FCSTD DOCUMENT  (FreeCAD 1.0R39109 (Git))
Label: boltNodeV2
License: All rights reserved
LicenseURL: http://en.wikipedia.org/wiki/All_rights_reserved
objects: Part::MultiFuse×223, Part::Feature×188, Sketcher::SketchObject×147, Part::FeaturePython×141, Part::Extrusion×117, Part::Cylinder×79, Part::Fillet×47, Part::Cut×44, App::Part×32, Part::Loft×14, Part::Compound×11, Part::MultiCommon×6, Part::Box×4
note: 1168 computed .brp shape members not serialized (recipe doc carries the construction recipe); baked Part::Feature solids carry a one-line shape summary decoded from their .brp

FEATURE [Part::Feature] Part__Feature020  label="Number Plate"
  Placement = pos=(0,-25,0) rot=(1,0,0;1.5708rad)
  shape: bbox 305.2 x 5.066 x 152.8 mm, 1758 faces (baked)
FEATURE [Part::Feature] Part__Feature021  label="Plate"
  shape: bbox 304.8 x 3.048 x 152.4 mm, 26 faces (baked)
FEATURE [App::Part] Assem1  label="backPlate"
  Group = -> [Part__Feature021]
  Origin = -> Origin
  Placement = pos=(20,6.5,1.5) rot=(0,0,1;0rad)
FEATURE [Part::Feature] Part__Feature023  label="COZIR"
  Placement = pos=(5.41029,2.97838,5.56111) rot=(0,0,1;0rad)
  shape: bbox 51.61 x 17 x 50.23 mm, 43 faces (baked)
FEATURE [Part::Feature] Part__Feature024  label="COMPOUND"
  shape: bbox 3.14 x 5 x 10.76 mm, 60 faces, 10 solids (baked)
FEATURE [App::Part] COZIR_Sensor_v2  label="COZIR Sensor v2"
  Group = -> [Part__Feature023,Part__Feature024]
  Origin = -> Origin001
  Placement = pos=(252.5,-22,91) rot=(0,1,0;4.71239rad)
FEATURE [Part::Feature] Part__Feature025  label="Board"
  shape: bbox 25.4 x 25.4 x 1.57 mm, 211 faces (baked)
FEATURE [Part::Feature] Part__Feature026  label="QFN24_4MM"
  Placement = pos=(12.1412,14.4526,1.57) rot=(0,0,1;3.92699rad)
  shape: bbox 5.657 x 5.657 x 0.9 mm, 172 faces (baked)
FEATURE [Part::Feature] Part__Feature027  label="Part 5"
  shape: bbox 0.48 x 0.6603 x 0.6 mm, 14 faces (baked)
FEATURE [Part::Feature] Part__Feature028  label="Part 6"
  shape: bbox 0.48 x 0.6603 x 0.6 mm, 14 faces (baked)
FEATURE [Part::Feature] Part__Feature029  label="Part 4"
  shape: bbox 0.48 x 0.6603 x 0.6 mm, 14 faces (baked)
FEATURE [Part::Feature] Part__Feature030  label="Part 3"
  shape: bbox 0.48 x 0.6603 x 0.6 mm, 14 faces (baked)
FEATURE [Part::Feature] Part__Feature031  label="Part 2"
  shape: bbox 0.48 x 0.6603 x 0.6 mm, 14 faces (baked)
FEATURE [Part::Feature] Part__Feature032  label="Part 1"
  shape: bbox 3 x 1.4 x 1 mm, 10 faces (baked)
FEATURE [Part::Feature] Part__Feature033  label="Pin1"
  shape: bbox 0.6224 x 1.252 x 1.252 mm, 37 faces (baked)
FEATURE [Part::Feature] Part__Feature034  label="Pin2"
  shape: bbox 0.6224 x 1.252 x 1.252 mm, 37 faces (baked)
FEATURE [Part::Feature] Part__Feature035  label="CeramicBody"
  shape: bbox 1.8 x 1.23 x 1.23 mm, 10 faces (baked)
FEATURE [Part::Feature] Part__Feature036  label="0603-NO (1)"
  Placement = pos=(23.241,6.223,1.57) rot=(0,0,1;0rad)
  shape: bbox 1.7 x 0.9 x 0.55 mm, 52 faces, 3 solids (baked)
FEATURE [Part::Feature] Part__Feature037  label="0603-NO (2)"
  Placement = pos=(13.3858,8.4328,1.57) rot=(0,0,1;0rad)
  shape: bbox 1.7 x 0.9 x 0.55 mm, 52 faces, 3 solids (baked)
FEATURE [Part::Feature] Part__Feature038  label="0603-NO (3)"
  Placement = pos=(1.905,18.923,1.57) rot=(0,0,1;3.14159rad)
  shape: bbox 1.7 x 0.9 x 0.55 mm, 52 faces, 3 solids (baked)
FEATURE [Part::Feature] Part__Feature039  label="Pin1 (1)"
  shape: bbox 0.6224 x 1.252 x 1.252 mm, 37 faces (baked)
FEATURE [Part::Feature] Part__Feature040  label="Pin2 (1)"
  shape: bbox 0.6224 x 1.252 x 1.252 mm, 37 faces (baked)
FEATURE [Part::Feature] Part__Feature041  label="CeramicBody (1)"
  shape: bbox 1.8 x 1.23 x 1.23 mm, 10 faces (baked)
FEATURE [Part::Feature] Part__Feature042  label="Pin1 (2)"
  shape: bbox 0.6224 x 1.252 x 1.252 mm, 37 faces (baked)
FEATURE [Part::Feature] Part__Feature043  label="Pin2 (2)"
  shape: bbox 0.6224 x 1.252 x 1.252 mm, 37 faces (baked)
FEATURE [Part::Feature] Part__Feature044  label="CeramicBody (2)"
  shape: bbox 1.8 x 1.23 x 1.23 mm, 10 faces (baked)
FEATURE [Part::Feature] Part__Feature045  label="CHIPLED_0603_NOOUTLINE"
  Placement = pos=(23.368,8.509,1.57) rot=(0,0,1;1.5708rad)
  shape: bbox 1.616 x 0.8 x 0.4 mm, 133 faces (baked)
FEATURE [Part::Feature] Part__Feature046  label="CHIPLED_0603_NOOUTLINE (1)"
  Placement = pos=(1.905,16.764,1.57) rot=(0,0,-1;1.5708rad)
  shape: bbox 1.616 x 0.8 x 0.4 mm, 133 faces (baked)
FEATURE [Part::Feature] Part__Feature047  label="JST_SH4"
  Placement = pos=(22.86,12.7,1.57) rot=(0,0,1;1.5708rad)
  shape: bbox 4.95 x 6 x 2.96 mm, 229 faces, 7 solids (baked)
FEATURE [Part::Feature] Part__Feature048  label="JST_SH4 (1)"
  Placement = pos=(2.54,12.7,1.57) rot=(0,0,-1;1.5708rad)
  shape: bbox 4.95 x 6 x 2.96 mm, 229 faces, 7 solids (baked)
FEATURE [Part::Feature] Part__Feature049  label="NEO3535_REVERSE"
  Placement = pos=(12.7,23.114,0) rot=(0,1,0;3.14159rad)
  shape: bbox 5.88 x 2.8 x 1.78 mm, 41 faces, 5 solids (baked)
FEATURE [Part::Feature] Part__Feature050  label="RESPACK_4X0603"
  Placement = pos=(22.86,18.415,1.57) rot=(0,0,1;3.14159rad)
  shape: bbox 3.2 x 1.6 x 0.61 mm, 172 faces (baked)
FEATURE [Part::Feature] Part__Feature051  label="SOT363"
  Placement = pos=(17.399,12.192,1.57) rot=(0,0,-1;1.5708rad)
  shape: bbox 2.208 x 2.208 x 1.121 mm, 178 faces, 4 solids (baked)
FEATURE [Sketcher::SketchObject] Sketch001
  ArcFitTolerance = 0
  FullyConstrained = true
  MakeInternals = false
  sketch-geometry (39):
    g0: LineSegment StartX=3 StartY=43.5 StartZ=0 EndX=3 EndY=34.5 EndZ=0
    g1: LineSegment StartX=3 StartY=34.5 StartZ=0 EndX=70.5 EndY=34.5 EndZ=0
    g2: LineSegment StartX=3 StartY=43.5 StartZ=0 EndX=10.5 EndY=43.5 EndZ=0
    g3: LineSegment StartX=3 StartY=71 StartZ=0 EndX=10.5 EndY=71 EndZ=0
    g4: LineSegment StartX=3 StartY=71 StartZ=0 EndX=3 EndY=80 EndZ=0
    g5: LineSegment StartX=70.5 StartY=80 StartZ=0 EndX=70.5 EndY=71 EndZ=0
    g6: LineSegment StartX=70.5 StartY=71 StartZ=0 EndX=62.5 EndY=71 EndZ=0
    g7: LineSegment StartX=62.5 StartY=71 StartZ=0 EndX=62.5 EndY=43 EndZ=0
    g8: LineSegment StartX=62.5 StartY=43 StartZ=0 EndX=70.5 EndY=43 EndZ=0
    g9: LineSegment StartX=70.5 StartY=43 StartZ=0 EndX=70.5 EndY=34.5 EndZ=0
    g10: GeomPoint [constr] X=70.5 Y=34.5 Z=0
    g11: GeomPoint [constr] X=70.5 Y=34.5 Z=0
    g12: GeomPoint [constr] X=70.5 Y=34.5 Z=0
    g13: GeomPoint [constr] X=70.5 Y=34.5 Z=0
    g14: GeomPoint [constr] X=70.5 Y=34.5 Z=0
    g15: LineSegment StartX=10.5 StartY=43.5 StartZ=0 EndX=10.5 EndY=71 EndZ=0
    g16: Circle CenterX=7.5 CenterY=75.5 CenterZ=0 NormalX=0 NormalY=0 NormalZ=1 AngleXU=0 Radius=1.6
    g17: Circle CenterX=7.5 CenterY=39 CenterZ=0 NormalX=0 NormalY=0 NormalZ=1 AngleXU=0 Radius=1.6
    g18: Circle CenterX=66.5 CenterY=39 CenterZ=0 NormalX=0 NormalY=0 NormalZ=1 AngleXU=0 Radius=1.6
    g19: Circle CenterX=66.5 CenterY=75.5 CenterZ=0 NormalX=0 NormalY=0 NormalZ=1 AngleXU=0 Radius=1.6
    g20: Circle CenterX=14.2 CenterY=70.46 CenterZ=0 NormalX=0 NormalY=0 NormalZ=1 AngleXU=0 Radius=1.6
    g21: Circle CenterX=38.54 CenterY=77.84 CenterZ=0 NormalX=0 NormalY=0 NormalZ=1 AngleXU=0 Radius=1.6
    g22: Circle CenterX=58.86 CenterY=77.84 CenterZ=0 NormalX=0 NormalY=0 NormalZ=1 AngleXU=0 Radius=1.6
    g23: Circle CenterX=38.54 CenterY=57.52 CenterZ=0 NormalX=0 NormalY=0 NormalZ=1 AngleXU=0 Radius=1.6
    g24: Circle CenterX=58.86 CenterY=57.52 CenterZ=0 NormalX=0 NormalY=0 NormalZ=1 AngleXU=0 Radius=1.6
    g25: Circle CenterX=38.54 CenterY=52.33 CenterZ=0 NormalX=0 NormalY=0 NormalZ=1 AngleXU=0 Radius=1.6
    g26: Circle CenterX=58.86 CenterY=52.33 CenterZ=0 NormalX=0 NormalY=0 NormalZ=1 AngleXU=0 Radius=1.6
    g27: Circle CenterX=38.54 CenterY=39.63 CenterZ=0 NormalX=0 NormalY=0 NormalZ=1 AngleXU=0 Radius=1.6
    g28: Circle CenterX=58.86 CenterY=39.63 CenterZ=0 NormalX=0 NormalY=0 NormalZ=1 AngleXU=0 Radius=1.6
    g29: Circle CenterX=30.43 CenterY=38.46 CenterZ=0 NormalX=0 NormalY=0 NormalZ=1 AngleXU=0 Radius=1.6
    g30: ArcOfCircle CenterX=48.54 CenterY=70.34 CenterZ=0 NormalX=0 NormalY=0 NormalZ=1 AngleXU=0 Radius=5 StartAngle=-9e-16 EndAngle=3.14159
    g31: ArcOfCircle CenterX=48.54 CenterY=42.63 CenterZ=0 NormalX=0 NormalY=0 NormalZ=1 AngleXU=0 Radius=5 StartAngle=3.14159 EndAngle=6.28319
    g32: LineSegment StartX=43.54 StartY=70.34 StartZ=0 EndX=43.54 EndY=42.63 EndZ=0
    g33: LineSegment StartX=53.54 StartY=42.63 StartZ=0 EndX=53.54 EndY=70.34 EndZ=0
    g34: ArcOfCircle CenterX=22.2 CenterY=70.34 CenterZ=0 NormalX=0 NormalY=0 NormalZ=1 AngleXU=0 Radius=5 StartAngle=0 EndAngle=3.14159
    g35: ArcOfCircle CenterX=22.2 CenterY=42.63 CenterZ=0 NormalX=0 NormalY=0 NormalZ=1 AngleXU=0 Radius=5 StartAngle=3.14159 EndAngle=6.28319
    g36: LineSegment StartX=17.2 StartY=70.34 StartZ=0 EndX=17.2 EndY=42.63 EndZ=0
    g37: LineSegment StartX=27.2 StartY=42.63 StartZ=0 EndX=27.2 EndY=70.34 EndZ=0
    g38: LineSegment StartX=3 StartY=80 StartZ=0 EndX=70.5 EndY=80 EndZ=0
  constraints (103):
    c: Vertical(g0)
    c: Coincident(g1,g0)
    c: Horizontal(g1)
    c: Coincident(g2,g0)
    c: Coincident(g4,g3)
    c: Vertical(g4)
    c: Coincident(g6,g5)
    c: Horizontal(g6)
    c: Coincident(g7,g6)
    c: Vertical(g7)
    c: Horizontal(g8)
    c: Horizontal(g2)
    c: Coincident(g10,g9)
    c: Coincident(g11,g1)
    c: Coincident(g12,g9)
    c: Coincident(g13,g1)
    c: Coincident(g14,g9)
    c: Coincident(g9,g1)
    c: Vertical(g9)
    c: Coincident(g15,g2)
    c: Coincident(g15,g3)
    c: Vertical(g15)
    c: Horizontal(g3)
    c: Vertical(g5)
    c: Coincident(g8,g9)
    c: Coincident(g7,g8)
    c: DistanceX(g8,g8) = 8
    c: Radius(g16) = 1.6
    c: DistanceY(g17) = 39
    c: Radius(g17) = 1.6
    c: DistanceX(g18) = 66.5
    c: DistanceY(g17,g18) = 0
    c: Radius(g18) = 1.6
    c: DistanceX(g19,g18) = 0
    c: Radius(g19) = 1.6
    c: DistanceY(g16) = 75.5
    c: DistanceY(g16,g19) = 0
    c: DistanceY(g3,g5) = 0
    c: Radius(g21) = 1.6
    c: DistanceY(g21,g22) = 0
    c: Radius(g22) = 1.6
    c: DistanceX(g21,g22) = 20.32
    c: DistanceX(g23,g21) = 0
    c: Radius(g23) = 1.6
    c: DistanceY(g23,g21) = 20.32
    c: DistanceY(g24,g23) = 0
    c: DistanceX(g24,g22) = 0
    c: Radius(g24) = 1.6
    c: DistanceX(g25,g23) = 0
    c: Radius(g25) = 1.6
    c: DistanceY(g25,g26) = 0
    c: DistanceX(g24,g26) = 0
    c: Radius(g26) = 1.6
    c: DistanceX(g25,g27) = 0
    c: DistanceX(g28,g26) = 0
    c: DistanceY(g27,g25) = 12.7
    c: DistanceY(g28,g27) = 0
    c: Radius(g28) = 1.6
    c: Radius(g27) = 1.6
    c: Radius(g29) = 1.6
    c: DistanceY(g29,g20) = 32
    c: Radius(g20) = 1.6
    c: Tangent(g30,g32) = -1.5708
    c: Tangent(g32,g31) = -1.5708
    c: Tangent(g31,g33) = -1.5708
    c: Tangent(g33,g30) = -1.5708
    c: Equal(g30,g31)
    c: Vertical(g32)
    c: DistanceY(g27,g31) = 3
    c: Radius(g30) = 5
    c: Tangent(g34,g36) = -1.5708
    c: Tangent(g36,g35) = -1.5708
    c: Tangent(g35,g37) = -1.5708
    c: Tangent(g37,g34) = -1.5708
    c: Equal(g34,g35)
    c: Vertical(g36)
    c: Radius(g34) = 5
    c: DistanceY(g34,g30) = 0
    c: DistanceY(g31,g35) = 0
    c: DistanceX(g16,g17) = 0
    c: DistanceX(g0,g3) = 0
    c: Coincident(g38,g4)
    c: Coincident(g38,g5)
    c: Horizontal(g38)
    c: DistanceX(g29) = 30.43
    c: DistanceX(g20) = 14.2
    c: DistanceY(g20) = 70.46
    c: DistanceX(g27) = 38.54
    c: DistanceY(g27) = 39.63
    c: DistanceY(g23) = 57.52
    c: DistanceY(g3,g16) = 4.5
    c: DistanceY(g16,g4) = 4.5
    c: DistanceY(g0,g17) = 4.5
    c: DistanceX(g0,g17) = 4.5
    c: DistanceX(g17) = 7.5
    c: DistanceY(g17,g0) = 4.5
    c: DistanceX(g16,g3) = 3
    c: DistanceX(g19,g5) = 4
    c: DistanceX(g6,g19) = 4
    c: DistanceY(g18,g8) = 4
    c: DistanceX(g25,g31) = 10
    c: DistanceY(g30,g21) = 7.5
    c: DistanceX(g20,g34) = 8
FEATURE [Part::Extrusion] Extrude  label="sensorHold"
  Base = -> Sketch001
  Dir = (0,0,1)
  DirMode = 2
  FaceMakerClass = Part::FaceMakerBullseye
  FaceMakerMode = 3
  LengthFwd = 4
  LengthRev = 0
  Placement = pos=(0,0,16) rot=(0,0,1;0rad)
  Solid = true
  Symmetric = false
FEATURE [Part::Fillet] Fillet002  label="sensorHold001"
  Base = -> Extrude
  EdgeLinks = -> Extrude [Edge1,Edge2,Edge5,Edge8,Edge11,Edge14,Edge17,Edge20,Edge23,Edge26,Edge29,Edge32]
  Edges = 12 edges r=3: [Edge1,Edge2,Edge5,Edge8,Edge11,Edge14,Edge17,Edge20,Edge23,Edge26,Edge29,Edge32]
FEATURE [App::Part] _603_NO  label="0603-NO"
  Group = -> [Part__Feature033,Part__Feature034,Part__Feature035]
  Origin = -> Origin004
  Placement = pos=(16.51,8.382,1.57) rot=(0,0,1;0rad)
FEATURE [App::Part] _6700497  label="36700497"
  Group = -> [Part__Feature027,Part__Feature028,Part__Feature029,Part__Feature030,Part__Feature031,Part__Feature032]
  Origin = -> Origin002
  Placement = pos=(0,0,0) rot=(0,0,1;3.14159rad)
FEATURE [App::Part] SOT23_5  label="SOT23-5"
  Group = -> [_6700497]
  Origin = -> Origin003
  Placement = pos=(2.54,6.985,1.57) rot=(0,0,1;3.14159rad)
FEATURE [App::Part] _805_NO  label="0805-NO"
  Group = -> [Part__Feature039,Part__Feature040,Part__Feature041]
  Origin = -> Origin005
  Placement = pos=(7.874,13.589,1.57) rot=(0,0,1;1.5708rad)
FEATURE [App::Part] _805_NO__1_  label="0805-NO (1)"
  Group = -> [Part__Feature042,Part__Feature043,Part__Feature044]
  Origin = -> Origin006
  Placement = pos=(12.827,6.223,1.57) rot=(0,0,1;3.14159rad)
FEATURE [App::Part] Packages
  Group = -> [Part__Feature026,SOT23_5,_603_NO,Part__Feature036,Part__Feature037,Part__Feature038,_805_NO,_805_NO__1_,Part__Feature045,Part__Feature046,Part__Feature047,Part__Feature048,Part__Feature049,Part__Feature050,Part__Feature051]
  Origin = -> Origin007
FEATURE [App::Part] Adafruit_I2C_QT_Rotary_Encoder_v2  label="gps"
  Group = -> [Part__Feature025,Packages,Sketch001,Extrude,Fillet002]
  Origin = -> Origin008
  Placement = pos=(176,-12,66) rot=(0,0,1;4.71239rad)
FEATURE [Part::Feature] Part__Feature059  label="ips7100"
  Placement = pos=(-24,0,222) rot=(0.999993,-0.003655,0;3.14159rad)
  shape: bbox 48.14 x 14.05 x 44.14 mm, 1935 faces (baked)
FEATURE [Part::Compound] Compound  label="ips7100s"
  Links = -> [Part__Feature059]
  Placement = pos=(226.5,-19,-35) rot=(0,0.707107,0.707107;0.008727rad)
FEATURE [Part::Feature] Part__Feature061  label="CAPC-0805-T0.95-BN v004"
  Placement = pos=(-5.48627,2.66154,1.6) rot=(0,0,-1;1.5708rad)
  shape: bbox 1.35 x 2.1 x 0.95 mm, 42 faces (baked)
FEATURE [Part::Feature] Part__Feature062  label="CAPC-0805-T0.95-BN v005"
  Placement = pos=(-3.43627,2.66154,1.6) rot=(0,0,-1;1.5708rad)
  shape: bbox 1.35 x 2.1 x 0.95 mm, 42 faces (baked)
FEATURE [Part::Feature] Part__Feature063  label="CAPC-0603-T0.9-BN v002"
  Placement = pos=(-1.69987,-3.28475,1.6) rot=(0,0,1;0rad)
  shape: bbox 1.7 x 0.9 x 0.9 mm, 42 faces (baked)
FEATURE [Part::Feature] Part__Feature064  label="BODY_MF06A001"
  Placement = pos=(0,0,0.762) rot=(0.57735,-0.57735,-0.57735;2.0944rad)
  shape: bbox 1.601 x 2.921 x 1.016 mm, 42 faces (baked)
FEATURE [Part::Feature] Part__Feature065  label="LEAD_MF06A006"
  Placement = pos=(-0.9652,-0.9525,0.1016) rot=(0.57735,-0.57735,-0.57735;2.0944rad)
  shape: bbox 0.6223 x 0.3749 x 0.8636 mm, 14 faces (baked)
FEATURE [Part::Feature] Part__Feature066  label="LEAD_MF06A007"
  Placement = pos=(-0.9652,0,0.1016) rot=(0.57735,-0.57735,-0.57735;2.0944rad)
  shape: bbox 0.6223 x 0.3749 x 0.8636 mm, 14 faces (baked)
FEATURE [Part::Feature] Part__Feature067  label="LEAD_MF06A008"
  Placement = pos=(-0.9652,0.9525,0.1016) rot=(0.57735,-0.57735,-0.57735;2.0944rad)
  shape: bbox 0.6223 x 0.3749 x 0.8636 mm, 14 faces (baked)
FEATURE [Part::Feature] Part__Feature068  label="LEAD_MF06A009"
  Placement = pos=(0.9652,-0.9525,0.1016) rot=(0.57735,0.57735,0.57735;2.0944rad)
  shape: bbox 0.6223 x 0.3749 x 0.8636 mm, 14 faces (baked)
FEATURE [Part::Feature] Part__Feature069  label="LEAD_MF06A010"
  Placement = pos=(0.9652,0,0.1016) rot=(0.57735,0.57735,0.57735;2.0944rad)
  shape: bbox 0.6223 x 0.3749 x 0.8636 mm, 14 faces (baked)
FEATURE [Part::Feature] Part__Feature070  label="LEAD_MF06A011"
  Placement = pos=(0.9652,0.9525,0.1016) rot=(0.57735,0.57735,0.57735;2.0944rad)
  shape: bbox 0.6223 x 0.3749 x 0.8636 mm, 14 faces (baked)
FEATURE [Part::Feature] Part__Feature071  label="SOT363 v003"
  Placement = pos=(4.97054,-0.645171,1.675) rot=(0,0,1;3.14159rad)
  shape: bbox 2.1 x 2 x 1.1 mm, 94 faces, 7 solids (baked)
FEATURE [Part::Feature] Part__Feature072  label="LED 0603 single color v002"
  Placement = pos=(-9.18406,3.72778,1.60762) rot=(0,0,1;1.5708rad)
  shape: bbox 1.961 x 0.7932 x 0.7145 mm, 63 faces, 5 solids (baked)
FEATURE [Part::Feature] Part__Feature073  label="RESC-0603 v003"
  Placement = pos=(4.83432,-3.67461,1.6) rot=(0,0,1;0rad)
  shape: bbox 1.7 x 0.9 x 0.55 mm, 52 faces, 3 solids (baked)
FEATURE [Part::Feature] Part__Feature074  label="RESC-0603 v004"
  Placement = pos=(-7.14949,3.61248,1.6) rot=(0,0,-1;1.5708rad)
  shape: bbox 0.9 x 1.7 x 0.55 mm, 52 faces, 3 solids (baked)
FEATURE [Part::Feature] Part__Feature075  label="Printed Circuit Board001"
  shape: bbox 25.4 x 17.78 x 1.6 mm, 42 faces (baked)
FEATURE [Part::Feature] Part__Feature076  label="EAHC2835WD007"
  shape: bbox 3.513 x 2.813 x 0.7485 mm, 108 faces, 4 solids (baked)
FEATURE [Part::Feature] Part__Feature077  label="AS7341 v003"
  Placement = pos=(0,-0.339822,1.6) rot=(0,0,1;0rad)
  shape: bbox 2 x 3.1 x 1.1 mm, 267 faces, 26 solids (baked)
FEATURE [Part::Feature] Part__Feature078  label="CAPC-0805-T0.95-BN v006"
  Placement = pos=(-5.01759,-3.15294,1.6) rot=(0,0,1;0rad)
  shape: bbox 2.1 x 1.35 x 0.95 mm, 42 faces (baked)
FEATURE [Part::Feature] Part__Feature079  label="YC164_RESPACK v002"
  Placement = pos=(2.99591,1.52916,1.6) rot=(0,0,1;0rad)
  shape: bbox 3.2 x 1.6 x 0.61 mm, 172 faces (baked)
FEATURE [Part::Feature] Part__Feature080  label="qwicc v004"
  Placement = pos=(-10.8364,0.0607456,1.65) rot=(0,0,-1;1.5708rad)
  shape: bbox 4.95 x 6 x 2.96 mm, 229 faces, 7 solids (baked)
FEATURE [Part::Feature] Part__Feature081  label="qwicc v005"
  Placement = pos=(10.8256,0.00556102,1.65) rot=(0,0,1;1.5708rad)
  shape: bbox 4.95 x 6 x 2.96 mm, 229 faces, 7 solids (baked)
FEATURE [App::Part] sot_23_6_v003  label="sot-23-6 v003"
  Group = -> [Part__Feature064,Part__Feature065,Part__Feature066,Part__Feature067,Part__Feature068,Part__Feature069,Part__Feature070]
  Origin = -> Origin011
  Placement = pos=(-4.47945,-0.603742,1.69152) rot=(0,0,1;0rad)
FEATURE [App::Part] Adafruit_AS7341_STEMMA_QT_v003  label="TMP 117"
  Group = -> [Part__Feature075,Part__Feature076,Part__Feature077,Part__Feature078,Part__Feature061,Part__Feature062,Part__Feature063,sot_23_6_v003,Part__Feature071,Part__Feature072,Part__Feature073,Part__Feature074,Part__Feature079,Part__Feature080,Part__Feature081]
  Origin = -> Origin012
  Placement = pos=(225.25,-10,30) rot=(0.57735,0.57735,-0.57735;2.0944rad)
FEATURE [Part::Feature] Part__Feature082  label="Printed Circuit Board002"
  shape: bbox 25.4 x 22.86 x 1.65 mm, 56 faces (baked)
FEATURE [Part::Feature] Part__Feature083  label="BNO055-9axis-IMU v2"
  shape: bbox 5.2 x 3.8 x 1.18 mm, 330 faces, 31 solids (baked)
FEATURE [Part::Feature] Part__Feature084  label="BNO085-9axis-IMU v1"
  Placement = pos=(0.0397428,0.834599,1.65) rot=(0,0,1;0rad)
  shape: bbox 5.2 x 3.8 x 1.18 mm, 330 faces, 31 solids (baked)
FEATURE [Part::Feature] Part__Feature085  label="BODY-TSSOP"
  Placement = pos=(0,0,0.68) rot=(1,0,0;1.5708rad)
  shape: bbox 4.4 x 5 x 1 mm, 44 faces (baked)
FEATURE [Part::Feature] Part__Feature086  label="LEAD-TSSOP"
  Placement = pos=(-2.575,2.275,0.25) rot=(0.57735,-0.57735,-0.57735;2.0944rad)
  shape: bbox 1 x 0.245 x 0.68 mm, 14 faces (baked)
FEATURE [Part::Feature] Part__Feature087  label="LEAD-TSSOP001"
  Placement = pos=(-2.575,1.625,0.25) rot=(0.57735,-0.57735,-0.57735;2.0944rad)
  shape: bbox 1 x 0.245 x 0.68 mm, 14 faces (baked)
FEATURE [Part::Feature] Part__Feature088  label="LEAD-TSSOP002"
  Placement = pos=(-2.575,0.975,0.25) rot=(0.57735,-0.57735,-0.57735;2.0944rad)
  shape: bbox 1 x 0.245 x 0.68 mm, 14 faces (baked)
FEATURE [Part::Feature] Part__Feature089  label="LEAD-TSSOP003"
  Placement = pos=(-2.575,0.325,0.25) rot=(0.57735,-0.57735,-0.57735;2.0944rad)
  shape: bbox 1 x 0.245 x 0.68 mm, 14 faces (baked)
FEATURE [Part::Feature] Part__Feature090  label="LEAD-TSSOP004"
  Placement = pos=(-2.575,-0.325,0.25) rot=(0.57735,-0.57735,-0.57735;2.0944rad)
  shape: bbox 1 x 0.245 x 0.68 mm, 14 faces (baked)
FEATURE [Part::Feature] Part__Feature091  label="LEAD-TSSOP005"
  Placement = pos=(-2.575,-0.975,0.25) rot=(0.57735,-0.57735,-0.57735;2.0944rad)
  shape: bbox 1 x 0.245 x 0.68 mm, 14 faces (baked)
FEATURE [Part::Feature] Part__Feature092  label="LEAD-TSSOP006"
  Placement = pos=(-2.575,-1.625,0.25) rot=(0.57735,-0.57735,-0.57735;2.0944rad)
  shape: bbox 1 x 0.245 x 0.68 mm, 14 faces (baked)
FEATURE [Part::Feature] Part__Feature093  label="LEAD-TSSOP007"
  Placement = pos=(-2.575,-2.275,0.25) rot=(0.57735,-0.57735,-0.57735;2.0944rad)
  shape: bbox 1 x 0.245 x 0.68 mm, 14 faces (baked)
FEATURE [Part::Feature] Part__Feature094  label="LEAD-TSSOP008"
  Placement = pos=(2.575,-2.275,0.25) rot=(0.57735,0.57735,0.57735;2.0944rad)
  shape: bbox 1 x 0.245 x 0.68 mm, 14 faces (baked)
FEATURE [Part::Feature] Part__Feature095  label="LEAD-TSSOP009"
  Placement = pos=(2.575,-1.625,0.25) rot=(0.57735,0.57735,0.57735;2.0944rad)
  shape: bbox 1 x 0.245 x 0.68 mm, 14 faces (baked)
FEATURE [Part::Feature] Part__Feature096  label="LEAD-TSSOP010"
  Placement = pos=(2.575,-0.975,0.25) rot=(0.57735,0.57735,0.57735;2.0944rad)
  shape: bbox 1 x 0.245 x 0.68 mm, 14 faces (baked)
FEATURE [Part::Feature] Part__Feature097  label="LEAD-TSSOP011"
  Placement = pos=(2.575,-0.325,0.25) rot=(0.57735,0.57735,0.57735;2.0944rad)
  shape: bbox 1 x 0.245 x 0.68 mm, 14 faces (baked)
FEATURE [Part::Feature] Part__Feature098  label="LEAD-TSSOP012"
  Placement = pos=(2.575,0.325,0.25) rot=(0.57735,0.57735,0.57735;2.0944rad)
  shape: bbox 1 x 0.245 x 0.68 mm, 14 faces (baked)
FEATURE [Part::Feature] Part__Feature099  label="LEAD-TSSOP013"
  Placement = pos=(2.575,0.975,0.25) rot=(0.57735,0.57735,0.57735;2.0944rad)
  shape: bbox 1 x 0.245 x 0.68 mm, 14 faces (baked)
FEATURE [Part::Feature] Part__Feature100  label="LEAD-TSSOP014"
  Placement = pos=(2.575,1.625,0.25) rot=(0.57735,0.57735,0.57735;2.0944rad)
  shape: bbox 1 x 0.245 x 0.68 mm, 14 faces (baked)
FEATURE [Part::Feature] Part__Feature101  label="LEAD-TSSOP015"
  Placement = pos=(2.575,2.275,0.25) rot=(0.57735,0.57735,0.57735;2.0944rad)
  shape: bbox 1 x 0.245 x 0.68 mm, 14 faces (baked)
FEATURE [App::Part] CD74HC4050PW_v2  label="CD74HC4050PW v2"
  Group = -> [Part__Feature085,Part__Feature086,Part__Feature087,Part__Feature088,Part__Feature089,Part__Feature090,Part__Feature091,Part__Feature092,Part__Feature093,Part__Feature094,Part__Feature095,Part__Feature096,Part__Feature097,Part__Feature098,Part__Feature099,Part__Feature100,Part__Feature101]
  Origin = -> Origin013
  Placement = pos=(-0.480857,-4.04007,1.65) rot=(0,0,1;0rad)
FEATURE [Part::Feature] Part__Feature102  label="Crystal_XTAL3215_32.768KHz v2"
  Placement = pos=(-1.27195,4.88696,1.65) rot=(0,0,1;0rad)
  shape: bbox 3.2 x 1.5 x 0.9 mm, 68 faces, 4 solids (baked)
FEATURE [Part::Feature] Part__Feature103  label="SOT23-5 v1"
  Placement = pos=(-6.713,-5.17721,1.62965) rot=(0,0,1;3.14159rad)
  shape: bbox 2.839 x 3.004 x 1.189 mm, 69 faces, 6 solids (baked)
FEATURE [Part::Feature] Part__Feature104  label="BSS138PS v2"
  Placement = pos=(8.84171,4.56758,1.725) rot=(0,0,1;1.5708rad)
  shape: bbox 2 x 2.1 x 1.1 mm, 94 faces, 7 solids (baked)
FEATURE [Part::Feature] Part__Feature105  label="LED 0603 single color v003"
  Placement = pos=(-11.1101,4.07892,1.65762) rot=(0,0,1;1.5708rad)
  shape: bbox 1.961 x 0.7932 x 0.7145 mm, 63 faces, 5 solids (baked)
FEATURE [Part::Feature] Part__Feature106  label="CAPC-0805-T0.95-BN v007"
  Placement = pos=(-5.76735,-1.60636,1.65) rot=(0,0,1;1.5708rad)
  shape: bbox 1.35 x 2.1 x 0.95 mm, 42 faces (baked)
FEATURE [Part::Feature] Part__Feature107  label="CAPC-0805-T0.95-BN v008"
  Placement = pos=(-9.58996,-4.86923,1.65) rot=(0,0,1;1.5708rad)
  shape: bbox 1.35 x 2.1 x 0.95 mm, 42 faces (baked)
FEATURE [Part::Feature] Part__Feature108  label="CAPC-0603-T0.9-BN v003"
  Placement = pos=(-3.91817,4.74576,1.65) rot=(0,0,-1;1.5708rad)
  shape: bbox 0.9 x 1.7 x 0.9 mm, 42 faces (baked)
FEATURE [Part::Feature] Part__Feature109  label="CAPC-0603-T0.9-BN v004"
  Placement = pos=(1.38535,4.40519,1.65) rot=(0,0,-1;1.5708rad)
  shape: bbox 0.9 x 1.7 x 0.9 mm, 42 faces (baked)
FEATURE [Part::Feature] Part__Feature110  label="CAPC-0603-T0.9-BN v005"
  Placement = pos=(11.4254,5.18954,1.65) rot=(0,0,-1;1.5708rad)
  shape: bbox 0.9 x 1.7 x 0.9 mm, 42 faces (baked)
FEATURE [Part::Feature] Part__Feature111  label="CAPC-0603-T0.9-BN v006"
  Placement = pos=(-5.1728,2.29973,1.65) rot=(0,0,1;0rad)
  shape: bbox 1.7 x 0.9 x 0.9 mm, 42 faces (baked)
FEATURE [Part::Feature] Part__Feature112  label="CAPC-0603-T0.9-BN v007"
  Placement = pos=(-5.03492,0.984521,1.65) rot=(0,0,1;0rad)
  shape: bbox 1.7 x 0.9 x 0.9 mm, 42 faces (baked)
FEATURE [Part::Feature] Part__Feature113  label="YC164_RESPACK v003"
  Placement = pos=(-4.85646,5.94433,1.65) rot=(0,0,1;3.14159rad)
  shape: bbox 3.2 x 1.6 x 0.61 mm, 172 faces (baked)
FEATURE [Part::Feature] Part__Feature114  label="YC164_RESPACK v004"
  Placement = pos=(3.72877,3.34539,1.65) rot=(0,0,1;0rad)
  shape: bbox 3.2 x 1.6 x 0.61 mm, 172 faces (baked)
FEATURE [Part::Feature] Part__Feature115  label="YC164_RESPACK v005"
  Placement = pos=(4.16527,1.97253,1.65) rot=(0,0,-1;1.5708rad)
  shape: bbox 1.6 x 3.2 x 0.61 mm, 172 faces (baked)
FEATURE [Part::Feature] Part__Feature116  label="qwicc v1"
  Placement = pos=(-8.45735,0.0215083,1.345) rot=(0.57735,-0.57735,-0.57735;2.0944rad)
  shape: bbox 4.95 x 6 x 2.96 mm, 229 faces, 7 solids (baked)
FEATURE [Part::Feature] Part__Feature117  label="qwicc v006"
  Placement = pos=(8.46074,0.018239,1.345) rot=(0.57735,0.57735,0.57735;2.0944rad)
  shape: bbox 4.95 x 6 x 2.96 mm, 229 faces, 7 solids (baked)
FEATURE [App::Part] Adafruit_BNO085_STEMMA_QT_v2  label="BNO085"
  Group = -> [Part__Feature082,Part__Feature083,Part__Feature084,CD74HC4050PW_v2,Part__Feature102,Part__Feature103,Part__Feature104,Part__Feature105,Part__Feature106,Part__Feature107,Part__Feature108,Part__Feature109,Part__Feature110,Part__Feature111,Part__Feature112,Part__Feature113,Part__Feature114,Part__Feature115,Part__Feature116,Part__Feature117]
  Origin = -> Origin014
  Placement = pos=(217,-24.7,66) rot=(0,0,-1;1.5708rad)
FEATURE [Part::Feature] Part__Feature  label=" backPlateLargeBorder"
  Placement = pos=(0,3,0) rot=(0,0,1;0rad)
  shape: bbox 311.2 x 1.905 x 158.8 mm, 97 faces (baked)
FEATURE [Part::Box] Box  label="batteryPlus"
  AttacherType = Attacher::AttachEngine3D
  Height = 11
  Length = 68
  Placement = pos=(139,-4,-25) rot=(0.57735,-0.57735,0.57735;2.0944rad)
  Width = 56
FEATURE [Sketcher::SketchObject] Sketch037
  ArcFitTolerance = 0
  FullyConstrained = true
  MakeInternals = false
  Placement = pos=(0,0,-41.5) rot=(0,0,1;0rad)
  sketch-geometry (8):
    g0: LineSegment StartX=158.5 StartY=-4 StartZ=0 EndX=169.5 EndY=-4 EndZ=0
    g1: LineSegment StartX=169.5 StartY=-4 StartZ=0 EndX=169.5 EndY=-14 EndZ=0
    g2: LineSegment StartX=169.5 StartY=-14 StartZ=0 EndX=158.5 EndY=-14 EndZ=0
    g3: LineSegment StartX=158.5 StartY=-14 StartZ=0 EndX=158.5 EndY=-4 EndZ=0
    g4: LineSegment StartX=235.5 StartY=-4 StartZ=0 EndX=246.5 EndY=-4 EndZ=0
    g5: LineSegment StartX=246.5 StartY=-4 StartZ=0 EndX=246.5 EndY=-14 EndZ=0
    g6: LineSegment StartX=246.5 StartY=-14 StartZ=0 EndX=235.5 EndY=-14 EndZ=0
    g7: LineSegment StartX=235.5 StartY=-14 StartZ=0 EndX=235.5 EndY=-4 EndZ=0
  constraints (24):
    c: Coincident(g0,g1)
    c: Coincident(g1,g2)
    c: Coincident(g2,g3)
    c: Coincident(g3,g0)
    c: Horizontal(g0)
    c: Horizontal(g2)
    c: Vertical(g1)
    c: Vertical(g3)
    c: Coincident(g4,g5)
    c: Coincident(g5,g6)
    c: Coincident(g6,g7)
    c: Coincident(g7,g4)
    c: Horizontal(g4)
    c: Horizontal(g6)
    c: Vertical(g5)
    c: Vertical(g7)
    c: DistanceY(g0) = -4
    c: DistanceX(g0) = 158.5
    c: DistanceY(g2,g0) = 10
    c: DistanceX(g2,g1) = 11
    c: DistanceY(g4,g0) = 0
    c: DistanceX(g6,g5) = 11
    c: DistanceY(g1,g6) = 0
    c: DistanceX(g6) = 235.5
FEATURE [Part::Extrusion] Extrude003
  Base = -> Sketch037
  Dir = (0,0,1)
  DirMode = 2
  FaceMakerClass = Part::FaceMakerBullseye
  FaceMakerMode = 3
  LengthFwd = 121.5
  LengthRev = 0
  Solid = true
  Symmetric = false
FEATURE [Part::Fillet] Fillet  label="srsHold"
  Base = -> Extrude003
  EdgeLinks = -> Extrude003 [Edge5,Edge8,Edge9,Edge10,Edge17,Edge20,Edge21,Edge22]
  Edges = 8 edges r=5: [Edge5,Edge8,Edge9,Edge10,Edge17,Edge20,Edge21,Edge22]
FEATURE [Sketcher::SketchObject] Sketch044  label="innerSRS004"
  ArcFitTolerance = 0
  FullyConstrained = true
  MakeInternals = false
  Placement = pos=(0,0,-65) rot=(0,0,1;0rad)
  sketch-geometry (12):
    g0: ArcOfCircle CenterX=180.5 CenterY=-32 CenterZ=0 NormalX=0 NormalY=0 NormalZ=1 AngleXU=0 Radius=10 StartAngle=3.14159 EndAngle=4.71239
    g1: ArcOfCircle CenterX=224.5 CenterY=-32 CenterZ=0 NormalX=0 NormalY=0 NormalZ=1 AngleXU=0 Radius=10 StartAngle=4.71239 EndAngle=6.28319
    g2: LineSegment StartX=170.5 StartY=-32 StartZ=0 EndX=170.5 EndY=0 EndZ=0
    g3: LineSegment StartX=234.5 StartY=0 StartZ=0 EndX=234.5 EndY=-32 EndZ=0
    g4: LineSegment StartX=180.5 StartY=-42 StartZ=0 EndX=224.5 EndY=-42 EndZ=0
    g5: LineSegment StartX=167.5 StartY=0 StartZ=0 EndX=167.5 EndY=-32 EndZ=0
    g6: LineSegment StartX=180.5 StartY=-45 StartZ=0 EndX=224.5 EndY=-45 EndZ=0
    g7: LineSegment StartX=237.5 StartY=0 StartZ=0 EndX=237.5 EndY=-32 EndZ=0
    g8: ArcOfCircle CenterX=180.5 CenterY=-32 CenterZ=0 NormalX=0 NormalY=0 NormalZ=1 AngleXU=0 Radius=13 StartAngle=3.14159 EndAngle=4.71239
    g9: ArcOfCircle CenterX=224.5 CenterY=-32 CenterZ=0 NormalX=0 NormalY=0 NormalZ=1 AngleXU=0 Radius=13 StartAngle=4.71239 EndAngle=6.28319
    g10: LineSegment StartX=167.5 StartY=0 StartZ=0 EndX=170.5 EndY=0 EndZ=0
    g11: LineSegment StartX=234.5 StartY=0 StartZ=0 EndX=237.5 EndY=0 EndZ=0
  constraints (40):
    c: Angle(g1) = 1.5708
    c: DistanceY(g1,g1) = 0
    c: DistanceY(g1,g0) = 0
    c: Angle(g0) = 1.5708
    c: DistanceX(g0,g0) = 10
    c: DistanceY(g0,g0) = 0
    c: DistanceX(g1,g1) = 10
    c: Coincident(g2,g0)
    c: Vertical(g2)
    c: PointOnObject(g3,g-1)
    c: Coincident(g3,g1)
    c: Vertical(g3)
    c: DistanceY(g2,g2) = 32
    c: Coincident(g4,g1)
    c: PointOnObject(g5,g-1)
    c: Vertical(g5)
    c: Horizontal(g6)
    c: Vertical(g7)
    c: DistanceX(g5,g2) = 3
    c: DistanceX(g3,g7) = 3
    c: DistanceY(g5,g0) = 0
    c: DistanceY(g7,g1) = 0
    c: DistanceY(g7,g3) = 0
    c: DistanceX(g2,g3) = 64
    c: DistanceX(g0,g6) = 0
    c: DistanceX(g6,g1) = 0
    c: DistanceY(g2) = 0
    c: Coincident(g5,g8)
    c: Coincident(g6,g8)
    c: DistanceY(g6,g0) = 3
    c: Coincident(g6,g9)
    c: Coincident(g7,g9)
    c: Angle(g8) = 1.5708
    c: Angle(g9) = 1.5708
    c: Coincident(g10,g5)
    c: Coincident(g10,g2)
    c: Coincident(g11,g3)
    c: Coincident(g11,g7)
    c: Coincident(g0,g4)
    c: DistanceX(g2) = 170.5
FEATURE [Sketcher::SketchObject] Sketch045  label="outerSRS004"
  ArcFitTolerance = 0
  FullyConstrained = true
  MakeInternals = false
  Placement = pos=(0,0,-80) rot=(0,0,1;0rad)
  sketch-geometry (12):
    g0: ArcOfCircle CenterX=180.5 CenterY=-32 CenterZ=0 NormalX=0 NormalY=0 NormalZ=1 AngleXU=0 Radius=20 StartAngle=3.14159 EndAngle=4.71239
    g1: ArcOfCircle CenterX=224.5 CenterY=-32 CenterZ=0 NormalX=0 NormalY=0 NormalZ=1 AngleXU=0 Radius=20 StartAngle=4.71239 EndAngle=6.28319
    g2: LineSegment StartX=160.5 StartY=-32 StartZ=0 EndX=160.5 EndY=0 EndZ=0
    g3: LineSegment StartX=244.5 StartY=0 StartZ=0 EndX=244.5 EndY=-32 EndZ=0
    g4: LineSegment StartX=180.5 StartY=-52 StartZ=0 EndX=224.5 EndY=-52 EndZ=0
    g5: LineSegment StartX=157.5 StartY=0 StartZ=0 EndX=157.5 EndY=-32 EndZ=0
    g6: LineSegment StartX=180.5 StartY=-55 StartZ=0 EndX=224.5 EndY=-55 EndZ=0
    g7: LineSegment StartX=247.5 StartY=0 StartZ=0 EndX=247.5 EndY=-32 EndZ=0
    g8: ArcOfCircle CenterX=180.5 CenterY=-32 CenterZ=0 NormalX=0 NormalY=0 NormalZ=1 AngleXU=0 Radius=23 StartAngle=3.14159 EndAngle=4.71239
    g9: ArcOfCircle CenterX=224.5 CenterY=-32 CenterZ=0 NormalX=0 NormalY=0 NormalZ=1 AngleXU=0 Radius=23 StartAngle=4.71239 EndAngle=6.28319
    g10: LineSegment StartX=157.5 StartY=0 StartZ=0 EndX=160.5 EndY=0 EndZ=0
    g11: LineSegment StartX=244.5 StartY=0 StartZ=0 EndX=247.5 EndY=0 EndZ=0
  constraints (40):
    c: Angle(g1) = 1.5708
    c: DistanceY(g1,g0) = 0
    c: Angle(g0) = 1.5708
    c: DistanceY(g0,g0) = 0
    c: Coincident(g2,g0)
    c: Vertical(g2)
    c: PointOnObject(g3,g-1)
    c: Coincident(g3,g1)
    c: Vertical(g3)
    c: DistanceY(g2,g2) = 32
    c: Coincident(g4,g1)
    c: PointOnObject(g5,g-1)
    c: Vertical(g5)
    c: Horizontal(g6)
    c: Vertical(g7)
    c: DistanceX(g5,g2) = 3
    c: DistanceX(g3,g7) = 3
    c: DistanceY(g5,g0) = 0
    c: DistanceY(g7,g1) = 0
    c: DistanceY(g7,g3) = 0
    c: DistanceX(g2) = 160.5
    c: DistanceX(g2,g3) = 84
    c: DistanceX(g0,g6) = 0
    c: DistanceX(g6,g1) = 0
    c: DistanceY(g2) = 0
    c: Coincident(g5,g8)
    c: Coincident(g6,g8)
    c: DistanceY(g6,g0) = 3
    c: Coincident(g6,g9)
    c: Coincident(g7,g9)
    c: Angle(g8) = 1.5708
    c: Angle(g9) = 1.5708
    c: Coincident(g10,g5)
    c: Coincident(g10,g2)
    c: Coincident(g11,g3)
    c: Coincident(g11,g7)
    c: DistanceY(g0,g0) = 20
    c: Coincident(g0,g4)
    c: DistanceY(g1,g0) = 0
    c: DistanceY(g1,g1) = 0
FEATURE [Part::Loft] Loft004  label="srs005"
  Closed = false
  MaxDegree = 5
  Ruled = false
  Sections = -> [Sketch044,Sketch045]
  Solid = true
FEATURE [Part::Fillet] Fillet007  label="srsCovers004"
  Base = -> Loft004
  EdgeLinks = -> Loft004 [Edge1,Edge3,Edge5,Edge7,Edge8,Edge10,Edge11,Edge13,Edge14,Edge16,Edge17,Edge19,Edge20,Edge22,Edge23,Edge25,Edge26,Edge28,Edge29,Edge31,Edge32,Edge34,Edge35,Edge36]
  Edges = 24 edges r=1: [Edge1,Edge3,Edge5,Edge7,Edge8,Edge10,Edge11,Edge13,Edge14,Edge16,Edge17,Edge19,Edge20,Edge22,Edge23,Edge25,Edge26,Edge28,Edge29,Edge31,Edge32,Edge34,Edge35,Edge36]
  Placement = pos=(0,0,38.67) rot=(0,0,1;0rad)
FEATURE [Sketcher::SketchObject] Sketch046  label="innerSRS005"
  ArcFitTolerance = 0
  FullyConstrained = true
  MakeInternals = false
  Placement = pos=(0,0,-65) rot=(0,0,1;0rad)
  sketch-geometry (12):
    g0: ArcOfCircle CenterX=180.5 CenterY=-32 CenterZ=0 NormalX=0 NormalY=0 NormalZ=1 AngleXU=0 Radius=10 StartAngle=3.14159 EndAngle=4.71239
    g1: ArcOfCircle CenterX=224.5 CenterY=-32 CenterZ=0 NormalX=0 NormalY=0 NormalZ=1 AngleXU=0 Radius=10 StartAngle=4.71239 EndAngle=6.28319
    g2: LineSegment StartX=170.5 StartY=-32 StartZ=0 EndX=170.5 EndY=0 EndZ=0
    g3: LineSegment StartX=234.5 StartY=0 StartZ=0 EndX=234.5 EndY=-32 EndZ=0
    g4: LineSegment StartX=180.5 StartY=-42 StartZ=0 EndX=224.5 EndY=-42 EndZ=0
    g5: LineSegment StartX=167.5 StartY=0 StartZ=0 EndX=167.5 EndY=-32 EndZ=0
    g6: LineSegment StartX=180.5 StartY=-45 StartZ=0 EndX=224.5 EndY=-45 EndZ=0
    g7: LineSegment StartX=237.5 StartY=0 StartZ=0 EndX=237.5 EndY=-32 EndZ=0
    g8: ArcOfCircle CenterX=180.5 CenterY=-32 CenterZ=0 NormalX=0 NormalY=0 NormalZ=1 AngleXU=0 Radius=13 StartAngle=3.14159 EndAngle=4.71239
    g9: ArcOfCircle CenterX=224.5 CenterY=-32 CenterZ=0 NormalX=0 NormalY=0 NormalZ=1 AngleXU=0 Radius=13 StartAngle=4.71239 EndAngle=6.28319
    g10: LineSegment StartX=167.5 StartY=0 StartZ=0 EndX=170.5 EndY=0 EndZ=0
    g11: LineSegment StartX=234.5 StartY=0 StartZ=0 EndX=237.5 EndY=0 EndZ=0
  constraints (40):
    c: Angle(g1) = 1.5708
    c: DistanceY(g1,g1) = 0
    c: DistanceY(g1,g0) = 0
    c: Angle(g0) = 1.5708
    c: DistanceX(g0,g0) = 10
    c: DistanceY(g0,g0) = 0
    c: DistanceX(g1,g1) = 10
    c: Coincident(g2,g0)
    c: Vertical(g2)
    c: PointOnObject(g3,g-1)
    c: Coincident(g3,g1)
    c: Vertical(g3)
    c: DistanceY(g2,g2) = 32
    c: Coincident(g4,g1)
    c: PointOnObject(g5,g-1)
    c: Vertical(g5)
    c: Horizontal(g6)
    c: Vertical(g7)
    c: DistanceX(g5,g2) = 3
    c: DistanceX(g3,g7) = 3
    c: DistanceY(g5,g0) = 0
    c: DistanceY(g7,g1) = 0
    c: DistanceY(g7,g3) = 0
    c: DistanceX(g2,g3) = 64
    c: DistanceX(g0,g6) = 0
    c: DistanceX(g6,g1) = 0
    c: DistanceY(g2) = 0
    c: Coincident(g5,g8)
    c: Coincident(g6,g8)
    c: DistanceY(g6,g0) = 3
    c: Coincident(g6,g9)
    c: Coincident(g7,g9)
    c: Angle(g8) = 1.5708
    c: Angle(g9) = 1.5708
    c: Coincident(g10,g5)
    c: Coincident(g10,g2)
    c: Coincident(g11,g3)
    c: Coincident(g11,g7)
    c: Coincident(g0,g4)
    c: DistanceX(g2) = 170.5
FEATURE [Sketcher::SketchObject] Sketch047  label="outerSRS005"
  ArcFitTolerance = 0
  FullyConstrained = true
  MakeInternals = false
  Placement = pos=(0,0,-80) rot=(0,0,1;0rad)
  sketch-geometry (12):
    g0: ArcOfCircle CenterX=180.5 CenterY=-32 CenterZ=0 NormalX=0 NormalY=0 NormalZ=1 AngleXU=0 Radius=20 StartAngle=3.14159 EndAngle=4.71239
    g1: ArcOfCircle CenterX=224.5 CenterY=-32 CenterZ=0 NormalX=0 NormalY=0 NormalZ=1 AngleXU=0 Radius=20 StartAngle=4.71239 EndAngle=6.28319
    g2: LineSegment StartX=160.5 StartY=-32 StartZ=0 EndX=160.5 EndY=0 EndZ=0
    g3: LineSegment StartX=244.5 StartY=0 StartZ=0 EndX=244.5 EndY=-32 EndZ=0
    g4: LineSegment StartX=180.5 StartY=-52 StartZ=0 EndX=224.5 EndY=-52 EndZ=0
    g5: LineSegment StartX=157.5 StartY=0 StartZ=0 EndX=157.5 EndY=-32 EndZ=0
    g6: LineSegment StartX=180.5 StartY=-55 StartZ=0 EndX=224.5 EndY=-55 EndZ=0
    g7: LineSegment StartX=247.5 StartY=0 StartZ=0 EndX=247.5 EndY=-32 EndZ=0
    g8: ArcOfCircle CenterX=180.5 CenterY=-32 CenterZ=0 NormalX=0 NormalY=0 NormalZ=1 AngleXU=0 Radius=23 StartAngle=3.14159 EndAngle=4.71239
    g9: ArcOfCircle CenterX=224.5 CenterY=-32 CenterZ=0 NormalX=0 NormalY=0 NormalZ=1 AngleXU=0 Radius=23 StartAngle=4.71239 EndAngle=6.28319
    g10: LineSegment StartX=157.5 StartY=0 StartZ=0 EndX=160.5 EndY=0 EndZ=0
    g11: LineSegment StartX=244.5 StartY=0 StartZ=0 EndX=247.5 EndY=0 EndZ=0
  constraints (40):
    c: Angle(g1) = 1.5708
    c: DistanceY(g1,g0) = 0
    c: Angle(g0) = 1.5708
    c: DistanceY(g0,g0) = 0
    c: Coincident(g2,g0)
    c: Vertical(g2)
    c: PointOnObject(g3,g-1)
    c: Coincident(g3,g1)
    c: Vertical(g3)
    c: DistanceY(g2,g2) = 32
    c: Coincident(g4,g1)
    c: PointOnObject(g5,g-1)
    c: Vertical(g5)
    c: Horizontal(g6)
    c: Vertical(g7)
    c: DistanceX(g5,g2) = 3
    c: DistanceX(g3,g7) = 3
    c: DistanceY(g5,g0) = 0
    c: DistanceY(g7,g1) = 0
    c: DistanceY(g7,g3) = 0
    c: DistanceX(g2) = 160.5
    c: DistanceX(g2,g3) = 84
    c: DistanceX(g0,g6) = 0
    c: DistanceX(g6,g1) = 0
    c: DistanceY(g2) = 0
    c: Coincident(g5,g8)
    c: Coincident(g6,g8)
    c: DistanceY(g6,g0) = 3
    c: Coincident(g6,g9)
    c: Coincident(g7,g9)
    c: Angle(g8) = 1.5708
    c: Angle(g9) = 1.5708
    c: Coincident(g10,g5)
    c: Coincident(g10,g2)
    c: Coincident(g11,g3)
    c: Coincident(g11,g7)
    c: DistanceY(g0,g0) = 20
    c: Coincident(g0,g4)
    c: DistanceY(g1,g0) = 0
    c: DistanceY(g1,g1) = 0
FEATURE [Part::Loft] Loft005  label="srs006"
  Closed = false
  MaxDegree = 5
  Ruled = false
  Sections = -> [Sketch046,Sketch047]
  Solid = true
FEATURE [Part::Fillet] Fillet008  label="srsCovers005"
  Base = -> Loft005
  EdgeLinks = -> Loft005 [Edge1,Edge3,Edge5,Edge7,Edge8,Edge10,Edge11,Edge13,Edge14,Edge16,Edge17,Edge19,Edge20,Edge22,Edge23,Edge25,Edge26,Edge28,Edge29,Edge31,Edge32,Edge34,Edge35,Edge36]
  Edges = 24 edges r=1: [Edge1,Edge3,Edge5,Edge7,Edge8,Edge10,Edge11,Edge13,Edge14,Edge16,Edge17,Edge19,Edge20,Edge22,Edge23,Edge25,Edge26,Edge28,Edge29,Edge31,Edge32,Edge34,Edge35,Edge36]
  Placement = pos=(0,0,48.33) rot=(0,0,1;0rad)
FEATURE [Sketcher::SketchObject] Sketch048  label="innerSRS006"
  ArcFitTolerance = 0
  FullyConstrained = true
  MakeInternals = false
  Placement = pos=(0,0,-65) rot=(0,0,1;0rad)
  sketch-geometry (12):
    g0: ArcOfCircle CenterX=180.5 CenterY=-32 CenterZ=0 NormalX=0 NormalY=0 NormalZ=1 AngleXU=0 Radius=10 StartAngle=3.14159 EndAngle=4.71239
    g1: ArcOfCircle CenterX=224.5 CenterY=-32 CenterZ=0 NormalX=0 NormalY=0 NormalZ=1 AngleXU=0 Radius=10 StartAngle=4.71239 EndAngle=6.28319
    g2: LineSegment StartX=170.5 StartY=-32 StartZ=0 EndX=170.5 EndY=0 EndZ=0
    g3: LineSegment StartX=234.5 StartY=0 StartZ=0 EndX=234.5 EndY=-32 EndZ=0
    g4: LineSegment StartX=180.5 StartY=-42 StartZ=0 EndX=224.5 EndY=-42 EndZ=0
    g5: LineSegment StartX=167.5 StartY=0 StartZ=0 EndX=167.5 EndY=-32 EndZ=0
    g6: LineSegment StartX=180.5 StartY=-45 StartZ=0 EndX=224.5 EndY=-45 EndZ=0
    g7: LineSegment StartX=237.5 StartY=0 StartZ=0 EndX=237.5 EndY=-32 EndZ=0
    g8: ArcOfCircle CenterX=180.5 CenterY=-32 CenterZ=0 NormalX=0 NormalY=0 NormalZ=1 AngleXU=0 Radius=13 StartAngle=3.14159 EndAngle=4.71239
    g9: ArcOfCircle CenterX=224.5 CenterY=-32 CenterZ=0 NormalX=0 NormalY=0 NormalZ=1 AngleXU=0 Radius=13 StartAngle=4.71239 EndAngle=6.28319
    g10: LineSegment StartX=167.5 StartY=0 StartZ=0 EndX=170.5 EndY=0 EndZ=0
    g11: LineSegment StartX=234.5 StartY=0 StartZ=0 EndX=237.5 EndY=0 EndZ=0
  constraints (40):
    c: Angle(g1) = 1.5708
    c: DistanceY(g1,g1) = 0
    c: DistanceY(g1,g0) = 0
    c: Angle(g0) = 1.5708
    c: DistanceX(g0,g0) = 10
    c: DistanceY(g0,g0) = 0
    c: DistanceX(g1,g1) = 10
    c: Coincident(g2,g0)
    c: Vertical(g2)
    c: PointOnObject(g3,g-1)
    c: Coincident(g3,g1)
    c: Vertical(g3)
    c: DistanceY(g2,g2) = 32
    c: Coincident(g4,g1)
    c: PointOnObject(g5,g-1)
    c: Vertical(g5)
    c: Horizontal(g6)
    c: Vertical(g7)
    c: DistanceX(g5,g2) = 3
    c: DistanceX(g3,g7) = 3
    c: DistanceY(g5,g0) = 0
    c: DistanceY(g7,g1) = 0
    c: DistanceY(g7,g3) = 0
    c: DistanceX(g2,g3) = 64
    c: DistanceX(g0,g6) = 0
    c: DistanceX(g6,g1) = 0
    c: DistanceY(g2) = 0
    c: Coincident(g5,g8)
    c: Coincident(g6,g8)
    c: DistanceY(g6,g0) = 3
    c: Coincident(g6,g9)
    c: Coincident(g7,g9)
    c: Angle(g8) = 1.5708
    c: Angle(g9) = 1.5708
    c: Coincident(g10,g5)
    c: Coincident(g10,g2)
    c: Coincident(g11,g3)
    c: Coincident(g11,g7)
    c: Coincident(g0,g4)
    c: DistanceX(g2) = 170.5
FEATURE [Sketcher::SketchObject] Sketch049  label="outerSRS006"
  ArcFitTolerance = 0
  FullyConstrained = true
  MakeInternals = false
  Placement = pos=(0,0,-80) rot=(0,0,1;0rad)
  sketch-geometry (12):
    g0: ArcOfCircle CenterX=180.5 CenterY=-32 CenterZ=0 NormalX=0 NormalY=0 NormalZ=1 AngleXU=0 Radius=20 StartAngle=3.14159 EndAngle=4.71239
    g1: ArcOfCircle CenterX=224.5 CenterY=-32 CenterZ=0 NormalX=0 NormalY=0 NormalZ=1 AngleXU=0 Radius=20 StartAngle=4.71239 EndAngle=6.28319
    g2: LineSegment StartX=160.5 StartY=-32 StartZ=0 EndX=160.5 EndY=0 EndZ=0
    g3: LineSegment StartX=244.5 StartY=0 StartZ=0 EndX=244.5 EndY=-32 EndZ=0
    g4: LineSegment StartX=180.5 StartY=-52 StartZ=0 EndX=224.5 EndY=-52 EndZ=0
    g5: LineSegment StartX=157.5 StartY=0 StartZ=0 EndX=157.5 EndY=-32 EndZ=0
    g6: LineSegment StartX=180.5 StartY=-55 StartZ=0 EndX=224.5 EndY=-55 EndZ=0
    g7: LineSegment StartX=247.5 StartY=0 StartZ=0 EndX=247.5 EndY=-32 EndZ=0
    g8: ArcOfCircle CenterX=180.5 CenterY=-32 CenterZ=0 NormalX=0 NormalY=0 NormalZ=1 AngleXU=0 Radius=23 StartAngle=3.14159 EndAngle=4.71239
    g9: ArcOfCircle CenterX=224.5 CenterY=-32 CenterZ=0 NormalX=0 NormalY=0 NormalZ=1 AngleXU=0 Radius=23 StartAngle=4.71239 EndAngle=6.28319
    g10: LineSegment StartX=157.5 StartY=0 StartZ=0 EndX=160.5 EndY=0 EndZ=0
    g11: LineSegment StartX=244.5 StartY=0 StartZ=0 EndX=247.5 EndY=0 EndZ=0
  constraints (40):
    c: Angle(g1) = 1.5708
    c: DistanceY(g1,g0) = 0
    c: Angle(g0) = 1.5708
    c: DistanceY(g0,g0) = 0
    c: Coincident(g2,g0)
    c: Vertical(g2)
    c: PointOnObject(g3,g-1)
    c: Coincident(g3,g1)
    c: Vertical(g3)
    c: DistanceY(g2,g2) = 32
    c: Coincident(g4,g1)
    c: PointOnObject(g5,g-1)
    c: Vertical(g5)
    c: Horizontal(g6)
    c: Vertical(g7)
    c: DistanceX(g5,g2) = 3
    c: DistanceX(g3,g7) = 3
    c: DistanceY(g5,g0) = 0
    c: DistanceY(g7,g1) = 0
    c: DistanceY(g7,g3) = 0
    c: DistanceX(g2) = 160.5
    c: DistanceX(g2,g3) = 84
    c: DistanceX(g0,g6) = 0
    c: DistanceX(g6,g1) = 0
    c: DistanceY(g2) = 0
    c: Coincident(g5,g8)
    c: Coincident(g6,g8)
    c: DistanceY(g6,g0) = 3
    c: Coincident(g6,g9)
    c: Coincident(g7,g9)
    c: Angle(g8) = 1.5708
    c: Angle(g9) = 1.5708
    c: Coincident(g10,g5)
    c: Coincident(g10,g2)
    c: Coincident(g11,g3)
    c: Coincident(g11,g7)
    c: DistanceY(g0,g0) = 20
    c: Coincident(g0,g4)
    c: DistanceY(g1,g0) = 0
    c: DistanceY(g1,g1) = 0
FEATURE [Part::Loft] Loft006  label="srs007"
  Closed = false
  MaxDegree = 5
  Ruled = false
  Sections = -> [Sketch048,Sketch049]
  Solid = true
FEATURE [Part::Fillet] Fillet009  label="srsCovers006"
  Base = -> Loft006
  EdgeLinks = -> Loft006 [Edge1,Edge3,Edge5,Edge7,Edge8,Edge10,Edge11,Edge13,Edge14,Edge16,Edge17,Edge19,Edge20,Edge22,Edge23,Edge25,Edge26,Edge28,Edge29,Edge31,Edge32,Edge34,Edge35,Edge36]
  Edges = 24 edges r=1: [Edge1,Edge3,Edge5,Edge7,Edge8,Edge10,Edge11,Edge13,Edge14,Edge16,Edge17,Edge19,Edge20,Edge22,Edge23,Edge25,Edge26,Edge28,Edge29,Edge31,Edge32,Edge34,Edge35,Edge36]
  Placement = pos=(0,0,58) rot=(0,0,1;0rad)
FEATURE [Sketcher::SketchObject] Sketch050  label="innerSRS007"
  ArcFitTolerance = 0
  FullyConstrained = true
  MakeInternals = false
  Placement = pos=(0,0,-65) rot=(0,0,1;0rad)
  sketch-geometry (12):
    g0: ArcOfCircle CenterX=180.5 CenterY=-32 CenterZ=0 NormalX=0 NormalY=0 NormalZ=1 AngleXU=0 Radius=10 StartAngle=3.14159 EndAngle=4.71239
    g1: ArcOfCircle CenterX=224.5 CenterY=-32 CenterZ=0 NormalX=0 NormalY=0 NormalZ=1 AngleXU=0 Radius=10 StartAngle=4.71239 EndAngle=6.28319
    g2: LineSegment StartX=170.5 StartY=-32 StartZ=0 EndX=170.5 EndY=0 EndZ=0
    g3: LineSegment StartX=234.5 StartY=0 StartZ=0 EndX=234.5 EndY=-32 EndZ=0
    g4: LineSegment StartX=180.5 StartY=-42 StartZ=0 EndX=224.5 EndY=-42 EndZ=0
    g5: LineSegment StartX=167.5 StartY=0 StartZ=0 EndX=167.5 EndY=-32 EndZ=0
    g6: LineSegment StartX=180.5 StartY=-45 StartZ=0 EndX=224.5 EndY=-45 EndZ=0
    g7: LineSegment StartX=237.5 StartY=0 StartZ=0 EndX=237.5 EndY=-32 EndZ=0
    g8: ArcOfCircle CenterX=180.5 CenterY=-32 CenterZ=0 NormalX=0 NormalY=0 NormalZ=1 AngleXU=0 Radius=13 StartAngle=3.14159 EndAngle=4.71239
    g9: ArcOfCircle CenterX=224.5 CenterY=-32 CenterZ=0 NormalX=0 NormalY=0 NormalZ=1 AngleXU=0 Radius=13 StartAngle=4.71239 EndAngle=6.28319
    g10: LineSegment StartX=167.5 StartY=0 StartZ=0 EndX=170.5 EndY=0 EndZ=0
    g11: LineSegment StartX=234.5 StartY=0 StartZ=0 EndX=237.5 EndY=0 EndZ=0
  constraints (40):
    c: Angle(g1) = 1.5708
    c: DistanceY(g1,g1) = 0
    c: DistanceY(g1,g0) = 0
    c: Angle(g0) = 1.5708
    c: DistanceX(g0,g0) = 10
    c: DistanceY(g0,g0) = 0
    c: DistanceX(g1,g1) = 10
    c: Coincident(g2,g0)
    c: Vertical(g2)
    c: PointOnObject(g3,g-1)
    c: Coincident(g3,g1)
    c: Vertical(g3)
    c: DistanceY(g2,g2) = 32
    c: Coincident(g4,g1)
    c: PointOnObject(g5,g-1)
    c: Vertical(g5)
    c: Horizontal(g6)
    c: Vertical(g7)
    c: DistanceX(g5,g2) = 3
    c: DistanceX(g3,g7) = 3
    c: DistanceY(g5,g0) = 0
    c: DistanceY(g7,g1) = 0
    c: DistanceY(g7,g3) = 0
    c: DistanceX(g2,g3) = 64
    c: DistanceX(g0,g6) = 0
    c: DistanceX(g6,g1) = 0
    c: DistanceY(g2) = 0
    c: Coincident(g5,g8)
    c: Coincident(g6,g8)
    c: DistanceY(g6,g0) = 3
    c: Coincident(g6,g9)
    c: Coincident(g7,g9)
    c: Angle(g8) = 1.5708
    c: Angle(g9) = 1.5708
    c: Coincident(g10,g5)
    c: Coincident(g10,g2)
    c: Coincident(g11,g3)
    c: Coincident(g11,g7)
    c: Coincident(g0,g4)
    c: DistanceX(g2) = 170.5
FEATURE [Sketcher::SketchObject] Sketch051  label="outerSRS007"
  ArcFitTolerance = 0
  FullyConstrained = true
  MakeInternals = false
  Placement = pos=(0,0,-80) rot=(0,0,1;0rad)
  sketch-geometry (12):
    g0: ArcOfCircle CenterX=180.5 CenterY=-32 CenterZ=0 NormalX=0 NormalY=0 NormalZ=1 AngleXU=0 Radius=20 StartAngle=3.14159 EndAngle=4.71239
    g1: ArcOfCircle CenterX=224.5 CenterY=-32 CenterZ=0 NormalX=0 NormalY=0 NormalZ=1 AngleXU=0 Radius=20 StartAngle=4.71239 EndAngle=6.28319
    g2: LineSegment StartX=160.5 StartY=-32 StartZ=0 EndX=160.5 EndY=0 EndZ=0
    g3: LineSegment StartX=244.5 StartY=0 StartZ=0 EndX=244.5 EndY=-32 EndZ=0
    g4: LineSegment StartX=180.5 StartY=-52 StartZ=0 EndX=224.5 EndY=-52 EndZ=0
    g5: LineSegment StartX=157.5 StartY=0 StartZ=0 EndX=157.5 EndY=-32 EndZ=0
    g6: LineSegment StartX=180.5 StartY=-55 StartZ=0 EndX=224.5 EndY=-55 EndZ=0
    g7: LineSegment StartX=247.5 StartY=0 StartZ=0 EndX=247.5 EndY=-32 EndZ=0
    g8: ArcOfCircle CenterX=180.5 CenterY=-32 CenterZ=0 NormalX=0 NormalY=0 NormalZ=1 AngleXU=0 Radius=23 StartAngle=3.14159 EndAngle=4.71239
    g9: ArcOfCircle CenterX=224.5 CenterY=-32 CenterZ=0 NormalX=0 NormalY=0 NormalZ=1 AngleXU=0 Radius=23 StartAngle=4.71239 EndAngle=6.28319
    g10: LineSegment StartX=157.5 StartY=0 StartZ=0 EndX=160.5 EndY=0 EndZ=0
    g11: LineSegment StartX=244.5 StartY=0 StartZ=0 EndX=247.5 EndY=0 EndZ=0
  constraints (40):
    c: Angle(g1) = 1.5708
    c: DistanceY(g1,g0) = 0
    c: Angle(g0) = 1.5708
    c: DistanceY(g0,g0) = 0
    c: Coincident(g2,g0)
    c: Vertical(g2)
    c: PointOnObject(g3,g-1)
    c: Coincident(g3,g1)
    c: Vertical(g3)
    c: DistanceY(g2,g2) = 32
    c: Coincident(g4,g1)
    c: PointOnObject(g5,g-1)
    c: Vertical(g5)
    c: Horizontal(g6)
    c: Vertical(g7)
    c: DistanceX(g5,g2) = 3
    c: DistanceX(g3,g7) = 3
    c: DistanceY(g5,g0) = 0
    c: DistanceY(g7,g1) = 0
    c: DistanceY(g7,g3) = 0
    c: DistanceX(g2) = 160.5
    c: DistanceX(g2,g3) = 84
    c: DistanceX(g0,g6) = 0
    c: DistanceX(g6,g1) = 0
    c: DistanceY(g2) = 0
    c: Coincident(g5,g8)
    c: Coincident(g6,g8)
    c: DistanceY(g6,g0) = 3
    c: Coincident(g6,g9)
    c: Coincident(g7,g9)
    c: Angle(g8) = 1.5708
    c: Angle(g9) = 1.5708
    c: Coincident(g10,g5)
    c: Coincident(g10,g2)
    c: Coincident(g11,g3)
    c: Coincident(g11,g7)
    c: DistanceY(g0,g0) = 20
    c: Coincident(g0,g4)
    c: DistanceY(g1,g0) = 0
    c: DistanceY(g1,g1) = 0
FEATURE [Part::Loft] Loft007  label="srs008"
  Closed = false
  MaxDegree = 5
  Ruled = false
  Sections = -> [Sketch050,Sketch051]
  Solid = true
FEATURE [Part::Fillet] Fillet010  label="srsCovers007"
  Base = -> Loft007
  EdgeLinks = -> Loft007 [Edge1,Edge3,Edge5,Edge7,Edge8,Edge10,Edge11,Edge13,Edge14,Edge16,Edge17,Edge19,Edge20,Edge22,Edge23,Edge25,Edge26,Edge28,Edge29,Edge31,Edge32,Edge34,Edge35,Edge36]
  Edges = 24 edges r=1: [Edge1,Edge3,Edge5,Edge7,Edge8,Edge10,Edge11,Edge13,Edge14,Edge16,Edge17,Edge19,Edge20,Edge22,Edge23,Edge25,Edge26,Edge28,Edge29,Edge31,Edge32,Edge34,Edge35,Edge36]
  Placement = pos=(0,0,67.67) rot=(0,0,1;0rad)
FEATURE [Sketcher::SketchObject] Sketch052  label="innerSRS008"
  ArcFitTolerance = 0
  FullyConstrained = true
  MakeInternals = false
  Placement = pos=(0,0,-65) rot=(0,0,1;0rad)
  sketch-geometry (12):
    g0: ArcOfCircle CenterX=180.5 CenterY=-32 CenterZ=0 NormalX=0 NormalY=0 NormalZ=1 AngleXU=0 Radius=10 StartAngle=3.14159 EndAngle=4.71239
    g1: ArcOfCircle CenterX=224.5 CenterY=-32 CenterZ=0 NormalX=0 NormalY=0 NormalZ=1 AngleXU=0 Radius=10 StartAngle=4.71239 EndAngle=6.28319
    g2: LineSegment StartX=170.5 StartY=-32 StartZ=0 EndX=170.5 EndY=0 EndZ=0
    g3: LineSegment StartX=234.5 StartY=0 StartZ=0 EndX=234.5 EndY=-32 EndZ=0
    g4: LineSegment StartX=180.5 StartY=-42 StartZ=0 EndX=224.5 EndY=-42 EndZ=0
    g5: LineSegment StartX=167.5 StartY=0 StartZ=0 EndX=167.5 EndY=-32 EndZ=0
    g6: LineSegment StartX=180.5 StartY=-45 StartZ=0 EndX=224.5 EndY=-45 EndZ=0
    g7: LineSegment StartX=237.5 StartY=0 StartZ=0 EndX=237.5 EndY=-32 EndZ=0
    g8: ArcOfCircle CenterX=180.5 CenterY=-32 CenterZ=0 NormalX=0 NormalY=0 NormalZ=1 AngleXU=0 Radius=13 StartAngle=3.14159 EndAngle=4.71239
    g9: ArcOfCircle CenterX=224.5 CenterY=-32 CenterZ=0 NormalX=0 NormalY=0 NormalZ=1 AngleXU=0 Radius=13 StartAngle=4.71239 EndAngle=6.28319
    g10: LineSegment StartX=167.5 StartY=0 StartZ=0 EndX=170.5 EndY=0 EndZ=0
    g11: LineSegment StartX=234.5 StartY=0 StartZ=0 EndX=237.5 EndY=0 EndZ=0
  constraints (40):
    c: Angle(g1) = 1.5708
    c: DistanceY(g1,g1) = 0
    c: DistanceY(g1,g0) = 0
    c: Angle(g0) = 1.5708
    c: DistanceX(g0,g0) = 10
    c: DistanceY(g0,g0) = 0
    c: DistanceX(g1,g1) = 10
    c: Coincident(g2,g0)
    c: Vertical(g2)
    c: PointOnObject(g3,g-1)
    c: Coincident(g3,g1)
    c: Vertical(g3)
    c: DistanceY(g2,g2) = 32
    c: Coincident(g4,g1)
    c: PointOnObject(g5,g-1)
    c: Vertical(g5)
    c: Horizontal(g6)
    c: Vertical(g7)
    c: DistanceX(g5,g2) = 3
    c: DistanceX(g3,g7) = 3
    c: DistanceY(g5,g0) = 0
    c: DistanceY(g7,g1) = 0
    c: DistanceY(g7,g3) = 0
    c: DistanceX(g2,g3) = 64
    c: DistanceX(g0,g6) = 0
    c: DistanceX(g6,g1) = 0
    c: DistanceY(g2) = 0
    c: Coincident(g5,g8)
    c: Coincident(g6,g8)
    c: DistanceY(g6,g0) = 3
    c: Coincident(g6,g9)
    c: Coincident(g7,g9)
    c: Angle(g8) = 1.5708
    c: Angle(g9) = 1.5708
    c: Coincident(g10,g5)
    c: Coincident(g10,g2)
    c: Coincident(g11,g3)
    c: Coincident(g11,g7)
    c: Coincident(g0,g4)
    c: DistanceX(g2) = 170.5
FEATURE [Sketcher::SketchObject] Sketch053  label="outerSRS008"
  ArcFitTolerance = 0
  FullyConstrained = true
  MakeInternals = false
  Placement = pos=(0,0,-80) rot=(0,0,1;0rad)
  sketch-geometry (12):
    g0: ArcOfCircle CenterX=180.5 CenterY=-32 CenterZ=0 NormalX=0 NormalY=0 NormalZ=1 AngleXU=0 Radius=20 StartAngle=3.14159 EndAngle=4.71239
    g1: ArcOfCircle CenterX=224.5 CenterY=-32 CenterZ=0 NormalX=0 NormalY=0 NormalZ=1 AngleXU=0 Radius=20 StartAngle=4.71239 EndAngle=6.28319
    g2: LineSegment StartX=160.5 StartY=-32 StartZ=0 EndX=160.5 EndY=0 EndZ=0
    g3: LineSegment StartX=244.5 StartY=0 StartZ=0 EndX=244.5 EndY=-32 EndZ=0
    g4: LineSegment StartX=180.5 StartY=-52 StartZ=0 EndX=224.5 EndY=-52 EndZ=0
    g5: LineSegment StartX=157.5 StartY=0 StartZ=0 EndX=157.5 EndY=-32 EndZ=0
    g6: LineSegment StartX=180.5 StartY=-55 StartZ=0 EndX=224.5 EndY=-55 EndZ=0
    g7: LineSegment StartX=247.5 StartY=0 StartZ=0 EndX=247.5 EndY=-32 EndZ=0
    g8: ArcOfCircle CenterX=180.5 CenterY=-32 CenterZ=0 NormalX=0 NormalY=0 NormalZ=1 AngleXU=0 Radius=23 StartAngle=3.14159 EndAngle=4.71239
    g9: ArcOfCircle CenterX=224.5 CenterY=-32 CenterZ=0 NormalX=0 NormalY=0 NormalZ=1 AngleXU=0 Radius=23 StartAngle=4.71239 EndAngle=6.28319
    g10: LineSegment StartX=157.5 StartY=0 StartZ=0 EndX=160.5 EndY=0 EndZ=0
    g11: LineSegment StartX=244.5 StartY=0 StartZ=0 EndX=247.5 EndY=0 EndZ=0
  constraints (40):
    c: Angle(g1) = 1.5708
    c: DistanceY(g1,g0) = 0
    c: Angle(g0) = 1.5708
    c: DistanceY(g0,g0) = 0
    c: Coincident(g2,g0)
    c: Vertical(g2)
    c: PointOnObject(g3,g-1)
    c: Coincident(g3,g1)
    c: Vertical(g3)
    c: DistanceY(g2,g2) = 32
    c: Coincident(g4,g1)
    c: PointOnObject(g5,g-1)
    c: Vertical(g5)
    c: Horizontal(g6)
    c: Vertical(g7)
    c: DistanceX(g5,g2) = 3
    c: DistanceX(g3,g7) = 3
    c: DistanceY(g5,g0) = 0
    c: DistanceY(g7,g1) = 0
    c: DistanceY(g7,g3) = 0
    c: DistanceX(g2) = 160.5
    c: DistanceX(g2,g3) = 84
    c: DistanceX(g0,g6) = 0
    c: DistanceX(g6,g1) = 0
    c: DistanceY(g2) = 0
    c: Coincident(g5,g8)
    c: Coincident(g6,g8)
    c: DistanceY(g6,g0) = 3
    c: Coincident(g6,g9)
    c: Coincident(g7,g9)
    c: Angle(g8) = 1.5708
    c: Angle(g9) = 1.5708
    c: Coincident(g10,g5)
    c: Coincident(g10,g2)
    c: Coincident(g11,g3)
    c: Coincident(g11,g7)
    c: DistanceY(g0,g0) = 20
    c: Coincident(g0,g4)
    c: DistanceY(g1,g0) = 0
    c: DistanceY(g1,g1) = 0
FEATURE [Part::Loft] Loft008  label="srs009"
  Closed = false
  MaxDegree = 5
  Ruled = false
  Sections = -> [Sketch052,Sketch053]
  Solid = true
FEATURE [Part::Fillet] Fillet011  label="srsCovers008"
  Base = -> Loft008
  EdgeLinks = -> Loft008 [Edge1,Edge3,Edge5,Edge7,Edge8,Edge10,Edge11,Edge13,Edge14,Edge16,Edge17,Edge19,Edge20,Edge22,Edge23,Edge25,Edge26,Edge28,Edge29,Edge31,Edge32,Edge34,Edge35,Edge36]
  Edges = 24 edges r=1: [Edge1,Edge3,Edge5,Edge7,Edge8,Edge10,Edge11,Edge13,Edge14,Edge16,Edge17,Edge19,Edge20,Edge22,Edge23,Edge25,Edge26,Edge28,Edge29,Edge31,Edge32,Edge34,Edge35,Edge36]
  Placement = pos=(0,0,77.33) rot=(0,0,1;0rad)
FEATURE [Sketcher::SketchObject] Sketch054  label="innerSRS009"
  ArcFitTolerance = 0
  FullyConstrained = true
  MakeInternals = false
  Placement = pos=(0,0,-65) rot=(0,0,1;0rad)
  sketch-geometry (12):
    g0: ArcOfCircle CenterX=180.5 CenterY=-32 CenterZ=0 NormalX=0 NormalY=0 NormalZ=1 AngleXU=0 Radius=10 StartAngle=3.14159 EndAngle=4.71239
    g1: ArcOfCircle CenterX=224.5 CenterY=-32 CenterZ=0 NormalX=0 NormalY=0 NormalZ=1 AngleXU=0 Radius=10 StartAngle=4.71239 EndAngle=6.28319
    g2: LineSegment StartX=170.5 StartY=-32 StartZ=0 EndX=170.5 EndY=0 EndZ=0
    g3: LineSegment StartX=234.5 StartY=0 StartZ=0 EndX=234.5 EndY=-32 EndZ=0
    g4: LineSegment StartX=180.5 StartY=-42 StartZ=0 EndX=224.5 EndY=-42 EndZ=0
    g5: LineSegment StartX=167.5 StartY=0 StartZ=0 EndX=167.5 EndY=-32 EndZ=0
    g6: LineSegment StartX=180.5 StartY=-45 StartZ=0 EndX=224.5 EndY=-45 EndZ=0
    g7: LineSegment StartX=237.5 StartY=0 StartZ=0 EndX=237.5 EndY=-32 EndZ=0
    g8: ArcOfCircle CenterX=180.5 CenterY=-32 CenterZ=0 NormalX=0 NormalY=0 NormalZ=1 AngleXU=0 Radius=13 StartAngle=3.14159 EndAngle=4.71239
    g9: ArcOfCircle CenterX=224.5 CenterY=-32 CenterZ=0 NormalX=0 NormalY=0 NormalZ=1 AngleXU=0 Radius=13 StartAngle=4.71239 EndAngle=6.28319
    g10: LineSegment StartX=167.5 StartY=0 StartZ=0 EndX=170.5 EndY=0 EndZ=0
    g11: LineSegment StartX=234.5 StartY=0 StartZ=0 EndX=237.5 EndY=0 EndZ=0
  constraints (40):
    c: Angle(g1) = 1.5708
    c: DistanceY(g1,g1) = 0
    c: DistanceY(g1,g0) = 0
    c: Angle(g0) = 1.5708
    c: DistanceX(g0,g0) = 10
    c: DistanceY(g0,g0) = 0
    c: DistanceX(g1,g1) = 10
    c: Coincident(g2,g0)
    c: Vertical(g2)
    c: PointOnObject(g3,g-1)
    c: Coincident(g3,g1)
    c: Vertical(g3)
    c: DistanceY(g2,g2) = 32
    c: Coincident(g4,g1)
    c: PointOnObject(g5,g-1)
    c: Vertical(g5)
    c: Horizontal(g6)
    c: Vertical(g7)
    c: DistanceX(g5,g2) = 3
    c: DistanceX(g3,g7) = 3
    c: DistanceY(g5,g0) = 0
    c: DistanceY(g7,g1) = 0
    c: DistanceY(g7,g3) = 0
    c: DistanceX(g2,g3) = 64
    c: DistanceX(g0,g6) = 0
    c: DistanceX(g6,g1) = 0
    c: DistanceY(g2) = 0
    c: Coincident(g5,g8)
    c: Coincident(g6,g8)
    c: DistanceY(g6,g0) = 3
    c: Coincident(g6,g9)
    c: Coincident(g7,g9)
    c: Angle(g8) = 1.5708
    c: Angle(g9) = 1.5708
    c: Coincident(g10,g5)
    c: Coincident(g10,g2)
    c: Coincident(g11,g3)
    c: Coincident(g11,g7)
    c: Coincident(g0,g4)
    c: DistanceX(g2) = 170.5
FEATURE [Sketcher::SketchObject] Sketch055  label="outerSRS009"
  ArcFitTolerance = 0
  FullyConstrained = true
  MakeInternals = false
  Placement = pos=(0,0,-80) rot=(0,0,1;0rad)
  sketch-geometry (12):
    g0: ArcOfCircle CenterX=180.5 CenterY=-32 CenterZ=0 NormalX=0 NormalY=0 NormalZ=1 AngleXU=0 Radius=20 StartAngle=3.14159 EndAngle=4.71239
    g1: ArcOfCircle CenterX=224.5 CenterY=-32 CenterZ=0 NormalX=0 NormalY=0 NormalZ=1 AngleXU=0 Radius=20 StartAngle=4.71239 EndAngle=6.28319
    g2: LineSegment StartX=160.5 StartY=-32 StartZ=0 EndX=160.5 EndY=0 EndZ=0
    g3: LineSegment StartX=244.5 StartY=0 StartZ=0 EndX=244.5 EndY=-32 EndZ=0
    g4: LineSegment StartX=180.5 StartY=-52 StartZ=0 EndX=224.5 EndY=-52 EndZ=0
    g5: LineSegment StartX=157.5 StartY=0 StartZ=0 EndX=157.5 EndY=-32 EndZ=0
    g6: LineSegment StartX=180.5 StartY=-55 StartZ=0 EndX=224.5 EndY=-55 EndZ=0
    g7: LineSegment StartX=247.5 StartY=0 StartZ=0 EndX=247.5 EndY=-32 EndZ=0
    g8: ArcOfCircle CenterX=180.5 CenterY=-32 CenterZ=0 NormalX=0 NormalY=0 NormalZ=1 AngleXU=0 Radius=23 StartAngle=3.14159 EndAngle=4.71239
    g9: ArcOfCircle CenterX=224.5 CenterY=-32 CenterZ=0 NormalX=0 NormalY=0 NormalZ=1 AngleXU=0 Radius=23 StartAngle=4.71239 EndAngle=6.28319
    g10: LineSegment StartX=157.5 StartY=0 StartZ=0 EndX=160.5 EndY=0 EndZ=0
    g11: LineSegment StartX=244.5 StartY=0 StartZ=0 EndX=247.5 EndY=0 EndZ=0
  constraints (40):
    c: Angle(g1) = 1.5708
    c: DistanceY(g1,g0) = 0
    c: Angle(g0) = 1.5708
    c: DistanceY(g0,g0) = 0
    c: Coincident(g2,g0)
    c: Vertical(g2)
    c: PointOnObject(g3,g-1)
    c: Coincident(g3,g1)
    c: Vertical(g3)
    c: DistanceY(g2,g2) = 32
    c: Coincident(g4,g1)
    c: PointOnObject(g5,g-1)
    c: Vertical(g5)
    c: Horizontal(g6)
    c: Vertical(g7)
    c: DistanceX(g5,g2) = 3
    c: DistanceX(g3,g7) = 3
    c: DistanceY(g5,g0) = 0
    c: DistanceY(g7,g1) = 0
    c: DistanceY(g7,g3) = 0
    c: DistanceX(g2) = 160.5
    c: DistanceX(g2,g3) = 84
    c: DistanceX(g0,g6) = 0
    c: DistanceX(g6,g1) = 0
    c: DistanceY(g2) = 0
    c: Coincident(g5,g8)
    c: Coincident(g6,g8)
    c: DistanceY(g6,g0) = 3
    c: Coincident(g6,g9)
    c: Coincident(g7,g9)
    c: Angle(g8) = 1.5708
    c: Angle(g9) = 1.5708
    c: Coincident(g10,g5)
    c: Coincident(g10,g2)
    c: Coincident(g11,g3)
    c: Coincident(g11,g7)
    c: DistanceY(g0,g0) = 20
    c: Coincident(g0,g4)
    c: DistanceY(g1,g0) = 0
    c: DistanceY(g1,g1) = 0
FEATURE [Part::Loft] Loft009  label="srs010"
  Closed = false
  MaxDegree = 5
  Ruled = false
  Sections = -> [Sketch054,Sketch055]
  Solid = true
FEATURE [Part::Fillet] Fillet012  label="srsCovers009"
  Base = -> Loft009
  EdgeLinks = -> Loft009 [Edge1,Edge3,Edge5,Edge7,Edge8,Edge10,Edge11,Edge13,Edge14,Edge16,Edge17,Edge19,Edge20,Edge22,Edge23,Edge25,Edge26,Edge28,Edge29,Edge31,Edge32,Edge34,Edge35,Edge36]
  Edges = 24 edges r=1: [Edge1,Edge3,Edge5,Edge7,Edge8,Edge10,Edge11,Edge13,Edge14,Edge16,Edge17,Edge19,Edge20,Edge22,Edge23,Edge25,Edge26,Edge28,Edge29,Edge31,Edge32,Edge34,Edge35,Edge36]
  Placement = pos=(0,0,87) rot=(0,0,1;0rad)
FEATURE [Sketcher::SketchObject] Sketch056  label="innerSRS010"
  ArcFitTolerance = 0
  FullyConstrained = true
  MakeInternals = false
  Placement = pos=(0,0,-65) rot=(0,0,1;0rad)
  sketch-geometry (12):
    g0: ArcOfCircle CenterX=180.5 CenterY=-32 CenterZ=0 NormalX=0 NormalY=0 NormalZ=1 AngleXU=0 Radius=10 StartAngle=3.14159 EndAngle=4.71239
    g1: ArcOfCircle CenterX=224.5 CenterY=-32 CenterZ=0 NormalX=0 NormalY=0 NormalZ=1 AngleXU=0 Radius=10 StartAngle=4.71239 EndAngle=6.28319
    g2: LineSegment StartX=170.5 StartY=-32 StartZ=0 EndX=170.5 EndY=0 EndZ=0
    g3: LineSegment StartX=234.5 StartY=0 StartZ=0 EndX=234.5 EndY=-32 EndZ=0
    g4: LineSegment StartX=180.5 StartY=-42 StartZ=0 EndX=224.5 EndY=-42 EndZ=0
    g5: LineSegment StartX=167.5 StartY=0 StartZ=0 EndX=167.5 EndY=-32 EndZ=0
    g6: LineSegment StartX=180.5 StartY=-45 StartZ=0 EndX=224.5 EndY=-45 EndZ=0
    g7: LineSegment StartX=237.5 StartY=0 StartZ=0 EndX=237.5 EndY=-32 EndZ=0
    g8: ArcOfCircle CenterX=180.5 CenterY=-32 CenterZ=0 NormalX=0 NormalY=0 NormalZ=1 AngleXU=0 Radius=13 StartAngle=3.14159 EndAngle=4.71239
    g9: ArcOfCircle CenterX=224.5 CenterY=-32 CenterZ=0 NormalX=0 NormalY=0 NormalZ=1 AngleXU=0 Radius=13 StartAngle=4.71239 EndAngle=6.28319
    g10: LineSegment StartX=167.5 StartY=0 StartZ=0 EndX=170.5 EndY=0 EndZ=0
    g11: LineSegment StartX=234.5 StartY=0 StartZ=0 EndX=237.5 EndY=0 EndZ=0
  constraints (40):
    c: Angle(g1) = 1.5708
    c: DistanceY(g1,g1) = 0
    c: DistanceY(g1,g0) = 0
    c: Angle(g0) = 1.5708
    c: DistanceX(g0,g0) = 10
    c: DistanceY(g0,g0) = 0
    c: DistanceX(g1,g1) = 10
    c: Coincident(g2,g0)
    c: Vertical(g2)
    c: PointOnObject(g3,g-1)
    c: Coincident(g3,g1)
    c: Vertical(g3)
    c: DistanceY(g2,g2) = 32
    c: Coincident(g4,g1)
    c: PointOnObject(g5,g-1)
    c: Vertical(g5)
    c: Horizontal(g6)
    c: Vertical(g7)
    c: DistanceX(g5,g2) = 3
    c: DistanceX(g3,g7) = 3
    c: DistanceY(g5,g0) = 0
    c: DistanceY(g7,g1) = 0
    c: DistanceY(g7,g3) = 0
    c: DistanceX(g2,g3) = 64
    c: DistanceX(g0,g6) = 0
    c: DistanceX(g6,g1) = 0
    c: DistanceY(g2) = 0
    c: Coincident(g5,g8)
    c: Coincident(g6,g8)
    c: DistanceY(g6,g0) = 3
    c: Coincident(g6,g9)
    c: Coincident(g7,g9)
    c: Angle(g8) = 1.5708
    c: Angle(g9) = 1.5708
    c: Coincident(g10,g5)
    c: Coincident(g10,g2)
    c: Coincident(g11,g3)
    c: Coincident(g11,g7)
    c: Coincident(g0,g4)
    c: DistanceX(g2) = 170.5
FEATURE [Sketcher::SketchObject] Sketch057  label="outerSRS010"
  ArcFitTolerance = 0
  FullyConstrained = true
  MakeInternals = false
  Placement = pos=(0,0,-80) rot=(0,0,1;0rad)
  sketch-geometry (12):
    g0: ArcOfCircle CenterX=180.5 CenterY=-32 CenterZ=0 NormalX=0 NormalY=0 NormalZ=1 AngleXU=0 Radius=20 StartAngle=3.14159 EndAngle=4.71239
    g1: ArcOfCircle CenterX=224.5 CenterY=-32 CenterZ=0 NormalX=0 NormalY=0 NormalZ=1 AngleXU=0 Radius=20 StartAngle=4.71239 EndAngle=6.28319
    g2: LineSegment StartX=160.5 StartY=-32 StartZ=0 EndX=160.5 EndY=0 EndZ=0
    g3: LineSegment StartX=244.5 StartY=0 StartZ=0 EndX=244.5 EndY=-32 EndZ=0
    g4: LineSegment StartX=180.5 StartY=-52 StartZ=0 EndX=224.5 EndY=-52 EndZ=0
    g5: LineSegment StartX=157.5 StartY=0 StartZ=0 EndX=157.5 EndY=-32 EndZ=0
    g6: LineSegment StartX=180.5 StartY=-55 StartZ=0 EndX=224.5 EndY=-55 EndZ=0
    g7: LineSegment StartX=247.5 StartY=0 StartZ=0 EndX=247.5 EndY=-32 EndZ=0
    g8: ArcOfCircle CenterX=180.5 CenterY=-32 CenterZ=0 NormalX=0 NormalY=0 NormalZ=1 AngleXU=0 Radius=23 StartAngle=3.14159 EndAngle=4.71239
    g9: ArcOfCircle CenterX=224.5 CenterY=-32 CenterZ=0 NormalX=0 NormalY=0 NormalZ=1 AngleXU=0 Radius=23 StartAngle=4.71239 EndAngle=6.28319
    g10: LineSegment StartX=157.5 StartY=0 StartZ=0 EndX=160.5 EndY=0 EndZ=0
    g11: LineSegment StartX=244.5 StartY=0 StartZ=0 EndX=247.5 EndY=0 EndZ=0
  constraints (40):
    c: Angle(g1) = 1.5708
    c: DistanceY(g1,g0) = 0
    c: Angle(g0) = 1.5708
    c: DistanceY(g0,g0) = 0
    c: Coincident(g2,g0)
    c: Vertical(g2)
    c: PointOnObject(g3,g-1)
    c: Coincident(g3,g1)
    c: Vertical(g3)
    c: DistanceY(g2,g2) = 32
    c: Coincident(g4,g1)
    c: PointOnObject(g5,g-1)
    c: Vertical(g5)
    c: Horizontal(g6)
    c: Vertical(g7)
    c: DistanceX(g5,g2) = 3
    c: DistanceX(g3,g7) = 3
    c: DistanceY(g5,g0) = 0
    c: DistanceY(g7,g1) = 0
    c: DistanceY(g7,g3) = 0
    c: DistanceX(g2) = 160.5
    c: DistanceX(g2,g3) = 84
    c: DistanceX(g0,g6) = 0
    c: DistanceX(g6,g1) = 0
    c: DistanceY(g2) = 0
    c: Coincident(g5,g8)
    c: Coincident(g6,g8)
    c: DistanceY(g6,g0) = 3
    c: Coincident(g6,g9)
    c: Coincident(g7,g9)
    c: Angle(g8) = 1.5708
    c: Angle(g9) = 1.5708
    c: Coincident(g10,g5)
    c: Coincident(g10,g2)
    c: Coincident(g11,g3)
    c: Coincident(g11,g7)
    c: DistanceY(g0,g0) = 20
    c: Coincident(g0,g4)
    c: DistanceY(g1,g0) = 0
    c: DistanceY(g1,g1) = 0
FEATURE [Part::Loft] Loft010  label="srs011"
  Closed = false
  MaxDegree = 5
  Ruled = false
  Sections = -> [Sketch056,Sketch057]
  Solid = true
FEATURE [Part::Fillet] Fillet013  label="srsCovers010"
  Base = -> Loft010
  EdgeLinks = -> Loft010 [Edge1,Edge3,Edge5,Edge7,Edge8,Edge10,Edge11,Edge13,Edge14,Edge16,Edge17,Edge19,Edge20,Edge22,Edge23,Edge25,Edge26,Edge28,Edge29,Edge31,Edge32,Edge34,Edge35,Edge36]
  Edges = 24 edges r=1: [Edge1,Edge3,Edge5,Edge7,Edge8,Edge10,Edge11,Edge13,Edge14,Edge16,Edge17,Edge19,Edge20,Edge22,Edge23,Edge25,Edge26,Edge28,Edge29,Edge31,Edge32,Edge34,Edge35,Edge36]
  Placement = pos=(0,0,96.67) rot=(0,0,1;0rad)
FEATURE [Sketcher::SketchObject] Sketch058  label="innerSRS011"
  ArcFitTolerance = 0
  FullyConstrained = true
  MakeInternals = false
  Placement = pos=(0,0,-65) rot=(0,0,1;0rad)
  sketch-geometry (12):
    g0: ArcOfCircle CenterX=180.5 CenterY=-32 CenterZ=0 NormalX=0 NormalY=0 NormalZ=1 AngleXU=0 Radius=10 StartAngle=3.14159 EndAngle=4.71239
    g1: ArcOfCircle CenterX=224.5 CenterY=-32 CenterZ=0 NormalX=0 NormalY=0 NormalZ=1 AngleXU=0 Radius=10 StartAngle=4.71239 EndAngle=6.28319
    g2: LineSegment StartX=170.5 StartY=-32 StartZ=0 EndX=170.5 EndY=0 EndZ=0
    g3: LineSegment StartX=234.5 StartY=0 StartZ=0 EndX=234.5 EndY=-32 EndZ=0
    g4: LineSegment StartX=180.5 StartY=-42 StartZ=0 EndX=224.5 EndY=-42 EndZ=0
    g5: LineSegment StartX=167.5 StartY=0 StartZ=0 EndX=167.5 EndY=-32 EndZ=0
    g6: LineSegment StartX=180.5 StartY=-45 StartZ=0 EndX=224.5 EndY=-45 EndZ=0
    g7: LineSegment StartX=237.5 StartY=0 StartZ=0 EndX=237.5 EndY=-32 EndZ=0
    g8: ArcOfCircle CenterX=180.5 CenterY=-32 CenterZ=0 NormalX=0 NormalY=0 NormalZ=1 AngleXU=0 Radius=13 StartAngle=3.14159 EndAngle=4.71239
    g9: ArcOfCircle CenterX=224.5 CenterY=-32 CenterZ=0 NormalX=0 NormalY=0 NormalZ=1 AngleXU=0 Radius=13 StartAngle=4.71239 EndAngle=6.28319
    g10: LineSegment StartX=167.5 StartY=0 StartZ=0 EndX=170.5 EndY=0 EndZ=0
    g11: LineSegment StartX=234.5 StartY=0 StartZ=0 EndX=237.5 EndY=0 EndZ=0
  constraints (40):
    c: Angle(g1) = 1.5708
    c: DistanceY(g1,g1) = 0
    c: DistanceY(g1,g0) = 0
    c: Angle(g0) = 1.5708
    c: DistanceX(g0,g0) = 10
    c: DistanceY(g0,g0) = 0
    c: DistanceX(g1,g1) = 10
    c: Coincident(g2,g0)
    c: Vertical(g2)
    c: PointOnObject(g3,g-1)
    c: Coincident(g3,g1)
    c: Vertical(g3)
    c: DistanceY(g2,g2) = 32
    c: Coincident(g4,g1)
    c: PointOnObject(g5,g-1)
    c: Vertical(g5)
    c: Horizontal(g6)
    c: Vertical(g7)
    c: DistanceX(g5,g2) = 3
    c: DistanceX(g3,g7) = 3
    c: DistanceY(g5,g0) = 0
    c: DistanceY(g7,g1) = 0
    c: DistanceY(g7,g3) = 0
    c: DistanceX(g2,g3) = 64
    c: DistanceX(g0,g6) = 0
    c: DistanceX(g6,g1) = 0
    c: DistanceY(g2) = 0
    c: Coincident(g5,g8)
    c: Coincident(g6,g8)
    c: DistanceY(g6,g0) = 3
    c: Coincident(g6,g9)
    c: Coincident(g7,g9)
    c: Angle(g8) = 1.5708
    c: Angle(g9) = 1.5708
    c: Coincident(g10,g5)
    c: Coincident(g10,g2)
    c: Coincident(g11,g3)
    c: Coincident(g11,g7)
    c: Coincident(g0,g4)
    c: DistanceX(g2) = 170.5
FEATURE [Sketcher::SketchObject] Sketch059  label="outerSRS011"
  ArcFitTolerance = 0
  FullyConstrained = true
  MakeInternals = false
  Placement = pos=(0,0,-80) rot=(0,0,1;0rad)
  sketch-geometry (12):
    g0: ArcOfCircle CenterX=180.5 CenterY=-32 CenterZ=0 NormalX=0 NormalY=0 NormalZ=1 AngleXU=0 Radius=20 StartAngle=3.14159 EndAngle=4.71239
    g1: ArcOfCircle CenterX=224.5 CenterY=-32 CenterZ=0 NormalX=0 NormalY=0 NormalZ=1 AngleXU=0 Radius=20 StartAngle=4.71239 EndAngle=6.28319
    g2: LineSegment StartX=160.5 StartY=-32 StartZ=0 EndX=160.5 EndY=0 EndZ=0
    g3: LineSegment StartX=244.5 StartY=0 StartZ=0 EndX=244.5 EndY=-32 EndZ=0
    g4: LineSegment StartX=180.5 StartY=-52 StartZ=0 EndX=224.5 EndY=-52 EndZ=0
    g5: LineSegment StartX=157.5 StartY=0 StartZ=0 EndX=157.5 EndY=-32 EndZ=0
    g6: LineSegment StartX=180.5 StartY=-55 StartZ=0 EndX=224.5 EndY=-55 EndZ=0
    g7: LineSegment StartX=247.5 StartY=0 StartZ=0 EndX=247.5 EndY=-32 EndZ=0
    g8: ArcOfCircle CenterX=180.5 CenterY=-32 CenterZ=0 NormalX=0 NormalY=0 NormalZ=1 AngleXU=0 Radius=23 StartAngle=3.14159 EndAngle=4.71239
    g9: ArcOfCircle CenterX=224.5 CenterY=-32 CenterZ=0 NormalX=0 NormalY=0 NormalZ=1 AngleXU=0 Radius=23 StartAngle=4.71239 EndAngle=6.28319
    g10: LineSegment StartX=157.5 StartY=0 StartZ=0 EndX=160.5 EndY=0 EndZ=0
    g11: LineSegment StartX=244.5 StartY=0 StartZ=0 EndX=247.5 EndY=0 EndZ=0
  constraints (40):
    c: Angle(g1) = 1.5708
    c: DistanceY(g1,g0) = 0
    c: Angle(g0) = 1.5708
    c: DistanceY(g0,g0) = 0
    c: Coincident(g2,g0)
    c: Vertical(g2)
    c: PointOnObject(g3,g-1)
    c: Coincident(g3,g1)
    c: Vertical(g3)
    c: DistanceY(g2,g2) = 32
    c: Coincident(g4,g1)
    c: PointOnObject(g5,g-1)
    c: Vertical(g5)
    c: Horizontal(g6)
    c: Vertical(g7)
    c: DistanceX(g5,g2) = 3
    c: DistanceX(g3,g7) = 3
    c: DistanceY(g5,g0) = 0
    c: DistanceY(g7,g1) = 0
    c: DistanceY(g7,g3) = 0
    c: DistanceX(g2) = 160.5
    c: DistanceX(g2,g3) = 84
    c: DistanceX(g0,g6) = 0
    c: DistanceX(g6,g1) = 0
    c: DistanceY(g2) = 0
    c: Coincident(g5,g8)
    c: Coincident(g6,g8)
    c: DistanceY(g6,g0) = 3
    c: Coincident(g6,g9)
    c: Coincident(g7,g9)
    c: Angle(g8) = 1.5708
    c: Angle(g9) = 1.5708
    c: Coincident(g10,g5)
    c: Coincident(g10,g2)
    c: Coincident(g11,g3)
    c: Coincident(g11,g7)
    c: DistanceY(g0,g0) = 20
    c: Coincident(g0,g4)
    c: DistanceY(g1,g0) = 0
    c: DistanceY(g1,g1) = 0
FEATURE [Part::Loft] Loft011  label="srs012"
  Closed = false
  MaxDegree = 5
  Ruled = false
  Sections = -> [Sketch058,Sketch059]
  Solid = true
FEATURE [Part::Fillet] Fillet014  label="srsCovers011"
  Base = -> Loft011
  EdgeLinks = -> Loft011 [Edge1,Edge3,Edge5,Edge7,Edge8,Edge10,Edge11,Edge13,Edge14,Edge16,Edge17,Edge19,Edge20,Edge22,Edge23,Edge25,Edge26,Edge28,Edge29,Edge31,Edge32,Edge34,Edge35,Edge36]
  Edges = 24 edges r=1: [Edge1,Edge3,Edge5,Edge7,Edge8,Edge10,Edge11,Edge13,Edge14,Edge16,Edge17,Edge19,Edge20,Edge22,Edge23,Edge25,Edge26,Edge28,Edge29,Edge31,Edge32,Edge34,Edge35,Edge36]
  Placement = pos=(0,0,106.33) rot=(0,0,1;0rad)
FEATURE [Sketcher::SketchObject] Sketch060  label="innerSRS012"
  ArcFitTolerance = 0
  FullyConstrained = true
  MakeInternals = false
  Placement = pos=(0,0,-65) rot=(0,0,1;0rad)
  sketch-geometry (12):
    g0: ArcOfCircle CenterX=180.5 CenterY=-32 CenterZ=0 NormalX=0 NormalY=0 NormalZ=1 AngleXU=0 Radius=10 StartAngle=3.14159 EndAngle=4.71239
    g1: ArcOfCircle CenterX=224.5 CenterY=-32 CenterZ=0 NormalX=0 NormalY=0 NormalZ=1 AngleXU=0 Radius=10 StartAngle=4.71239 EndAngle=6.28319
    g2: LineSegment StartX=170.5 StartY=-32 StartZ=0 EndX=170.5 EndY=0 EndZ=0
    g3: LineSegment StartX=234.5 StartY=0 StartZ=0 EndX=234.5 EndY=-32 EndZ=0
    g4: LineSegment StartX=180.5 StartY=-42 StartZ=0 EndX=224.5 EndY=-42 EndZ=0
    g5: LineSegment StartX=167.5 StartY=0 StartZ=0 EndX=167.5 EndY=-32 EndZ=0
    g6: LineSegment StartX=180.5 StartY=-45 StartZ=0 EndX=224.5 EndY=-45 EndZ=0
    g7: LineSegment StartX=237.5 StartY=0 StartZ=0 EndX=237.5 EndY=-32 EndZ=0
    g8: ArcOfCircle CenterX=180.5 CenterY=-32 CenterZ=0 NormalX=0 NormalY=0 NormalZ=1 AngleXU=0 Radius=13 StartAngle=3.14159 EndAngle=4.71239
    g9: ArcOfCircle CenterX=224.5 CenterY=-32 CenterZ=0 NormalX=0 NormalY=0 NormalZ=1 AngleXU=0 Radius=13 StartAngle=4.71239 EndAngle=6.28319
    g10: LineSegment StartX=167.5 StartY=0 StartZ=0 EndX=170.5 EndY=0 EndZ=0
    g11: LineSegment StartX=234.5 StartY=0 StartZ=0 EndX=237.5 EndY=0 EndZ=0
  constraints (40):
    c: Angle(g1) = 1.5708
    c: DistanceY(g1,g1) = 0
    c: DistanceY(g1,g0) = 0
    c: Angle(g0) = 1.5708
    c: DistanceX(g0,g0) = 10
    c: DistanceY(g0,g0) = 0
    c: DistanceX(g1,g1) = 10
    c: Coincident(g2,g0)
    c: Vertical(g2)
    c: PointOnObject(g3,g-1)
    c: Coincident(g3,g1)
    c: Vertical(g3)
    c: DistanceY(g2,g2) = 32
    c: Coincident(g4,g1)
    c: PointOnObject(g5,g-1)
    c: Vertical(g5)
    c: Horizontal(g6)
    c: Vertical(g7)
    c: DistanceX(g5,g2) = 3
    c: DistanceX(g3,g7) = 3
    c: DistanceY(g5,g0) = 0
    c: DistanceY(g7,g1) = 0
    c: DistanceY(g7,g3) = 0
    c: DistanceX(g2,g3) = 64
    c: DistanceX(g0,g6) = 0
    c: DistanceX(g6,g1) = 0
    c: DistanceY(g2) = 0
    c: Coincident(g5,g8)
    c: Coincident(g6,g8)
    c: DistanceY(g6,g0) = 3
    c: Coincident(g6,g9)
    c: Coincident(g7,g9)
    c: Angle(g8) = 1.5708
    c: Angle(g9) = 1.5708
    c: Coincident(g10,g5)
    c: Coincident(g10,g2)
    c: Coincident(g11,g3)
    c: Coincident(g11,g7)
    c: Coincident(g0,g4)
    c: DistanceX(g2) = 170.5
FEATURE [Sketcher::SketchObject] Sketch061  label="outerSRS012"
  ArcFitTolerance = 0
  FullyConstrained = true
  MakeInternals = false
  Placement = pos=(0,0,-80) rot=(0,0,1;0rad)
  sketch-geometry (12):
    g0: ArcOfCircle CenterX=180.5 CenterY=-32 CenterZ=0 NormalX=0 NormalY=0 NormalZ=1 AngleXU=0 Radius=20 StartAngle=3.14159 EndAngle=4.71239
    g1: ArcOfCircle CenterX=224.5 CenterY=-32 CenterZ=0 NormalX=0 NormalY=0 NormalZ=1 AngleXU=0 Radius=20 StartAngle=4.71239 EndAngle=6.28319
    g2: LineSegment StartX=160.5 StartY=-32 StartZ=0 EndX=160.5 EndY=0 EndZ=0
    g3: LineSegment StartX=244.5 StartY=0 StartZ=0 EndX=244.5 EndY=-32 EndZ=0
    g4: LineSegment StartX=180.5 StartY=-52 StartZ=0 EndX=224.5 EndY=-52 EndZ=0
    g5: LineSegment StartX=157.5 StartY=0 StartZ=0 EndX=157.5 EndY=-32 EndZ=0
    g6: LineSegment StartX=180.5 StartY=-55 StartZ=0 EndX=224.5 EndY=-55 EndZ=0
    g7: LineSegment StartX=247.5 StartY=0 StartZ=0 EndX=247.5 EndY=-32 EndZ=0
    g8: ArcOfCircle CenterX=180.5 CenterY=-32 CenterZ=0 NormalX=0 NormalY=0 NormalZ=1 AngleXU=0 Radius=23 StartAngle=3.14159 EndAngle=4.71239
    g9: ArcOfCircle CenterX=224.5 CenterY=-32 CenterZ=0 NormalX=0 NormalY=0 NormalZ=1 AngleXU=0 Radius=23 StartAngle=4.71239 EndAngle=6.28319
    g10: LineSegment StartX=157.5 StartY=0 StartZ=0 EndX=160.5 EndY=0 EndZ=0
    g11: LineSegment StartX=244.5 StartY=0 StartZ=0 EndX=247.5 EndY=0 EndZ=0
  constraints (40):
    c: Angle(g1) = 1.5708
    c: DistanceY(g1,g0) = 0
    c: Angle(g0) = 1.5708
    c: DistanceY(g0,g0) = 0
    c: Coincident(g2,g0)
    c: Vertical(g2)
    c: PointOnObject(g3,g-1)
    c: Coincident(g3,g1)
    c: Vertical(g3)
    c: DistanceY(g2,g2) = 32
    c: Coincident(g4,g1)
    c: PointOnObject(g5,g-1)
    c: Vertical(g5)
    c: Horizontal(g6)
    c: Vertical(g7)
    c: DistanceX(g5,g2) = 3
    c: DistanceX(g3,g7) = 3
    c: DistanceY(g5,g0) = 0
    c: DistanceY(g7,g1) = 0
    c: DistanceY(g7,g3) = 0
    c: DistanceX(g2) = 160.5
    c: DistanceX(g2,g3) = 84
    c: DistanceX(g0,g6) = 0
    c: DistanceX(g6,g1) = 0
    c: DistanceY(g2) = 0
    c: Coincident(g5,g8)
    c: Coincident(g6,g8)
    c: DistanceY(g6,g0) = 3
    c: Coincident(g6,g9)
    c: Coincident(g7,g9)
    c: Angle(g8) = 1.5708
    c: Angle(g9) = 1.5708
    c: Coincident(g10,g5)
    c: Coincident(g10,g2)
    c: Coincident(g11,g3)
    c: Coincident(g11,g7)
    c: DistanceY(g0,g0) = 20
    c: Coincident(g0,g4)
    c: DistanceY(g1,g0) = 0
    c: DistanceY(g1,g1) = 0
FEATURE [Part::Loft] Loft012  label="srs013"
  Closed = false
  MaxDegree = 5
  Ruled = false
  Sections = -> [Sketch060,Sketch061]
  Solid = true
FEATURE [Part::Fillet] Fillet015  label="srsCovers012"
  Base = -> Loft012
  EdgeLinks = -> Loft012 [Edge1,Edge3,Edge5,Edge7,Edge8,Edge10,Edge11,Edge13,Edge14,Edge16,Edge17,Edge19,Edge20,Edge22,Edge23,Edge25,Edge26,Edge28,Edge29,Edge31,Edge32,Edge34,Edge35,Edge36]
  Edges = 24 edges r=1: [Edge1,Edge3,Edge5,Edge7,Edge8,Edge10,Edge11,Edge13,Edge14,Edge16,Edge17,Edge19,Edge20,Edge22,Edge23,Edge25,Edge26,Edge28,Edge29,Edge31,Edge32,Edge34,Edge35,Edge36]
  Placement = pos=(0,0,116) rot=(0,0,1;0rad)
FEATURE [Sketcher::SketchObject] Sketch062  label="innerSRS013"
  ArcFitTolerance = 0
  FullyConstrained = true
  MakeInternals = false
  Placement = pos=(0,0,-65) rot=(0,0,1;0rad)
  sketch-geometry (12):
    g0: ArcOfCircle CenterX=180.5 CenterY=-32 CenterZ=0 NormalX=0 NormalY=0 NormalZ=1 AngleXU=0 Radius=10 StartAngle=3.14159 EndAngle=4.71239
    g1: ArcOfCircle CenterX=224.5 CenterY=-32 CenterZ=0 NormalX=0 NormalY=0 NormalZ=1 AngleXU=0 Radius=10 StartAngle=4.71239 EndAngle=6.28319
    g2: LineSegment StartX=170.5 StartY=-32 StartZ=0 EndX=170.5 EndY=0 EndZ=0
    g3: LineSegment StartX=234.5 StartY=0 StartZ=0 EndX=234.5 EndY=-32 EndZ=0
    g4: LineSegment StartX=180.5 StartY=-42 StartZ=0 EndX=224.5 EndY=-42 EndZ=0
    g5: LineSegment StartX=167.5 StartY=0 StartZ=0 EndX=167.5 EndY=-32 EndZ=0
    g6: LineSegment StartX=180.5 StartY=-45 StartZ=0 EndX=224.5 EndY=-45 EndZ=0
    g7: LineSegment StartX=237.5 StartY=0 StartZ=0 EndX=237.5 EndY=-32 EndZ=0
    g8: ArcOfCircle CenterX=180.5 CenterY=-32 CenterZ=0 NormalX=0 NormalY=0 NormalZ=1 AngleXU=0 Radius=13 StartAngle=3.14159 EndAngle=4.71239
    g9: ArcOfCircle CenterX=224.5 CenterY=-32 CenterZ=0 NormalX=0 NormalY=0 NormalZ=1 AngleXU=0 Radius=13 StartAngle=4.71239 EndAngle=6.28319
    g10: LineSegment StartX=167.5 StartY=0 StartZ=0 EndX=170.5 EndY=0 EndZ=0
    g11: LineSegment StartX=234.5 StartY=0 StartZ=0 EndX=237.5 EndY=0 EndZ=0
  constraints (40):
    c: Angle(g1) = 1.5708
    c: DistanceY(g1,g1) = 0
    c: DistanceY(g1,g0) = 0
    c: Angle(g0) = 1.5708
    c: DistanceX(g0,g0) = 10
    c: DistanceY(g0,g0) = 0
    c: DistanceX(g1,g1) = 10
    c: Coincident(g2,g0)
    c: Vertical(g2)
    c: PointOnObject(g3,g-1)
    c: Coincident(g3,g1)
    c: Vertical(g3)
    c: DistanceY(g2,g2) = 32
    c: Coincident(g4,g1)
    c: PointOnObject(g5,g-1)
    c: Vertical(g5)
    c: Horizontal(g6)
    c: Vertical(g7)
    c: DistanceX(g5,g2) = 3
    c: DistanceX(g3,g7) = 3
    c: DistanceY(g5,g0) = 0
    c: DistanceY(g7,g1) = 0
    c: DistanceY(g7,g3) = 0
    c: DistanceX(g2,g3) = 64
    c: DistanceX(g0,g6) = 0
    c: DistanceX(g6,g1) = 0
    c: DistanceY(g2) = 0
    c: Coincident(g5,g8)
    c: Coincident(g6,g8)
    c: DistanceY(g6,g0) = 3
    c: Coincident(g6,g9)
    c: Coincident(g7,g9)
    c: Angle(g8) = 1.5708
    c: Angle(g9) = 1.5708
    c: Coincident(g10,g5)
    c: Coincident(g10,g2)
    c: Coincident(g11,g3)
    c: Coincident(g11,g7)
    c: Coincident(g0,g4)
    c: DistanceX(g2) = 170.5
FEATURE [Sketcher::SketchObject] Sketch063  label="outerSRS013"
  ArcFitTolerance = 0
  FullyConstrained = true
  MakeInternals = false
  Placement = pos=(0,0,-80) rot=(0,0,1;0rad)
  sketch-geometry (12):
    g0: ArcOfCircle CenterX=180.5 CenterY=-32 CenterZ=0 NormalX=0 NormalY=0 NormalZ=1 AngleXU=0 Radius=20 StartAngle=3.14159 EndAngle=4.71239
    g1: ArcOfCircle CenterX=224.5 CenterY=-32 CenterZ=0 NormalX=0 NormalY=0 NormalZ=1 AngleXU=0 Radius=20 StartAngle=4.71239 EndAngle=6.28319
    g2: LineSegment StartX=160.5 StartY=-32 StartZ=0 EndX=160.5 EndY=0 EndZ=0
    g3: LineSegment StartX=244.5 StartY=0 StartZ=0 EndX=244.5 EndY=-32 EndZ=0
    g4: LineSegment StartX=180.5 StartY=-52 StartZ=0 EndX=224.5 EndY=-52 EndZ=0
    g5: LineSegment StartX=157.5 StartY=0 StartZ=0 EndX=157.5 EndY=-32 EndZ=0
    g6: LineSegment StartX=180.5 StartY=-55 StartZ=0 EndX=224.5 EndY=-55 EndZ=0
    g7: LineSegment StartX=247.5 StartY=0 StartZ=0 EndX=247.5 EndY=-32 EndZ=0
    g8: ArcOfCircle CenterX=180.5 CenterY=-32 CenterZ=0 NormalX=0 NormalY=0 NormalZ=1 AngleXU=0 Radius=23 StartAngle=3.14159 EndAngle=4.71239
    g9: ArcOfCircle CenterX=224.5 CenterY=-32 CenterZ=0 NormalX=0 NormalY=0 NormalZ=1 AngleXU=0 Radius=23 StartAngle=4.71239 EndAngle=6.28319
    g10: LineSegment StartX=157.5 StartY=0 StartZ=0 EndX=160.5 EndY=0 EndZ=0
    g11: LineSegment StartX=244.5 StartY=0 StartZ=0 EndX=247.5 EndY=0 EndZ=0
  constraints (40):
    c: Angle(g1) = 1.5708
    c: DistanceY(g1,g0) = 0
    c: Angle(g0) = 1.5708
    c: DistanceY(g0,g0) = 0
    c: Coincident(g2,g0)
    c: Vertical(g2)
    c: PointOnObject(g3,g-1)
    c: Coincident(g3,g1)
    c: Vertical(g3)
    c: DistanceY(g2,g2) = 32
    c: Coincident(g4,g1)
    c: PointOnObject(g5,g-1)
    c: Vertical(g5)
    c: Horizontal(g6)
    c: Vertical(g7)
    c: DistanceX(g5,g2) = 3
    c: DistanceX(g3,g7) = 3
    c: DistanceY(g5,g0) = 0
    c: DistanceY(g7,g1) = 0
    c: DistanceY(g7,g3) = 0
    c: DistanceX(g2) = 160.5
    c: DistanceX(g2,g3) = 84
    c: DistanceX(g0,g6) = 0
    c: DistanceX(g6,g1) = 0
    c: DistanceY(g2) = 0
    c: Coincident(g5,g8)
    c: Coincident(g6,g8)
    c: DistanceY(g6,g0) = 3
    c: Coincident(g6,g9)
    c: Coincident(g7,g9)
    c: Angle(g8) = 1.5708
    c: Angle(g9) = 1.5708
    c: Coincident(g10,g5)
    c: Coincident(g10,g2)
    c: Coincident(g11,g3)
    c: Coincident(g11,g7)
    c: DistanceY(g0,g0) = 20
    c: Coincident(g0,g4)
    c: DistanceY(g1,g0) = 0
    c: DistanceY(g1,g1) = 0
FEATURE [Part::Loft] Loft013  label="srs014"
  Closed = false
  MaxDegree = 5
  Ruled = false
  Sections = -> [Sketch062,Sketch063]
  Solid = true
FEATURE [Part::Fillet] Fillet016  label="srsCovers013"
  Base = -> Loft013
  EdgeLinks = -> Loft013 [Edge1,Edge3,Edge5,Edge7,Edge8,Edge10,Edge11,Edge13,Edge14,Edge16,Edge17,Edge19,Edge20,Edge22,Edge23,Edge25,Edge26,Edge28,Edge29,Edge31,Edge32,Edge34,Edge35,Edge36]
  Edges = 24 edges r=1: [Edge1,Edge3,Edge5,Edge7,Edge8,Edge10,Edge11,Edge13,Edge14,Edge16,Edge17,Edge19,Edge20,Edge22,Edge23,Edge25,Edge26,Edge28,Edge29,Edge31,Edge32,Edge34,Edge35,Edge36]
  Placement = pos=(0,0,125.67) rot=(0,0,1;0rad)
FEATURE [Sketcher::SketchObject] Sketch064  label="innerSRS014"
  ArcFitTolerance = 0
  FullyConstrained = true
  MakeInternals = false
  Placement = pos=(0,0,-65) rot=(0,0,1;0rad)
  sketch-geometry (12):
    g0: ArcOfCircle CenterX=180.5 CenterY=-32 CenterZ=0 NormalX=0 NormalY=0 NormalZ=1 AngleXU=0 Radius=10 StartAngle=3.14159 EndAngle=4.71239
    g1: ArcOfCircle CenterX=224.5 CenterY=-32 CenterZ=0 NormalX=0 NormalY=0 NormalZ=1 AngleXU=0 Radius=10 StartAngle=4.71239 EndAngle=6.28319
    g2: LineSegment StartX=170.5 StartY=-32 StartZ=0 EndX=170.5 EndY=0 EndZ=0
    g3: LineSegment StartX=234.5 StartY=0 StartZ=0 EndX=234.5 EndY=-32 EndZ=0
    g4: LineSegment StartX=180.5 StartY=-42 StartZ=0 EndX=224.5 EndY=-42 EndZ=0
    g5: LineSegment StartX=167.5 StartY=0 StartZ=0 EndX=167.5 EndY=-32 EndZ=0
    g6: LineSegment StartX=180.5 StartY=-45 StartZ=0 EndX=224.5 EndY=-45 EndZ=0
    g7: LineSegment StartX=237.5 StartY=0 StartZ=0 EndX=237.5 EndY=-32 EndZ=0
    g8: ArcOfCircle CenterX=180.5 CenterY=-32 CenterZ=0 NormalX=0 NormalY=0 NormalZ=1 AngleXU=0 Radius=13 StartAngle=3.14159 EndAngle=4.71239
    g9: ArcOfCircle CenterX=224.5 CenterY=-32 CenterZ=0 NormalX=0 NormalY=0 NormalZ=1 AngleXU=0 Radius=13 StartAngle=4.71239 EndAngle=6.28319
    g10: LineSegment StartX=167.5 StartY=0 StartZ=0 EndX=170.5 EndY=0 EndZ=0
    g11: LineSegment StartX=234.5 StartY=0 StartZ=0 EndX=237.5 EndY=0 EndZ=0
  constraints (40):
    c: Angle(g1) = 1.5708
    c: DistanceY(g1,g1) = 0
    c: DistanceY(g1,g0) = 0
    c: Angle(g0) = 1.5708
    c: DistanceX(g0,g0) = 10
    c: DistanceY(g0,g0) = 0
    c: DistanceX(g1,g1) = 10
    c: Coincident(g2,g0)
    c: Vertical(g2)
    c: PointOnObject(g3,g-1)
    c: Coincident(g3,g1)
    c: Vertical(g3)
    c: DistanceY(g2,g2) = 32
    c: Coincident(g4,g1)
    c: PointOnObject(g5,g-1)
    c: Vertical(g5)
    c: Horizontal(g6)
    c: Vertical(g7)
    c: DistanceX(g5,g2) = 3
    c: DistanceX(g3,g7) = 3
    c: DistanceY(g5,g0) = 0
    c: DistanceY(g7,g1) = 0
    c: DistanceY(g7,g3) = 0
    c: DistanceX(g2,g3) = 64
    c: DistanceX(g0,g6) = 0
    c: DistanceX(g6,g1) = 0
    c: DistanceY(g2) = 0
    c: Coincident(g5,g8)
    c: Coincident(g6,g8)
    c: DistanceY(g6,g0) = 3
    c: Coincident(g6,g9)
    c: Coincident(g7,g9)
    c: Angle(g8) = 1.5708
    c: Angle(g9) = 1.5708
    c: Coincident(g10,g5)
    c: Coincident(g10,g2)
    c: Coincident(g11,g3)
    c: Coincident(g11,g7)
    c: Coincident(g0,g4)
    c: DistanceX(g2) = 170.5
FEATURE [Sketcher::SketchObject] Sketch065  label="outerSRS014"
  ArcFitTolerance = 0
  FullyConstrained = true
  MakeInternals = false
  Placement = pos=(0,0,-80) rot=(0,0,1;0rad)
  sketch-geometry (12):
    g0: ArcOfCircle CenterX=180.5 CenterY=-32 CenterZ=0 NormalX=0 NormalY=0 NormalZ=1 AngleXU=0 Radius=20 StartAngle=3.14159 EndAngle=4.71239
    g1: ArcOfCircle CenterX=224.5 CenterY=-32 CenterZ=0 NormalX=0 NormalY=0 NormalZ=1 AngleXU=0 Radius=20 StartAngle=4.71239 EndAngle=6.28319
    g2: LineSegment StartX=160.5 StartY=-32 StartZ=0 EndX=160.5 EndY=0 EndZ=0
    g3: LineSegment StartX=244.5 StartY=0 StartZ=0 EndX=244.5 EndY=-32 EndZ=0
    g4: LineSegment StartX=180.5 StartY=-52 StartZ=0 EndX=224.5 EndY=-52 EndZ=0
    g5: LineSegment StartX=157.5 StartY=0 StartZ=0 EndX=157.5 EndY=-32 EndZ=0
    g6: LineSegment StartX=180.5 StartY=-55 StartZ=0 EndX=224.5 EndY=-55 EndZ=0
    g7: LineSegment StartX=247.5 StartY=0 StartZ=0 EndX=247.5 EndY=-32 EndZ=0
    g8: ArcOfCircle CenterX=180.5 CenterY=-32 CenterZ=0 NormalX=0 NormalY=0 NormalZ=1 AngleXU=0 Radius=23 StartAngle=3.14159 EndAngle=4.71239
    g9: ArcOfCircle CenterX=224.5 CenterY=-32 CenterZ=0 NormalX=0 NormalY=0 NormalZ=1 AngleXU=0 Radius=23 StartAngle=4.71239 EndAngle=6.28319
    g10: LineSegment StartX=157.5 StartY=0 StartZ=0 EndX=160.5 EndY=0 EndZ=0
    g11: LineSegment StartX=244.5 StartY=0 StartZ=0 EndX=247.5 EndY=0 EndZ=0
  constraints (40):
    c: Angle(g1) = 1.5708
    c: DistanceY(g1,g0) = 0
    c: Angle(g0) = 1.5708
    c: DistanceY(g0,g0) = 0
    c: Coincident(g2,g0)
    c: Vertical(g2)
    c: PointOnObject(g3,g-1)
    c: Coincident(g3,g1)
    c: Vertical(g3)
    c: DistanceY(g2,g2) = 32
    c: Coincident(g4,g1)
    c: PointOnObject(g5,g-1)
    c: Vertical(g5)
    c: Horizontal(g6)
    c: Vertical(g7)
    c: DistanceX(g5,g2) = 3
    c: DistanceX(g3,g7) = 3
    c: DistanceY(g5,g0) = 0
    c: DistanceY(g7,g1) = 0
    c: DistanceY(g7,g3) = 0
    c: DistanceX(g2) = 160.5
    c: DistanceX(g2,g3) = 84
    c: DistanceX(g0,g6) = 0
    c: DistanceX(g6,g1) = 0
    c: DistanceY(g2) = 0
    c: Coincident(g5,g8)
    c: Coincident(g6,g8)
    c: DistanceY(g6,g0) = 3
    c: Coincident(g6,g9)
    c: Coincident(g7,g9)
    c: Angle(g8) = 1.5708
    c: Angle(g9) = 1.5708
    c: Coincident(g10,g5)
    c: Coincident(g10,g2)
    c: Coincident(g11,g3)
    c: Coincident(g11,g7)
    c: DistanceY(g0,g0) = 20
    c: Coincident(g0,g4)
    c: DistanceY(g1,g0) = 0
    c: DistanceY(g1,g1) = 0
FEATURE [Part::Loft] Loft014  label="srs015"
  Closed = false
  MaxDegree = 5
  Ruled = false
  Sections = -> [Sketch064,Sketch065]
  Solid = true
FEATURE [Part::Fillet] Fillet017  label="srsCovers014"
  Base = -> Loft014
  EdgeLinks = -> Loft014 [Edge1,Edge3,Edge5,Edge7,Edge8,Edge10,Edge11,Edge13,Edge14,Edge16,Edge17,Edge19,Edge20,Edge22,Edge23,Edge25,Edge26,Edge28,Edge29,Edge31,Edge32,Edge34,Edge35,Edge36]
  Edges = 24 edges r=1: [Edge1,Edge3,Edge5,Edge7,Edge8,Edge10,Edge11,Edge13,Edge14,Edge16,Edge17,Edge19,Edge20,Edge22,Edge23,Edge25,Edge26,Edge28,Edge29,Edge31,Edge32,Edge34,Edge35,Edge36]
  Placement = pos=(0,0,135.33) rot=(0,0,1;0rad)
FEATURE [Sketcher::SketchObject] Sketch066  label="innerSRS015"
  ArcFitTolerance = 0
  FullyConstrained = true
  MakeInternals = false
  Placement = pos=(0,0,-65) rot=(0,0,1;0rad)
  sketch-geometry (12):
    g0: ArcOfCircle CenterX=180.5 CenterY=-32 CenterZ=0 NormalX=0 NormalY=0 NormalZ=1 AngleXU=0 Radius=10 StartAngle=3.14159 EndAngle=4.71239
    g1: ArcOfCircle CenterX=224.5 CenterY=-32 CenterZ=0 NormalX=0 NormalY=0 NormalZ=1 AngleXU=0 Radius=10 StartAngle=4.71239 EndAngle=6.28319
    g2: LineSegment StartX=170.5 StartY=-32 StartZ=0 EndX=170.5 EndY=0 EndZ=0
    g3: LineSegment StartX=234.5 StartY=0 StartZ=0 EndX=234.5 EndY=-32 EndZ=0
    g4: LineSegment StartX=180.5 StartY=-42 StartZ=0 EndX=224.5 EndY=-42 EndZ=0
    g5: LineSegment StartX=167.5 StartY=0 StartZ=0 EndX=167.5 EndY=-32 EndZ=0
    g6: LineSegment StartX=180.5 StartY=-45 StartZ=0 EndX=224.5 EndY=-45 EndZ=0
    g7: LineSegment StartX=237.5 StartY=0 StartZ=0 EndX=237.5 EndY=-32 EndZ=0
    g8: ArcOfCircle CenterX=180.5 CenterY=-32 CenterZ=0 NormalX=0 NormalY=0 NormalZ=1 AngleXU=0 Radius=13 StartAngle=3.14159 EndAngle=4.71239
    g9: ArcOfCircle CenterX=224.5 CenterY=-32 CenterZ=0 NormalX=0 NormalY=0 NormalZ=1 AngleXU=0 Radius=13 StartAngle=4.71239 EndAngle=6.28319
    g10: LineSegment StartX=167.5 StartY=0 StartZ=0 EndX=170.5 EndY=0 EndZ=0
    g11: LineSegment StartX=234.5 StartY=0 StartZ=0 EndX=237.5 EndY=0 EndZ=0
  constraints (40):
    c: Angle(g1) = 1.5708
    c: DistanceY(g1,g1) = 0
    c: DistanceY(g1,g0) = 0
    c: Angle(g0) = 1.5708
    c: DistanceX(g0,g0) = 10
    c: DistanceY(g0,g0) = 0
    c: DistanceX(g1,g1) = 10
    c: Coincident(g2,g0)
    c: Vertical(g2)
    c: PointOnObject(g3,g-1)
    c: Coincident(g3,g1)
    c: Vertical(g3)
    c: DistanceY(g2,g2) = 32
    c: Coincident(g4,g1)
    c: PointOnObject(g5,g-1)
    c: Vertical(g5)
    c: Horizontal(g6)
    c: Vertical(g7)
    c: DistanceX(g5,g2) = 3
    c: DistanceX(g3,g7) = 3
    c: DistanceY(g5,g0) = 0
    c: DistanceY(g7,g1) = 0
    c: DistanceY(g7,g3) = 0
    c: DistanceX(g2,g3) = 64
    c: DistanceX(g0,g6) = 0
    c: DistanceX(g6,g1) = 0
    c: DistanceY(g2) = 0
    c: Coincident(g5,g8)
    c: Coincident(g6,g8)
    c: DistanceY(g6,g0) = 3
    c: Coincident(g6,g9)
    c: Coincident(g7,g9)
    c: Angle(g8) = 1.5708
    c: Angle(g9) = 1.5708
    c: Coincident(g10,g5)
    c: Coincident(g10,g2)
    c: Coincident(g11,g3)
    c: Coincident(g11,g7)
    c: Coincident(g0,g4)
    c: DistanceX(g2) = 170.5
FEATURE [Sketcher::SketchObject] Sketch067  label="outerSRS015"
  ArcFitTolerance = 0
  FullyConstrained = true
  MakeInternals = false
  Placement = pos=(0,0,-80) rot=(0,0,1;0rad)
  sketch-geometry (12):
    g0: ArcOfCircle CenterX=180.5 CenterY=-32 CenterZ=0 NormalX=0 NormalY=0 NormalZ=1 AngleXU=0 Radius=20 StartAngle=3.14159 EndAngle=4.71239
    g1: ArcOfCircle CenterX=224.5 CenterY=-32 CenterZ=0 NormalX=0 NormalY=0 NormalZ=1 AngleXU=0 Radius=20 StartAngle=4.71239 EndAngle=6.28319
    g2: LineSegment StartX=160.5 StartY=-32 StartZ=0 EndX=160.5 EndY=0 EndZ=0
    g3: LineSegment StartX=244.5 StartY=0 StartZ=0 EndX=244.5 EndY=-32 EndZ=0
    g4: LineSegment StartX=180.5 StartY=-52 StartZ=0 EndX=224.5 EndY=-52 EndZ=0
    g5: LineSegment StartX=157.5 StartY=0 StartZ=0 EndX=157.5 EndY=-32 EndZ=0
    g6: LineSegment StartX=180.5 StartY=-55 StartZ=0 EndX=224.5 EndY=-55 EndZ=0
    g7: LineSegment StartX=247.5 StartY=0 StartZ=0 EndX=247.5 EndY=-32 EndZ=0
    g8: ArcOfCircle CenterX=180.5 CenterY=-32 CenterZ=0 NormalX=0 NormalY=0 NormalZ=1 AngleXU=0 Radius=23 StartAngle=3.14159 EndAngle=4.71239
    g9: ArcOfCircle CenterX=224.5 CenterY=-32 CenterZ=0 NormalX=0 NormalY=0 NormalZ=1 AngleXU=0 Radius=23 StartAngle=4.71239 EndAngle=6.28319
    g10: LineSegment StartX=157.5 StartY=0 StartZ=0 EndX=160.5 EndY=0 EndZ=0
    g11: LineSegment StartX=244.5 StartY=0 StartZ=0 EndX=247.5 EndY=0 EndZ=0
  constraints (40):
    c: Angle(g1) = 1.5708
    c: DistanceY(g1,g0) = 0
    c: Angle(g0) = 1.5708
    c: DistanceY(g0,g0) = 0
    c: Coincident(g2,g0)
    c: Vertical(g2)
    c: PointOnObject(g3,g-1)
    c: Coincident(g3,g1)
    c: Vertical(g3)
    c: DistanceY(g2,g2) = 32
    c: Coincident(g4,g1)
    c: PointOnObject(g5,g-1)
    c: Vertical(g5)
    c: Horizontal(g6)
    c: Vertical(g7)
    c: DistanceX(g5,g2) = 3
    c: DistanceX(g3,g7) = 3
    c: DistanceY(g5,g0) = 0
    c: DistanceY(g7,g1) = 0
    c: DistanceY(g7,g3) = 0
    c: DistanceX(g2) = 160.5
    c: DistanceX(g2,g3) = 84
    c: DistanceX(g0,g6) = 0
    c: DistanceX(g6,g1) = 0
    c: DistanceY(g2) = 0
    c: Coincident(g5,g8)
    c: Coincident(g6,g8)
    c: DistanceY(g6,g0) = 3
    c: Coincident(g6,g9)
    c: Coincident(g7,g9)
    c: Angle(g8) = 1.5708
    c: Angle(g9) = 1.5708
    c: Coincident(g10,g5)
    c: Coincident(g10,g2)
    c: Coincident(g11,g3)
    c: Coincident(g11,g7)
    c: DistanceY(g0,g0) = 20
    c: Coincident(g0,g4)
    c: DistanceY(g1,g0) = 0
    c: DistanceY(g1,g1) = 0
FEATURE [Part::Loft] Loft015  label="srs016"
  Closed = false
  MaxDegree = 5
  Ruled = false
  Sections = -> [Sketch066,Sketch067]
  Solid = true
FEATURE [Part::Fillet] Fillet018  label="srsCovers015"
  Base = -> Loft015
  EdgeLinks = -> Loft015 [Edge1,Edge3,Edge5,Edge7,Edge8,Edge10,Edge11,Edge13,Edge14,Edge16,Edge17,Edge19,Edge20,Edge22,Edge23,Edge25,Edge26,Edge28,Edge29,Edge31,Edge32,Edge34,Edge35,Edge36]
  Edges = 24 edges r=1: [Edge1,Edge3,Edge5,Edge7,Edge8,Edge10,Edge11,Edge13,Edge14,Edge16,Edge17,Edge19,Edge20,Edge22,Edge23,Edge25,Edge26,Edge28,Edge29,Edge31,Edge32,Edge34,Edge35,Edge36]
  Placement = pos=(0,0,145) rot=(0,0,1;0rad)
FEATURE [Sketcher::SketchObject] Sketch068  label="innerSRS016"
  ArcFitTolerance = 0
  FullyConstrained = true
  MakeInternals = false
  Placement = pos=(0,0,77) rot=(0,0,1;0rad)
  sketch-geometry (6):
    g0: LineSegment StartX=167.5 StartY=0 StartZ=0 EndX=167.5 EndY=-32 EndZ=0
    g1: LineSegment StartX=180.5 StartY=-45 StartZ=0 EndX=224.5 EndY=-45 EndZ=0
    g2: LineSegment StartX=237.5 StartY=0 StartZ=0 EndX=237.5 EndY=-32 EndZ=0
    g3: ArcOfCircle CenterX=180.5 CenterY=-32 CenterZ=0 NormalX=0 NormalY=0 NormalZ=1 AngleXU=0 Radius=13 StartAngle=3.14159 EndAngle=4.71239
    g4: ArcOfCircle CenterX=224.5 CenterY=-32 CenterZ=0 NormalX=0 NormalY=0 NormalZ=1 AngleXU=0 Radius=13 StartAngle=4.71239 EndAngle=6.28319
    g5: LineSegment StartX=167.5 StartY=0 StartZ=0 EndX=237.5 EndY=0 EndZ=0
  constraints (20):
    c: PointOnObject(g0,g-1)
    c: Vertical(g0)
    c: Horizontal(g1)
    c: Vertical(g2)
    c: DistanceY(g5) = 0
    c: Coincident(g0,g3)
    c: Coincident(g1,g3)
    c: Coincident(g1,g4)
    c: Coincident(g2,g4)
    c: Angle(g3) = 1.5708
    c: Angle(g4) = 1.5708
    c: Coincident(g5,g0)
    c: DistanceX(g0,g3) = 13
    c: DistanceY(g0,g0) = 32
    c: DistanceY(g1,g0) = 13
    c: DistanceY(g3,g4) = 0
    c: DistanceY(g2,g3) = 0
    c: DistanceX(g0) = 167.5
    c: Coincident(g5,g2)
    c: DistanceX(g1,g1) = 44
FEATURE [Sketcher::SketchObject] Sketch069  label="outerSRS016"
  ArcFitTolerance = 0
  FullyConstrained = true
  MakeInternals = false
  Placement = pos=(0,0,-80) rot=(0,0,1;0rad)
  sketch-geometry (6):
    g0: LineSegment StartX=157.5 StartY=0 StartZ=0 EndX=157.5 EndY=-32 EndZ=0
    g1: LineSegment StartX=180.5 StartY=-55 StartZ=0 EndX=224.5 EndY=-55 EndZ=0
    g2: LineSegment StartX=247.5 StartY=0 StartZ=0 EndX=247.5 EndY=-32 EndZ=0
    g3: ArcOfCircle CenterX=180.5 CenterY=-32 CenterZ=0 NormalX=0 NormalY=0 NormalZ=1 AngleXU=0 Radius=23 StartAngle=3.14159 EndAngle=4.71239
    g4: ArcOfCircle CenterX=224.5 CenterY=-32 CenterZ=0 NormalX=0 NormalY=0 NormalZ=1 AngleXU=0 Radius=23 StartAngle=4.71239 EndAngle=6.28319
    g5: LineSegment StartX=157.5 StartY=0 StartZ=0 EndX=247.5 EndY=0 EndZ=0
  constraints (20):
    c: PointOnObject(g5,g-1)
    c: Vertical(g0)
    c: Horizontal(g1)
    c: Vertical(g2)
    c: DistanceY(g2,g5) = 0
    c: Coincident(g0,g3)
    c: Coincident(g1,g3)
    c: Coincident(g1,g4)
    c: Coincident(g2,g4)
    c: Angle(g3) = 1.5708
    c: Angle(g4) = 1.5708
    c: Coincident(g5,g2)
    c: DistanceX(g0) = 157.5
    c: Coincident(g5,g0)
    c: DistanceX(g0,g2) = 90
    c: DistanceY(g0,g0) = 32
    c: DistanceY(g2,g0) = 0
    c: DistanceY(g3,g0) = 0
    c: DistanceY(g4,g2) = 0
    c: DistanceX(g0,g3) = 23
FEATURE [Part::Extrusion] Extrude004
  Base = -> Sketch069
  Dir = (0,0,1)
  DirMode = 2
  FaceMakerClass = Part::FaceMakerBullseye
  FaceMakerMode = 3
  LengthFwd = 3
  LengthRev = 0
  Solid = true
  Symmetric = false
FEATURE [Part::Fillet] Fillet019  label="srsBottom"
  Base = -> Extrude004
  EdgeLinks = -> Extrude004 [Edge3,Edge4,Edge6,Edge7,Edge9,Edge10,Edge12,Edge13,Edge15,Edge16,Edge17,Edge18]
  Edges = 12 edges r=1: [Edge3,Edge4,Edge6,Edge7,Edge9,Edge10,Edge12,Edge13,Edge15,Edge16,Edge17,Edge18]
FEATURE [Sketcher::SketchObject] Sketch072
  ArcFitTolerance = 0
  FullyConstrained = true
  MakeInternals = false
  Placement = pos=(0,0,0) rot=(1,0,0;1.5708rad)
  sketch-geometry (4):
    g0: LineSegment StartX=70 StartY=80 StartZ=0 EndX=247.5 EndY=80 EndZ=0
    g1: LineSegment StartX=247.5 StartY=80 StartZ=0 EndX=247.5 EndY=-80 EndZ=0
    g2: LineSegment StartX=247.5 StartY=-80 StartZ=0 EndX=70 EndY=-80 EndZ=0
    g3: LineSegment StartX=70 StartY=-80 StartZ=0 EndX=70 EndY=80 EndZ=0
  constraints (12):
    c: Coincident(g0,g1)
    c: Coincident(g1,g2)
    c: Coincident(g2,g3)
    c: Coincident(g3,g0)
    c: Horizontal(g0)
    c: Horizontal(g2)
    c: Vertical(g1)
    c: Vertical(g3)
    c: DistanceY(g2) = -80
    c: DistanceY(g0) = 80
    c: DistanceX(g2) = 70
    c: DistanceX(g2,g2) = 177.5
FEATURE [Part::Extrusion] Extrude007  label="srsCuts001"
  Base = -> Sketch072
  Dir = (0,-1,2e-16)
  DirMode = 2
  FaceMakerClass = Part::FaceMakerBullseye
  FaceMakerMode = 3
  LengthFwd = 4.1
  LengthRev = 0
  Solid = true
  Symmetric = false
FEATURE [Part::Extrusion] Extrude008
  Base = -> Sketch068
  Dir = (0,0,1)
  DirMode = 2
  FaceMakerClass = Part::FaceMakerBullseye
  FaceMakerMode = 3
  LengthFwd = 3
  LengthRev = 0
  Solid = true
  Symmetric = false
FEATURE [Part::Fillet] Fillet020  label="srsTop"
  Base = -> Extrude008
  EdgeLinks = -> Extrude008 [Edge4,Edge7,Edge10,Edge13,Edge16,Edge18]
  Edges = 6 edges r=1: [Edge4,Edge7,Edge10,Edge13,Edge16,Edge18]
FEATURE [Part::Cylinder] Cylinder002  label="srsM4Cut"
  Angle = 360
  AttacherType = Attacher::AttachEngine3D
  FirstAngle = 0
  Height = 21
  Placement = pos=(202.5,0,-60) rot=(1,0,0;2.35619rad)
  Radius = 2.25
  SecondAngle = 0
FEATURE [Part::Feature] Part__Feature265  label="M4s"
  Placement = pos=(202.5,-6.22435,-66.2756) rot=(-1,0,0;0.785398rad)
  shape: bbox 8.084 x 6.83 x 6.83 mm, 34 faces (baked)
FEATURE [Part::Feature] Part__Feature266  label="M3Nut"
  Placement = pos=(0,-1,18) rot=(-1,0,0;1.5708rad)
  shape: bbox 6.352 x 2.188 x 6.352 mm, 35 faces (baked)
FEATURE [Part::Feature] Part__Feature267  label="CAPC-0805-T0.95-BN v009"
  Placement = pos=(-5.48627,2.66154,1.6) rot=(0,0,-1;1.5708rad)
  shape: bbox 1.35 x 2.1 x 0.95 mm, 42 faces (baked)
FEATURE [Part::Feature] Part__Feature268  label="CAPC-0805-T0.95-BN v010"
  Placement = pos=(-3.43627,2.66154,1.6) rot=(0,0,-1;1.5708rad)
  shape: bbox 1.35 x 2.1 x 0.95 mm, 42 faces (baked)
FEATURE [Part::Feature] Part__Feature269  label="CAPC-0603-T0.9-BN v008"
  Placement = pos=(-1.69987,-3.28475,1.6) rot=(0,0,1;0rad)
  shape: bbox 1.7 x 0.9 x 0.9 mm, 42 faces (baked)
FEATURE [Part::Feature] Part__Feature270  label="BODY_MF06A002"
  Placement = pos=(0,0,0.762) rot=(0.57735,-0.57735,-0.57735;2.0944rad)
  shape: bbox 1.601 x 2.921 x 1.016 mm, 42 faces (baked)
FEATURE [Part::Feature] Part__Feature271  label="LEAD_MF06A012"
  Placement = pos=(-0.9652,-0.9525,0.1016) rot=(0.57735,-0.57735,-0.57735;2.0944rad)
  shape: bbox 0.6223 x 0.3749 x 0.8636 mm, 14 faces (baked)
FEATURE [Part::Feature] Part__Feature272  label="LEAD_MF06A013"
  Placement = pos=(-0.9652,0,0.1016) rot=(0.57735,-0.57735,-0.57735;2.0944rad)
  shape: bbox 0.6223 x 0.3749 x 0.8636 mm, 14 faces (baked)
FEATURE [Part::Feature] Part__Feature273  label="LEAD_MF06A014"
  Placement = pos=(-0.9652,0.9525,0.1016) rot=(0.57735,-0.57735,-0.57735;2.0944rad)
  shape: bbox 0.6223 x 0.3749 x 0.8636 mm, 14 faces (baked)
FEATURE [Part::Feature] Part__Feature274  label="LEAD_MF06A015"
  Placement = pos=(0.9652,-0.9525,0.1016) rot=(0.57735,0.57735,0.57735;2.0944rad)
  shape: bbox 0.6223 x 0.3749 x 0.8636 mm, 14 faces (baked)
FEATURE [Part::Feature] Part__Feature275  label="LEAD_MF06A016"
  Placement = pos=(0.9652,0,0.1016) rot=(0.57735,0.57735,0.57735;2.0944rad)
  shape: bbox 0.6223 x 0.3749 x 0.8636 mm, 14 faces (baked)
FEATURE [Part::Feature] Part__Feature276  label="LEAD_MF06A017"
  Placement = pos=(0.9652,0.9525,0.1016) rot=(0.57735,0.57735,0.57735;2.0944rad)
  shape: bbox 0.6223 x 0.3749 x 0.8636 mm, 14 faces (baked)
FEATURE [Part::Feature] Part__Feature277  label="SOT363 v004"
  Placement = pos=(4.97054,-0.645171,1.675) rot=(0,0,1;3.14159rad)
  shape: bbox 2.1 x 2 x 1.1 mm, 94 faces, 7 solids (baked)
FEATURE [Part::Feature] Part__Feature278  label="LED 0603 single color v004"
  Placement = pos=(-9.18406,3.72778,1.60762) rot=(0,0,1;1.5708rad)
  shape: bbox 1.961 x 0.7932 x 0.7145 mm, 63 faces, 5 solids (baked)
FEATURE [Part::Feature] Part__Feature279  label="RESC-0603 v005"
  Placement = pos=(4.83432,-3.67461,1.6) rot=(0,0,1;0rad)
  shape: bbox 1.7 x 0.9 x 0.55 mm, 52 faces, 3 solids (baked)
FEATURE [Part::Feature] Part__Feature280  label="RESC-0603 v006"
  Placement = pos=(-7.14949,3.61248,1.6) rot=(0,0,-1;1.5708rad)
  shape: bbox 0.9 x 1.7 x 0.55 mm, 52 faces, 3 solids (baked)
FEATURE [Part::Feature] Part__Feature281  label="Printed Circuit Board003"
  shape: bbox 25.4 x 17.78 x 1.6 mm, 42 faces (baked)
FEATURE [Part::Feature] Part__Feature282  label="EAHC2835WD008"
  shape: bbox 3.513 x 2.813 x 0.7485 mm, 108 faces, 4 solids (baked)
FEATURE [Part::Feature] Part__Feature283  label="AS7341 v004"
  Placement = pos=(0,-0.339822,1.6) rot=(0,0,1;0rad)
  shape: bbox 2 x 3.1 x 1.1 mm, 267 faces, 26 solids (baked)
FEATURE [Part::Feature] Part__Feature284  label="CAPC-0805-T0.95-BN v011"
  Placement = pos=(-5.01759,-3.15294,1.6) rot=(0,0,1;0rad)
  shape: bbox 2.1 x 1.35 x 0.95 mm, 42 faces (baked)
FEATURE [Part::Feature] Part__Feature285  label="YC164_RESPACK v006"
  Placement = pos=(2.99591,1.52916,1.6) rot=(0,0,1;0rad)
  shape: bbox 3.2 x 1.6 x 0.61 mm, 172 faces (baked)
FEATURE [Part::Feature] Part__Feature286  label="qwicc v007"
  Placement = pos=(-10.8364,0.0607456,1.65) rot=(0,0,-1;1.5708rad)
  shape: bbox 4.95 x 6 x 2.96 mm, 229 faces, 7 solids (baked)
FEATURE [Part::Feature] Part__Feature287  label="qwicc v008"
  Placement = pos=(10.8256,0.00556102,1.65) rot=(0,0,1;1.5708rad)
  shape: bbox 4.95 x 6 x 2.96 mm, 229 faces, 7 solids (baked)
FEATURE [App::Part] sot_23_6_v004  label="sot-23-6 v004"
  Group = -> [Part__Feature270,Part__Feature271,Part__Feature272,Part__Feature273,Part__Feature274,Part__Feature275,Part__Feature276]
  Origin = -> Origin015
  Placement = pos=(-4.47945,-0.603742,1.69152) rot=(0,0,1;0rad)
FEATURE [App::Part] Adafruit_AS7341_STEMMA_QT_v004  label="i2cHub"
  Group = -> [Part__Feature281,Part__Feature282,Part__Feature283,Part__Feature284,Part__Feature267,Part__Feature268,Part__Feature269,sot_23_6_v004,Part__Feature277,Part__Feature278,Part__Feature279,Part__Feature280,Part__Feature285,Part__Feature286,Part__Feature287]
  Origin = -> Origin016
  Placement = pos=(202.5,-10,41.83) rot=(-0.57735,0.57735,-0.57735;4.18879rad)
FEATURE [Part::Cylinder] Cylinder012  label="srsM4Cut001"
  Angle = 360
  AttacherType = Attacher::AttachEngine3D
  FirstAngle = 0
  Height = 15
  Placement = pos=(202.5,-14.8492,-74.8492) rot=(1,0,0;2.35619rad)
  Radius = 4
  SecondAngle = 0
FEATURE [Part::FeaturePython] Clone  label="m3x20sNT001"  # WARN: FeaturePython — macro-defined, semantics opaque (R4)
  AttacherType = Attacher::AttachEngine3D
  Fuse = false
  Placement = pos=(170,-8,73) rot=(0,-1,0;1.5708rad)
  Scale = (1.1,1.1,1.1)
FEATURE [Part::FeaturePython] Clone007  label="m3x20sNT002"  # WARN: FeaturePython — macro-defined, semantics opaque (R4)
  AttacherType = Attacher::AttachEngine3D
  Fuse = false
  Placement = pos=(235,-8,73) rot=(0.707107,0,0.707107;3.14159rad)
  Scale = (1.1,1.1,1.1)
FEATURE [Part::MultiFuse] Fusion119  label="srsCuts"
  Shapes = -> [Clone007,Clone]
FEATURE [Part::FeaturePython] Clone008  label="M3Nut019"  # WARN: FeaturePython — macro-defined, semantics opaque (R4)
  AttacherType = Attacher::AttachEngine3D
  Fuse = false
  Placement = pos=(175,-8,74) rot=(0.57735,0.57735,0.57735;2.0944rad)
  Scale = (1.09,1.09,1)
FEATURE [Part::FeaturePython] Clone009  label="M3Nut020"  # WARN: FeaturePython — macro-defined, semantics opaque (R4)
  AttacherType = Attacher::AttachEngine3D
  Fuse = false
  Placement = pos=(230,-8,74) rot=(0.57735,0.57735,0.57735;2.0944rad)
  Scale = (1.09,1.09,1)
FEATURE [Part::Compound] Compound002  label="m3NutsForSRS"
  Links = -> [Clone008,Clone009]
  Placement = pos=(0,0,-1) rot=(0,0,1;0rad)
FEATURE [Sketcher::SketchObject] Sketch095
  ArcFitTolerance = 0
  FullyConstrained = true
  MakeInternals = false
  Placement = pos=(170,0,0) rot=(0.57735,0.57735,0.57735;2.0944rad)
  sketch-geometry (4):
    g0: LineSegment StartX=-14 StartY=80.15 StartZ=0 EndX=-4 EndY=80.15 EndZ=0
    g1: LineSegment StartX=-4 StartY=80.15 StartZ=0 EndX=-4 EndY=76.95 EndZ=0
    g2: LineSegment StartX=-4 StartY=76.95 StartZ=0 EndX=-14 EndY=76.95 EndZ=0
    g3: LineSegment StartX=-14 StartY=76.95 StartZ=0 EndX=-14 EndY=80.15 EndZ=0
  constraints (12):
    c: Coincident(g0,g1)
    c: Coincident(g1,g2)
    c: Coincident(g2,g3)
    c: Coincident(g3,g0)
    c: Horizontal(g0)
    c: Horizontal(g2)
    c: Vertical(g1)
    c: Vertical(g3)
    c: DistanceY(g2) = 76.95
    c: DistanceY(g3,g3) = 3.2
    c: DistanceX(g2,g2) = 10
    c: DistanceX(g2) = -14
FEATURE [Part::Extrusion] Extrude031  label="srsCut002"
  Base = -> Sketch095
  Dir = (1,0,0)
  DirMode = 2
  FaceMakerClass = Part::FaceMakerBullseye
  FaceMakerMode = 3
  LengthFwd = 65
  LengthRev = 0
  Solid = true
  Symmetric = false
FEATURE [Part::Cylinder] Cylinder016
  Angle = 360
  AttacherType = Attacher::AttachEngine3D
  FirstAngle = 0
  Height = 8
  Radius = 2
  SecondAngle = 0
FEATURE [Part::Feature] Part__Feature293  label="m2Nuts"
  shape: bbox 4.619 x 4.619 x 1.601 mm, 22 faces (baked)
FEATURE [Part::FeaturePython] Clone010  label="m2Nuts001"  # Draft clone (typed FeaturePython)
  AttacherType = Attacher::AttachEngine3D
  Fuse = false
  Objects = -> [Part__Feature293]
  Placement = pos=(0,0,4) rot=(0,0,1;0rad)
  Scale = (1.05,1.05,5)
FEATURE [Part::Feature] Part__Feature294  label="m2Nuts003"
  shape: bbox 4.619 x 4.619 x 1.601 mm, 22 faces (baked)
FEATURE [Part::FeaturePython] Clone011  label="m2Nuts002"  # Draft clone (typed FeaturePython)
  AttacherType = Attacher::AttachEngine3D
  Fuse = false
  Objects = -> [Part__Feature294]
  Placement = pos=(0,0,0.8) rot=(0,0,1;0rad)
  Scale = (1.05,1.05,1)
FEATURE [Part::MultiFuse] Fusion003
  Shapes = -> [Clone011,Clone010]
FEATURE [Part::MultiFuse] Fusion004  label="m2Cuts"
  Placement = pos=(178.54,-14.55,61) rot=(0,1,0;3.14159rad)
  Shapes = -> [Cylinder016,Fusion003]
FEATURE [Part::Feature] Part__Feature296  label="M2x14s"
  Placement = pos=(178.54,-34.85,73.99) rot=(0.707107,0.707107,0;3.14159rad)
  shape: bbox 3.801 x 3.801 x 16.02 mm, 166 faces (baked)
FEATURE [Part::Feature] Part__Feature295  label="M2x10s"
  Placement = pos=(178.54,-34.85,1) rot=(0.707107,0.707107,0;3.14159rad)
  shape: bbox 3.801 x 3.801 x 12.02 mm, 126 faces (baked)
FEATURE [Part::Feature] Part__Feature297  label="M2x14s001"
  Placement = pos=(178.54,-14.55,73.99) rot=(0.707107,0.707107,0;3.14159rad)
  shape: bbox 3.801 x 3.801 x 16.02 mm, 166 faces (baked)
FEATURE [Part::Feature] Part__Feature298  label="M2x14s002"
  Placement = pos=(198.84,-14.55,73.99) rot=(0.707107,0.707107,0;3.14159rad)
  shape: bbox 3.801 x 3.801 x 16.02 mm, 166 faces (baked)
FEATURE [Part::Feature] Part__Feature299  label="M2x14s003"
  Placement = pos=(208.09,-14.55,73.99) rot=(0.707107,0.707107,0;3.14159rad)
  shape: bbox 3.801 x 3.801 x 16.02 mm, 166 faces (baked)
FEATURE [Part::Feature] Part__Feature300  label="M2x14s004"
  Placement = pos=(225.89,-34.85,73.99) rot=(0.707107,0.707107,0;3.14159rad)
  shape: bbox 3.801 x 3.801 x 16.02 mm, 166 faces (baked)
FEATURE [Part::Feature] Part__Feature301  label="M2x14s005"
  Placement = pos=(225.89,-14.55,73.99) rot=(0.707107,0.707107,0;3.14159rad)
  shape: bbox 3.801 x 3.801 x 16.02 mm, 166 faces (baked)
FEATURE [Part::MultiFuse] Fusion120  label="gpsM2x14s"
  Placement = pos=(0,0,-14.5) rot=(0,0,1;0rad)
  Shapes = -> [Part__Feature301,Part__Feature296,Part__Feature297,Part__Feature298,Part__Feature299,Part__Feature300]
FEATURE [Part::Feature] Part__Feature302  label="M3x20s002"
  Placement = pos=(180.93,-15.5,53.45) rot=(1,0,0;1.5708rad)
  shape: bbox 5.501 x 23.29 x 5.501 mm, 108 faces (baked)
FEATURE [Part::Feature] Part__Feature303  label="M3x20s003"
  Placement = pos=(224.07,-15.5,53.45) rot=(1,0,0;1.5708rad)
  shape: bbox 5.501 x 23.29 x 5.501 mm, 108 faces (baked)
FEATURE [Part::Feature] Part__Feature304  label="M3x20s004"
  Placement = pos=(202.51,-15.5,16.1) rot=(1,0,0;1.5708rad)
  shape: bbox 5.501 x 23.29 x 5.501 mm, 108 faces (baked)
FEATURE [Part::MultiFuse] Fusion136  label="Co2m3x20s"
  Shapes = -> [Part__Feature302,Part__Feature303,Part__Feature304]
FEATURE [Part::Feature] Part__Feature315  label="M2x14s006"
  Placement = pos=(178.65,-4.68,-43.85) rot=(0.57735,0.57735,0.57735;4.18879rad)
  shape: bbox 3.801 x 16.02 x 3.801 mm, 166 faces (baked)
FEATURE [Part::Feature] Part__Feature316  label="M2x10s001"
  Placement = pos=(190.85,-2.21,-49.51) rot=(-1,0,0;1.5708rad)
  shape: bbox 3.801 x 12.02 x 3.801 mm, 126 faces (baked)
FEATURE [Part::Feature] Part__Feature318  label="m2x30s"
  Placement = pos=(0,-15.16,-31.13) rot=(1,0,0;1.5708rad)
  shape: bbox 3.8 x 32.16 x 3.8 mm, 112 faces (baked)
FEATURE [Part::Feature] Part__Feature319  label="m2x25s"
  Placement = pos=(182.13,-17.67,-31.14) rot=(1,0,0;1.5708rad)
  shape: bbox 4.114 x 27.16 x 4.114 mm, 174 faces (baked)
FEATURE [Part::Feature] Part__Feature314  label="m3x20s002"
  Placement = pos=(223.15,-7e-15,5.42) rot=(0.57735,0.57735,0.57735;4.18879rad)
  shape: bbox 3.801 x 22.02 x 3.801 mm, 226 faces (baked)
FEATURE [Part::Feature] Part__Feature313  label="m3x20s001"
  Placement = pos=(182.14,-7e-15,-31.14) rot=(0.57735,0.57735,0.57735;4.18879rad)
  shape: bbox 3.801 x 22.02 x 3.801 mm, 226 faces (baked)
FEATURE [Part::MultiFuse] Fusion152  label="ipsM2s001"
  Placement = pos=(0,-9.16,0) rot=(0,0,1;0rad)
  Shapes = -> [Part__Feature314,Part__Feature313]
FEATURE [Part::Feature] Part__Feature320  label="m2x25s003"
  Placement = pos=(223.15,-17.67,5.46) rot=(0.57735,-0.57735,0.57735;2.0944rad)
  shape: bbox 4.114 x 27.16 x 4.114 mm, 174 faces (baked)
FEATURE [Part::MultiFuse] Fusion153  label="ipsM2s"
  Shapes = -> [Part__Feature320,Part__Feature319]
FEATURE [Part::FeaturePython] Clone048  label="m2Nuts036"  # WARN: FeaturePython — macro-defined, semantics opaque (R4)
  AttacherType = Attacher::AttachEngine3D
  Fuse = false
  Placement = pos=(0,0,4) rot=(0,0,1;0rad)
  Scale = (1.05,1.05,5)
FEATURE [Part::FeaturePython] Clone049  label="m2Nuts037"  # WARN: FeaturePython — macro-defined, semantics opaque (R4)
  AttacherType = Attacher::AttachEngine3D
  Fuse = false
  Placement = pos=(0,0,0.8) rot=(0,0,1;0rad)
  Scale = (1.05,1.05,1)
FEATURE [Part::Cylinder] Cylinder035
  Angle = 360
  AttacherType = Attacher::AttachEngine3D
  FirstAngle = 0
  Height = 8
  Radius = 2
  SecondAngle = 0
FEATURE [Part::MultiFuse] Fusion165
  Shapes = -> [Clone049,Clone048]
FEATURE [Part::MultiFuse] Fusion166  label="m2Cuts015"
  Placement = pos=(178.65,-6,-43.85) rot=(0.57735,0.57735,0.57735;4.18879rad)
  Shapes = -> [Cylinder035,Fusion165]
FEATURE [Part::FeaturePython] Clone050  label="m2Nuts038"  # WARN: FeaturePython — macro-defined, semantics opaque (R4)
  AttacherType = Attacher::AttachEngine3D
  Fuse = false
  Placement = pos=(0,0,4) rot=(0,0,1;0rad)
  Scale = (1.05,1.05,5)
FEATURE [Part::FeaturePython] Clone051  label="m2Nuts039"  # WARN: FeaturePython — macro-defined, semantics opaque (R4)
  AttacherType = Attacher::AttachEngine3D
  Fuse = false
  Placement = pos=(0,0,0.8) rot=(0,0,1;0rad)
  Scale = (1.05,1.05,1)
FEATURE [Part::Cylinder] Cylinder036
  Angle = 360
  AttacherType = Attacher::AttachEngine3D
  FirstAngle = 0
  Height = 8
  Radius = 2
  SecondAngle = 0
FEATURE [Part::MultiFuse] Fusion167
  Shapes = -> [Clone051,Clone050]
FEATURE [Part::MultiFuse] Fusion168  label="m2Cuts016"
  Placement = pos=(178.65,-6,-64.15) rot=(0.57735,0.57735,0.57735;4.18879rad)
  Shapes = -> [Cylinder036,Fusion167]
FEATURE [Part::FeaturePython] Clone052  label="m2Nuts040"  # WARN: FeaturePython — macro-defined, semantics opaque (R4)
  AttacherType = Attacher::AttachEngine3D
  Fuse = false
  Placement = pos=(0,0,4) rot=(0,0,1;0rad)
  Scale = (1.05,1.05,5)
FEATURE [Part::FeaturePython] Clone053  label="m2Nuts041"  # WARN: FeaturePython — macro-defined, semantics opaque (R4)
  AttacherType = Attacher::AttachEngine3D
  Fuse = false
  Placement = pos=(0,0,0.8) rot=(0,0,1;0rad)
  Scale = (1.05,1.05,1)
FEATURE [Part::Cylinder] Cylinder037
  Angle = 360
  AttacherType = Attacher::AttachEngine3D
  FirstAngle = 0
  Height = 8
  Radius = 2
  SecondAngle = 0
FEATURE [Part::MultiFuse] Fusion169
  Shapes = -> [Clone053,Clone052]
FEATURE [Part::MultiFuse] Fusion170  label="m2Cuts017"
  Placement = pos=(191.35,-6,-64.15) rot=(0.57735,0.57735,0.57735;4.18879rad)
  Shapes = -> [Cylinder037,Fusion169]
FEATURE [Part::FeaturePython] Clone054  label="m2Nuts042"  # WARN: FeaturePython — macro-defined, semantics opaque (R4)
  AttacherType = Attacher::AttachEngine3D
  Fuse = false
  Placement = pos=(0,0,4) rot=(0,0,1;0rad)
  Scale = (1.05,1.05,5)
FEATURE [Part::FeaturePython] Clone055  label="m2Nuts043"  # WARN: FeaturePython — macro-defined, semantics opaque (R4)
  AttacherType = Attacher::AttachEngine3D
  Fuse = false
  Placement = pos=(0,0,0.8) rot=(0,0,1;0rad)
  Scale = (1.05,1.05,1)
FEATURE [Part::Cylinder] Cylinder038
  Angle = 360
  AttacherType = Attacher::AttachEngine3D
  FirstAngle = 0
  Height = 8
  Radius = 2
  SecondAngle = 0
FEATURE [Part::MultiFuse] Fusion171
  Shapes = -> [Clone055,Clone054]
FEATURE [Part::MultiFuse] Fusion172  label="m2Cuts018"
  Placement = pos=(213.65,-6,-64.15) rot=(0.57735,0.57735,0.57735;4.18879rad)
  Shapes = -> [Cylinder038,Fusion171]
FEATURE [Part::FeaturePython] Clone056  label="m2Nuts044"  # WARN: FeaturePython — macro-defined, semantics opaque (R4)
  AttacherType = Attacher::AttachEngine3D
  Fuse = false
  Placement = pos=(0,0,4) rot=(0,0,1;0rad)
  Scale = (1.05,1.05,5)
FEATURE [Part::FeaturePython] Clone057  label="m2Nuts045"  # WARN: FeaturePython — macro-defined, semantics opaque (R4)
  AttacherType = Attacher::AttachEngine3D
  Fuse = false
  Placement = pos=(0,0,0.8) rot=(0,0,1;0rad)
  Scale = (1.05,1.05,1)
FEATURE [Part::Cylinder] Cylinder039
  Angle = 360
  AttacherType = Attacher::AttachEngine3D
  FirstAngle = 0
  Height = 8
  Radius = 2
  SecondAngle = 0
FEATURE [Part::MultiFuse] Fusion173
  Shapes = -> [Clone057,Clone056]
FEATURE [Part::MultiFuse] Fusion174  label="m2Cuts019"
  Placement = pos=(226.35,-6,-64.15) rot=(0.57735,0.57735,0.57735;4.18879rad)
  Shapes = -> [Cylinder039,Fusion173]
FEATURE [Part::FeaturePython] Clone058  label="m2Nuts046"  # WARN: FeaturePython — macro-defined, semantics opaque (R4)
  AttacherType = Attacher::AttachEngine3D
  Fuse = false
  Placement = pos=(0,0,4) rot=(0,0,1;0rad)
  Scale = (1.05,1.05,5)
FEATURE [Part::FeaturePython] Clone059  label="m2Nuts047"  # WARN: FeaturePython — macro-defined, semantics opaque (R4)
  AttacherType = Attacher::AttachEngine3D
  Fuse = false
  Placement = pos=(0,0,0.8) rot=(0,0,1;0rad)
  Scale = (1.05,1.05,1)
FEATURE [Part::Cylinder] Cylinder040
  Angle = 360
  AttacherType = Attacher::AttachEngine3D
  FirstAngle = 0
  Height = 8
  Radius = 2
  SecondAngle = 0
FEATURE [Part::MultiFuse] Fusion175
  Shapes = -> [Clone059,Clone058]
FEATURE [Part::MultiFuse] Fusion176  label="m2Cuts020"
  Placement = pos=(226.35,-6,-43.85) rot=(0.57735,0.57735,0.57735;4.18879rad)
  Shapes = -> [Cylinder040,Fusion175]
FEATURE [Part::Cylinder] Cylinder041
  Angle = 360
  AttacherType = Attacher::AttachEngine3D
  FirstAngle = 0
  Height = 10
  Placement = pos=(160,-8,73) rot=(0,-1,0;1.5708rad)
  Radius = 2
  SecondAngle = 0
FEATURE [Part::Cylinder] Cylinder042
  Angle = 360
  AttacherType = Attacher::AttachEngine3D
  FirstAngle = 0
  Height = 10
  Placement = pos=(255,-8,73) rot=(0,-1,0;1.5708rad)
  Radius = 2
  SecondAngle = 0
FEATURE [Part::MultiFuse] Fusion178  label="m3Cut001"
  Shapes = -> [Cylinder042,Cylinder041]
FEATURE [Sketcher::SketchObject] Sketch097
  ArcFitTolerance = 0
  FullyConstrained = true
  MakeInternals = false
  Placement = pos=(0,0,0) rot=(1,0,0;1.5708rad)
  sketch-geometry (4):
    g0: LineSegment StartX=70 StartY=80 StartZ=0 EndX=247.5 EndY=80 EndZ=0
    g1: LineSegment StartX=247.5 StartY=80 StartZ=0 EndX=247.5 EndY=-80 EndZ=0
    g2: LineSegment StartX=247.5 StartY=-80 StartZ=0 EndX=70 EndY=-80 EndZ=0
    g3: LineSegment StartX=70 StartY=-80 StartZ=0 EndX=70 EndY=80 EndZ=0
  constraints (12):
    c: Coincident(g0,g1)
    c: Coincident(g1,g2)
    c: Coincident(g2,g3)
    c: Coincident(g3,g0)
    c: Horizontal(g0)
    c: Horizontal(g2)
    c: Vertical(g1)
    c: Vertical(g3)
    c: DistanceY(g2) = -80
    c: DistanceY(g0) = 80
    c: DistanceX(g2) = 70
    c: DistanceX(g2,g2) = 177.5
FEATURE [Part::Extrusion] Extrude032  label="baseCutLarge"
  Base = -> Sketch097
  Dir = (0,-1,2e-16)
  DirMode = 2
  FaceMakerClass = Part::FaceMakerBullseye
  FaceMakerMode = 3
  LengthFwd = 10
  LengthRev = 0
  Placement = pos=(0,10,0) rot=(0,0,1;0rad)
  Solid = true
  Symmetric = false
FEATURE [Part::MultiFuse] Fusion184  label="srsM4Cuts"
  Shapes = -> [Cylinder012,Cylinder002]
FEATURE [Sketcher::SketchObject] Sketch098  label="outerSRS019"
  ArcFitTolerance = 0
  FullyConstrained = true
  MakeInternals = false
  Placement = pos=(0,0,-80) rot=(0,0,1;0rad)
  sketch-geometry (6):
    g0: LineSegment StartX=157.5 StartY=0 StartZ=0 EndX=157.5 EndY=-32 EndZ=0
    g1: LineSegment StartX=180.5 StartY=-55 StartZ=0 EndX=224.5 EndY=-55 EndZ=0
    g2: LineSegment StartX=247.5 StartY=0 StartZ=0 EndX=247.5 EndY=-32 EndZ=0
    g3: ArcOfCircle CenterX=180.5 CenterY=-32 CenterZ=0 NormalX=0 NormalY=0 NormalZ=1 AngleXU=0 Radius=23 StartAngle=3.14159 EndAngle=4.71239
    g4: ArcOfCircle CenterX=224.5 CenterY=-32 CenterZ=0 NormalX=0 NormalY=0 NormalZ=1 AngleXU=0 Radius=23 StartAngle=4.71239 EndAngle=6.28319
    g5: LineSegment StartX=157.5 StartY=0 StartZ=0 EndX=247.5 EndY=0 EndZ=0
  constraints (20):
    c: PointOnObject(g5,g-1)
    c: Vertical(g0)
    c: Horizontal(g1)
    c: Vertical(g2)
    c: DistanceY(g2,g5) = 0
    c: Coincident(g0,g3)
    c: Coincident(g1,g3)
    c: Coincident(g1,g4)
    c: Coincident(g2,g4)
    c: Angle(g3) = 1.5708
    c: Angle(g4) = 1.5708
    c: Coincident(g5,g2)
    c: DistanceX(g0) = 157.5
    c: Coincident(g5,g0)
    c: DistanceX(g0,g2) = 90
    c: DistanceY(g0,g0) = 32
    c: DistanceY(g2,g0) = 0
    c: DistanceY(g3,g0) = 0
    c: DistanceY(g4,g2) = 0
    c: DistanceX(g0,g3) = 23
FEATURE [Part::Extrusion] Extrude033  label="srsCut"
  Base = -> Sketch098
  Dir = (0,0,1)
  DirMode = 2
  FaceMakerClass = Part::FaceMakerBullseye
  FaceMakerMode = 3
  LengthFwd = 20
  LengthRev = 0
  Reversed = true
  Solid = true
  Symmetric = false
FEATURE [Part::MultiFuse] Fusion186  label="srsCut001"
  Shapes = -> [Extrude033,Fusion184]
FEATURE [Part::Box] Box002  label="batteryPlus12MAH"
  AttacherType = Attacher::AttachEngine3D
  Height = 9
  Length = 68
  Placement = pos=(168.5,9,-70) rot=(1,0,0;1.5708rad)
  Width = 140
FEATURE [Part::Feature] Part__Feature326  label="Male USB C"
  Placement = pos=(-6.66,6.07,3.21) rot=(0.57735,0.57735,-0.57735;4.18879rad)
  shape: bbox 14.42 x 11 x 2.669 mm, 1445 faces, 110 solids (baked)
FEATURE [Part::Feature] Part__Feature327  label="USB C cord"
  shape: bbox 154.9 x 26.96 x 8.644 mm, 201 faces (baked)
FEATURE [Part::Feature] Part__Feature328  label="Female USB C"
  Placement = pos=(150.02,6.085,3.21) rot=(0.707107,0.707107,0;3.14159rad)
  shape: bbox 7.914 x 8.954 x 3.224 mm, 340 faces, 24 solids (baked)
FEATURE [App::Part] USB_C_cable_v4  label="USB C cable v4"
  Group = -> [Part__Feature326,Part__Feature327,Part__Feature328]
  Origin = -> Origin018
  Placement = pos=(122.92,-2.35,-75.5) rot=(0.57735,0.57735,-0.57735;2.0944rad)
FEATURE [Sketcher::SketchObject] Sketch215
  ArcFitTolerance = 0
  FullyConstrained = true
  MakeInternals = false
  Placement = pos=(0,0,0) rot=(1,0,0;1.5708rad)
  sketch-geometry (10):
    g0: LineSegment StartX=132 StartY=-27 StartZ=0 EndX=81 EndY=-27 EndZ=0
    g1: LineSegment StartX=81 StartY=-27 StartZ=0 EndX=81 EndY=45 EndZ=0
    g2: LineSegment StartX=81 StartY=45 StartZ=0 EndX=141 EndY=45 EndZ=0
    g3: LineSegment StartX=141 StartY=45 StartZ=0 EndX=141 EndY=-25 EndZ=0
    g4: LineSegment StartX=141 StartY=-25 StartZ=0 EndX=145 EndY=-25 EndZ=0
    g5: LineSegment StartX=145 StartY=-25 StartZ=0 EndX=145 EndY=49 EndZ=0
    g6: LineSegment StartX=145 StartY=49 StartZ=0 EndX=77 EndY=49 EndZ=0
    g7: LineSegment StartX=77 StartY=49 StartZ=0 EndX=77 EndY=-31 EndZ=0
    g8: LineSegment StartX=77 StartY=-31 StartZ=0 EndX=132 EndY=-31 EndZ=0
    g9: LineSegment StartX=132 StartY=-31 StartZ=0 EndX=132 EndY=-27 EndZ=0
  constraints (30):
    c: Horizontal(g0)
    c: Coincident(g1,g0)
    c: Vertical(g1)
    c: Horizontal(g2)
    c: Coincident(g3,g2)
    c: Vertical(g3)
    c: Coincident(g4,g3)
    c: Horizontal(g4)
    c: Coincident(g5,g4)
    c: Vertical(g5)
    c: Coincident(g6,g5)
    c: Horizontal(g6)
    c: Vertical(g7)
    c: Horizontal(g8)
    c: Coincident(g9,g8)
    c: Coincident(g9,g0)
    c: Vertical(g9)
    c: Coincident(g6,g7)
    c: Coincident(g1,g2)
    c: Coincident(g7,g8)
    c: DistanceX(g7) = 77
    c: DistanceX(g7,g0) = 4
    c: DistanceX(g4,g4) = 4
    c: DistanceY(g7,g0) = 4
    c: DistanceY(g0) = -27
    c: DistanceX(g3) = 141
    c: DistanceY(g1) = 45
    c: DistanceY(g1,g6) = 4
    c: DistanceY(g3) = -25
    c: DistanceX(g0) = 132
FEATURE [Sketcher::SketchObject] Sketch221
  ArcFitTolerance = 0
  FullyConstrained = true
  MakeInternals = false
  Placement = pos=(0,0,0) rot=(1,0,0;1.5708rad)
  sketch-geometry (4):
    g0: ArcOfCircle CenterX=85 CenterY=60.35 CenterZ=0 NormalX=0 NormalY=0 NormalZ=1 AngleXU=0 Radius=4.875 StartAngle=1.5708 EndAngle=4.71239
    g1: ArcOfCircle CenterX=92.25 CenterY=60.35 CenterZ=0 NormalX=0 NormalY=0 NormalZ=1 AngleXU=0 Radius=4.875 StartAngle=4.71239 EndAngle=7.85398
    g2: LineSegment StartX=85 StartY=55.475 StartZ=0 EndX=92.25 EndY=55.475 EndZ=0
    g3: LineSegment StartX=92.25 StartY=65.225 StartZ=0 EndX=85 EndY=65.225 EndZ=0
  constraints (10):
    c: Tangent(g0,g2) = -1.5708
    c: Tangent(g2,g1) = -1.5708
    c: Tangent(g1,g3) = -1.5708
    c: Tangent(g3,g0) = -1.5708
    c: Equal(g0,g1)
    c: Horizontal(g0,g1)
    c: DistanceX(g0) = 85
    c: DistanceX(g0,g1) = 7.25
    c: DistanceY(g0) = 60.35
    c: Diameter(g0) = 9.75
FEATURE [Part::Feature] Part__Feature334  label="CAPC-0805-T0.95-BN v012"
  Placement = pos=(-5.48627,2.66154,1.6) rot=(0,0,-1;1.5708rad)
  shape: bbox 1.35 x 2.1 x 0.95 mm, 42 faces (baked)
FEATURE [Part::Feature] Part__Feature335  label="CAPC-0805-T0.95-BN v013"
  Placement = pos=(-3.43627,2.66154,1.6) rot=(0,0,-1;1.5708rad)
  shape: bbox 1.35 x 2.1 x 0.95 mm, 42 faces (baked)
FEATURE [Part::Feature] Part__Feature336  label="CAPC-0603-T0.9-BN v009"
  Placement = pos=(-1.69987,-3.28475,1.6) rot=(0,0,1;0rad)
  shape: bbox 1.7 x 0.9 x 0.9 mm, 42 faces (baked)
FEATURE [Part::Feature] Part__Feature337  label="BODY_MF06A003"
  Placement = pos=(0,0,0.762) rot=(0.57735,-0.57735,-0.57735;2.0944rad)
  shape: bbox 1.601 x 2.921 x 1.016 mm, 42 faces (baked)
FEATURE [Part::Feature] Part__Feature338  label="LEAD_MF06A018"
  Placement = pos=(-0.9652,-0.9525,0.1016) rot=(0.57735,-0.57735,-0.57735;2.0944rad)
  shape: bbox 0.6223 x 0.3749 x 0.8636 mm, 14 faces (baked)
FEATURE [Part::Feature] Part__Feature339  label="LEAD_MF06A019"
  Placement = pos=(-0.9652,0,0.1016) rot=(0.57735,-0.57735,-0.57735;2.0944rad)
  shape: bbox 0.6223 x 0.3749 x 0.8636 mm, 14 faces (baked)
FEATURE [Part::Feature] Part__Feature340  label="LEAD_MF06A020"
  Placement = pos=(-0.9652,0.9525,0.1016) rot=(0.57735,-0.57735,-0.57735;2.0944rad)
  shape: bbox 0.6223 x 0.3749 x 0.8636 mm, 14 faces (baked)
FEATURE [Part::Feature] Part__Feature341  label="LEAD_MF06A021"
  Placement = pos=(0.9652,-0.9525,0.1016) rot=(0.57735,0.57735,0.57735;2.0944rad)
  shape: bbox 0.6223 x 0.3749 x 0.8636 mm, 14 faces (baked)
FEATURE [Part::Feature] Part__Feature342  label="LEAD_MF06A022"
  Placement = pos=(0.9652,0,0.1016) rot=(0.57735,0.57735,0.57735;2.0944rad)
  shape: bbox 0.6223 x 0.3749 x 0.8636 mm, 14 faces (baked)
FEATURE [Part::Feature] Part__Feature343  label="LEAD_MF06A023"
  Placement = pos=(0.9652,0.9525,0.1016) rot=(0.57735,0.57735,0.57735;2.0944rad)
  shape: bbox 0.6223 x 0.3749 x 0.8636 mm, 14 faces (baked)
FEATURE [Part::Feature] Part__Feature344  label="SOT363 v005"
  Placement = pos=(4.97054,-0.645171,1.675) rot=(0,0,1;3.14159rad)
  shape: bbox 2.1 x 2 x 1.1 mm, 94 faces, 7 solids (baked)
FEATURE [Part::Feature] Part__Feature345  label="LED 0603 single color v005"
  Placement = pos=(-9.18406,3.72778,1.60762) rot=(0,0,1;1.5708rad)
  shape: bbox 1.961 x 0.7932 x 0.7145 mm, 63 faces, 5 solids (baked)
FEATURE [Part::Feature] Part__Feature346  label="RESC-0603 v007"
  Placement = pos=(4.83432,-3.67461,1.6) rot=(0,0,1;0rad)
  shape: bbox 1.7 x 0.9 x 0.55 mm, 52 faces, 3 solids (baked)
FEATURE [Part::Feature] Part__Feature347  label="RESC-0603 v008"
  Placement = pos=(-7.14949,3.61248,1.6) rot=(0,0,-1;1.5708rad)
  shape: bbox 0.9 x 1.7 x 0.55 mm, 52 faces, 3 solids (baked)
FEATURE [Part::Feature] Part__Feature348  label="Printed Circuit Board004"
  shape: bbox 25.4 x 17.78 x 1.6 mm, 42 faces (baked)
FEATURE [Part::Feature] Part__Feature349  label="EAHC2835WD009"
  shape: bbox 3.513 x 2.813 x 0.7485 mm, 108 faces, 4 solids (baked)
FEATURE [Part::Feature] Part__Feature350  label="AS7341 v005"
  Placement = pos=(0,-0.339822,1.6) rot=(0,0,1;0rad)
  shape: bbox 2 x 3.1 x 1.1 mm, 267 faces, 26 solids (baked)
FEATURE [Part::Feature] Part__Feature351  label="CAPC-0805-T0.95-BN v014"
  Placement = pos=(-5.01759,-3.15294,1.6) rot=(0,0,1;0rad)
  shape: bbox 2.1 x 1.35 x 0.95 mm, 42 faces (baked)
FEATURE [Part::Feature] Part__Feature352  label="YC164_RESPACK v007"
  Placement = pos=(2.99591,1.52916,1.6) rot=(0,0,1;0rad)
  shape: bbox 3.2 x 1.6 x 0.61 mm, 172 faces (baked)
FEATURE [Part::Feature] Part__Feature353  label="qwicc v009"
  Placement = pos=(-10.8364,0.0607456,1.65) rot=(0,0,-1;1.5708rad)
  shape: bbox 4.95 x 6 x 2.96 mm, 229 faces, 7 solids (baked)
FEATURE [Part::Feature] Part__Feature354  label="qwicc v010"
  Placement = pos=(10.8256,0.00556102,1.65) rot=(0,0,1;1.5708rad)
  shape: bbox 4.95 x 6 x 2.96 mm, 229 faces, 7 solids (baked)
FEATURE [App::Part] sot_23_6_v005  label="sot-23-6 v005"
  Group = -> [Part__Feature337,Part__Feature338,Part__Feature339,Part__Feature340,Part__Feature341,Part__Feature342,Part__Feature343]
  Origin = -> Origin019
  Placement = pos=(-4.47945,-0.603742,1.69152) rot=(0,0,1;0rad)
FEATURE [App::Part] Adafruit_AS7341_STEMMA_QT_v005  label="bme280"
  Group = -> [Part__Feature348,Part__Feature349,Part__Feature350,Part__Feature351,Part__Feature334,Part__Feature335,Part__Feature336,sot_23_6_v005,Part__Feature344,Part__Feature345,Part__Feature346,Part__Feature347,Part__Feature352,Part__Feature353,Part__Feature354]
  Origin = -> Origin020
  Placement = pos=(180,-10,30) rot=(0.57735,0.57735,-0.57735;2.0944rad)
FEATURE [Sketcher::SketchObject] Sketch
  ArcFitTolerance = 0
  FullyConstrained = true
  MakeInternals = false
  Placement = pos=(0,0,0) rot=(1,0,0;1.5708rad)
  sketch-geometry (8):
    g0: LineSegment StartX=158.5 StartY=80 StartZ=0 EndX=246.5 EndY=80 EndZ=0
    g1: LineSegment StartX=246.5 StartY=80 StartZ=0 EndX=246.5 EndY=-80 EndZ=0
    g2: LineSegment StartX=246.5 StartY=-80 StartZ=0 EndX=158.5 EndY=-80 EndZ=0
    g3: LineSegment StartX=158.5 StartY=-80 StartZ=0 EndX=158.5 EndY=80 EndZ=0
    g4: LineSegment StartX=167.5 StartY=71 StartZ=0 EndX=237.5 EndY=71 EndZ=0
    g5: LineSegment StartX=237.5 StartY=71 StartZ=0 EndX=237.5 EndY=-72 EndZ=0
    g6: LineSegment StartX=237.5 StartY=-72 StartZ=0 EndX=167.5 EndY=-72 EndZ=0
    g7: LineSegment StartX=167.5 StartY=-72 StartZ=0 EndX=167.5 EndY=71 EndZ=0
  constraints (24):
    c: Coincident(g0,g1)
    c: Coincident(g1,g2)
    c: Coincident(g2,g3)
    c: Coincident(g3,g0)
    c: Horizontal(g0)
    c: Horizontal(g2)
    c: Vertical(g1)
    c: Vertical(g3)
    c: DistanceX(g2) = 158.5
    c: DistanceY(g2) = -80
    c: DistanceY(g2,g0) = 160
    c: Coincident(g4,g5)
    c: Coincident(g5,g6)
    c: Coincident(g6,g7)
    c: Coincident(g7,g4)
    c: Horizontal(g4)
    c: Horizontal(g6)
    c: Vertical(g5)
    c: Vertical(g7)
    c: DistanceX(g0,g4) = 9
    c: DistanceY(g4,g0) = 9
    c: DistanceY(g2,g6) = 8
    c: DistanceX(g5,g1) = 9
    c: DistanceX(g1) = 246.5
FEATURE [Part::Extrusion] Extrude231
  Base = -> Sketch
  Dir = (0,-1,2e-16)
  DirMode = 2
  FaceMakerClass = Part::FaceMakerBullseye
  FaceMakerMode = 3
  LengthFwd = 10
  LengthRev = 0
  Reversed = true
  Solid = true
  Symmetric = false
FEATURE [Sketcher::SketchObject] Sketch233
  ArcFitTolerance = 0
  FullyConstrained = true
  MakeInternals = false
  Placement = pos=(0,13,0) rot=(1,0,0;1.5708rad)
  sketch-geometry (8):
    g0: LineSegment StartX=67.5 StartY=80 StartZ=0 EndX=246.5 EndY=80 EndZ=0
    g1: LineSegment StartX=246.5 StartY=80 StartZ=0 EndX=246.5 EndY=-80 EndZ=0
    g2: LineSegment StartX=246.5 StartY=-80 StartZ=0 EndX=67.5 EndY=-80 EndZ=0
    g3: LineSegment StartX=67.5 StartY=-80 StartZ=0 EndX=67.5 EndY=80 EndZ=0
    g4: ArcOfCircle CenterX=85.4 CenterY=60.35 CenterZ=0 NormalX=0 NormalY=0 NormalZ=1 AngleXU=0 Radius=4.75 StartAngle=1.5708 EndAngle=4.71239
    g5: ArcOfCircle CenterX=91.9 CenterY=60.35 CenterZ=0 NormalX=0 NormalY=0 NormalZ=1 AngleXU=0 Radius=4.75 StartAngle=4.71239 EndAngle=7.85398
    g6: LineSegment StartX=85.4 StartY=55.6 StartZ=0 EndX=91.9 EndY=55.6 EndZ=0
    g7: LineSegment StartX=91.9 StartY=65.1 StartZ=0 EndX=85.4 EndY=65.1 EndZ=0
  constraints (22):
    c: Coincident(g0,g1)
    c: Coincident(g1,g2)
    c: Coincident(g2,g3)
    c: Coincident(g3,g0)
    c: Horizontal(g0)
    c: Horizontal(g2)
    c: Vertical(g1)
    c: Vertical(g3)
    c: DistanceX(g2,g2) = 179
    c: DistanceY(g3,g3) = 160
    c: DistanceY(g2) = -80
    c: DistanceX(g0) = 67.5
    c: Tangent(g4,g6) = -1.5708
    c: Tangent(g6,g5) = -1.5708
    c: Tangent(g5,g7) = -1.5708
    c: Tangent(g7,g4) = -1.5708
    c: Equal(g4,g5)
    c: Horizontal(g6)
    c: DistanceX(g4) = 85.4
    c: DistanceY(g4) = 60.35
    c: Diameter(g4) = 9.5
    c: DistanceX(g4,g5) = 6.5
FEATURE [Part::Extrusion] Extrude232
  Base = -> Sketch233
  Dir = (0,-1,2e-16)
  DirMode = 2
  FaceMakerClass = Part::FaceMakerBullseye
  FaceMakerMode = 3
  LengthFwd = 3
  LengthRev = 0
  Solid = true
  Symmetric = false
FEATURE [Sketcher::SketchObject] Sketch234
  ArcFitTolerance = 0
  FullyConstrained = true
  MakeInternals = false
  Placement = pos=(0,13,0) rot=(1,0,0;1.5708rad)
  sketch-geometry (4):
    g0: ArcOfCircle CenterX=85.4 CenterY=-60.4 CenterZ=0 NormalX=0 NormalY=0 NormalZ=1 AngleXU=0 Radius=4.25 StartAngle=1.5708 EndAngle=4.71239
    g1: ArcOfCircle CenterX=91.9 CenterY=-60.4 CenterZ=0 NormalX=0 NormalY=0 NormalZ=1 AngleXU=0 Radius=4.25 StartAngle=4.71239 EndAngle=7.85398
    g2: LineSegment StartX=85.4 StartY=-64.65 StartZ=0 EndX=91.9 EndY=-64.65 EndZ=0
    g3: LineSegment StartX=91.9 StartY=-56.15 StartZ=0 EndX=85.4 EndY=-56.15 EndZ=0
  constraints (10):
    c: Tangent(g0,g2) = -1.5708
    c: Tangent(g2,g1) = -1.5708
    c: Tangent(g1,g3) = -1.5708
    c: Tangent(g3,g0) = -1.5708
    c: Equal(g0,g1)
    c: Horizontal(g2)
    c: Diameter(g0) = 8.5
    c: DistanceX(g0) = 85.4
    c: DistanceY(g0) = -60.4
    c: DistanceX(g3,g3) = 6.5
FEATURE [Part::Extrusion] Extrude233
  Base = -> Sketch234
  Dir = (0,-1,2e-16)
  DirMode = 2
  FaceMakerClass = Part::FaceMakerBullseye
  FaceMakerMode = 3
  LengthFwd = 10
  LengthRev = 0
  Solid = true
  Symmetric = false
FEATURE [Part::MultiFuse] Fusion224  label="batteryHousing"
  Shapes = -> [Extrude232,Extrude233,Extrude231]
FEATURE [Sketcher::SketchObject] Sketch235  label="outerSRS020"
  ArcFitTolerance = 0
  FullyConstrained = true
  MakeInternals = false
  Placement = pos=(0,0,-80) rot=(0,0,1;0rad)
  sketch-geometry (6):
    g0: LineSegment StartX=157.5 StartY=0 StartZ=0 EndX=157.5 EndY=-32 EndZ=0
    g1: LineSegment StartX=180.5 StartY=-55 StartZ=0 EndX=224.5 EndY=-55 EndZ=0
    g2: LineSegment StartX=247.5 StartY=0 StartZ=0 EndX=247.5 EndY=-32 EndZ=0
    g3: ArcOfCircle CenterX=180.5 CenterY=-32 CenterZ=0 NormalX=0 NormalY=0 NormalZ=1 AngleXU=0 Radius=23 StartAngle=3.14159 EndAngle=4.71239
    g4: ArcOfCircle CenterX=224.5 CenterY=-32 CenterZ=0 NormalX=0 NormalY=0 NormalZ=1 AngleXU=0 Radius=23 StartAngle=4.71239 EndAngle=6.28319
    g5: LineSegment StartX=157.5 StartY=0 StartZ=0 EndX=247.5 EndY=0 EndZ=0
  constraints (20):
    c: PointOnObject(g5,g-1)
    c: Vertical(g0)
    c: Horizontal(g1)
    c: Vertical(g2)
    c: DistanceY(g2,g5) = 0
    c: Coincident(g0,g3)
    c: Coincident(g1,g3)
    c: Coincident(g1,g4)
    c: Coincident(g2,g4)
    c: Angle(g3) = 1.5708
    c: Angle(g4) = 1.5708
    c: Coincident(g5,g2)
    c: DistanceX(g0) = 157.5
    c: Coincident(g5,g0)
    c: DistanceX(g0,g2) = 90
    c: DistanceY(g0,g0) = 32
    c: DistanceY(g2,g0) = 0
    c: DistanceY(g3,g0) = 0
    c: DistanceY(g4,g2) = 0
    c: DistanceX(g0,g3) = 23
FEATURE [Part::Extrusion] Extrude234
  Base = -> Sketch235
  Dir = (0,0,1)
  DirMode = 2
  FaceMakerClass = Part::FaceMakerBullseye
  FaceMakerMode = 3
  LengthFwd = 3
  LengthRev = 0
  Solid = true
  Symmetric = false
FEATURE [Part::Fillet] Fillet055  label="srsBottom001"
  Base = -> Extrude234
  EdgeLinks = -> Extrude234 [Edge3,Edge4,Edge6,Edge7,Edge9,Edge10,Edge12,Edge13,Edge15,Edge16,Edge17,Edge18]
  Edges = 12 edges r=1: [Edge3,Edge4,Edge6,Edge7,Edge9,Edge10,Edge12,Edge13,Edge15,Edge16,Edge17,Edge18]
  Placement = pos=(0,0,37) rot=(0,0,1;0rad)
FEATURE [Part::MultiFuse] Fusion  label="srs"
  Shapes = -> [Fillet020,Fillet,Fillet007,Fillet008,Fillet010,Fillet009,Fillet011,Fillet012,Fillet013,Fillet014,Fillet015,Fillet016,Fillet017,Fillet018]
FEATURE [Sketcher::SketchObject] Sketch238  label="outerSRS021"
  ArcFitTolerance = 0
  FullyConstrained = true
  MakeInternals = false
  Placement = pos=(0,0,-80) rot=(0,0,1;0rad)
  sketch-geometry (6):
    g0: LineSegment StartX=158.5 StartY=0 StartZ=0 EndX=158.5 EndY=-32 EndZ=0
    g1: LineSegment StartX=180.5 StartY=-54 StartZ=0 EndX=224.5 EndY=-54 EndZ=0
    g2: LineSegment StartX=246.5 StartY=0 StartZ=0 EndX=246.5 EndY=-32 EndZ=0
    g3: ArcOfCircle CenterX=180.5 CenterY=-32 CenterZ=0 NormalX=0 NormalY=0 NormalZ=1 AngleXU=0 Radius=22 StartAngle=3.14159 EndAngle=4.71239
    g4: ArcOfCircle CenterX=224.5 CenterY=-32 CenterZ=0 NormalX=0 NormalY=0 NormalZ=1 AngleXU=0 Radius=22 StartAngle=4.71239 EndAngle=6.28319
    g5: LineSegment StartX=158.5 StartY=0 StartZ=0 EndX=246.5 EndY=0 EndZ=0
  constraints (20):
    c: PointOnObject(g5,g-1)
    c: Vertical(g0)
    c: Horizontal(g1)
    c: Vertical(g2)
    c: DistanceY(g2,g5) = 0
    c: Coincident(g0,g3)
    c: Coincident(g1,g3)
    c: Coincident(g1,g4)
    c: Coincident(g2,g4)
    c: Angle(g3) = 1.5708
    c: Angle(g4) = 1.5708
    c: Coincident(g5,g2)
    c: DistanceX(g0) = 158.5
    c: Coincident(g5,g0)
    c: DistanceX(g0,g2) = 88
    c: DistanceY(g0,g0) = 32
    c: DistanceY(g2,g0) = 0
    c: DistanceY(g3,g0) = 0
    c: DistanceY(g4,g2) = 0
    c: DistanceX(g0,g3) = 22
FEATURE [Part::Extrusion] Extrude237
  Base = -> Sketch238
  Dir = (0,0,1)
  DirMode = 2
  FaceMakerClass = Part::FaceMakerBullseye
  FaceMakerMode = 3
  LengthFwd = 4
  LengthRev = 0
  Solid = true
  Symmetric = false
FEATURE [Part::Fillet] Fillet056  label="piCoverBottom"
  Base = -> Extrude237
  EdgeLinks = -> Extrude237 [Edge3,Edge4,Edge6,Edge7,Edge9,Edge10,Edge12,Edge13,Edge15,Edge16,Edge17,Edge18]
  Edges = 12 edges r=1: [Edge3,Edge4,Edge6,Edge7,Edge9,Edge10,Edge12,Edge13,Edge15,Edge16,Edge17,Edge18]
FEATURE [Sketcher::SketchObject] Sketch239  label="innerSRS017"
  ArcFitTolerance = 0
  FullyConstrained = true
  MakeInternals = false
  Placement = pos=(0,0,-65) rot=(0,0,1;0rad)
  sketch-geometry (12):
    g0: ArcOfCircle CenterX=180.5 CenterY=-32 CenterZ=0 NormalX=0 NormalY=0 NormalZ=1 AngleXU=0 Radius=10 StartAngle=3.14159 EndAngle=4.71239
    g1: ArcOfCircle CenterX=224.5 CenterY=-32 CenterZ=0 NormalX=0 NormalY=0 NormalZ=1 AngleXU=0 Radius=10 StartAngle=4.71239 EndAngle=6.28319
    g2: LineSegment StartX=170.5 StartY=-32 StartZ=0 EndX=170.5 EndY=0 EndZ=0
    g3: LineSegment StartX=234.5 StartY=0 StartZ=0 EndX=234.5 EndY=-32 EndZ=0
    g4: LineSegment StartX=180.5 StartY=-42 StartZ=0 EndX=224.5 EndY=-42 EndZ=0
    g5: LineSegment StartX=167.5 StartY=0 StartZ=0 EndX=167.5 EndY=-32 EndZ=0
    g6: LineSegment StartX=180.5 StartY=-45 StartZ=0 EndX=224.5 EndY=-45 EndZ=0
    g7: LineSegment StartX=237.5 StartY=0 StartZ=0 EndX=237.5 EndY=-32 EndZ=0
    g8: ArcOfCircle CenterX=180.5 CenterY=-32 CenterZ=0 NormalX=0 NormalY=0 NormalZ=1 AngleXU=0 Radius=13 StartAngle=3.14159 EndAngle=4.71239
    g9: ArcOfCircle CenterX=224.5 CenterY=-32 CenterZ=0 NormalX=0 NormalY=0 NormalZ=1 AngleXU=0 Radius=13 StartAngle=4.71239 EndAngle=6.28319
    g10: LineSegment StartX=167.5 StartY=0 StartZ=0 EndX=170.5 EndY=0 EndZ=0
    g11: LineSegment StartX=234.5 StartY=0 StartZ=0 EndX=237.5 EndY=0 EndZ=0
  constraints (40):
    c: Angle(g1) = 1.5708
    c: DistanceY(g1,g1) = 0
    c: DistanceY(g1,g0) = 0
    c: Angle(g0) = 1.5708
    c: DistanceX(g0,g0) = 10
    c: DistanceY(g0,g0) = 0
    c: DistanceX(g1,g1) = 10
    c: Coincident(g2,g0)
    c: Vertical(g2)
    c: PointOnObject(g3,g-1)
    c: Coincident(g3,g1)
    c: Vertical(g3)
    c: DistanceY(g2,g2) = 32
    c: Coincident(g4,g1)
    c: PointOnObject(g5,g-1)
    c: Vertical(g5)
    c: Horizontal(g6)
    c: Vertical(g7)
    c: DistanceX(g5,g2) = 3
    c: DistanceX(g3,g7) = 3
    c: DistanceY(g5,g0) = 0
    c: DistanceY(g7,g1) = 0
    c: DistanceY(g7,g3) = 0
    c: DistanceX(g2,g3) = 64
    c: DistanceX(g0,g6) = 0
    c: DistanceX(g6,g1) = 0
    c: DistanceY(g2) = 0
    c: Coincident(g5,g8)
    c: Coincident(g6,g8)
    c: DistanceY(g6,g0) = 3
    c: Coincident(g6,g9)
    c: Coincident(g7,g9)
    c: Angle(g8) = 1.5708
    c: Angle(g9) = 1.5708
    c: Coincident(g10,g5)
    c: Coincident(g10,g2)
    c: Coincident(g11,g3)
    c: Coincident(g11,g7)
    c: Coincident(g0,g4)
    c: DistanceX(g2) = 170.5
FEATURE [Sketcher::SketchObject] Sketch240  label="outerSRS022"
  ArcFitTolerance = 0
  FullyConstrained = true
  MakeInternals = false
  Placement = pos=(0,0,-80) rot=(0,0,1;0rad)
  sketch-geometry (12):
    g0: ArcOfCircle CenterX=180.5 CenterY=-32 CenterZ=0 NormalX=0 NormalY=0 NormalZ=1 AngleXU=0 Radius=20 StartAngle=3.14159 EndAngle=4.71239
    g1: ArcOfCircle CenterX=224.5 CenterY=-32 CenterZ=0 NormalX=0 NormalY=0 NormalZ=1 AngleXU=0 Radius=20 StartAngle=4.71239 EndAngle=6.28319
    g2: LineSegment StartX=160.5 StartY=-32 StartZ=0 EndX=160.5 EndY=0 EndZ=0
    g3: LineSegment StartX=244.5 StartY=0 StartZ=0 EndX=244.5 EndY=-32 EndZ=0
    g4: LineSegment StartX=180.5 StartY=-52 StartZ=0 EndX=224.5 EndY=-52 EndZ=0
    g5: LineSegment StartX=157.5 StartY=0 StartZ=0 EndX=157.5 EndY=-32 EndZ=0
    g6: LineSegment StartX=180.5 StartY=-55 StartZ=0 EndX=224.5 EndY=-55 EndZ=0
    g7: LineSegment StartX=247.5 StartY=0 StartZ=0 EndX=247.5 EndY=-32 EndZ=0
    g8: ArcOfCircle CenterX=180.5 CenterY=-32 CenterZ=0 NormalX=0 NormalY=0 NormalZ=1 AngleXU=0 Radius=23 StartAngle=3.14159 EndAngle=4.71239
    g9: ArcOfCircle CenterX=224.5 CenterY=-32 CenterZ=0 NormalX=0 NormalY=0 NormalZ=1 AngleXU=0 Radius=23 StartAngle=4.71239 EndAngle=6.28319
    g10: LineSegment StartX=157.5 StartY=0 StartZ=0 EndX=160.5 EndY=0 EndZ=0
    g11: LineSegment StartX=244.5 StartY=0 StartZ=0 EndX=247.5 EndY=0 EndZ=0
  constraints (40):
    c: Angle(g1) = 1.5708
    c: DistanceY(g1,g0) = 0
    c: Angle(g0) = 1.5708
    c: DistanceY(g0,g0) = 0
    c: Coincident(g2,g0)
    c: Vertical(g2)
    c: PointOnObject(g3,g-1)
    c: Coincident(g3,g1)
    c: Vertical(g3)
    c: DistanceY(g2,g2) = 32
    c: Coincident(g4,g1)
    c: PointOnObject(g5,g-1)
    c: Vertical(g5)
    c: Horizontal(g6)
    c: Vertical(g7)
    c: DistanceX(g5,g2) = 3
    c: DistanceX(g3,g7) = 3
    c: DistanceY(g5,g0) = 0
    c: DistanceY(g7,g1) = 0
    c: DistanceY(g7,g3) = 0
    c: DistanceX(g2) = 160.5
    c: DistanceX(g2,g3) = 84
    c: DistanceX(g0,g6) = 0
    c: DistanceX(g6,g1) = 0
    c: DistanceY(g2) = 0
    c: Coincident(g5,g8)
    c: Coincident(g6,g8)
    c: DistanceY(g6,g0) = 3
    c: Coincident(g6,g9)
    c: Coincident(g7,g9)
    c: Angle(g8) = 1.5708
    c: Angle(g9) = 1.5708
    c: Coincident(g10,g5)
    c: Coincident(g10,g2)
    c: Coincident(g11,g3)
    c: Coincident(g11,g7)
    c: DistanceY(g0,g0) = 20
    c: Coincident(g0,g4)
    c: DistanceY(g1,g0) = 0
    c: DistanceY(g1,g1) = 0
FEATURE [Part::Loft] Loft016  label="srs018"
  Closed = false
  MaxDegree = 5
  Ruled = false
  Sections = -> [Sketch239,Sketch240]
  Solid = true
FEATURE [Part::Fillet] Fillet057  label="piCover"
  Base = -> Loft016
  EdgeLinks = -> Loft016 [Edge1,Edge3,Edge5,Edge7,Edge8,Edge10,Edge11,Edge13,Edge14,Edge16,Edge17,Edge19,Edge20,Edge22,Edge23,Edge25,Edge26,Edge28,Edge29,Edge31,Edge32,Edge34,Edge35,Edge36]
  Edges = 24 edges r=1: [Edge1,Edge3,Edge5,Edge7,Edge8,Edge10,Edge11,Edge13,Edge14,Edge16,Edge17,Edge19,Edge20,Edge22,Edge23,Edge25,Edge26,Edge28,Edge29,Edge31,Edge32,Edge34,Edge35,Edge36]
  Placement = pos=(0,0,29) rot=(0,0,1;0rad)
FEATURE [App::Part] Part001  label="unwanted"
  Group = -> [Extrude234,Sketch235,Fillet055,Sketch215,Sketch221,Cylinder002,Cylinder012,Fusion184,Extrude033,Sketch098,Fusion186,Sketch097,Extrude032,USB_C_cable_v4,Part__Feature315,Clone058,Clone059,Cylinder040,Fusion175,Fusion176,Clone056,Clone057,Cylinder039,Fusion173,Fusion174,Clone054,Clone055,Cylinder038,Fusion171,Fusion172,Clone048,Clone049,Cylinder035,Fusion165,Fusion166,Clone050,Clone051,Cylinder036,+34 more]
  Origin = -> Origin022
FEATURE [Sketcher::SketchObject] Sketch241  label="outerSRS023"
  ArcFitTolerance = 0
  FullyConstrained = true
  MakeInternals = false
  Placement = pos=(0,0,-80) rot=(0,0,1;0rad)
  sketch-geometry (12):
    g0: ArcOfCircle CenterX=180.5 CenterY=-32 CenterZ=0 NormalX=0 NormalY=0 NormalZ=1 AngleXU=0 Radius=19 StartAngle=3.14159 EndAngle=4.71239
    g1: ArcOfCircle CenterX=224.5 CenterY=-32 CenterZ=0 NormalX=0 NormalY=0 NormalZ=1 AngleXU=0 Radius=19 StartAngle=4.71239 EndAngle=6.28319
    g2: LineSegment StartX=161.5 StartY=-32 StartZ=0 EndX=161.5 EndY=0 EndZ=0
    g3: LineSegment StartX=243.5 StartY=0 StartZ=0 EndX=243.5 EndY=-32 EndZ=0
    g4: LineSegment StartX=180.5 StartY=-51 StartZ=0 EndX=224.5 EndY=-51 EndZ=0
    g5: LineSegment StartX=158.5 StartY=0 StartZ=0 EndX=158.5 EndY=-32 EndZ=0
    g6: LineSegment StartX=180.5 StartY=-54 StartZ=0 EndX=224.5 EndY=-54 EndZ=0
    g7: LineSegment StartX=246.5 StartY=0 StartZ=0 EndX=246.5 EndY=-32 EndZ=0
    g8: ArcOfCircle CenterX=180.5 CenterY=-32 CenterZ=0 NormalX=0 NormalY=0 NormalZ=1 AngleXU=0 Radius=22 StartAngle=3.14159 EndAngle=4.71239
    g9: ArcOfCircle CenterX=224.5 CenterY=-32 CenterZ=0 NormalX=0 NormalY=0 NormalZ=1 AngleXU=0 Radius=22 StartAngle=4.71239 EndAngle=6.28319
    g10: LineSegment StartX=158.5 StartY=0 StartZ=0 EndX=161.5 EndY=0 EndZ=0
    g11: LineSegment StartX=243.5 StartY=0 StartZ=0 EndX=246.5 EndY=0 EndZ=0
  constraints (40):
    c: Angle(g1) = 1.5708
    c: DistanceY(g1,g0) = 0
    c: Angle(g0) = 1.5708
    c: DistanceY(g0,g0) = 0
    c: Coincident(g2,g0)
    c: Vertical(g2)
    c: PointOnObject(g3,g-1)
    c: Coincident(g3,g1)
    c: Vertical(g3)
    c: DistanceY(g2,g2) = 32
    c: Coincident(g4,g1)
    c: PointOnObject(g5,g-1)
    c: Vertical(g5)
    c: Horizontal(g6)
    c: Vertical(g7)
    c: DistanceX(g5,g2) = 3
    c: DistanceX(g3,g7) = 3
    c: DistanceY(g5,g0) = 0
    c: DistanceY(g7,g1) = 0
    c: DistanceY(g7,g3) = 0
    c: DistanceX(g2) = 161.5
    c: DistanceX(g2,g3) = 82
    c: DistanceX(g0,g6) = 0
    c: DistanceX(g6,g1) = 0
    c: DistanceY(g2) = 0
    c: Coincident(g5,g8)
    c: Coincident(g6,g8)
    c: DistanceY(g6,g0) = 3
    c: Coincident(g6,g9)
    c: Coincident(g7,g9)
    c: Angle(g8) = 1.5708
    c: Angle(g9) = 1.5708
    c: Coincident(g10,g5)
    c: Coincident(g10,g2)
    c: Coincident(g11,g3)
    c: Coincident(g11,g7)
    c: DistanceY(g0,g0) = 19
    c: Coincident(g0,g4)
    c: DistanceY(g1,g0) = 0
    c: DistanceY(g1,g1) = 0
FEATURE [Part::Extrusion] Extrude238  label="piCover001"
  Base = -> Sketch241
  Dir = (0,0,1)
  DirMode = 2
  FaceMakerClass = Part::FaceMakerBullseye
  FaceMakerMode = 3
  LengthFwd = 30.5
  LengthRev = 0
  Solid = true
  Symmetric = false
FEATURE [Part::Fillet] Fillet058
  Base = -> Extrude238
  EdgeLinks = -> Extrude238 [Edge24,Edge25,Edge27,Edge28,Edge30,Edge31,Edge33,Edge34,Edge35,Edge36]
  Edges = 10 edges r=1: [Edge24,Edge25,Edge27,Edge28,Edge30,Edge31,Edge33,Edge34,Edge35,Edge36]
FEATURE [Part::MultiFuse] Fusion228  label="piCover002"
  Shapes = -> [Fillet058,Fillet057,Fillet056]
FEATURE [Sketcher::SketchObject] Sketch242
  ArcFitTolerance = 0
  FullyConstrained = true
  MakeInternals = false
  Placement = pos=(0,0,0) rot=(1,0,0;1.5708rad)
  sketch-geometry (4):
    g0: LineSegment StartX=70 StartY=80 StartZ=0 EndX=247.5 EndY=80 EndZ=0
    g1: LineSegment StartX=247.5 StartY=80 StartZ=0 EndX=247.5 EndY=-80 EndZ=0
    g2: LineSegment StartX=247.5 StartY=-80 StartZ=0 EndX=70 EndY=-80 EndZ=0
    g3: LineSegment StartX=70 StartY=-80 StartZ=0 EndX=70 EndY=80 EndZ=0
  constraints (12):
    c: Coincident(g0,g1)
    c: Coincident(g1,g2)
    c: Coincident(g2,g3)
    c: Coincident(g3,g0)
    c: Horizontal(g0)
    c: Horizontal(g2)
    c: Vertical(g1)
    c: Vertical(g3)
    c: DistanceY(g2) = -80
    c: DistanceY(g0) = 80
    c: DistanceX(g2) = 70
    c: DistanceX(g2,g2) = 177.5
FEATURE [Part::Extrusion] Extrude239  label="srsCuts002"
  Base = -> Sketch242
  Dir = (0,-1,2e-16)
  DirMode = 2
  FaceMakerClass = Part::FaceMakerBullseye
  FaceMakerMode = 3
  LengthFwd = 4.1
  LengthRev = 0
  Solid = true
  Symmetric = false
FEATURE [Part::Cut] Cut013  label="piCover003"
  Base = -> Fusion228
  Tool = -> Extrude239
FEATURE [Sketcher::SketchObject] Sketch244  label="outerSRS024"
  ArcFitTolerance = 0
  FullyConstrained = true
  MakeInternals = false
  Placement = pos=(0,0,-80) rot=(0,0,1;0rad)
  sketch-geometry (12):
    g0: ArcOfCircle CenterX=180.5 CenterY=-32 CenterZ=0 NormalX=0 NormalY=0 NormalZ=1 AngleXU=0 Radius=17 StartAngle=3.14159 EndAngle=4.71239
    g1: ArcOfCircle CenterX=224.5 CenterY=-32 CenterZ=0 NormalX=0 NormalY=0 NormalZ=1 AngleXU=0 Radius=17 StartAngle=4.71239 EndAngle=6.28319
    g2: LineSegment StartX=163.5 StartY=-32 StartZ=0 EndX=163.5 EndY=0 EndZ=0
    g3: LineSegment StartX=241.5 StartY=0 StartZ=0 EndX=241.5 EndY=-32 EndZ=0
    g4: LineSegment StartX=180.5 StartY=-49 StartZ=0 EndX=224.5 EndY=-49 EndZ=0
    g5: LineSegment StartX=158.5 StartY=0 StartZ=0 EndX=158.5 EndY=-32 EndZ=0
    g6: LineSegment StartX=180.5 StartY=-54 StartZ=0 EndX=224.5 EndY=-54 EndZ=0
    g7: LineSegment StartX=246.5 StartY=0 StartZ=0 EndX=246.5 EndY=-32 EndZ=0
    g8: ArcOfCircle CenterX=180.5 CenterY=-32 CenterZ=0 NormalX=0 NormalY=0 NormalZ=1 AngleXU=0 Radius=22 StartAngle=3.14159 EndAngle=4.71239
    g9: ArcOfCircle CenterX=224.5 CenterY=-32 CenterZ=0 NormalX=0 NormalY=0 NormalZ=1 AngleXU=0 Radius=22 StartAngle=4.71239 EndAngle=6.28319
    g10: LineSegment StartX=158.5 StartY=0 StartZ=0 EndX=163.5 EndY=0 EndZ=0
    g11: LineSegment StartX=241.5 StartY=0 StartZ=0 EndX=246.5 EndY=0 EndZ=0
  constraints (40):
    c: Angle(g1) = 1.5708
    c: DistanceY(g1,g0) = 0
    c: Angle(g0) = 1.5708
    c: DistanceY(g0,g0) = 0
    c: Coincident(g2,g0)
    c: Vertical(g2)
    c: PointOnObject(g3,g-1)
    c: Coincident(g3,g1)
    c: Vertical(g3)
    c: DistanceY(g2,g2) = 32
    c: Coincident(g4,g1)
    c: PointOnObject(g5,g-1)
    c: Vertical(g5)
    c: Horizontal(g6)
    c: Vertical(g7)
    c: DistanceY(g5,g0) = 0
    c: DistanceY(g7,g1) = 0
    c: DistanceY(g7,g3) = 0
    c: DistanceX(g0,g6) = 0
    c: DistanceX(g6,g1) = 0
    c: DistanceY(g2) = 0
    c: Coincident(g5,g8)
    c: Coincident(g6,g8)
    c: Coincident(g6,g9)
    c: Coincident(g7,g9)
    c: Angle(g8) = 1.5708
    c: Angle(g9) = 1.5708
    c: Coincident(g10,g5)
    c: Coincident(g10,g2)
    c: Coincident(g11,g3)
    c: Coincident(g11,g7)
    c: Coincident(g0,g4)
    c: DistanceY(g1,g0) = 0
    c: DistanceY(g1,g1) = 0
    c: DistanceX(g5,g7) = 88
    c: DistanceX(g5) = 158.5
    c: DistanceY(g6) = -54
    c: DistanceX(g6,g6) = 44
    c: DistanceX(g6) = 180.5
    c: DistanceX(g5,g2) = 5
FEATURE [Part::Extrusion] Extrude240  label="srsBottom002"
  Base = -> Sketch244
  Dir = (0,0,1)
  DirMode = 2
  FaceMakerClass = Part::FaceMakerBullseye
  FaceMakerMode = 3
  LengthFwd = 2.5
  LengthRev = 0
  Placement = pos=(0,0,38.5) rot=(0,0,1;0rad)
  Solid = true
  Symmetric = false
FEATURE [Part::Fillet] Fillet059  label="srsBottom003"
  Base = -> Extrude240
  EdgeLinks = -> Extrude240 [Edge6,Edge9,Edge12,Edge15,Edge18,Edge24,Edge25,Edge27,Edge28,Edge30,Edge31,Edge33,Edge34,Edge35,Edge36]
  Edges = 15 edges r=1: [Edge6,Edge9,Edge12,Edge15,Edge18,Edge24,Edge25,Edge27,Edge28,Edge30,Edge31,Edge33,Edge34,Edge35,Edge36]
FEATURE [Part::FeaturePython] Clone064  label="M3Nut030"  # WARN: FeaturePython — macro-defined, semantics opaque (R4)
  AttacherType = Attacher::AttachEngine3D
  Fuse = false
  Placement = pos=(0,0,4.5) rot=(0,0,1;0rad)
  Scale = (1.1,1.1,5)
FEATURE [Part::FeaturePython] Clone065  label="M3Nut031"  # WARN: FeaturePython — macro-defined, semantics opaque (R4)
  AttacherType = Attacher::AttachEngine3D
  Fuse = false
  Placement = pos=(0,0,0.9) rot=(0,0,1;0rad)
  Scale = (1.1,1.1,1)
FEATURE [Part::Cylinder] Cylinder043
  Angle = 360
  AttacherType = Attacher::AttachEngine3D
  FirstAngle = 0
  Height = 5
  Radius = 2
  SecondAngle = 0
FEATURE [Part::Cylinder] Cylinder044
  Angle = 360
  AttacherType = Attacher::AttachEngine3D
  FirstAngle = 0
  Height = 5
  Radius = 4
  SecondAngle = 0
FEATURE [Part::MultiFuse] Fusion230
  Shapes = -> [Clone064,Cylinder043]
FEATURE [Part::MultiFuse] Fusion231
  Shapes = -> [Fusion230,Clone065]
FEATURE [Part::MultiCommon] Common001  label="m3NutCut5mm001"
  Placement = pos=(163,13,63) rot=(1,0,0;1.5708rad)
  Shapes = -> [Cylinder044,Fusion231]
FEATURE [Part::Feature] Part__Feature355  label="M3x14s"
  Placement = pos=(163,1.5,63) rot=(1,0,0;1.5708rad)
  shape: bbox 5.501 x 17.29 x 5.501 mm, 84 faces (baked)
FEATURE [Part::Feature] Part__Feature357  label="M3x015"
  Placement = pos=(163,1.5,63) rot=(1,0,0;1.5708rad)
  shape: bbox 5.501 x 17.29 x 5.501 mm, 84 faces (baked)
FEATURE [Sketcher::SketchObject] Sketch245
  ArcFitTolerance = 0
  FullyConstrained = true
  MakeInternals = false
  Placement = pos=(0,0,0) rot=(1,0,0;1.5708rad)
  sketch-geometry (4):
    g0: Circle CenterX=163 CenterY=63 CenterZ=0 NormalX=0 NormalY=0 NormalZ=1 AngleXU=0 Radius=2.875
    g1: Circle CenterX=242 CenterY=63 CenterZ=0 NormalX=0 NormalY=0 NormalZ=1 AngleXU=0 Radius=2.875
    g2: Circle CenterX=163 CenterY=-27 CenterZ=0 NormalX=0 NormalY=0 NormalZ=1 AngleXU=0 Radius=2.875
    g3: Circle CenterX=242 CenterY=-27 CenterZ=0 NormalX=0 NormalY=0 NormalZ=1 AngleXU=0 Radius=2.875
  constraints (12):
    c: Horizontal(g0,g1)
    c: Horizontal(g3,g2)
    c: Vertical(g1,g3)
    c: Vertical(g0,g2)
    c: DistanceX(g0) = 163
    c: DistanceY(g0) = 63
    c: Equal(g0,g1)
    c: Equal(g0,g2)
    c: Equal(g0,g3)
    c: Diameter(g0) = 5.75
    c: DistanceX(g0,g1) = 79
    c: DistanceY(g2,g0) = 90
FEATURE [Part::Extrusion] Extrude241  label="srsCuts003"
  Base = -> Sketch245
  Dir = (0,-1,2e-16)
  DirMode = 2
  FaceMakerClass = Part::FaceMakerBullseye
  FaceMakerMode = 3
  LengthFwd = 3.5
  LengthRev = 0
  Placement = pos=(0,-4,0) rot=(0,0,1;0rad)
  Solid = true
  Symmetric = false
FEATURE [Sketcher::SketchObject] Sketch246
  ArcFitTolerance = 0
  FullyConstrained = true
  MakeInternals = false
  Placement = pos=(0,13,0) rot=(1,0,0;1.5708rad)
  sketch-geometry (6):
    g0: Circle CenterX=163 CenterY=63 CenterZ=0 NormalX=0 NormalY=0 NormalZ=1 AngleXU=0 Radius=1.625
    g1: Circle CenterX=242 CenterY=63 CenterZ=0 NormalX=0 NormalY=0 NormalZ=1 AngleXU=0 Radius=1.625
    g2: Circle CenterX=163 CenterY=-27 CenterZ=0 NormalX=0 NormalY=0 NormalZ=1 AngleXU=0 Radius=1.625
    g3: Circle CenterX=242 CenterY=-27 CenterZ=0 NormalX=0 NormalY=0 NormalZ=1 AngleXU=0 Radius=1.625
    g4: Circle CenterX=163 CenterY=-63 CenterZ=0 NormalX=0 NormalY=0 NormalZ=1 AngleXU=0 Radius=1.625
    g5: Circle CenterX=242 CenterY=-63 CenterZ=0 NormalX=0 NormalY=0 NormalZ=1 AngleXU=0 Radius=1.625
  constraints (18):
    c: Horizontal(g0,g1)
    c: DistanceX(g0) = 163
    c: DistanceY(g0) = 63
    c: DistanceX(g0,g1) = 79
    c: Horizontal(g2,g3)
    c: Equal(g2,g3)
    c: Equal(g2,g1)
    c: Equal(g2,g0)
    c: Diameter(g2) = 3.25
    c: DistanceY(g2,g0) = 90
    c: Vertical(g3,g1)
    c: Vertical(g2,g0)
    c: Vertical(g2,g4)
    c: Vertical(g5,g3)
    c: Horizontal(g4,g5)
    c: DistanceY(g4) = -63
    c: Equal(g4,g5)
    c: Diameter(g4) = 3.25
FEATURE [Part::Extrusion] Extrude242  label="srsCutsForM3s"
  Base = -> Sketch246
  Dir = (0,-1,2e-16)
  DirMode = 2
  FaceMakerClass = Part::FaceMakerBullseye
  FaceMakerMode = 3
  LengthFwd = 17
  LengthRev = 0
  Solid = true
  Symmetric = false
FEATURE [Part::MultiFuse] Fusion253  label="srs019"
  Shapes = -> [Fusion,Fillet059]
FEATURE [Part::MultiFuse] Fusion254  label="srsCuts004"
  Shapes = -> [Extrude241,Extrude007]
FEATURE [Part::Cut] Cut  label="srs020"
  Base = -> Fusion253
  Tool = -> Fusion254
FEATURE [Part::FeaturePython] Clone078  label="M3Nut044"  # WARN: FeaturePython — macro-defined, semantics opaque (R4)
  AttacherType = Attacher::AttachEngine3D
  Fuse = false
  Placement = pos=(175,-8,74) rot=(0.57735,0.57735,0.57735;2.0944rad)
  Scale = (1.09,1.09,1)
FEATURE [Part::FeaturePython] Clone082  label="M3Nut048"  # WARN: FeaturePython — macro-defined, semantics opaque (R4)
  AttacherType = Attacher::AttachEngine3D
  Fuse = false
  Placement = pos=(0,0,4.5) rot=(0,0,1;0rad)
  Scale = (1.1,1.1,5)
FEATURE [Part::FeaturePython] Clone083  label="M3Nut049"  # WARN: FeaturePython — macro-defined, semantics opaque (R4)
  AttacherType = Attacher::AttachEngine3D
  Fuse = false
  Placement = pos=(0,0,0.9) rot=(0,0,1;0rad)
  Scale = (1.1,1.1,1)
FEATURE [Part::Cylinder] Cylinder045
  Angle = 360
  AttacherType = Attacher::AttachEngine3D
  FirstAngle = 0
  Height = 5
  Radius = 2
  SecondAngle = 0
FEATURE [Part::Cylinder] Cylinder046
  Angle = 360
  AttacherType = Attacher::AttachEngine3D
  FirstAngle = 0
  Height = 5
  Radius = 4
  SecondAngle = 0
FEATURE [Part::MultiFuse] Fusion262
  Shapes = -> [Clone082,Cylinder045]
FEATURE [Part::MultiFuse] Fusion263
  Shapes = -> [Fusion262,Clone083]
FEATURE [Part::MultiCommon] Common002  label="m3NutCut5mm002"
  Placement = pos=(242,13,63) rot=(1,0,0;1.5708rad)
  Shapes = -> [Cylinder046,Fusion263]
FEATURE [Part::MultiFuse] Fusion264  label="m3Cuts"
  Shapes = -> [Common002,Common001]
FEATURE [Part::FeaturePython] Clone084  label="M3Nut050"  # WARN: FeaturePython — macro-defined, semantics opaque (R4)
  AttacherType = Attacher::AttachEngine3D
  Fuse = false
  Placement = pos=(0,0,4.5) rot=(0,0,1;0rad)
  Scale = (1.1,1.1,5)
FEATURE [Part::FeaturePython] Clone085  label="M3Nut051"  # WARN: FeaturePython — macro-defined, semantics opaque (R4)
  AttacherType = Attacher::AttachEngine3D
  Fuse = false
  Placement = pos=(0,0,0.9) rot=(0,0,1;0rad)
  Scale = (1.1,1.1,1)
FEATURE [Part::FeaturePython] Clone086  label="M3Nut052"  # WARN: FeaturePython — macro-defined, semantics opaque (R4)
  AttacherType = Attacher::AttachEngine3D
  Fuse = false
  Placement = pos=(0,0,4.5) rot=(0,0,1;0rad)
  Scale = (1.1,1.1,5)
FEATURE [Part::FeaturePython] Clone087  label="M3Nut053"  # WARN: FeaturePython — macro-defined, semantics opaque (R4)
  AttacherType = Attacher::AttachEngine3D
  Fuse = false
  Placement = pos=(0,0,0.9) rot=(0,0,1;0rad)
  Scale = (1.1,1.1,1)
FEATURE [Part::Cylinder] Cylinder047
  Angle = 360
  AttacherType = Attacher::AttachEngine3D
  FirstAngle = 0
  Height = 5
  Radius = 2
  SecondAngle = 0
FEATURE [Part::Cylinder] Cylinder048
  Angle = 360
  AttacherType = Attacher::AttachEngine3D
  FirstAngle = 0
  Height = 5
  Radius = 4
  SecondAngle = 0
FEATURE [Part::Cylinder] Cylinder049
  Angle = 360
  AttacherType = Attacher::AttachEngine3D
  FirstAngle = 0
  Height = 5
  Radius = 2
  SecondAngle = 0
FEATURE [Part::Cylinder] Cylinder050
  Angle = 360
  AttacherType = Attacher::AttachEngine3D
  FirstAngle = 0
  Height = 5
  Radius = 4
  SecondAngle = 0
FEATURE [Part::MultiFuse] Fusion265
  Shapes = -> [Clone084,Cylinder047]
FEATURE [Part::MultiFuse] Fusion266
  Shapes = -> [Fusion265,Clone085]
FEATURE [Part::MultiCommon] Common003  label="m3NutCut5mm003"
  Placement = pos=(163,13,63) rot=(1,0,0;1.5708rad)
  Shapes = -> [Cylinder048,Fusion266]
FEATURE [Part::MultiFuse] Fusion267
  Shapes = -> [Clone086,Cylinder049]
FEATURE [Part::MultiFuse] Fusion268
  Shapes = -> [Fusion267,Clone087]
FEATURE [Part::MultiCommon] Common004  label="m3NutCut5mm004"
  Placement = pos=(242,13,63) rot=(1,0,0;1.5708rad)
  Shapes = -> [Cylinder050,Fusion268]
FEATURE [Part::MultiFuse] Fusion269  label="m3Cuts001"
  Placement = pos=(0,0,-90) rot=(0,0,1;0rad)
  Shapes = -> [Common004,Common003]
FEATURE [Part::MultiFuse] Fusion270  label="m3CutsForBaseMountBatteryHolder"
  Shapes = -> [Fusion269,Fusion264]
FEATURE [Part::Cut] Cut021  label="batteryHousing001"
  Base = -> Fusion224
  Tool = -> Fusion270
FEATURE [Part::Cut] Cut022  label="batteryHousing002"
  Base = -> Cut021
  Tool = -> Extrude242
FEATURE [Sketcher::SketchObject] Sketch300  label="outerSRS026"
  ArcFitTolerance = 0
  FullyConstrained = true
  MakeInternals = false
  Placement = pos=(0,0,-80) rot=(0,0,1;0rad)
  sketch-geometry (6):
    g0: LineSegment StartX=163.5 StartY=0 StartZ=0 EndX=163.5 EndY=-18 EndZ=0
    g1: LineSegment StartX=184 StartY=-38.5 StartZ=0 EndX=221 EndY=-38.5 EndZ=0
    g2: LineSegment StartX=241.5 StartY=0 StartZ=0 EndX=241.5 EndY=-18 EndZ=0
    g3: ArcOfCircle CenterX=184 CenterY=-18 CenterZ=0 NormalX=0 NormalY=0 NormalZ=1 AngleXU=0 Radius=20.5 StartAngle=3.14159 EndAngle=4.71239
    g4: ArcOfCircle CenterX=221 CenterY=-18 CenterZ=0 NormalX=0 NormalY=0 NormalZ=1 AngleXU=0 Radius=20.5 StartAngle=4.71239 EndAngle=6.28319
    g5: LineSegment StartX=163.5 StartY=0 StartZ=0 EndX=241.5 EndY=0 EndZ=0
  constraints (20):
    c: PointOnObject(g5,g-1)
    c: Vertical(g0)
    c: Horizontal(g1)
    c: Vertical(g2)
    c: DistanceY(g2,g5) = 0
    c: Coincident(g0,g3)
    c: Coincident(g1,g3)
    c: Coincident(g1,g4)
    c: Coincident(g2,g4)
    c: Angle(g3) = 1.5708
    c: Angle(g4) = 1.5708
    c: Coincident(g5,g2)
    c: DistanceX(g0) = 163.5
    c: Coincident(g5,g0)
    c: DistanceX(g0,g2) = 78
    c: DistanceY(g0,g0) = 18
    c: DistanceY(g2,g0) = 0
    c: DistanceY(g3,g0) = 0
    c: DistanceY(g4,g2) = 0
    c: DistanceX(g0,g3) = 20.5
FEATURE [Part::Extrusion] Extrude296
  Base = -> Sketch300
  Dir = (0,0,1)
  DirMode = 2
  FaceMakerClass = Part::FaceMakerBullseye
  FaceMakerMode = 3
  LengthFwd = 4
  LengthRev = 0
  Solid = true
  Symmetric = false
FEATURE [Part::Fillet] Fillet062  label="piCoverBottom002"
  Base = -> Extrude296
  EdgeLinks = -> Extrude296 [Edge3,Edge6,Edge9,Edge12,Edge15]
  Edges = 5 edges r=1: [Edge3,Edge6,Edge9,Edge12,Edge15]
FEATURE [Part::Cut] Cut028  label="piCover004"
  Base = -> Cut013
  Tool = -> Fillet062
FEATURE [Sketcher::SketchObject] Sketch014
  ArcFitTolerance = 0
  FullyConstrained = true
  MakeInternals = false
  Placement = pos=(0,0,0) rot=(1,0,0;1.5708rad)
  sketch-geometry (8):
    g0: ArcOfCircle CenterX=12.75 CenterY=15.33 CenterZ=0 NormalX=0 NormalY=0 NormalZ=1 AngleXU=0 Radius=0.9 StartAngle=1.5708 EndAngle=3.14159
    g1: ArcOfCircle CenterX=16.95 CenterY=15.33 CenterZ=0 NormalX=0 NormalY=0 NormalZ=1 AngleXU=0 Radius=0.9 StartAngle=8e-16 EndAngle=1.5708
    g2: ArcOfCircle CenterX=16.95 CenterY=14.43 CenterZ=0 NormalX=0 NormalY=0 NormalZ=1 AngleXU=0 Radius=0.9 StartAngle=4.71239 EndAngle=6.28319
    g3: ArcOfCircle CenterX=12.75 CenterY=14.43 CenterZ=0 NormalX=0 NormalY=0 NormalZ=1 AngleXU=0 Radius=0.9 StartAngle=3.14159 EndAngle=4.71239
    g4: LineSegment StartX=12.75 StartY=16.23 StartZ=0 EndX=16.95 EndY=16.23 EndZ=0
    g5: LineSegment StartX=17.85 StartY=15.33 StartZ=0 EndX=17.85 EndY=14.43 EndZ=0
    g6: LineSegment StartX=16.95 StartY=13.53 StartZ=0 EndX=12.75 EndY=13.53 EndZ=0
    g7: LineSegment StartX=11.85 StartY=14.43 StartZ=0 EndX=11.85 EndY=15.33 EndZ=0
  constraints (28):
    c: Coincident(g4,g0)
    c: Coincident(g4,g1)
    c: Horizontal(g4)
    c: Coincident(g5,g1)
    c: Coincident(g5,g2)
    c: Coincident(g6,g2)
    c: Coincident(g6,g3)
    c: Horizontal(g6)
    c: Coincident(g7,g3)
    c: Coincident(g7,g0)
    c: Vertical(g7)
    c: Radius(g0) = 0.9
    c: DistanceY(g0,g0) = 0
    c: Angle(g3) = 1.5708
    c: DistanceY(g3,g3) = 0
    c: DistanceY(g3,g0) = 0.9
    c: DistanceY(g3) = 14.43
    c: Radius(g3) = 0.9
    c: Radius(g2) = 0.9
    c: Radius(g1) = 0.9
    c: DistanceX(g6,g6) = 4.2
    c: DistanceX(g3) = 12.75
    c: DistanceY(g1,g1) = 0
    c: DistanceX(g2,g2) = 0
    c: Angle(g1) = 1.5708
    c: Angle(g2) = 1.5708
    c: Vertical(g5)
    c: DistanceX(g0,g0) = 0
FEATURE [Part::Extrusion] Extrude014
  Base = -> Sketch014
  Dir = (0,-1,2e-16)
  DirMode = 2
  FaceMakerClass = Part::FaceMakerBullseye
  FaceMakerMode = 3
  LengthFwd = 5
  LengthRev = 0
  Placement = pos=(-0.3,2,-0.1) rot=(0,0,1;0rad)
  Solid = true
  Symmetric = false
FEATURE [Sketcher::SketchObject] Sketch015
  ArcFitTolerance = 0
  FullyConstrained = true
  MakeInternals = false
  Placement = pos=(0,0,0) rot=(1,0,0;1.5708rad)
  sketch-geometry (8):
    g0: ArcOfCircle CenterX=11.7 CenterY=15.45 CenterZ=0 NormalX=0 NormalY=0 NormalZ=1 AngleXU=0 Radius=0.9 StartAngle=1.5708 EndAngle=3.14159
    g1: ArcOfCircle CenterX=17.4 CenterY=15.45 CenterZ=0 NormalX=0 NormalY=0 NormalZ=1 AngleXU=0 Radius=0.9 StartAngle=4e-16 EndAngle=1.5708
    g2: ArcOfCircle CenterX=16.8 CenterY=14.2 CenterZ=0 NormalX=0 NormalY=0 NormalZ=1 AngleXU=0 Radius=1.5 StartAngle=4.71239 EndAngle=6.28319
    g3: ArcOfCircle CenterX=12.3 CenterY=14.2 CenterZ=0 NormalX=0 NormalY=0 NormalZ=1 AngleXU=0 Radius=1.5 StartAngle=3.14159 EndAngle=4.71239
    g4: LineSegment StartX=11.7 StartY=16.35 StartZ=0 EndX=17.4 EndY=16.35 EndZ=0
    g5: LineSegment StartX=18.3 StartY=15.45 StartZ=0 EndX=18.3 EndY=14.2 EndZ=0
    g6: LineSegment StartX=16.8 StartY=12.7 StartZ=0 EndX=12.3 EndY=12.7 EndZ=0
    g7: LineSegment StartX=10.8 StartY=14.2 StartZ=0 EndX=10.8 EndY=15.45 EndZ=0
  constraints (28):
    c: Coincident(g4,g0)
    c: Coincident(g4,g1)
    c: Horizontal(g4)
    c: Coincident(g5,g1)
    c: Coincident(g5,g2)
    c: Coincident(g6,g2)
    c: Coincident(g6,g3)
    c: Horizontal(g6)
    c: Coincident(g7,g3)
    c: Coincident(g7,g0)
    c: Vertical(g7)
    c: Radius(g0) = 0.9
    c: DistanceY(g0,g0) = 0
    c: Angle(g3) = 1.5708
    c: DistanceY(g3,g3) = 0
    c: DistanceY(g3,g0) = 1.25
    c: DistanceY(g3) = 14.2
    c: Radius(g3) = 1.5
    c: Radius(g2) = 1.5
    c: Radius(g1) = 0.9
    c: DistanceX(g6,g6) = 4.5
    c: DistanceX(g3) = 12.3
    c: DistanceY(g1,g1) = 0
    c: DistanceX(g2,g2) = 0
    c: Angle(g1) = 1.5708
    c: Angle(g2) = 1.5708
    c: Vertical(g5)
    c: DistanceX(g0,g0) = 0
FEATURE [Part::Extrusion] Extrude015
  Base = -> Sketch015
  Dir = (0,-1,2e-16)
  DirMode = 2
  FaceMakerClass = Part::FaceMakerBullseye
  FaceMakerMode = 3
  LengthFwd = 1
  LengthRev = 0
  Placement = pos=(0,2.5,0) rot=(0,0,1;0rad)
  Solid = true
  Symmetric = false
FEATURE [Part::MultiFuse] Fusion018  label="button1"
  Placement = pos=(104.5,9.5,-78) rot=(1,0,0;1.5708rad)
  Shapes = -> [Extrude014,Extrude015]
FEATURE [Sketcher::SketchObject] Sketch231
  ArcFitTolerance = 0
  FullyConstrained = true
  MakeInternals = false
  Placement = pos=(0,0,0) rot=(1,0,0;1.5708rad)
  sketch-geometry (8):
    g0: ArcOfCircle CenterX=12.75 CenterY=15.33 CenterZ=0 NormalX=0 NormalY=0 NormalZ=1 AngleXU=0 Radius=0.9 StartAngle=1.5708 EndAngle=3.14159
    g1: ArcOfCircle CenterX=16.95 CenterY=15.33 CenterZ=0 NormalX=0 NormalY=0 NormalZ=1 AngleXU=0 Radius=0.9 StartAngle=8e-16 EndAngle=1.5708
    g2: ArcOfCircle CenterX=16.95 CenterY=14.43 CenterZ=0 NormalX=0 NormalY=0 NormalZ=1 AngleXU=0 Radius=0.9 StartAngle=4.71239 EndAngle=6.28319
    g3: ArcOfCircle CenterX=12.75 CenterY=14.43 CenterZ=0 NormalX=0 NormalY=0 NormalZ=1 AngleXU=0 Radius=0.9 StartAngle=3.14159 EndAngle=4.71239
    g4: LineSegment StartX=12.75 StartY=16.23 StartZ=0 EndX=16.95 EndY=16.23 EndZ=0
    g5: LineSegment StartX=17.85 StartY=15.33 StartZ=0 EndX=17.85 EndY=14.43 EndZ=0
    g6: LineSegment StartX=16.95 StartY=13.53 StartZ=0 EndX=12.75 EndY=13.53 EndZ=0
    g7: LineSegment StartX=11.85 StartY=14.43 StartZ=0 EndX=11.85 EndY=15.33 EndZ=0
  constraints (28):
    c: Coincident(g4,g0)
    c: Coincident(g4,g1)
    c: Horizontal(g4)
    c: Coincident(g5,g1)
    c: Coincident(g5,g2)
    c: Coincident(g6,g2)
    c: Coincident(g6,g3)
    c: Horizontal(g6)
    c: Coincident(g7,g3)
    c: Coincident(g7,g0)
    c: Vertical(g7)
    c: Radius(g0) = 0.9
    c: DistanceY(g0,g0) = 0
    c: Angle(g3) = 1.5708
    c: DistanceY(g3,g3) = 0
    c: DistanceY(g3,g0) = 0.9
    c: DistanceY(g3) = 14.43
    c: Radius(g3) = 0.9
    c: Radius(g2) = 0.9
    c: Radius(g1) = 0.9
    c: DistanceX(g6,g6) = 4.2
    c: DistanceX(g3) = 12.75
    c: DistanceY(g1,g1) = 0
    c: DistanceX(g2,g2) = 0
    c: Angle(g1) = 1.5708
    c: Angle(g2) = 1.5708
    c: Vertical(g5)
    c: DistanceX(g0,g0) = 0
FEATURE [Part::Extrusion] Extrude229
  Base = -> Sketch231
  Dir = (0,-1,2e-16)
  DirMode = 2
  FaceMakerClass = Part::FaceMakerBullseye
  FaceMakerMode = 3
  LengthFwd = 5
  LengthRev = 0
  Placement = pos=(-0.3,2,-0.1) rot=(0,0,1;0rad)
  Solid = true
  Symmetric = false
FEATURE [Sketcher::SketchObject] Sketch232
  ArcFitTolerance = 0
  FullyConstrained = true
  MakeInternals = false
  Placement = pos=(0,0,0) rot=(1,0,0;1.5708rad)
  sketch-geometry (8):
    g0: ArcOfCircle CenterX=11.7 CenterY=15.45 CenterZ=0 NormalX=0 NormalY=0 NormalZ=1 AngleXU=0 Radius=0.9 StartAngle=1.5708 EndAngle=3.14159
    g1: ArcOfCircle CenterX=17.4 CenterY=15.45 CenterZ=0 NormalX=0 NormalY=0 NormalZ=1 AngleXU=0 Radius=0.9 StartAngle=4e-16 EndAngle=1.5708
    g2: ArcOfCircle CenterX=16.8 CenterY=14.2 CenterZ=0 NormalX=0 NormalY=0 NormalZ=1 AngleXU=0 Radius=1.5 StartAngle=4.71239 EndAngle=6.28319
    g3: ArcOfCircle CenterX=12.3 CenterY=14.2 CenterZ=0 NormalX=0 NormalY=0 NormalZ=1 AngleXU=0 Radius=1.5 StartAngle=3.14159 EndAngle=4.71239
    g4: LineSegment StartX=11.7 StartY=16.35 StartZ=0 EndX=17.4 EndY=16.35 EndZ=0
    g5: LineSegment StartX=18.3 StartY=15.45 StartZ=0 EndX=18.3 EndY=14.2 EndZ=0
    g6: LineSegment StartX=16.8 StartY=12.7 StartZ=0 EndX=12.3 EndY=12.7 EndZ=0
    g7: LineSegment StartX=10.8 StartY=14.2 StartZ=0 EndX=10.8 EndY=15.45 EndZ=0
  constraints (28):
    c: Coincident(g4,g0)
    c: Coincident(g4,g1)
    c: Horizontal(g4)
    c: Coincident(g5,g1)
    c: Coincident(g5,g2)
    c: Coincident(g6,g2)
    c: Coincident(g6,g3)
    c: Horizontal(g6)
    c: Coincident(g7,g3)
    c: Coincident(g7,g0)
    c: Vertical(g7)
    c: Radius(g0) = 0.9
    c: DistanceY(g0,g0) = 0
    c: Angle(g3) = 1.5708
    c: DistanceY(g3,g3) = 0
    c: DistanceY(g3,g0) = 1.25
    c: DistanceY(g3) = 14.2
    c: Radius(g3) = 1.5
    c: Radius(g2) = 1.5
    c: Radius(g1) = 0.9
    c: DistanceX(g6,g6) = 4.5
    c: DistanceX(g3) = 12.3
    c: DistanceY(g1,g1) = 0
    c: DistanceX(g2,g2) = 0
    c: Angle(g1) = 1.5708
    c: Angle(g2) = 1.5708
    c: Vertical(g5)
    c: DistanceX(g0,g0) = 0
FEATURE [Part::Extrusion] Extrude230
  Base = -> Sketch232
  Dir = (0,-1,2e-16)
  DirMode = 2
  FaceMakerClass = Part::FaceMakerBullseye
  FaceMakerMode = 3
  LengthFwd = 1
  LengthRev = 0
  Placement = pos=(0,2.5,0) rot=(0,0,1;0rad)
  Solid = true
  Symmetric = false
FEATURE [Part::MultiFuse] Fusion223  label="button005"
  Placement = pos=(72,9.5,-78) rot=(1,0,0;1.5708rad)
  Shapes = -> [Extrude229,Extrude230]
FEATURE [Sketcher::SketchObject] Sketch227
  ArcFitTolerance = 0
  FullyConstrained = true
  MakeInternals = false
  Placement = pos=(0,0,0) rot=(1,0,0;1.5708rad)
  sketch-geometry (12):
    g0: LineSegment StartX=79.5 StartY=-51.5 StartZ=0 EndX=74 EndY=-51.5 EndZ=0
    g1: LineSegment StartX=74 StartY=-51.5 StartZ=0 EndX=74 EndY=-43.5 EndZ=0
    g2: LineSegment StartX=74 StartY=-43.5 StartZ=0 EndX=82.5 EndY=-43.5 EndZ=0
    g3: LineSegment StartX=82.5 StartY=-43.5 StartZ=0 EndX=82.5 EndY=-48.5 EndZ=0
    g4: ArcOfCircle CenterX=79.5 CenterY=-48.5 CenterZ=0 NormalX=0 NormalY=0 NormalZ=1 AngleXU=0 Radius=3 StartAngle=4.71239 EndAngle=6.28319
    g5: Circle CenterX=79.5 CenterY=-48.5 CenterZ=0 NormalX=0 NormalY=0 NormalZ=1 AngleXU=0 Radius=1.75
    g6: LineSegment StartX=148 StartY=-51.25 StartZ=0 EndX=137.5 EndY=-51.25 EndZ=0
    g7: LineSegment StartX=148 StartY=-43.5 StartZ=0 EndX=134.75 EndY=-43.5 EndZ=0
    g8: LineSegment StartX=134.75 StartY=-43.5 StartZ=0 EndX=134.75 EndY=-48.5 EndZ=0
    g9: ArcOfCircle CenterX=137.5 CenterY=-48.5 CenterZ=0 NormalX=0 NormalY=0 NormalZ=1 AngleXU=0 Radius=2.75 StartAngle=3.14159 EndAngle=4.71239
    g10: LineSegment StartX=148 StartY=-51.25 StartZ=0 EndX=148 EndY=-43.5 EndZ=0
    g11: Circle CenterX=137.5 CenterY=-48.5 CenterZ=0 NormalX=0 NormalY=0 NormalZ=1 AngleXU=0 Radius=1.75
  constraints (36):
    c: Horizontal(g0)
    c: Coincident(g1,g0)
    c: Vertical(g1)
    c: Coincident(g2,g1)
    c: Horizontal(g2)
    c: Coincident(g3,g2)
    c: Vertical(g3)
    c: Coincident(g4,g3)
    c: Angle(g4) = 1.5708
    c: Coincident(g0,g4)
    c: DistanceY(g0) = -51.5
    c: Vertical(g0,g4)
    c: DistanceX(g4) = 79.5
    c: DistanceY(g4) = -48.5
    c: DistanceX(g0) = 74
    c: Coincident(g5,g4)
    c: Diameter(g5) = 3.5
    c: Horizontal(g6)
    c: Horizontal(g7)
    c: Coincident(g8,g7)
    c: Vertical(g8)
    c: Coincident(g9,g6)
    c: Coincident(g9,g8)
    c: Horizontal(g9,g4)
    c: DistanceX(g4,g9) = 58
    c: DistanceX(g9,g6) = 10.5
    c: Coincident(g10,g6)
    c: Coincident(g10,g7)
    c: Vertical(g10)
    c: Angle(g9) = 1.5708
    c: Horizontal(g9,g8)
    c: Diameter(g9) = 5.5
    c: Coincident(g11,g9)
    c: Diameter(g11) = 3.5
    c: DistanceY(g1,g1) = 8
    c: DistanceY(g2,g7) = 0
FEATURE [Part::Extrusion] Extrude226  label="piZeroHolds"
  Base = -> Sketch227
  Dir = (0,-1,2e-16)
  DirMode = 2
  FaceMakerClass = Part::FaceMakerBullseye
  FaceMakerMode = 3
  LengthFwd = 7
  LengthRev = 0
  Solid = true
  Symmetric = false
FEATURE [Sketcher::SketchObject] Sketch202
  ArcFitTolerance = 0
  FullyConstrained = true
  MakeInternals = false
  Placement = pos=(0,0,0) rot=(1,0,0;1.5708rad)
  sketch-geometry (8):
    g0: ArcOfCircle CenterX=12.75 CenterY=15.33 CenterZ=0 NormalX=0 NormalY=0 NormalZ=1 AngleXU=0 Radius=0.9 StartAngle=1.5708 EndAngle=3.14159
    g1: ArcOfCircle CenterX=16.95 CenterY=15.33 CenterZ=0 NormalX=0 NormalY=0 NormalZ=1 AngleXU=0 Radius=0.9 StartAngle=8e-16 EndAngle=1.5708
    g2: ArcOfCircle CenterX=16.95 CenterY=14.43 CenterZ=0 NormalX=0 NormalY=0 NormalZ=1 AngleXU=0 Radius=0.9 StartAngle=4.71239 EndAngle=6.28319
    g3: ArcOfCircle CenterX=12.75 CenterY=14.43 CenterZ=0 NormalX=0 NormalY=0 NormalZ=1 AngleXU=0 Radius=0.9 StartAngle=3.14159 EndAngle=4.71239
    g4: LineSegment StartX=12.75 StartY=16.23 StartZ=0 EndX=16.95 EndY=16.23 EndZ=0
    g5: LineSegment StartX=17.85 StartY=15.33 StartZ=0 EndX=17.85 EndY=14.43 EndZ=0
    g6: LineSegment StartX=16.95 StartY=13.53 StartZ=0 EndX=12.75 EndY=13.53 EndZ=0
    g7: LineSegment StartX=11.85 StartY=14.43 StartZ=0 EndX=11.85 EndY=15.33 EndZ=0
  constraints (28):
    c: Coincident(g4,g0)
    c: Coincident(g4,g1)
    c: Horizontal(g4)
    c: Coincident(g5,g1)
    c: Coincident(g5,g2)
    c: Coincident(g6,g2)
    c: Coincident(g6,g3)
    c: Horizontal(g6)
    c: Coincident(g7,g3)
    c: Coincident(g7,g0)
    c: Vertical(g7)
    c: Radius(g0) = 0.9
    c: DistanceY(g0,g0) = 0
    c: Angle(g3) = 1.5708
    c: DistanceY(g3,g3) = 0
    c: DistanceY(g3,g0) = 0.9
    c: DistanceY(g3) = 14.43
    c: Radius(g3) = 0.9
    c: Radius(g2) = 0.9
    c: Radius(g1) = 0.9
    c: DistanceX(g6,g6) = 4.2
    c: DistanceX(g3) = 12.75
    c: DistanceY(g1,g1) = 0
    c: DistanceX(g2,g2) = 0
    c: Angle(g1) = 1.5708
    c: Angle(g2) = 1.5708
    c: Vertical(g5)
    c: DistanceX(g0,g0) = 0
FEATURE [Part::Extrusion] Extrude201
  Base = -> Sketch202
  Dir = (0,-1,2e-16)
  DirMode = 2
  FaceMakerClass = Part::FaceMakerBullseye
  FaceMakerMode = 3
  LengthFwd = 2.75
  LengthRev = 0
  Placement = pos=(-0.3,2,-0.1) rot=(0,0,1;0rad)
  Solid = true
  Symmetric = false
FEATURE [Sketcher::SketchObject] Sketch203
  ArcFitTolerance = 0
  FullyConstrained = true
  MakeInternals = false
  Placement = pos=(0,0,0) rot=(1,0,0;1.5708rad)
  sketch-geometry (8):
    g0: ArcOfCircle CenterX=11.7 CenterY=15.45 CenterZ=0 NormalX=0 NormalY=0 NormalZ=1 AngleXU=0 Radius=0.9 StartAngle=1.5708 EndAngle=3.14159
    g1: ArcOfCircle CenterX=17.4 CenterY=15.45 CenterZ=0 NormalX=0 NormalY=0 NormalZ=1 AngleXU=0 Radius=0.9 StartAngle=4e-16 EndAngle=1.5708
    g2: ArcOfCircle CenterX=16.8 CenterY=14.2 CenterZ=0 NormalX=0 NormalY=0 NormalZ=1 AngleXU=0 Radius=1.5 StartAngle=4.71239 EndAngle=6.28319
    g3: ArcOfCircle CenterX=12.3 CenterY=14.2 CenterZ=0 NormalX=0 NormalY=0 NormalZ=1 AngleXU=0 Radius=1.5 StartAngle=3.14159 EndAngle=4.71239
    g4: LineSegment StartX=11.7 StartY=16.35 StartZ=0 EndX=17.4 EndY=16.35 EndZ=0
    g5: LineSegment StartX=18.3 StartY=15.45 StartZ=0 EndX=18.3 EndY=14.2 EndZ=0
    g6: LineSegment StartX=16.8 StartY=12.7 StartZ=0 EndX=12.3 EndY=12.7 EndZ=0
    g7: LineSegment StartX=10.8 StartY=14.2 StartZ=0 EndX=10.8 EndY=15.45 EndZ=0
  constraints (28):
    c: Coincident(g4,g0)
    c: Coincident(g4,g1)
    c: Horizontal(g4)
    c: Coincident(g5,g1)
    c: Coincident(g5,g2)
    c: Coincident(g6,g2)
    c: Coincident(g6,g3)
    c: Horizontal(g6)
    c: Coincident(g7,g3)
    c: Coincident(g7,g0)
    c: Vertical(g7)
    c: Radius(g0) = 0.9
    c: DistanceY(g0,g0) = 0
    c: Angle(g3) = 1.5708
    c: DistanceY(g3,g3) = 0
    c: DistanceY(g3,g0) = 1.25
    c: DistanceY(g3) = 14.2
    c: Radius(g3) = 1.5
    c: Radius(g2) = 1.5
    c: Radius(g1) = 0.9
    c: DistanceX(g6,g6) = 4.5
    c: DistanceX(g3) = 12.3
    c: DistanceY(g1,g1) = 0
    c: DistanceX(g2,g2) = 0
    c: Angle(g1) = 1.5708
    c: Angle(g2) = 1.5708
    c: Vertical(g5)
    c: DistanceX(g0,g0) = 0
FEATURE [Part::Extrusion] Extrude202
  Base = -> Sketch203
  Dir = (0,-1,2e-16)
  DirMode = 2
  FaceMakerClass = Part::FaceMakerBullseye
  FaceMakerMode = 3
  LengthFwd = 1
  LengthRev = 0
  Placement = pos=(0,2.5,0) rot=(0,0,1;0rad)
  Solid = true
  Symmetric = false
FEATURE [Part::MultiFuse] Fusion198  label="button004"
  Shapes = -> [Extrude201,Extrude202]
FEATURE [Sketcher::SketchObject] Sketch204
  ArcFitTolerance = 0
  FullyConstrained = true
  MakeInternals = false
  Placement = pos=(0,0,0) rot=(1,0,0;1.5708rad)
  sketch-geometry (46):
    g0: LineSegment StartX=11.75 StartY=19.5 StartZ=0 EndX=21.5 EndY=19.5 EndZ=0
    g1: LineSegment StartX=21.5 StartY=19.5 StartZ=0 EndX=23.75 EndY=22 EndZ=0
    g2: LineSegment StartX=23.75 StartY=22 StartZ=0 EndX=23.75 EndY=25 EndZ=0
    g3: LineSegment StartX=23.75 StartY=25 StartZ=0 EndX=9.5 EndY=25 EndZ=0
    g4: LineSegment StartX=9.5 StartY=25 StartZ=0 EndX=9.5 EndY=22 EndZ=0
    g5: LineSegment StartX=40 StartY=24.5 StartZ=0 EndX=40 EndY=22 EndZ=0
    g6: LineSegment StartX=40 StartY=22 StartZ=0 EndX=42.5 EndY=19.5 EndZ=0
    g7: LineSegment StartX=42.5 StartY=19.5 StartZ=0 EndX=48.7 EndY=19.5 EndZ=0
    g8: LineSegment StartX=48.7 StartY=19.5 StartZ=0 EndX=51.2 EndY=22 EndZ=0
    g9: LineSegment StartX=51.2 StartY=22 StartZ=0 EndX=51.2 EndY=24.5 EndZ=0
    g10: LineSegment StartX=51.2 StartY=24.5 StartZ=0 EndX=40 EndY=24.5 EndZ=0
    g11: LineSegment StartX=52.45 StartY=24.5 StartZ=0 EndX=52.45 EndY=22 EndZ=0
    g12: LineSegment StartX=52.45 StartY=22 StartZ=0 EndX=54.95 EndY=19.5 EndZ=0
    g13: LineSegment StartX=54.95 StartY=19.5 StartZ=0 EndX=61.15 EndY=19.5 EndZ=0
    g14: LineSegment StartX=61.15 StartY=19.5 StartZ=0 EndX=63.65 EndY=22 EndZ=0
    g15: LineSegment StartX=63.65 StartY=22 StartZ=0 EndX=63.65 EndY=24.5 EndZ=0
    g16: LineSegment StartX=63.65 StartY=24.5 StartZ=0 EndX=52.45 EndY=24.5 EndZ=0
    g17: LineSegment StartX=9.5 StartY=22 StartZ=0 EndX=11.75 EndY=19.5 EndZ=0
    g18: ArcOfCircle CenterX=12.3 CenterY=15.45 CenterZ=0 NormalX=0 NormalY=0 NormalZ=1 AngleXU=0 Radius=1 StartAngle=1.5708 EndAngle=3.14159
    g19: LineSegment StartX=11.3 StartY=15.45 StartZ=0 EndX=11.3 EndY=14.2 EndZ=0
    g20: LineSegment StartX=12.3 StartY=16.45 StartZ=0 EndX=16.8 EndY=16.45 EndZ=0
    g21: ArcOfCircle CenterX=16.8 CenterY=15.45 CenterZ=0 NormalX=0 NormalY=0 NormalZ=1 AngleXU=0 Radius=1 StartAngle=3e-16 EndAngle=1.5708
    g22: ArcOfCircle CenterX=16.8 CenterY=14.2 CenterZ=0 NormalX=0 NormalY=0 NormalZ=1 AngleXU=0 Radius=1 StartAngle=4.71239 EndAngle=6.28319
    g23: ArcOfCircle CenterX=12.3 CenterY=14.2 CenterZ=0 NormalX=0 NormalY=0 NormalZ=1 AngleXU=0 Radius=1 StartAngle=3.14159 EndAngle=4.71239
    g24: LineSegment StartX=12.3 StartY=13.2 StartZ=0 EndX=16.8 EndY=13.2 EndZ=0
    g25: LineSegment StartX=17.8 StartY=15.45 StartZ=0 EndX=17.8 EndY=14.2 EndZ=0
    g26: Circle CenterX=18.9 CenterY=16.475 CenterZ=0 NormalX=0 NormalY=0 NormalZ=1 AngleXU=0 Radius=0.5
    g27: Circle CenterX=21.09 CenterY=16.475 CenterZ=0 NormalX=0 NormalY=0 NormalZ=1 AngleXU=0 Radius=0.5
    g28: Circle CenterX=23.28 CenterY=16.475 CenterZ=0 NormalX=0 NormalY=0 NormalZ=1 AngleXU=0 Radius=0.5
    g29: Circle CenterX=25.47 CenterY=16.475 CenterZ=0 NormalX=0 NormalY=0 NormalZ=1 AngleXU=0 Radius=0.5
    g30: LineSegment StartX=44.8 StartY=16.45 StartZ=0 EndX=49.3 EndY=16.45 EndZ=0
    g31: LineSegment StartX=50.3 StartY=15.45 StartZ=0 EndX=50.3 EndY=14.2 EndZ=0
    g32: LineSegment StartX=49.3 StartY=13.2 StartZ=0 EndX=44.8 EndY=13.2 EndZ=0
    g33: LineSegment StartX=43.8 StartY=15.45 StartZ=0 EndX=43.8 EndY=14.2 EndZ=0
    g34: ArcOfCircle CenterX=44.8 CenterY=15.45 CenterZ=0 NormalX=0 NormalY=0 NormalZ=1 AngleXU=0 Radius=1 StartAngle=1.5708 EndAngle=3.14159
    g35: ArcOfCircle CenterX=49.3 CenterY=15.45 CenterZ=0 NormalX=0 NormalY=0 NormalZ=1 AngleXU=0 Radius=1 StartAngle=3e-16 EndAngle=1.5708
    g36: ArcOfCircle CenterX=49.3 CenterY=14.2 CenterZ=0 NormalX=0 NormalY=0 NormalZ=1 AngleXU=0 Radius=1 StartAngle=4.71239 EndAngle=6.28319
    g37: ArcOfCircle CenterX=44.8 CenterY=14.2 CenterZ=0 NormalX=0 NormalY=0 NormalZ=1 AngleXU=0 Radius=1 StartAngle=3.14159 EndAngle=4.71239
    g38: LineSegment StartX=52.25 StartY=15.58 StartZ=0 EndX=52.25 EndY=14.58 EndZ=0
    g39: LineSegment StartX=53.5 StartY=16.83 StartZ=0 EndX=60.5 EndY=16.83 EndZ=0
    g40: LineSegment StartX=53.5 StartY=13.33 StartZ=0 EndX=60.5 EndY=13.33 EndZ=0
    g41: LineSegment StartX=61.75 StartY=15.58 StartZ=0 EndX=61.75 EndY=14.58 EndZ=0
    g42: ArcOfCircle CenterX=53.5 CenterY=15.58 CenterZ=0 NormalX=0 NormalY=0 NormalZ=1 AngleXU=0 Radius=1.25 StartAngle=1.5708 EndAngle=3.14159
    g43: ArcOfCircle CenterX=60.5 CenterY=15.58 CenterZ=0 NormalX=0 NormalY=0 NormalZ=1 AngleXU=0 Radius=1.25 StartAngle=2e-16 EndAngle=1.5708
    g44: ArcOfCircle CenterX=60.5 CenterY=14.58 CenterZ=0 NormalX=0 NormalY=0 NormalZ=1 AngleXU=0 Radius=1.25 StartAngle=4.7124 EndAngle=6.28319
    g45: ArcOfCircle CenterX=53.5 CenterY=14.58 CenterZ=0 NormalX=0 NormalY=0 NormalZ=1 AngleXU=0 Radius=1.25 StartAngle=3.14159 EndAngle=4.71239
  constraints (150):
    c: Horizontal(g0)
    c: Coincident(g0,g1)
    c: Coincident(g1,g2)
    c: Coincident(g2,g3)
    c: Horizontal(g3)
    c: Coincident(g3,g4)
    c: Vertical(g4)
    c: Coincident(g5,g6)
    c: Coincident(g6,g7)
    c: Horizontal(g7)
    c: Coincident(g7,g8)
    c: Coincident(g8,g9)
    c: Vertical(g9)
    c: Coincident(g9,g10)
    c: Coincident(g10,g5)
    c: Coincident(g11,g12)
    c: Coincident(g12,g13)
    c: Horizontal(g13)
    c: Coincident(g13,g14)
    c: Coincident(g14,g15)
    c: Vertical(g15)
    c: Coincident(g15,g16)
    c: Coincident(g16,g11)
    c: Horizontal(g16)
    c: Coincident(g17,g4)
    c: Coincident(g0,g17)
    c: DistanceX(g3) = 9.5
    c: DistanceX(g3,g3) = 14.25
    c: Vertical(g2)
    c: DistanceY(g3) = 25
    c: DistanceY(g4) = 22
    c: DistanceY(g4,g1) = 0
    c: DistanceX(g4,g0) = 2.25
    c: DistanceX(g0,g1) = 2.25
    c: Horizontal(g10)
    c: Vertical(g5)
    c: Vertical(g11)
    c: DistanceX(g5) = 40
    c: DistanceX(g5,g9) = 11.2
    c: DistanceY(g11,g9) = 0
    c: DistanceY(g5,g5) = 2.5
    c: DistanceY(g8,g5) = 0
    c: DistanceY(g11,g8) = 0
    c: DistanceY(g14,g11) = 0
    c: DistanceY(g6,g5) = 2.5
    c: DistanceX(g5,g6) = 2.5
    c: DistanceX(g7,g8) = 2.5
    c: DistanceX(g9,g11) = 1.25
    c: DistanceY(g12,g7) = 0
    c: DistanceX(g11,g12) = 2.5
    c: DistanceX(g13,g14) = 2.5
    c: DistanceX(g11,g15) = 11.2
    c: DistanceY(g0,g4) = 2.5
    c: DistanceY(g5) = 24.5
    c: Coincident(g19,g18)
    c: Vertical(g19)
    c: Horizontal(g20)
    c: Coincident(g21,g20)
    c: Coincident(g23,g19)
    c: Coincident(g24,g23)
    c: Coincident(g24,g22)
    c: Horizontal(g24)
    c: Coincident(g25,g21)
    c: Coincident(g25,g22)
    c: Vertical(g25)
    c: Coincident(g18,g20)
    c: Radius(g18) = 1
    c: Angle(g18) = 1.5708
    c: Angle(g21) = 1.5708
    c: Angle(g22) = 1.5708
    c: Angle(g23) = 1.5708
    c: DistanceX(g23) = 12.3
    c: DistanceY(g23) = 13.2
    c: DistanceX(g19) = 11.3
    c: DistanceY(g23,g19) = 0
    c: DistanceY(g18,g18) = 0
    c: DistanceX(g21,g20) = 0
    c: Radius(g21) = 1
    c: Radius(g22) = 1
    c: DistanceX(g22,g22) = 0
    c: DistanceX(g18,g20) = 4.5
    c: DistanceX(g26) = 18.9
    c: Radius(g26) = 0.5
    c: DistanceY(g26) = 16.475
    c: DistanceX(g26,g27) = 2.19
    c: DistanceY(g26,g27) = 0
    c: DistanceY(g28,g27) = 0
    c: DistanceY(g29,g28) = 0
    c: DistanceX(g27,g28) = 2.19
    c: Radius(g27) = 0.5
    c: Radius(g28) = 0.5
    c: Radius(g29) = 0.5
    c: DistanceX(g28,g29) = 2.19
    c: DistanceY(g23,g18) = 1.25
    c: Horizontal(g30)
    c: Vertical(g31)
    c: Vertical(g33)
    c: Coincident(g33,g34)
    c: Coincident(g33,g37)
    c: Coincident(g32,g37)
    c: Coincident(g32,g36)
    c: Coincident(g31,g36)
    c: Coincident(g31,g35)
    c: Coincident(g30,g35)
    c: Coincident(g30,g34)
    c: Angle(g34) = 1.5708
    c: Angle(g35) = 1.5708
    c: Angle(g37) = 1.5708
    c: Angle(g36) = 1.5708
    c: DistanceY(g18,g34) = 0
    c: DistanceY(g34,g33) = 0
    c: Radius(g34) = 1
    c: DistanceY(g33,g37) = 0
    c: Radius(g37) = 1
    c: Radius(g36) = 1
    c: Radius(g35) = 1
    c: DistanceY(g33,g23) = 0
    c: DistanceY(g31,g36) = 0
    c: Horizontal(g32)
    c: DistanceX(g35,g30) = 0
    c: DistanceX(g32,g32) = 4.5
    c: Vertical(g38)
    c: Horizontal(g39)
    c: Horizontal(g40)
    c: Vertical(g41)
    c: Coincident(g42,g38)
    c: Coincident(g42,g39)
    c: Coincident(g43,g39)
    c: Coincident(g45,g38)
    c: Coincident(g45,g40)
    c: Coincident(g40,g44)
    c: Coincident(g41,g44)
    c: Coincident(g41,g43)
    c: DistanceX(g42) = 53.5
    c: DistanceY(g42) = 15.58
    c: DistanceX(g42,g45) = 0
    c: DistanceY(g45,g42) = 1
    c: Radius(g42) = 1.25
    c: Radius(g44) = 1.25
    c: Radius(g43) = 1.25
    c: DistanceX(g45,g40) = 0
    c: DistanceX(g42,g39) = 0
    c: DistanceY(g42,g43) = 0
    c: DistanceY(g44,g45) = 0
    c: DistanceY(g45,g38) = 0
    c: DistanceX(g42,g43) = 7
    c: DistanceX(g18,g34) = 32.5
    c: DistanceY(g41,g44) = 0
    c: DistanceY(g43,g41) = 0
    c: Angle(g42) = 1.5708
FEATURE [Part::Extrusion] Extrude203  label="lightBottomCutDone007"
  Base = -> Sketch204
  Dir = (0,-1,2e-16)
  DirMode = 2
  FaceMakerClass = Part::FaceMakerBullseye
  FaceMakerMode = 3
  LengthFwd = 5
  LengthRev = 0
  Placement = pos=(0,2,0) rot=(0,0,1;0rad)
  Solid = true
  Symmetric = false
FEATURE [Sketcher::SketchObject] Sketch206
  ArcFitTolerance = 0
  FullyConstrained = true
  MakeInternals = false
  Placement = pos=(0,0,0) rot=(1,0,0;1.5708rad)
  sketch-geometry (8):
    g0: ArcOfCircle CenterX=11.8 CenterY=15.45 CenterZ=0 NormalX=0 NormalY=0 NormalZ=1 AngleXU=0 Radius=1.25 StartAngle=1.5708 EndAngle=3.14159
    g1: ArcOfCircle CenterX=17.3 CenterY=15.45 CenterZ=0 NormalX=0 NormalY=0 NormalZ=1 AngleXU=0 Radius=1.25 StartAngle=-9e-16 EndAngle=1.5708
    g2: ArcOfCircle CenterX=16.8 CenterY=14.2 CenterZ=0 NormalX=0 NormalY=0 NormalZ=1 AngleXU=0 Radius=1.75 StartAngle=4.71239 EndAngle=6.28319
    g3: ArcOfCircle CenterX=12.3 CenterY=14.2 CenterZ=0 NormalX=0 NormalY=0 NormalZ=1 AngleXU=0 Radius=1.75 StartAngle=3.14159 EndAngle=4.71239
    g4: LineSegment StartX=11.8 StartY=16.7 StartZ=0 EndX=17.3 EndY=16.7 EndZ=0
    g5: LineSegment StartX=18.55 StartY=15.45 StartZ=0 EndX=18.55 EndY=14.2 EndZ=0
    g6: LineSegment StartX=16.8 StartY=12.45 StartZ=0 EndX=12.3 EndY=12.45 EndZ=0
    g7: LineSegment StartX=10.55 StartY=14.2 StartZ=0 EndX=10.55 EndY=15.45 EndZ=0
  constraints (28):
    c: Coincident(g4,g0)
    c: Coincident(g4,g1)
    c: Horizontal(g4)
    c: Coincident(g5,g1)
    c: Coincident(g5,g2)
    c: Coincident(g6,g2)
    c: Coincident(g6,g3)
    c: Horizontal(g6)
    c: Coincident(g7,g3)
    c: Coincident(g7,g0)
    c: Vertical(g7)
    c: Radius(g0) = 1.25
    c: DistanceY(g0,g0) = 0
    c: Angle(g3) = 1.5708
    c: DistanceY(g3,g3) = 0
    c: DistanceY(g3,g0) = 1.25
    c: DistanceY(g3) = 14.2
    c: Radius(g3) = 1.75
    c: Radius(g2) = 1.75
    c: Radius(g1) = 1.25
    c: DistanceX(g6,g6) = 4.5
    c: DistanceX(g3) = 12.3
    c: DistanceY(g1,g1) = 0
    c: DistanceX(g2,g2) = 0
    c: Angle(g1) = 1.5708
    c: Angle(g2) = 1.5708
    c: Vertical(g5)
    c: DistanceX(g0,g0) = 0
FEATURE [Part::Extrusion] Extrude207  label="buttonCuts015"
  Base = -> Sketch206
  Dir = (0,-1,2e-16)
  DirMode = 2
  FaceMakerClass = Part::FaceMakerBullseye
  FaceMakerMode = 3
  LengthFwd = 0.6
  LengthRev = 0
  Placement = pos=(32.5,2,0) rot=(0,0,1;0rad)
  Solid = true
  Symmetric = false
FEATURE [Sketcher::SketchObject] Sketch207
  ArcFitTolerance = 0
  FullyConstrained = true
  MakeInternals = false
  Placement = pos=(0,0,0) rot=(0.57735,0.57735,0.57735;2.0944rad)
  sketch-geometry (4):
    g0: LineSegment StartX=8 StartY=23 StartZ=0 EndX=26 EndY=23 EndZ=0
    g1: LineSegment StartX=26 StartY=23 StartZ=0 EndX=26 EndY=20 EndZ=0
    g2: LineSegment StartX=26 StartY=20 StartZ=0 EndX=8 EndY=20 EndZ=0
    g3: LineSegment StartX=8 StartY=20 StartZ=0 EndX=8 EndY=23 EndZ=0
  constraints (12):
    c: Coincident(g0,g1)
    c: Coincident(g1,g2)
    c: Coincident(g2,g3)
    c: Coincident(g3,g0)
    c: Horizontal(g0)
    c: Horizontal(g2)
    c: Vertical(g1)
    c: Vertical(g3)
    c: DistanceX(g2) = 8
    c: DistanceX(g2,g0) = 18
    c: DistanceY(g2) = 20
    c: DistanceY(g2,g0) = 3
FEATURE [Part::Extrusion] Extrude206  label="leftInCut007"
  Base = -> Sketch207
  Dir = (1,0,0)
  DirMode = 2
  FaceMakerClass = Part::FaceMakerBullseye
  FaceMakerMode = 3
  LengthFwd = 5
  LengthRev = 0
  Placement = pos=(72,1,0) rot=(0,0,1;0rad)
  Solid = true
  Symmetric = false
FEATURE [Sketcher::SketchObject] Sketch205
  ArcFitTolerance = 0
  AttachmentSupport = -> [Extrude206]
  FullyConstrained = true
  MakeInternals = false
  MapMode = 4
  Placement = pos=(72,1,0) rot=(0.57735,0.57735,0.57735;2.0944rad)
  sketch-geometry (4):
    g0: LineSegment StartX=26 StartY=19.9 StartZ=0 EndX=12 EndY=19.9 EndZ=0
    g1: LineSegment StartX=12 StartY=19.9 StartZ=0 EndX=12 EndY=22.9 EndZ=0
    g2: LineSegment StartX=12 StartY=22.9 StartZ=0 EndX=26 EndY=22.9 EndZ=0
    g3: LineSegment StartX=26 StartY=22.9 StartZ=0 EndX=26 EndY=19.9 EndZ=0
  constraints (12):
    c: Coincident(g0,g1)
    c: Coincident(g1,g2)
    c: Coincident(g2,g3)
    c: Coincident(g3,g0)
    c: Horizontal(g0)
    c: Horizontal(g2)
    c: Vertical(g1)
    c: Vertical(g3)
    c: DistanceX(g0,g0) = 14
    c: DistanceX(g1) = 12
    c: DistanceY(g1) = 22.9
    c: DistanceY(g1,g1) = 3
FEATURE [Part::Extrusion] Extrude204  label="sdCut007"
  Base = -> Sketch205
  Dir = (1,0,0)
  DirMode = 2
  FaceMakerClass = Part::FaceMakerBullseye
  FaceMakerMode = 3
  LengthFwd = 5
  LengthRev = 0
  Placement = pos=(-70,0,0) rot=(0,0,1;0rad)
  Reversed = true
  Solid = true
  Symmetric = false
FEATURE [Part::MultiFuse] Fusion201  label="bottomCutsHorDone007"
  Shapes = -> [Extrude204,Extrude206]
FEATURE [Sketcher::SketchObject] Sketch208
  ArcFitTolerance = 0
  FullyConstrained = true
  MakeInternals = false
  Placement = pos=(0,0,0) rot=(1,0,0;1.5708rad)
  sketch-geometry (8):
    g0: ArcOfCircle CenterX=11.8 CenterY=15.45 CenterZ=0 NormalX=0 NormalY=0 NormalZ=1 AngleXU=0 Radius=1.25 StartAngle=1.5708 EndAngle=3.14159
    g1: ArcOfCircle CenterX=17.3 CenterY=15.45 CenterZ=0 NormalX=0 NormalY=0 NormalZ=1 AngleXU=0 Radius=1.25 StartAngle=-9e-16 EndAngle=1.5708
    g2: ArcOfCircle CenterX=16.8 CenterY=14.2 CenterZ=0 NormalX=0 NormalY=0 NormalZ=1 AngleXU=0 Radius=1.75 StartAngle=4.71239 EndAngle=6.28319
    g3: ArcOfCircle CenterX=12.3 CenterY=14.2 CenterZ=0 NormalX=0 NormalY=0 NormalZ=1 AngleXU=0 Radius=1.75 StartAngle=3.14159 EndAngle=4.71239
    g4: LineSegment StartX=11.8 StartY=16.7 StartZ=0 EndX=17.3 EndY=16.7 EndZ=0
    g5: LineSegment StartX=18.55 StartY=15.45 StartZ=0 EndX=18.55 EndY=14.2 EndZ=0
    g6: LineSegment StartX=16.8 StartY=12.45 StartZ=0 EndX=12.3 EndY=12.45 EndZ=0
    g7: LineSegment StartX=10.55 StartY=14.2 StartZ=0 EndX=10.55 EndY=15.45 EndZ=0
  constraints (28):
    c: Coincident(g4,g0)
    c: Coincident(g4,g1)
    c: Horizontal(g4)
    c: Coincident(g5,g1)
    c: Coincident(g5,g2)
    c: Coincident(g6,g2)
    c: Coincident(g6,g3)
    c: Horizontal(g6)
    c: Coincident(g7,g3)
    c: Coincident(g7,g0)
    c: Vertical(g7)
    c: Radius(g0) = 1.25
    c: DistanceY(g0,g0) = 0
    c: Angle(g3) = 1.5708
    c: DistanceY(g3,g3) = 0
    c: DistanceY(g3,g0) = 1.25
    c: DistanceY(g3) = 14.2
    c: Radius(g3) = 1.75
    c: Radius(g2) = 1.75
    c: Radius(g1) = 1.25
    c: DistanceX(g6,g6) = 4.5
    c: DistanceX(g3) = 12.3
    c: DistanceY(g1,g1) = 0
    c: DistanceX(g2,g2) = 0
    c: Angle(g1) = 1.5708
    c: Angle(g2) = 1.5708
    c: Vertical(g5)
    c: DistanceX(g0,g0) = 0
FEATURE [Part::Extrusion] Extrude205  label="buttonCuts014"
  Base = -> Sketch208
  Dir = (0,-1,2e-16)
  DirMode = 2
  FaceMakerClass = Part::FaceMakerBullseye
  FaceMakerMode = 3
  LengthFwd = 0.6
  LengthRev = 0
  Placement = pos=(0,2,0) rot=(0,0,1;0rad)
  Solid = true
  Symmetric = false
FEATURE [Part::MultiFuse] Fusion199  label="bottomButtonCuts009"
  Shapes = -> [Extrude207,Extrude205]
FEATURE [Part::MultiFuse] Fusion200  label="bottomCuts007"
  Shapes = -> [Fusion201,Fusion199,Extrude203]
FEATURE [Part::Compound] Compound009  label="wearableCuts002"
  Links = -> [Fusion198,Fusion200]
  Placement = pos=(72,9.5,-78) rot=(1,0,0;1.5708rad)
FEATURE [Part::Feature] Part__Feature333  label="RaspberryPiZeroW001"
  Placement = pos=(36.5,18,19.18) rot=(1,0,0;1.5708rad)
  shape: bbox 65.9 x 31.25 x 4.8 mm, 368 faces, 2 solids (baked)
FEATURE [Part::Feature] pisugar3Board001003
  shape: bbox 65 x 30.4 x 6 mm, 19726 faces, 0 solids (baked)
FEATURE [Part::Compound] Compound014  label="PiDuo001"
  Links = -> [pisugar3Board001003,Part__Feature333]
  Placement = pos=(72,9.5,-78) rot=(1,0,0;1.5708rad)
FEATURE [Sketcher::SketchObject] Sketch213
  ArcFitTolerance = 0
  FullyConstrained = true
  MakeInternals = false
  Placement = pos=(148,0,0) rot=(0.57735,0.57735,0.57735;2.0944rad)
  sketch-geometry (14):
    g0: LineSegment StartX=-15 StartY=-82 StartZ=0 EndX=-4.75 EndY=-82 EndZ=0
    g1: LineSegment StartX=-4.75 StartY=-82 StartZ=0 EndX=-4.75 EndY=-79.15 EndZ=0
    g2: LineSegment StartX=-4.75 StartY=-79.15 StartZ=0 EndX=-5.05 EndY=-79.15 EndZ=0
    g3: LineSegment StartX=-5.05 StartY=-79.15 StartZ=0 EndX=-5.05 EndY=-78.25 EndZ=0
    g4: LineSegment StartX=-5.05 StartY=-78.25 StartZ=0 EndX=-4.75 EndY=-78.25 EndZ=0
    g5: LineSegment StartX=-4.75 StartY=-78.25 StartZ=0 EndX=-4.75 EndY=-75.65 EndZ=0
    g6: LineSegment StartX=-15 StartY=-82 StartZ=0 EndX=-15 EndY=-65.65 EndZ=0
    g7: LineSegment StartX=-15 StartY=-65.65 StartZ=0 EndX=-6.5 EndY=-65.65 EndZ=0
    g8: LineSegment StartX=-6.5 StartY=-65.65 StartZ=0 EndX=-6.5 EndY=-75.65 EndZ=0
    g9: LineSegment StartX=-6.5 StartY=-75.65 StartZ=0 EndX=-6 EndY=-75.65 EndZ=0
    g10: LineSegment StartX=-6 StartY=-75.65 StartZ=0 EndX=-6 EndY=-75.1 EndZ=0
    g11: LineSegment StartX=-6 StartY=-75.1 StartZ=0 EndX=-5 EndY=-75.1 EndZ=0
    g12: LineSegment StartX=-5 StartY=-75.1 StartZ=0 EndX=-5 EndY=-75.65 EndZ=0
    g13: LineSegment StartX=-5 StartY=-75.65 StartZ=0 EndX=-4.75 EndY=-75.65 EndZ=0
  constraints (42):
    c: Horizontal(g0)
    c: Coincident(g1,g0)
    c: Vertical(g1)
    c: Coincident(g2,g1)
    c: Vertical(g3)
    c: Vertical(g5)
    c: Horizontal(g2)
    c: Horizontal(g4)
    c: Coincident(g3,g4)
    c: Coincident(g2,g3)
    c: Coincident(g4,g5)
    c: DistanceX(g0) = -4.75
    c: DistanceX(g2,g2) = 0.3
    c: DistanceX(g1,g4) = 0
    c: DistanceY(g3,g3) = 0.9
    c: DistanceX(g6) = -15
    c: DistanceY(g5,g5) = 2.6
    c: DistanceY(g0) = -82
    c: DistanceY(g1,g1) = 2.85
    c: Vertical(g6)
    c: Coincident(g7,g6)
    c: Horizontal(g11)
    c: Coincident(g12,g11)
    c: Coincident(g13,g12)
    c: Coincident(g13,g5)
    c: Horizontal(g13)
    c: Horizontal(g7)
    c: Coincident(g7,g8)
    c: Vertical(g8)
    c: Coincident(g8,g9)
    c: Vertical(g10)
    c: Coincident(g10,g11)
    c: Horizontal(g9)
    c: Vertical(g12)
    c: Coincident(g9,g10)
    c: DistanceX(g13,g13) = 0.25
    c: DistanceX(g11,g11) = 1
    c: DistanceX(g9,g9) = 0.5
    c: DistanceY(g10,g10) = 0.55
    c: DistanceY(g8,g8) = 10
    c: Horizontal(g12,g9)
    c: Coincident(g0,g6)
FEATURE [Part::Extrusion] Extrude212  label="switchCut"
  Base = -> Sketch213
  Dir = (1,0,0)
  DirMode = 2
  FaceMakerClass = Part::FaceMakerBullseye
  FaceMakerMode = 3
  LengthFwd = 2.6
  LengthRev = 0
  Reversed = true
  Solid = true
  Symmetric = false
FEATURE [Part::Feature] Part__Feature324  label="CL-SA_s_C003"
  Placement = pos=(-0.8,0,-1e-15) rot=(0,0,1;0rad)
  shape: bbox 8.3 x 3.1 x 2.4 mm, 31 faces (baked)
FEATURE [Part::Feature] Part__Feature325  label="CL-SA_c_C003"
  Placement = pos=(0,-4.5,-1e-15) rot=(0,0,1;0rad)
  shape: bbox 10 x 10 x 2.54 mm, 56 faces (baked)
FEATURE [App::Part] CL_SA_12C_023  label="switch"
  Group = -> [Part__Feature324,Part__Feature325]
  Origin = -> Origin017
  Placement = pos=(146.73,-9.8,-80.2) rot=(0.57735,-0.57735,0.57735;4.18879rad)
FEATURE [Sketcher::SketchObject] Sketch214
  ArcFitTolerance = 0
  FullyConstrained = true
  MakeInternals = false
  Placement = pos=(148,0,0) rot=(0.57735,0.57735,0.57735;2.0944rad)
  sketch-geometry (4):
    g0: LineSegment StartX=-4 StartY=-76 StartZ=0 EndX=-15 EndY=-76 EndZ=0
    g1: LineSegment StartX=-15 StartY=-76 StartZ=0 EndX=-15 EndY=-69 EndZ=0
    g2: LineSegment StartX=-15 StartY=-69 StartZ=0 EndX=-4 EndY=-69 EndZ=0
    g3: LineSegment StartX=-4 StartY=-69 StartZ=0 EndX=-4 EndY=-76 EndZ=0
  constraints (12):
    c: Coincident(g0,g1)
    c: Coincident(g1,g2)
    c: Coincident(g2,g3)
    c: Coincident(g3,g0)
    c: Horizontal(g0)
    c: Horizontal(g2)
    c: Vertical(g1)
    c: Vertical(g3)
    c: DistanceX(g0) = -4
    c: DistanceY(g0) = -76
    c: DistanceX(g0,g0) = 11
    c: DistanceY(g0,g2) = 7
FEATURE [Part::Extrusion] Extrude213  label="baseIn"
  Base = -> Sketch214
  Dir = (1,0,0)
  DirMode = 2
  FaceMakerClass = Part::FaceMakerBullseye
  FaceMakerMode = 3
  LengthFwd = 5
  LengthRev = 0
  Reversed = true
  Solid = true
  Symmetric = false
FEATURE [Sketcher::SketchObject] Sketch194
  ArcFitTolerance = 0
  FullyConstrained = true
  MakeInternals = false
  MapMode = 2
  sketch-geometry (10):
    g0: LineSegment StartX=63 StartY=9.25 StartZ=0 EndX=72 EndY=9.25 EndZ=0
    g1: LineSegment StartX=72 StartY=9.25 StartZ=0 EndX=72 EndY=2 EndZ=0
    g2: LineSegment StartX=72 StartY=2 StartZ=0 EndX=63 EndY=2 EndZ=0
    g3: LineSegment StartX=63 StartY=2 StartZ=0 EndX=63 EndY=9.25 EndZ=0
    g4: LineSegment StartX=2 StartY=9.25 StartZ=0 EndX=10 EndY=9.25 EndZ=0
    g5: LineSegment StartX=10 StartY=9.25 StartZ=0 EndX=10 EndY=2 EndZ=0
    g6: LineSegment StartX=10 StartY=2 StartZ=0 EndX=2 EndY=2 EndZ=0
    g7: LineSegment StartX=2 StartY=2 StartZ=0 EndX=2 EndY=9.25 EndZ=0
    g8: Circle CenterX=7.47 CenterY=6.47 CenterZ=0 NormalX=0 NormalY=0 NormalZ=1 AngleXU=0 Radius=1.35
    g9: Circle CenterX=65.52 CenterY=6.47 CenterZ=0 NormalX=0 NormalY=0 NormalZ=1 AngleXU=0 Radius=1.35
  constraints (30):
    c: Coincident(g0,g1)
    c: Coincident(g1,g2)
    c: Coincident(g2,g3)
    c: Coincident(g3,g0)
    c: Horizontal(g0)
    c: Horizontal(g2)
    c: Vertical(g1)
    c: Vertical(g3)
    c: Coincident(g4,g5)
    c: Coincident(g5,g6)
    c: Coincident(g6,g7)
    c: Coincident(g7,g4)
    c: Horizontal(g4)
    c: Horizontal(g6)
    c: Vertical(g5)
    c: Vertical(g7)
    c: DistanceX(g6) = 2
    c: DistanceY(g6) = 2
    c: DistanceX(g6,g6) = 8
    c: DistanceY(g7,g7) = 7.25
    c: DistanceX(g-1,g1) = 72
    c: DistanceY(g2,g5) = 0
    c: DistanceY(g0,g4) = 0
    c: DistanceX(g2,g2) = 9
    c: DistanceX(g8) = 7.47
    c: Radius(g8) = 1.35
    c: DistanceX(g9) = 65.52
    c: DistanceY(g8,g9) = 0
    c: Radius(g9) = 1.35
    c: DistanceY(g8) = 6.47
FEATURE [Part::Extrusion] Extrude193  label="RaberryPiHold006"
  Base = -> Sketch194
  Dir = (0,0,1)
  DirMode = 2
  FaceMakerClass = Part::FaceMakerBullseye
  FaceMakerMode = 3
  LengthFwd = 2
  LengthRev = 0
  Placement = pos=(0,0,20.7) rot=(0,0,1;0rad)
  Solid = true
  Symmetric = false
FEATURE [Part::Fillet] Fillet054  label="piHoldBottomInDone006"
  Base = -> Extrude193
  EdgeLinks = -> Extrude193 [Edge1,Edge4,Edge12,Edge17,Edge19,Edge22]
  Edges = 6 edges: [Edge1 r=2,Edge4 r=1,Edge12 r=1,Edge17 r=2,Edge19 r=1,Edge22 r=1]
FEATURE [Part::Compound] Compound007  label="wearableHolds"
  Links = -> [Fillet054]
  Placement = pos=(72,9.5,-78) rot=(1,0,0;1.5708rad)
FEATURE [Sketcher::SketchObject] Sketch183
  ArcFitTolerance = 0
  FullyConstrained = true
  MakeInternals = false
  Placement = pos=(0,0,0) rot=(1,0,0;1.5708rad)
  sketch-geometry (46):
    g0: LineSegment StartX=11.75 StartY=19.5 StartZ=0 EndX=21.5 EndY=19.5 EndZ=0
    g1: LineSegment StartX=21.5 StartY=19.5 StartZ=0 EndX=23.75 EndY=22 EndZ=0
    g2: LineSegment StartX=23.75 StartY=22 StartZ=0 EndX=23.75 EndY=25 EndZ=0
    g3: LineSegment StartX=23.75 StartY=25 StartZ=0 EndX=9.5 EndY=25 EndZ=0
    g4: LineSegment StartX=9.5 StartY=25 StartZ=0 EndX=9.5 EndY=22 EndZ=0
    g5: LineSegment StartX=40 StartY=24.5 StartZ=0 EndX=40 EndY=22 EndZ=0
    g6: LineSegment StartX=40 StartY=22 StartZ=0 EndX=42.5 EndY=19.5 EndZ=0
    g7: LineSegment StartX=42.5 StartY=19.5 StartZ=0 EndX=48.7 EndY=19.5 EndZ=0
    g8: LineSegment StartX=48.7 StartY=19.5 StartZ=0 EndX=51.2 EndY=22 EndZ=0
    g9: LineSegment StartX=51.2 StartY=22 StartZ=0 EndX=51.2 EndY=24.5 EndZ=0
    g10: LineSegment StartX=51.2 StartY=24.5 StartZ=0 EndX=40 EndY=24.5 EndZ=0
    g11: LineSegment StartX=52.45 StartY=24.5 StartZ=0 EndX=52.45 EndY=22 EndZ=0
    g12: LineSegment StartX=52.45 StartY=22 StartZ=0 EndX=54.95 EndY=19.5 EndZ=0
    g13: LineSegment StartX=54.95 StartY=19.5 StartZ=0 EndX=61.15 EndY=19.5 EndZ=0
    g14: LineSegment StartX=61.15 StartY=19.5 StartZ=0 EndX=63.65 EndY=22 EndZ=0
    g15: LineSegment StartX=63.65 StartY=22 StartZ=0 EndX=63.65 EndY=24.5 EndZ=0
    g16: LineSegment StartX=63.65 StartY=24.5 StartZ=0 EndX=52.45 EndY=24.5 EndZ=0
    g17: LineSegment StartX=9.5 StartY=22 StartZ=0 EndX=11.75 EndY=19.5 EndZ=0
    g18: ArcOfCircle CenterX=12.3 CenterY=15.45 CenterZ=0 NormalX=0 NormalY=0 NormalZ=1 AngleXU=0 Radius=1 StartAngle=1.5708 EndAngle=3.14159
    g19: LineSegment StartX=11.3 StartY=15.45 StartZ=0 EndX=11.3 EndY=14.2 EndZ=0
    g20: LineSegment StartX=12.3 StartY=16.45 StartZ=0 EndX=16.8 EndY=16.45 EndZ=0
    g21: ArcOfCircle CenterX=16.8 CenterY=15.45 CenterZ=0 NormalX=0 NormalY=0 NormalZ=1 AngleXU=0 Radius=1 StartAngle=3e-16 EndAngle=1.5708
    g22: ArcOfCircle CenterX=16.8 CenterY=14.2 CenterZ=0 NormalX=0 NormalY=0 NormalZ=1 AngleXU=0 Radius=1 StartAngle=4.71239 EndAngle=6.28319
    g23: ArcOfCircle CenterX=12.3 CenterY=14.2 CenterZ=0 NormalX=0 NormalY=0 NormalZ=1 AngleXU=0 Radius=1 StartAngle=3.14159 EndAngle=4.71239
    g24: LineSegment StartX=12.3 StartY=13.2 StartZ=0 EndX=16.8 EndY=13.2 EndZ=0
    g25: LineSegment StartX=17.8 StartY=15.45 StartZ=0 EndX=17.8 EndY=14.2 EndZ=0
    g26: Circle CenterX=18.9 CenterY=16.475 CenterZ=0 NormalX=0 NormalY=0 NormalZ=1 AngleXU=0 Radius=0.5
    g27: Circle CenterX=21.09 CenterY=16.475 CenterZ=0 NormalX=0 NormalY=0 NormalZ=1 AngleXU=0 Radius=0.5
    g28: Circle CenterX=23.28 CenterY=16.475 CenterZ=0 NormalX=0 NormalY=0 NormalZ=1 AngleXU=0 Radius=0.5
    g29: Circle CenterX=25.47 CenterY=16.475 CenterZ=0 NormalX=0 NormalY=0 NormalZ=1 AngleXU=0 Radius=0.5
    g30: LineSegment StartX=44.8 StartY=16.45 StartZ=0 EndX=49.3 EndY=16.45 EndZ=0
    g31: LineSegment StartX=50.3 StartY=15.45 StartZ=0 EndX=50.3 EndY=14.2 EndZ=0
    g32: LineSegment StartX=49.3 StartY=13.2 StartZ=0 EndX=44.8 EndY=13.2 EndZ=0
    g33: LineSegment StartX=43.8 StartY=15.45 StartZ=0 EndX=43.8 EndY=14.2 EndZ=0
    g34: ArcOfCircle CenterX=44.8 CenterY=15.45 CenterZ=0 NormalX=0 NormalY=0 NormalZ=1 AngleXU=0 Radius=1 StartAngle=1.5708 EndAngle=3.14159
    g35: ArcOfCircle CenterX=49.3 CenterY=15.45 CenterZ=0 NormalX=0 NormalY=0 NormalZ=1 AngleXU=0 Radius=1 StartAngle=3e-16 EndAngle=1.5708
    g36: ArcOfCircle CenterX=49.3 CenterY=14.2 CenterZ=0 NormalX=0 NormalY=0 NormalZ=1 AngleXU=0 Radius=1 StartAngle=4.71239 EndAngle=6.28319
    g37: ArcOfCircle CenterX=44.8 CenterY=14.2 CenterZ=0 NormalX=0 NormalY=0 NormalZ=1 AngleXU=0 Radius=1 StartAngle=3.14159 EndAngle=4.71239
    g38: LineSegment StartX=52.25 StartY=15.58 StartZ=0 EndX=52.25 EndY=14.58 EndZ=0
    g39: LineSegment StartX=53.5 StartY=16.83 StartZ=0 EndX=60.5 EndY=16.83 EndZ=0
    g40: LineSegment StartX=53.5 StartY=13.33 StartZ=0 EndX=60.5 EndY=13.33 EndZ=0
    g41: LineSegment StartX=61.75 StartY=15.58 StartZ=0 EndX=61.75 EndY=14.58 EndZ=0
    g42: ArcOfCircle CenterX=53.5 CenterY=15.58 CenterZ=0 NormalX=0 NormalY=0 NormalZ=1 AngleXU=0 Radius=1.25 StartAngle=1.5708 EndAngle=3.14159
    g43: ArcOfCircle CenterX=60.5 CenterY=15.58 CenterZ=0 NormalX=0 NormalY=0 NormalZ=1 AngleXU=0 Radius=1.25 StartAngle=2e-16 EndAngle=1.5708
    g44: ArcOfCircle CenterX=60.5 CenterY=14.58 CenterZ=0 NormalX=0 NormalY=0 NormalZ=1 AngleXU=0 Radius=1.25 StartAngle=4.7124 EndAngle=6.28319
    g45: ArcOfCircle CenterX=53.5 CenterY=14.58 CenterZ=0 NormalX=0 NormalY=0 NormalZ=1 AngleXU=0 Radius=1.25 StartAngle=3.14159 EndAngle=4.71239
  constraints (150):
    c: Horizontal(g0)
    c: Coincident(g0,g1)
    c: Coincident(g1,g2)
    c: Coincident(g2,g3)
    c: Horizontal(g3)
    c: Coincident(g3,g4)
    c: Vertical(g4)
    c: Coincident(g5,g6)
    c: Coincident(g6,g7)
    c: Horizontal(g7)
    c: Coincident(g7,g8)
    c: Coincident(g8,g9)
    c: Vertical(g9)
    c: Coincident(g9,g10)
    c: Coincident(g10,g5)
    c: Coincident(g11,g12)
    c: Coincident(g12,g13)
    c: Horizontal(g13)
    c: Coincident(g13,g14)
    c: Coincident(g14,g15)
    c: Vertical(g15)
    c: Coincident(g15,g16)
    c: Coincident(g16,g11)
    c: Horizontal(g16)
    c: Coincident(g17,g4)
    c: Coincident(g0,g17)
    c: DistanceX(g3) = 9.5
    c: DistanceX(g3,g3) = 14.25
    c: Vertical(g2)
    c: DistanceY(g3) = 25
    c: DistanceY(g4) = 22
    c: DistanceY(g4,g1) = 0
    c: DistanceX(g4,g0) = 2.25
    c: DistanceX(g0,g1) = 2.25
    c: Horizontal(g10)
    c: Vertical(g5)
    c: Vertical(g11)
    c: DistanceX(g5) = 40
    c: DistanceX(g5,g9) = 11.2
    c: DistanceY(g11,g9) = 0
    c: DistanceY(g5,g5) = 2.5
    c: DistanceY(g8,g5) = 0
    c: DistanceY(g11,g8) = 0
    c: DistanceY(g14,g11) = 0
    c: DistanceY(g6,g5) = 2.5
    c: DistanceX(g5,g6) = 2.5
    c: DistanceX(g7,g8) = 2.5
    c: DistanceX(g9,g11) = 1.25
    c: DistanceY(g12,g7) = 0
    c: DistanceX(g11,g12) = 2.5
    c: DistanceX(g13,g14) = 2.5
    c: DistanceX(g11,g15) = 11.2
    c: DistanceY(g0,g4) = 2.5
    c: DistanceY(g5) = 24.5
    c: Coincident(g19,g18)
    c: Vertical(g19)
    c: Horizontal(g20)
    c: Coincident(g21,g20)
    c: Coincident(g23,g19)
    c: Coincident(g24,g23)
    c: Coincident(g24,g22)
    c: Horizontal(g24)
    c: Coincident(g25,g21)
    c: Coincident(g25,g22)
    c: Vertical(g25)
    c: Coincident(g18,g20)
    c: Radius(g18) = 1
    c: Angle(g18) = 1.5708
    c: Angle(g21) = 1.5708
    c: Angle(g22) = 1.5708
    c: Angle(g23) = 1.5708
    c: DistanceX(g23) = 12.3
    c: DistanceY(g23) = 13.2
    c: DistanceX(g19) = 11.3
    c: DistanceY(g23,g19) = 0
    c: DistanceY(g18,g18) = 0
    c: DistanceX(g21,g20) = 0
    c: Radius(g21) = 1
    c: Radius(g22) = 1
    c: DistanceX(g22,g22) = 0
    c: DistanceX(g18,g20) = 4.5
    c: DistanceX(g26) = 18.9
    c: Radius(g26) = 0.5
    c: DistanceY(g26) = 16.475
    c: DistanceX(g26,g27) = 2.19
    c: DistanceY(g26,g27) = 0
    c: DistanceY(g28,g27) = 0
    c: DistanceY(g29,g28) = 0
    c: DistanceX(g27,g28) = 2.19
    c: Radius(g27) = 0.5
    c: Radius(g28) = 0.5
    c: Radius(g29) = 0.5
    c: DistanceX(g28,g29) = 2.19
    c: DistanceY(g23,g18) = 1.25
    c: Horizontal(g30)
    c: Vertical(g31)
    c: Vertical(g33)
    c: Coincident(g33,g34)
    c: Coincident(g33,g37)
    c: Coincident(g32,g37)
    c: Coincident(g32,g36)
    c: Coincident(g31,g36)
    c: Coincident(g31,g35)
    c: Coincident(g30,g35)
    c: Coincident(g30,g34)
    c: Angle(g34) = 1.5708
    c: Angle(g35) = 1.5708
    c: Angle(g37) = 1.5708
    c: Angle(g36) = 1.5708
    c: DistanceY(g18,g34) = 0
    c: DistanceY(g34,g33) = 0
    c: Radius(g34) = 1
    c: DistanceY(g33,g37) = 0
    c: Radius(g37) = 1
    c: Radius(g36) = 1
    c: Radius(g35) = 1
    c: DistanceY(g33,g23) = 0
    c: DistanceY(g31,g36) = 0
    c: Horizontal(g32)
    c: DistanceX(g35,g30) = 0
    c: DistanceX(g32,g32) = 4.5
    c: Vertical(g38)
    c: Horizontal(g39)
    c: Horizontal(g40)
    c: Vertical(g41)
    c: Coincident(g42,g38)
    c: Coincident(g42,g39)
    c: Coincident(g43,g39)
    c: Coincident(g45,g38)
    c: Coincident(g45,g40)
    c: Coincident(g40,g44)
    c: Coincident(g41,g44)
    c: Coincident(g41,g43)
    c: DistanceX(g42) = 53.5
    c: DistanceY(g42) = 15.58
    c: DistanceX(g42,g45) = 0
    c: DistanceY(g45,g42) = 1
    c: Radius(g42) = 1.25
    c: Radius(g44) = 1.25
    c: Radius(g43) = 1.25
    c: DistanceX(g45,g40) = 0
    c: DistanceX(g42,g39) = 0
    c: DistanceY(g42,g43) = 0
    c: DistanceY(g44,g45) = 0
    c: DistanceY(g45,g38) = 0
    c: DistanceX(g42,g43) = 7
    c: DistanceX(g18,g34) = 32.5
    c: DistanceY(g41,g44) = 0
    c: DistanceY(g43,g41) = 0
    c: Angle(g42) = 1.5708
FEATURE [Part::Extrusion] Extrude181  label="lightBottomCutDone005"
  Base = -> Sketch183
  Dir = (0,-1,2e-16)
  DirMode = 2
  FaceMakerClass = Part::FaceMakerBullseye
  FaceMakerMode = 3
  LengthFwd = 5
  LengthRev = 0
  Placement = pos=(0,2,0) rot=(0,0,1;0rad)
  Solid = true
  Symmetric = false
FEATURE [Sketcher::SketchObject] Sketch185
  ArcFitTolerance = 0
  FullyConstrained = true
  MakeInternals = false
  Placement = pos=(0,0,0) rot=(1,0,0;1.5708rad)
  sketch-geometry (8):
    g0: ArcOfCircle CenterX=11.8 CenterY=15.45 CenterZ=0 NormalX=0 NormalY=0 NormalZ=1 AngleXU=0 Radius=1.25 StartAngle=1.5708 EndAngle=3.14159
    g1: ArcOfCircle CenterX=17.3 CenterY=15.45 CenterZ=0 NormalX=0 NormalY=0 NormalZ=1 AngleXU=0 Radius=1.25 StartAngle=-9e-16 EndAngle=1.5708
    g2: ArcOfCircle CenterX=16.8 CenterY=14.2 CenterZ=0 NormalX=0 NormalY=0 NormalZ=1 AngleXU=0 Radius=1.75 StartAngle=4.71239 EndAngle=6.28319
    g3: ArcOfCircle CenterX=12.3 CenterY=14.2 CenterZ=0 NormalX=0 NormalY=0 NormalZ=1 AngleXU=0 Radius=1.75 StartAngle=3.14159 EndAngle=4.71239
    g4: LineSegment StartX=11.8 StartY=16.7 StartZ=0 EndX=17.3 EndY=16.7 EndZ=0
    g5: LineSegment StartX=18.55 StartY=15.45 StartZ=0 EndX=18.55 EndY=14.2 EndZ=0
    g6: LineSegment StartX=16.8 StartY=12.45 StartZ=0 EndX=12.3 EndY=12.45 EndZ=0
    g7: LineSegment StartX=10.55 StartY=14.2 StartZ=0 EndX=10.55 EndY=15.45 EndZ=0
  constraints (28):
    c: Coincident(g4,g0)
    c: Coincident(g4,g1)
    c: Horizontal(g4)
    c: Coincident(g5,g1)
    c: Coincident(g5,g2)
    c: Coincident(g6,g2)
    c: Coincident(g6,g3)
    c: Horizontal(g6)
    c: Coincident(g7,g3)
    c: Coincident(g7,g0)
    c: Vertical(g7)
    c: Radius(g0) = 1.25
    c: DistanceY(g0,g0) = 0
    c: Angle(g3) = 1.5708
    c: DistanceY(g3,g3) = 0
    c: DistanceY(g3,g0) = 1.25
    c: DistanceY(g3) = 14.2
    c: Radius(g3) = 1.75
    c: Radius(g2) = 1.75
    c: Radius(g1) = 1.25
    c: DistanceX(g6,g6) = 4.5
    c: DistanceX(g3) = 12.3
    c: DistanceY(g1,g1) = 0
    c: DistanceX(g2,g2) = 0
    c: Angle(g1) = 1.5708
    c: Angle(g2) = 1.5708
    c: Vertical(g5)
    c: DistanceX(g0,g0) = 0
FEATURE [Part::Extrusion] Extrude186  label="buttonCuts011"
  Base = -> Sketch185
  Dir = (0,-1,2e-16)
  DirMode = 2
  FaceMakerClass = Part::FaceMakerBullseye
  FaceMakerMode = 3
  LengthFwd = 0.6
  LengthRev = 0
  Placement = pos=(32.5,2,0) rot=(0,0,1;0rad)
  Solid = true
  Symmetric = false
FEATURE [Sketcher::SketchObject] Sketch187
  ArcFitTolerance = 0
  FullyConstrained = true
  MakeInternals = false
  Placement = pos=(0,0,0) rot=(0.57735,0.57735,0.57735;2.0944rad)
  sketch-geometry (4):
    g0: LineSegment StartX=8 StartY=23 StartZ=0 EndX=26 EndY=23 EndZ=0
    g1: LineSegment StartX=26 StartY=23 StartZ=0 EndX=26 EndY=20 EndZ=0
    g2: LineSegment StartX=26 StartY=20 StartZ=0 EndX=8 EndY=20 EndZ=0
    g3: LineSegment StartX=8 StartY=20 StartZ=0 EndX=8 EndY=23 EndZ=0
  constraints (12):
    c: Coincident(g0,g1)
    c: Coincident(g1,g2)
    c: Coincident(g2,g3)
    c: Coincident(g3,g0)
    c: Horizontal(g0)
    c: Horizontal(g2)
    c: Vertical(g1)
    c: Vertical(g3)
    c: DistanceX(g2) = 8
    c: DistanceX(g2,g0) = 18
    c: DistanceY(g2) = 20
    c: DistanceY(g2,g0) = 3
FEATURE [Part::Extrusion] Extrude184  label="leftInCut005"
  Base = -> Sketch187
  Dir = (1,0,0)
  DirMode = 2
  FaceMakerClass = Part::FaceMakerBullseye
  FaceMakerMode = 3
  LengthFwd = 10
  LengthRev = 0
  Placement = pos=(72,1,0) rot=(0,0,1;0rad)
  Solid = true
  Symmetric = false
FEATURE [Sketcher::SketchObject] Sketch184
  ArcFitTolerance = 0
  AttachmentSupport = -> [Extrude184]
  FullyConstrained = true
  MakeInternals = false
  MapMode = 4
  Placement = pos=(72,1,0) rot=(0.57735,0.57735,0.57735;2.0944rad)
  sketch-geometry (4):
    g0: LineSegment StartX=26 StartY=19.9 StartZ=0 EndX=12 EndY=19.9 EndZ=0
    g1: LineSegment StartX=12 StartY=19.9 StartZ=0 EndX=12 EndY=22.9 EndZ=0
    g2: LineSegment StartX=12 StartY=22.9 StartZ=0 EndX=26 EndY=22.9 EndZ=0
    g3: LineSegment StartX=26 StartY=22.9 StartZ=0 EndX=26 EndY=19.9 EndZ=0
  constraints (12):
    c: Coincident(g0,g1)
    c: Coincident(g1,g2)
    c: Coincident(g2,g3)
    c: Coincident(g3,g0)
    c: Horizontal(g0)
    c: Horizontal(g2)
    c: Vertical(g1)
    c: Vertical(g3)
    c: DistanceX(g0,g0) = 14
    c: DistanceX(g1) = 12
    c: DistanceY(g1) = 22.9
    c: DistanceY(g1,g1) = 3
FEATURE [Part::Extrusion] Extrude182  label="sdCut005"
  Base = -> Sketch184
  Dir = (1,0,0)
  DirMode = 2
  FaceMakerClass = Part::FaceMakerBullseye
  FaceMakerMode = 3
  LengthFwd = 5
  LengthRev = 0
  Placement = pos=(-70,0,0) rot=(0,0,1;0rad)
  Reversed = true
  Solid = true
  Symmetric = false
FEATURE [Part::MultiFuse] Fusion192  label="bottomCutsHorDone005"
  Shapes = -> [Extrude182,Extrude184]
FEATURE [Sketcher::SketchObject] Sketch188
  ArcFitTolerance = 0
  FullyConstrained = true
  MakeInternals = false
  Placement = pos=(0,0,0) rot=(1,0,0;1.5708rad)
  sketch-geometry (8):
    g0: ArcOfCircle CenterX=11.8 CenterY=15.45 CenterZ=0 NormalX=0 NormalY=0 NormalZ=1 AngleXU=0 Radius=1.25 StartAngle=1.5708 EndAngle=3.14159
    g1: ArcOfCircle CenterX=17.3 CenterY=15.45 CenterZ=0 NormalX=0 NormalY=0 NormalZ=1 AngleXU=0 Radius=1.25 StartAngle=-9e-16 EndAngle=1.5708
    g2: ArcOfCircle CenterX=16.8 CenterY=14.2 CenterZ=0 NormalX=0 NormalY=0 NormalZ=1 AngleXU=0 Radius=1.75 StartAngle=4.71239 EndAngle=6.28319
    g3: ArcOfCircle CenterX=12.3 CenterY=14.2 CenterZ=0 NormalX=0 NormalY=0 NormalZ=1 AngleXU=0 Radius=1.75 StartAngle=3.14159 EndAngle=4.71239
    g4: LineSegment StartX=11.8 StartY=16.7 StartZ=0 EndX=17.3 EndY=16.7 EndZ=0
    g5: LineSegment StartX=18.55 StartY=15.45 StartZ=0 EndX=18.55 EndY=14.2 EndZ=0
    g6: LineSegment StartX=16.8 StartY=12.45 StartZ=0 EndX=12.3 EndY=12.45 EndZ=0
    g7: LineSegment StartX=10.55 StartY=14.2 StartZ=0 EndX=10.55 EndY=15.45 EndZ=0
  constraints (28):
    c: Coincident(g4,g0)
    c: Coincident(g4,g1)
    c: Horizontal(g4)
    c: Coincident(g5,g1)
    c: Coincident(g5,g2)
    c: Coincident(g6,g2)
    c: Coincident(g6,g3)
    c: Horizontal(g6)
    c: Coincident(g7,g3)
    c: Coincident(g7,g0)
    c: Vertical(g7)
    c: Radius(g0) = 1.25
    c: DistanceY(g0,g0) = 0
    c: Angle(g3) = 1.5708
    c: DistanceY(g3,g3) = 0
    c: DistanceY(g3,g0) = 1.25
    c: DistanceY(g3) = 14.2
    c: Radius(g3) = 1.75
    c: Radius(g2) = 1.75
    c: Radius(g1) = 1.25
    c: DistanceX(g6,g6) = 4.5
    c: DistanceX(g3) = 12.3
    c: DistanceY(g1,g1) = 0
    c: DistanceX(g2,g2) = 0
    c: Angle(g1) = 1.5708
    c: Angle(g2) = 1.5708
    c: Vertical(g5)
    c: DistanceX(g0,g0) = 0
FEATURE [Part::Extrusion] Extrude183  label="buttonCuts010"
  Base = -> Sketch188
  Dir = (0,-1,2e-16)
  DirMode = 2
  FaceMakerClass = Part::FaceMakerBullseye
  FaceMakerMode = 3
  LengthFwd = 0.6
  LengthRev = 0
  Placement = pos=(0,2,0) rot=(0,0,1;0rad)
  Solid = true
  Symmetric = false
FEATURE [Part::MultiFuse] Fusion190  label="bottomButtonCuts007"
  Shapes = -> [Extrude186,Extrude183]
FEATURE [Part::MultiFuse] Fusion191  label="bottomCuts005"
  Shapes = -> [Fusion192,Fusion190,Extrude181]
FEATURE [Part::Compound] Compound006  label="wearableCuts"
  Links = -> [Fusion191]
  Placement = pos=(72,9.5,-78) rot=(1,0,0;1.5708rad)
FEATURE [Sketcher::SketchObject] Sketch209
  ArcFitTolerance = 0
  FullyConstrained = true
  MakeInternals = false
  Placement = pos=(0,0,-77.25) rot=(0,0,1;0rad)
  sketch-geometry (6):
    g0: ArcOfCircle CenterX=125.5 CenterY=-4.58 CenterZ=0 NormalX=0 NormalY=0 NormalZ=1 AngleXU=0 Radius=2.4 StartAngle=1.5708 EndAngle=3.14159
    g1: ArcOfCircle CenterX=132.5 CenterY=-4.58 CenterZ=0 NormalX=0 NormalY=0 NormalZ=1 AngleXU=0 Radius=2.4 StartAngle=0 EndAngle=1.5708
    g2: LineSegment StartX=125.5 StartY=-2.18 StartZ=0 EndX=132.5 EndY=-2.18 EndZ=0
    g3: LineSegment StartX=134.9 StartY=-4.58 StartZ=0 EndX=134.9 EndY=-8.75 EndZ=0
    g4: LineSegment StartX=134.9 StartY=-8.75 StartZ=0 EndX=123.1 EndY=-8.75 EndZ=0
    g5: LineSegment StartX=123.1 StartY=-8.75 StartZ=0 EndX=123.1 EndY=-4.58 EndZ=0
  constraints (20):
    c: Vertical(g1,g1)
    c: Horizontal(g1,g0)
    c: Horizontal(g0,g0)
    c: DistanceX(g1) = 132.5
    c: Vertical(g1,g3)
    c: Horizontal(g1,g0)
    c: Coincident(g2,g0)
    c: Coincident(g2,g1)
    c: Coincident(g3,g1)
    c: Coincident(g5,g0)
    c: DistanceY(g0) = -4.58
    c: Horizontal(g4)
    c: DistanceY(g4) = -8.75
    c: Vertical(g5)
    c: DistanceX(g5) = 123.1
    c: Horizontal(g0,g1)
    c: Coincident(g4,g5)
    c: Diameter(g1) = 4.8
    c: Angle(g0) = 1.5708
    c: Coincident(g3,g4)
FEATURE [Part::Extrusion] Extrude208  label="usbCCut"
  Base = -> Sketch209
  Dir = (0,0,1)
  DirMode = 2
  FaceMakerClass = Part::FaceMakerBullseye
  FaceMakerMode = 3
  LengthFwd = 10
  LengthRev = 0
  Reversed = true
  Solid = true
  Symmetric = false
FEATURE [Sketcher::SketchObject] Sketch210
  ArcFitTolerance = 0
  FullyConstrained = true
  MakeInternals = false
  Placement = pos=(0,0,-78) rot=(0,0,1;0rad)
  sketch-geometry (8):
    g0: ArcOfCircle CenterX=81 CenterY=-12 CenterZ=0 NormalX=0 NormalY=0 NormalZ=1 AngleXU=0 Radius=3.25 StartAngle=1.5708 EndAngle=3.14159
    g1: ArcOfCircle CenterX=81 CenterY=-14 CenterZ=0 NormalX=0 NormalY=0 NormalZ=1 AngleXU=0 Radius=3.25 StartAngle=3.14159 EndAngle=4.71239
    g2: ArcOfCircle CenterX=135 CenterY=-14 CenterZ=0 NormalX=0 NormalY=0 NormalZ=1 AngleXU=0 Radius=3.25 StartAngle=4.71239 EndAngle=6.28319
    g3: ArcOfCircle CenterX=135 CenterY=-12 CenterZ=0 NormalX=0 NormalY=0 NormalZ=1 AngleXU=0 Radius=3.25 StartAngle=0 EndAngle=1.5708
    g4: LineSegment StartX=81 StartY=-17.25 StartZ=0 EndX=135 EndY=-17.25 EndZ=0
    g5: LineSegment StartX=138.25 StartY=-14 StartZ=0 EndX=138.25 EndY=-12 EndZ=0
    g6: LineSegment StartX=135 StartY=-8.75 StartZ=0 EndX=81 EndY=-8.75 EndZ=0
    g7: LineSegment StartX=77.75 StartY=-12 StartZ=0 EndX=77.75 EndY=-14 EndZ=0
  constraints (30):
    c: Horizontal(g3,g0)
    c: Vertical(g1,g0)
    c: Vertical(g3,g2)
    c: Vertical(g2,g2)
    c: Vertical(g2,g3)
    c: Vertical(g1,g1)
    c: Vertical(g0,g0)
    c: Horizontal(g0,g0)
    c: Horizontal(g3,g3)
    c: Horizontal(g1,g1)
    c: DistanceY(g3) = -8.75
    c: Vertical(g0,g1)
    c: Horizontal(g3,g0)
    c: Vertical(g2,g3)
    c: Horizontal(g2,g2)
    c: Horizontal(g2,g1)
    c: DistanceX(g2) = 135
    c: DistanceY(g2) = -14
    c: DistanceY(g2,g3) = 2
    c: DistanceX(g0,g3) = 54
    c: Coincident(g4,g1)
    c: Coincident(g4,g2)
    c: Coincident(g5,g2)
    c: Coincident(g5,g3)
    c: Coincident(g6,g3)
    c: Coincident(g6,g0)
    c: Horizontal(g6)
    c: Tangent(g6,g0)
    c: Coincident(g7,g0)
    c: Coincident(g7,g1)
FEATURE [Part::Extrusion] Extrude209  label="microUSBCut"
  Base = -> Sketch210
  Dir = (0,0,1)
  DirMode = 2
  FaceMakerClass = Part::FaceMakerBullseye
  FaceMakerMode = 3
  LengthFwd = 10
  LengthRev = 0
  Reversed = true
  Solid = true
  Symmetric = false
FEATURE [Part::MultiFuse] Fusion202  label="wireCuts"
  Shapes = -> [Extrude208,Extrude209]
FEATURE [App::Part] Part  label="piZeroParts"
  Group = -> [Extrude014,Extrude015,Sketch014,Sketch015,Fusion018,Extrude229,Extrude230,Sketch231,Sketch232,Fusion223,Sketch227,Extrude226,Extrude201,Extrude202,Extrude203,Extrude204,Extrude205,Extrude206,Extrude207,Fusion198,Fusion199,Fusion200,Fusion201,Sketch202,Sketch203,Sketch204,Sketch205,Sketch206,Sketch207,Sketch208,Compound009,Part__Feature333,pisugar3Board001003,Compound014,Sketch213,Extrude212,+26 more]
  Origin = -> Origin021
  Placement = pos=(94,-4,0) rot=(0,0,1;0rad)
FEATURE [Part::FeaturePython] Clone088  label="m3x20sNT003"  # WARN: FeaturePython — macro-defined, semantics opaque (R4)
  AttacherType = Attacher::AttachEngine3D
  Fuse = false
  Placement = pos=(170,-8,73) rot=(0,-1,0;1.5708rad)
  Scale = (1.1,1.1,1.1)
FEATURE [Part::FeaturePython] Clone089  label="m3x20sNT004"  # WARN: FeaturePython — macro-defined, semantics opaque (R4)
  AttacherType = Attacher::AttachEngine3D
  Fuse = false
  Placement = pos=(235,-8,73) rot=(0.707107,0,0.707107;3.14159rad)
  Scale = (1.1,1.1,1.1)
FEATURE [Part::MultiFuse] Fusion329  label="srsCuts005"
  Shapes = -> [Clone089,Clone088]
FEATURE [Part::FeaturePython] Clone090  label="m3x20sNT005"  # WARN: FeaturePython — macro-defined, semantics opaque (R4)
  AttacherType = Attacher::AttachEngine3D
  Fuse = false
  Placement = pos=(170,-8,73) rot=(0,-1,0;1.5708rad)
  Scale = (1.1,1.1,1.1)
FEATURE [Part::FeaturePython] Clone091  label="m3x20sNT006"  # WARN: FeaturePython — macro-defined, semantics opaque (R4)
  AttacherType = Attacher::AttachEngine3D
  Fuse = false
  Placement = pos=(235,-8,73) rot=(0.707107,0,0.707107;3.14159rad)
  Scale = (1.1,1.1,1.1)
FEATURE [Part::MultiFuse] Fusion330  label="srsCuts006"
  Placement = pos=(0,0,-90) rot=(0,0,1;0rad)
  Shapes = -> [Clone091,Clone090]
FEATURE [Part::MultiFuse] Fusion331
  Shapes = -> [Fusion329,Fusion330]
FEATURE [Part::Cut] Cut030  label="srs021"
  Base = -> Cut
  Tool = -> Fusion331
FEATURE [Part::Cylinder] Cylinder
  Angle = 360
  AttacherType = Attacher::AttachEngine3D
  FirstAngle = 0
  Height = 2
  Placement = pos=(158.5,-8,73) rot=(0.707107,0,0.707107;3.14159rad)
  Radius = 1.6
  SecondAngle = 0
FEATURE [Part::Cylinder] Cylinder051
  Angle = 360
  AttacherType = Attacher::AttachEngine3D
  FirstAngle = 0
  Height = 2
  Placement = pos=(246.5,-8,73) rot=(-0.707107,0,0.707107;3.14159rad)
  Radius = 1.6
  SecondAngle = 0
FEATURE [Part::MultiFuse] Fusion332
  Shapes = -> [Cylinder,Cylinder051]
FEATURE [Part::Cylinder] Cylinder052
  Angle = 360
  AttacherType = Attacher::AttachEngine3D
  FirstAngle = 0
  Height = 2
  Placement = pos=(158.5,-8,73) rot=(0.707107,0,0.707107;3.14159rad)
  Radius = 1.6
  SecondAngle = 0
FEATURE [Part::Cylinder] Cylinder053
  Angle = 360
  AttacherType = Attacher::AttachEngine3D
  FirstAngle = 0
  Height = 2
  Placement = pos=(246.5,-8,73) rot=(0.707107,0,-0.707107;3.14159rad)
  Radius = 1.6
  SecondAngle = 0
FEATURE [Part::MultiFuse] Fusion333
  Placement = pos=(0,0,-90) rot=(0,0,1;0rad)
  Shapes = -> [Cylinder052,Cylinder053]
FEATURE [Part::MultiFuse] Fusion334
  Shapes = -> [Fusion332,Fusion333]
FEATURE [Part::Cut] Cut031  label="srs022"
  Base = -> Cut030
  Tool = -> Fusion334
FEATURE [Part::FeaturePython] Clone092  label="M3Nut054"  # WARN: FeaturePython — macro-defined, semantics opaque (R4)
  AttacherType = Attacher::AttachEngine3D
  Fuse = false
  Placement = pos=(0,0,4.5) rot=(0,0,1;0rad)
  Scale = (1.1,1.1,5)
FEATURE [Part::FeaturePython] Clone093  label="M3Nut055"  # WARN: FeaturePython — macro-defined, semantics opaque (R4)
  AttacherType = Attacher::AttachEngine3D
  Fuse = false
  Placement = pos=(0,0,0.9) rot=(0,0,1;0rad)
  Scale = (1.1,1.1,1)
FEATURE [Part::FeaturePython] Clone094  label="M3Nut056"  # WARN: FeaturePython — macro-defined, semantics opaque (R4)
  AttacherType = Attacher::AttachEngine3D
  Fuse = false
  Placement = pos=(0,0,4.5) rot=(0,0,1;0rad)
  Scale = (1.1,1.1,5)
FEATURE [Part::FeaturePython] Clone095  label="M3Nut057"  # WARN: FeaturePython — macro-defined, semantics opaque (R4)
  AttacherType = Attacher::AttachEngine3D
  Fuse = false
  Placement = pos=(0,0,0.9) rot=(0,0,1;0rad)
  Scale = (1.1,1.1,1)
FEATURE [Part::Cylinder] Cylinder054
  Angle = 360
  AttacherType = Attacher::AttachEngine3D
  FirstAngle = 0
  Height = 5
  Radius = 2
  SecondAngle = 0
FEATURE [Part::Cylinder] Cylinder055
  Angle = 360
  AttacherType = Attacher::AttachEngine3D
  FirstAngle = 0
  Height = 5
  Radius = 4
  SecondAngle = 0
FEATURE [Part::Cylinder] Cylinder056
  Angle = 360
  AttacherType = Attacher::AttachEngine3D
  FirstAngle = 0
  Height = 5
  Radius = 2
  SecondAngle = 0
FEATURE [Part::Cylinder] Cylinder057
  Angle = 360
  AttacherType = Attacher::AttachEngine3D
  FirstAngle = 0
  Height = 5
  Radius = 4
  SecondAngle = 0
FEATURE [Part::MultiFuse] Fusion335
  Shapes = -> [Clone092,Cylinder054]
FEATURE [Part::MultiFuse] Fusion336
  Shapes = -> [Fusion335,Clone093]
FEATURE [Part::MultiCommon] Common005  label="m3NutCut5mm005"
  Placement = pos=(163,13,63) rot=(1,0,0;1.5708rad)
  Shapes = -> [Cylinder055,Fusion336]
FEATURE [Part::MultiFuse] Fusion337
  Shapes = -> [Clone094,Cylinder056]
FEATURE [Part::MultiFuse] Fusion338
  Shapes = -> [Fusion337,Clone095]
FEATURE [Part::MultiCommon] Common006  label="m3NutCut5mm006"
  Placement = pos=(242,13,63) rot=(1,0,0;1.5708rad)
  Shapes = -> [Cylinder057,Fusion338]
FEATURE [Part::MultiFuse] Fusion339  label="m3Cuts002"
  Placement = pos=(0,0,-126) rot=(0,0,1;0rad)
  Shapes = -> [Common006,Common005]
FEATURE [Part::Cut] Cut032  label="batteryHousing003"
  Base = -> Cut022
  Tool = -> Fusion339
FEATURE [Sketcher::SketchObject] Sketch306
  ArcFitTolerance = 0
  FullyConstrained = true
  MakeInternals = false
  Placement = pos=(0,0,-77) rot=(0,0,1;0rad)
  sketch-geometry (8):
    g0: LineSegment StartX=158.5 StartY=-25 StartZ=0 EndX=168.5 EndY=-25 EndZ=0
    g1: LineSegment StartX=158.5 StartY=-25 StartZ=0 EndX=158.5 EndY=-32 EndZ=0
    g2: LineSegment StartX=168.5 StartY=-25 StartZ=0 EndX=168.5 EndY=-50.215 EndZ=0
    g3: ArcOfCircle CenterX=181 CenterY=-31.5 CenterZ=0 NormalX=0 NormalY=0 NormalZ=1 AngleXU=0 Radius=22.5056 StartAngle=3.16381 EndAngle=4.12352
    g4: LineSegment StartX=246.5 StartY=-25 StartZ=0 EndX=236.5 EndY=-25 EndZ=0
    g5: LineSegment StartX=236.5 StartY=-25 StartZ=0 EndX=236.5 EndY=-50.215 EndZ=0
    g6: LineSegment StartX=246.5 StartY=-25 StartZ=0 EndX=246.5 EndY=-31.5 EndZ=0
    g7: ArcOfCircle CenterX=223.988 CenterY=-31.5 CenterZ=0 NormalX=0 NormalY=0 NormalZ=1 AngleXU=0 Radius=22.5125 StartAngle=5.30172 EndAngle=6.28319
  constraints (26):
    c: Horizontal(g0)
    c: Coincident(g1,g0)
    c: Vertical(g1)
    c: Coincident(g2,g0)
    c: Vertical(g2)
    c: DistanceX(g0) = 158.5
    c: DistanceX(g0,g0) = 10
    c: Coincident(g3,g2)
    c: Coincident(g3,g1)
    c: DistanceY(g1,g1) = 7
    c: DistanceY(g0) = -25
    c: DistanceY(g3,g0) = 6.5
    c: DistanceX(g1,g3) = 22.5
    c: Horizontal(g4)
    c: Coincident(g5,g4)
    c: Vertical(g5)
    c: DistanceX(g4) = 246.5
    c: DistanceX(g4,g4) = 10
    c: DistanceY(g2,g5) = 0
    c: Horizontal(g4,g0)
    c: Coincident(g6,g4)
    c: Vertical(g6)
    c: DistanceY(g6,g3) = 0
    c: Coincident(g7,g6)
    c: Coincident(g7,g5)
    c: DistanceY(g7,g3) = 0
FEATURE [Part::Extrusion] Extrude302
  Base = -> Sketch306
  Dir = (0,0,1)
  DirMode = 2
  FaceMakerClass = Part::FaceMakerBullseye
  FaceMakerMode = 3
  LengthFwd = 27.5
  LengthRev = 0
  Solid = true
  Symmetric = false
FEATURE [Part::MultiFuse] Fusion341  label="piCover005"
  Shapes = -> [Extrude302,Cut028]
FEATURE [Sketcher::SketchObject] Sketch307
  ArcFitTolerance = 0
  FullyConstrained = true
  MakeInternals = false
  Placement = pos=(0,13,0) rot=(1,0,0;1.5708rad)
  sketch-geometry (6):
    g0: Circle CenterX=163 CenterY=63 CenterZ=0 NormalX=0 NormalY=0 NormalZ=1 AngleXU=0 Radius=1.625
    g1: Circle CenterX=242 CenterY=63 CenterZ=0 NormalX=0 NormalY=0 NormalZ=1 AngleXU=0 Radius=1.625
    g2: Circle CenterX=163 CenterY=-27 CenterZ=0 NormalX=0 NormalY=0 NormalZ=1 AngleXU=0 Radius=1.625
    g3: Circle CenterX=242 CenterY=-27 CenterZ=0 NormalX=0 NormalY=0 NormalZ=1 AngleXU=0 Radius=1.625
    g4: Circle CenterX=163 CenterY=-63 CenterZ=0 NormalX=0 NormalY=0 NormalZ=1 AngleXU=0 Radius=1.625
    g5: Circle CenterX=242 CenterY=-63 CenterZ=0 NormalX=0 NormalY=0 NormalZ=1 AngleXU=0 Radius=1.625
  constraints (18):
    c: Horizontal(g0,g1)
    c: DistanceX(g0) = 163
    c: DistanceY(g0) = 63
    c: DistanceX(g0,g1) = 79
    c: Horizontal(g2,g3)
    c: Equal(g2,g3)
    c: Equal(g2,g1)
    c: Equal(g2,g0)
    c: Diameter(g2) = 3.25
    c: DistanceY(g2,g0) = 90
    c: Vertical(g3,g1)
    c: Vertical(g2,g0)
    c: Vertical(g2,g4)
    c: Vertical(g5,g3)
    c: Equal(g4,g5)
    c: Diameter(g4) = 3.25
    c: DistanceY(g4,g2) = 36
    c: Horizontal(g5,g4)
FEATURE [Part::Extrusion] Extrude303  label="srsCutsForM3s002"
  Base = -> Sketch307
  Dir = (0,-1,2e-16)
  DirMode = 2
  FaceMakerClass = Part::FaceMakerBullseye
  FaceMakerMode = 3
  LengthFwd = 50
  LengthRev = 0
  Placement = pos=(0,-17,0) rot=(0,0,1;0rad)
  Solid = true
  Symmetric = false
FEATURE [Part::Cut] Cut033  label="piHolder"
  Base = -> Fusion341
  Tool = -> Extrude303
FEATURE [Sketcher::SketchObject] Sketch308
  ArcFitTolerance = 0
  FullyConstrained = true
  MakeInternals = false
  Placement = pos=(0,13,0) rot=(1,0,0;1.5708rad)
  sketch-geometry (6):
    g0: Circle CenterX=163 CenterY=63 CenterZ=0 NormalX=0 NormalY=0 NormalZ=1 AngleXU=0 Radius=1.625
    g1: Circle CenterX=242 CenterY=63 CenterZ=0 NormalX=0 NormalY=0 NormalZ=1 AngleXU=0 Radius=1.625
    g2: Circle CenterX=163 CenterY=-27 CenterZ=0 NormalX=0 NormalY=0 NormalZ=1 AngleXU=0 Radius=1.625
    g3: Circle CenterX=242 CenterY=-27 CenterZ=0 NormalX=0 NormalY=0 NormalZ=1 AngleXU=0 Radius=1.625
    g4: Circle CenterX=163 CenterY=-63 CenterZ=0 NormalX=0 NormalY=0 NormalZ=1 AngleXU=0 Radius=3
    g5: Circle CenterX=242 CenterY=-63 CenterZ=0 NormalX=0 NormalY=0 NormalZ=1 AngleXU=0 Radius=3
  constraints (18):
    c: Horizontal(g0,g1)
    c: DistanceX(g0) = 163
    c: DistanceY(g0) = 63
    c: DistanceX(g0,g1) = 79
    c: Horizontal(g2,g3)
    c: Equal(g2,g3)
    c: Equal(g2,g1)
    c: Equal(g2,g0)
    c: Diameter(g2) = 3.25
    c: DistanceY(g2,g0) = 90
    c: Vertical(g3,g1)
    c: Vertical(g2,g0)
    c: Vertical(g2,g4)
    c: Vertical(g5,g3)
    c: Equal(g4,g5)
    c: Diameter(g4) = 6
    c: DistanceY(g4,g2) = 36
    c: Horizontal(g5,g4)
FEATURE [Part::Extrusion] Extrude304  label="srsCutsForM3s003"
  Base = -> Sketch308
  Dir = (0,-1,2e-16)
  DirMode = 2
  FaceMakerClass = Part::FaceMakerBullseye
  FaceMakerMode = 3
  LengthFwd = 50
  LengthRev = 0
  Placement = pos=(0,-53,0) rot=(0,0,1;0rad)
  Solid = true
  Symmetric = false
FEATURE [Part::Feature] Part__Feature360  label="m3x40s"
  Placement = pos=(163,-21.5,-63) rot=(1,0,0;1.5708rad)
  shape: bbox 5.501 x 43 x 5.501 mm, 32 faces (baked)
FEATURE [Part::Feature] Part__Feature361  label="m3x40s001"
  Placement = pos=(242,-21.5,-63) rot=(1,0,0;1.5708rad)
  shape: bbox 5.501 x 43 x 5.501 mm, 32 faces (baked)
FEATURE [Part::MultiFuse] Fusion342  label="m3x40s002"
  Shapes = -> [Part__Feature360,Part__Feature361]
FEATURE [Part::Cut] Cut034  label="piHolder001"
  Base = -> Cut033
  Tool = -> Extrude304
FEATURE [Part::Fillet] Fillet064  label="batteryHousing004"
  Base = -> Cut032
  EdgeLinks = -> Cut032 [Edge152,Edge154,Edge156,Edge158]
  Edges = 4 edges r=3: [Edge152,Edge154,Edge156,Edge158]
FEATURE [Sketcher::SketchObject] Sketch310
  ArcFitTolerance = 0
  FullyConstrained = true
  MakeInternals = false
  Placement = pos=(0,-4,0) rot=(1,0,0;1.5708rad)
  sketch-geometry (4):
    g0: LineSegment StartX=163.5 StartY=-41.5 StartZ=0 EndX=241.5 EndY=-41.5 EndZ=0
    g1: LineSegment StartX=163.5 StartY=-41.5 StartZ=0 EndX=169.9 EndY=-32 EndZ=0
    g2: LineSegment StartX=169.9 StartY=-32 StartZ=0 EndX=235.1 EndY=-32 EndZ=0
    g3: LineSegment StartX=235.1 StartY=-32 StartZ=0 EndX=241.5 EndY=-41.5 EndZ=0
  constraints (12):
    c: Horizontal(g0)
    c: Coincident(g1,g0)
    c: Horizontal(g2)
    c: Coincident(g3,g0)
    c: DistanceY(g0) = -41.5
    c: Coincident(g1,g2)
    c: DistanceX(g0,g1) = 6.4
    c: DistanceX(g0) = 163.5
    c: Coincident(g2,g3)
    c: DistanceX(g0) = 241.5
    c: DistanceX(g2,g0) = 6.4
    c: DistanceY(g0,g1) = 9.5
FEATURE [Part::Extrusion] Extrude306
  Base = -> Sketch310
  Dir = (0,-1,2e-16)
  DirMode = 2
  FaceMakerClass = Part::FaceMakerBullseye
  FaceMakerMode = 3
  LengthFwd = 10
  LengthRev = 0
  Solid = true
  Symmetric = false
FEATURE [Part::Cut] Cut036  label="srs023"
  Base = -> Cut031
  Tool = -> Extrude306
FEATURE [Sketcher::SketchObject] Sketch311
  ArcFitTolerance = 0
  FullyConstrained = true
  MakeInternals = false
  Placement = pos=(0,0,0) rot=(1,0,0;1.5708rad)
  sketch-geometry (4):
    g0: ArcOfCircle CenterX=233.5 CenterY=-58 CenterZ=0 NormalX=0 NormalY=0 NormalZ=1 AngleXU=0 Radius=4 StartAngle=1e-16 EndAngle=3.14159
    g1: ArcOfCircle CenterX=233.5 CenterY=-62 CenterZ=0 NormalX=0 NormalY=0 NormalZ=1 AngleXU=0 Radius=4 StartAngle=3.14159 EndAngle=6.28319
    g2: LineSegment StartX=229.5 StartY=-58 StartZ=0 EndX=229.5 EndY=-62 EndZ=0
    g3: LineSegment StartX=237.5 StartY=-62 StartZ=0 EndX=237.5 EndY=-58 EndZ=0
  constraints (10):
    c: Tangent(g0,g2) = -1.5708
    c: Tangent(g2,g1) = -1.5708
    c: Tangent(g1,g3) = -1.5708
    c: Tangent(g3,g0) = -1.5708
    c: Equal(g0,g1)
    c: Vertical(g2)
    c: DistanceX(g1) = 237.5
    c: DistanceX(g1,g1) = 8
    c: DistanceY(g1,g0) = 4
    c: DistanceY(g1) = -62
FEATURE [Part::Extrusion] Extrude307  label="baseWireCut"
  Base = -> Sketch311
  Dir = (0,-1,2e-16)
  DirMode = 2
  FaceMakerClass = Part::FaceMakerBullseye
  FaceMakerMode = 3
  LengthFwd = 4
  LengthRev = 0
  Solid = true
  Symmetric = false
FEATURE [Sketcher::SketchObject] Sketch312
  ArcFitTolerance = 0
  FullyConstrained = true
  MakeInternals = false
  Placement = pos=(0,0,0) rot=(1,0,0;1.5708rad)
  sketch-geometry (8):
    g0: ArcOfCircle CenterX=12.75 CenterY=15.33 CenterZ=0 NormalX=0 NormalY=0 NormalZ=1 AngleXU=0 Radius=0.9 StartAngle=1.5708 EndAngle=3.14159
    g1: ArcOfCircle CenterX=16.95 CenterY=15.33 CenterZ=0 NormalX=0 NormalY=0 NormalZ=1 AngleXU=0 Radius=0.9 StartAngle=8e-16 EndAngle=1.5708
    g2: ArcOfCircle CenterX=16.95 CenterY=14.43 CenterZ=0 NormalX=0 NormalY=0 NormalZ=1 AngleXU=0 Radius=0.9 StartAngle=4.71239 EndAngle=6.28319
    g3: ArcOfCircle CenterX=12.75 CenterY=14.43 CenterZ=0 NormalX=0 NormalY=0 NormalZ=1 AngleXU=0 Radius=0.9 StartAngle=3.14159 EndAngle=4.71239
    g4: LineSegment StartX=12.75 StartY=16.23 StartZ=0 EndX=16.95 EndY=16.23 EndZ=0
    g5: LineSegment StartX=17.85 StartY=15.33 StartZ=0 EndX=17.85 EndY=14.43 EndZ=0
    g6: LineSegment StartX=16.95 StartY=13.53 StartZ=0 EndX=12.75 EndY=13.53 EndZ=0
    g7: LineSegment StartX=11.85 StartY=14.43 StartZ=0 EndX=11.85 EndY=15.33 EndZ=0
  constraints (28):
    c: Coincident(g4,g0)
    c: Coincident(g4,g1)
    c: Horizontal(g4)
    c: Coincident(g5,g1)
    c: Coincident(g5,g2)
    c: Coincident(g6,g2)
    c: Coincident(g6,g3)
    c: Horizontal(g6)
    c: Coincident(g7,g3)
    c: Coincident(g7,g0)
    c: Vertical(g7)
    c: Radius(g0) = 0.9
    c: DistanceY(g0,g0) = 0
    c: Angle(g3) = 1.5708
    c: DistanceY(g3,g3) = 0
    c: DistanceY(g3,g0) = 0.9
    c: DistanceY(g3) = 14.43
    c: Radius(g3) = 0.9
    c: Radius(g2) = 0.9
    c: Radius(g1) = 0.9
    c: DistanceX(g6,g6) = 4.2
    c: DistanceX(g3) = 12.75
    c: DistanceY(g1,g1) = 0
    c: DistanceX(g2,g2) = 0
    c: Angle(g1) = 1.5708
    c: Angle(g2) = 1.5708
    c: Vertical(g5)
    c: DistanceX(g0,g0) = 0
FEATURE [Part::Extrusion] Extrude308
  Base = -> Sketch312
  Dir = (0,-1,2e-16)
  DirMode = 2
  FaceMakerClass = Part::FaceMakerBullseye
  FaceMakerMode = 3
  LengthFwd = 5
  LengthRev = 0
  Placement = pos=(-0.3,2,-0.1) rot=(0,0,1;0rad)
  Solid = true
  Symmetric = false
FEATURE [Sketcher::SketchObject] Sketch313
  ArcFitTolerance = 0
  FullyConstrained = true
  MakeInternals = false
  Placement = pos=(0,0,0) rot=(1,0,0;1.5708rad)
  sketch-geometry (8):
    g0: ArcOfCircle CenterX=11.7 CenterY=15.45 CenterZ=0 NormalX=0 NormalY=0 NormalZ=1 AngleXU=0 Radius=0.9 StartAngle=1.5708 EndAngle=3.14159
    g1: ArcOfCircle CenterX=17.4 CenterY=15.45 CenterZ=0 NormalX=0 NormalY=0 NormalZ=1 AngleXU=0 Radius=0.9 StartAngle=4e-16 EndAngle=1.5708
    g2: ArcOfCircle CenterX=16.8 CenterY=14.2 CenterZ=0 NormalX=0 NormalY=0 NormalZ=1 AngleXU=0 Radius=1.5 StartAngle=4.71239 EndAngle=6.28319
    g3: ArcOfCircle CenterX=12.3 CenterY=14.2 CenterZ=0 NormalX=0 NormalY=0 NormalZ=1 AngleXU=0 Radius=1.5 StartAngle=3.14159 EndAngle=4.71239
    g4: LineSegment StartX=11.7 StartY=16.35 StartZ=0 EndX=17.4 EndY=16.35 EndZ=0
    g5: LineSegment StartX=18.3 StartY=15.45 StartZ=0 EndX=18.3 EndY=14.2 EndZ=0
    g6: LineSegment StartX=16.8 StartY=12.7 StartZ=0 EndX=12.3 EndY=12.7 EndZ=0
    g7: LineSegment StartX=10.8 StartY=14.2 StartZ=0 EndX=10.8 EndY=15.45 EndZ=0
  constraints (28):
    c: Coincident(g4,g0)
    c: Coincident(g4,g1)
    c: Horizontal(g4)
    c: Coincident(g5,g1)
    c: Coincident(g5,g2)
    c: Coincident(g6,g2)
    c: Coincident(g6,g3)
    c: Horizontal(g6)
    c: Coincident(g7,g3)
    c: Coincident(g7,g0)
    c: Vertical(g7)
    c: Radius(g0) = 0.9
    c: DistanceY(g0,g0) = 0
    c: Angle(g3) = 1.5708
    c: DistanceY(g3,g3) = 0
    c: DistanceY(g3,g0) = 1.25
    c: DistanceY(g3) = 14.2
    c: Radius(g3) = 1.5
    c: Radius(g2) = 1.5
    c: Radius(g1) = 0.9
    c: DistanceX(g6,g6) = 4.5
    c: DistanceX(g3) = 12.3
    c: DistanceY(g1,g1) = 0
    c: DistanceX(g2,g2) = 0
    c: Angle(g1) = 1.5708
    c: Angle(g2) = 1.5708
    c: Vertical(g5)
    c: DistanceX(g0,g0) = 0
FEATURE [Part::Extrusion] Extrude309
  Base = -> Sketch313
  Dir = (0,-1,2e-16)
  DirMode = 2
  FaceMakerClass = Part::FaceMakerBullseye
  FaceMakerMode = 3
  LengthFwd = 1
  LengthRev = 0
  Placement = pos=(0,2.5,0) rot=(0,0,1;0rad)
  Solid = true
  Symmetric = false
FEATURE [Part::MultiFuse] Fusion383  label="button006"
  Placement = pos=(104.5,9.5,-78) rot=(1,0,0;1.5708rad)
  Shapes = -> [Extrude308,Extrude309]
FEATURE [Sketcher::SketchObject] Sketch314
  ArcFitTolerance = 0
  FullyConstrained = true
  MakeInternals = false
  Placement = pos=(0,0,0) rot=(1,0,0;1.5708rad)
  sketch-geometry (8):
    g0: ArcOfCircle CenterX=12.75 CenterY=15.33 CenterZ=0 NormalX=0 NormalY=0 NormalZ=1 AngleXU=0 Radius=0.9 StartAngle=1.5708 EndAngle=3.14159
    g1: ArcOfCircle CenterX=16.95 CenterY=15.33 CenterZ=0 NormalX=0 NormalY=0 NormalZ=1 AngleXU=0 Radius=0.9 StartAngle=8e-16 EndAngle=1.5708
    g2: ArcOfCircle CenterX=16.95 CenterY=14.43 CenterZ=0 NormalX=0 NormalY=0 NormalZ=1 AngleXU=0 Radius=0.9 StartAngle=4.71239 EndAngle=6.28319
    g3: ArcOfCircle CenterX=12.75 CenterY=14.43 CenterZ=0 NormalX=0 NormalY=0 NormalZ=1 AngleXU=0 Radius=0.9 StartAngle=3.14159 EndAngle=4.71239
    g4: LineSegment StartX=12.75 StartY=16.23 StartZ=0 EndX=16.95 EndY=16.23 EndZ=0
    g5: LineSegment StartX=17.85 StartY=15.33 StartZ=0 EndX=17.85 EndY=14.43 EndZ=0
    g6: LineSegment StartX=16.95 StartY=13.53 StartZ=0 EndX=12.75 EndY=13.53 EndZ=0
    g7: LineSegment StartX=11.85 StartY=14.43 StartZ=0 EndX=11.85 EndY=15.33 EndZ=0
  constraints (28):
    c: Coincident(g4,g0)
    c: Coincident(g4,g1)
    c: Horizontal(g4)
    c: Coincident(g5,g1)
    c: Coincident(g5,g2)
    c: Coincident(g6,g2)
    c: Coincident(g6,g3)
    c: Horizontal(g6)
    c: Coincident(g7,g3)
    c: Coincident(g7,g0)
    c: Vertical(g7)
    c: Radius(g0) = 0.9
    c: DistanceY(g0,g0) = 0
    c: Angle(g3) = 1.5708
    c: DistanceY(g3,g3) = 0
    c: DistanceY(g3,g0) = 0.9
    c: DistanceY(g3) = 14.43
    c: Radius(g3) = 0.9
    c: Radius(g2) = 0.9
    c: Radius(g1) = 0.9
    c: DistanceX(g6,g6) = 4.2
    c: DistanceX(g3) = 12.75
    c: DistanceY(g1,g1) = 0
    c: DistanceX(g2,g2) = 0
    c: Angle(g1) = 1.5708
    c: Angle(g2) = 1.5708
    c: Vertical(g5)
    c: DistanceX(g0,g0) = 0
FEATURE [Part::Extrusion] Extrude310
  Base = -> Sketch314
  Dir = (0,-1,2e-16)
  DirMode = 2
  FaceMakerClass = Part::FaceMakerBullseye
  FaceMakerMode = 3
  LengthFwd = 5
  LengthRev = 0
  Placement = pos=(-0.3,2,-0.1) rot=(0,0,1;0rad)
  Solid = true
  Symmetric = false
FEATURE [Sketcher::SketchObject] Sketch315
  ArcFitTolerance = 0
  FullyConstrained = true
  MakeInternals = false
  Placement = pos=(0,0,0) rot=(1,0,0;1.5708rad)
  sketch-geometry (8):
    g0: ArcOfCircle CenterX=11.7 CenterY=15.45 CenterZ=0 NormalX=0 NormalY=0 NormalZ=1 AngleXU=0 Radius=0.9 StartAngle=1.5708 EndAngle=3.14159
    g1: ArcOfCircle CenterX=17.4 CenterY=15.45 CenterZ=0 NormalX=0 NormalY=0 NormalZ=1 AngleXU=0 Radius=0.9 StartAngle=4e-16 EndAngle=1.5708
    g2: ArcOfCircle CenterX=16.8 CenterY=14.2 CenterZ=0 NormalX=0 NormalY=0 NormalZ=1 AngleXU=0 Radius=1.5 StartAngle=4.71239 EndAngle=6.28319
    g3: ArcOfCircle CenterX=12.3 CenterY=14.2 CenterZ=0 NormalX=0 NormalY=0 NormalZ=1 AngleXU=0 Radius=1.5 StartAngle=3.14159 EndAngle=4.71239
    g4: LineSegment StartX=11.7 StartY=16.35 StartZ=0 EndX=17.4 EndY=16.35 EndZ=0
    g5: LineSegment StartX=18.3 StartY=15.45 StartZ=0 EndX=18.3 EndY=14.2 EndZ=0
    g6: LineSegment StartX=16.8 StartY=12.7 StartZ=0 EndX=12.3 EndY=12.7 EndZ=0
    g7: LineSegment StartX=10.8 StartY=14.2 StartZ=0 EndX=10.8 EndY=15.45 EndZ=0
  constraints (28):
    c: Coincident(g4,g0)
    c: Coincident(g4,g1)
    c: Horizontal(g4)
    c: Coincident(g5,g1)
    c: Coincident(g5,g2)
    c: Coincident(g6,g2)
    c: Coincident(g6,g3)
    c: Horizontal(g6)
    c: Coincident(g7,g3)
    c: Coincident(g7,g0)
    c: Vertical(g7)
    c: Radius(g0) = 0.9
    c: DistanceY(g0,g0) = 0
    c: Angle(g3) = 1.5708
    c: DistanceY(g3,g3) = 0
    c: DistanceY(g3,g0) = 1.25
    c: DistanceY(g3) = 14.2
    c: Radius(g3) = 1.5
    c: Radius(g2) = 1.5
    c: Radius(g1) = 0.9
    c: DistanceX(g6,g6) = 4.5
    c: DistanceX(g3) = 12.3
    c: DistanceY(g1,g1) = 0
    c: DistanceX(g2,g2) = 0
    c: Angle(g1) = 1.5708
    c: Angle(g2) = 1.5708
    c: Vertical(g5)
    c: DistanceX(g0,g0) = 0
FEATURE [Part::Extrusion] Extrude311
  Base = -> Sketch315
  Dir = (0,-1,2e-16)
  DirMode = 2
  FaceMakerClass = Part::FaceMakerBullseye
  FaceMakerMode = 3
  LengthFwd = 1
  LengthRev = 0
  Placement = pos=(0,2.5,0) rot=(0,0,1;0rad)
  Solid = true
  Symmetric = false
FEATURE [Part::MultiFuse] Fusion384  label="button007"
  Placement = pos=(72,9.5,-78) rot=(1,0,0;1.5708rad)
  Shapes = -> [Extrude310,Extrude311]
FEATURE [Part::MultiFuse] Fusion385  label="buttons"
  Placement = pos=(94,-4,0) rot=(0,0,1;0rad)
  Shapes = -> [Fusion384,Fusion383]
FEATURE [Sketcher::SketchObject] Sketch317
  ArcFitTolerance = 1e-06
  FullyConstrained = true
  MakeInternals = false
  MapMode = 5
  Placement = pos=(0,13,0) rot=(1,0,0;1.5708rad)
  sketch-geometry (4):
    g0: LineSegment StartX=78 StartY=-50 StartZ=0 EndX=78 EndY=50 EndZ=0
    g1: LineSegment StartX=78 StartY=50 StartZ=0 EndX=148 EndY=50 EndZ=0
    g2: LineSegment StartX=148 StartY=50 StartZ=0 EndX=148 EndY=-50 EndZ=0
    g3: LineSegment StartX=148 StartY=-50 StartZ=0 EndX=78 EndY=-50 EndZ=0
  constraints (12):
    c: Coincident(g0,g1)
    c: Coincident(g1,g2)
    c: Coincident(g2,g3)
    c: Coincident(g3,g0)
    c: Vertical(g0)
    c: Vertical(g2)
    c: Horizontal(g1)
    c: Horizontal(g3)
    c: DistanceX(g0) = 78
    c: DistanceY(g0) = 50
    c: DistanceY(g0) = -50
    c: DistanceX(g1,g1) = 70
FEATURE [Part::Extrusion] Extrude312
  Base = -> Sketch317
  Dir = (0,-1,2e-16)
  DirMode = 2
  FaceMakerClass = Part::FaceMakerBullseye
  FaceMakerMode = 3
  LengthFwd = 3
  LengthRev = 0
  Solid = true
  Symmetric = false
FEATURE [Part::Cut] Cut038  label="base025"
  Base = -> Fillet064
  Tool = -> Extrude312
FEATURE [Part::Fillet] Fillet072  label="batteryHousing005"
  Base = -> Cut038
  EdgeLinks = -> Cut038 [Edge11,Edge12,Edge13,Edge21,Edge22,Edge23,Edge24,Edge33,Edge34,Edge35,Edge37,Edge40,Edge53,Edge54,Edge55,Edge56,Edge57,Edge58,Edge59,Edge60,Edge61]
  Edges = 21 edges r=1: [Edge11,Edge12,Edge13,Edge21,Edge22,Edge23,Edge24,Edge33,Edge34,Edge35,Edge37,Edge40,Edge53,Edge54,Edge55,Edge56,Edge57,Edge58,Edge59,Edge60,Edge61]
FEATURE [Part::Box] Box003  label="Cube001"
  AttacherType = Attacher::AttachEngine3D
  Height = 10
  Length = 38.5
  Placement = pos=(170,-4,50.5) rot=(0,0,-1;1.5708rad)
  Width = 65
FEATURE [Part::FeaturePython] Clone124  label="m2Nuts076"  # WARN: FeaturePython — macro-defined, semantics opaque (R4)
  AttacherType = Attacher::AttachEngine3D
  Fuse = false
  Placement = pos=(0,0,4) rot=(0,0,1;0rad)
  Scale = (1.05,1.05,5)
FEATURE [Part::FeaturePython] Clone125  label="m2Nuts077"  # WARN: FeaturePython — macro-defined, semantics opaque (R4)
  AttacherType = Attacher::AttachEngine3D
  Fuse = false
  Placement = pos=(0,0,0.8) rot=(0,0,1;0rad)
  Scale = (1.05,1.05,1)
FEATURE [Part::FeaturePython] Clone126  label="m2Nuts078"  # WARN: FeaturePython — macro-defined, semantics opaque (R4)
  AttacherType = Attacher::AttachEngine3D
  Fuse = false
  Placement = pos=(0,0,4) rot=(0,0,1;0rad)
  Scale = (1.05,1.05,5)
FEATURE [Part::FeaturePython] Clone127  label="m2Nuts079"  # WARN: FeaturePython — macro-defined, semantics opaque (R4)
  AttacherType = Attacher::AttachEngine3D
  Fuse = false
  Placement = pos=(0,0,0.8) rot=(0,0,1;0rad)
  Scale = (1.05,1.05,1)
FEATURE [Part::FeaturePython] Clone128  label="m2Nuts080"  # WARN: FeaturePython — macro-defined, semantics opaque (R4)
  AttacherType = Attacher::AttachEngine3D
  Fuse = false
  Placement = pos=(0,0,4) rot=(0,0,1;0rad)
  Scale = (1.05,1.05,5)
FEATURE [Part::FeaturePython] Clone129  label="m2Nuts081"  # WARN: FeaturePython — macro-defined, semantics opaque (R4)
  AttacherType = Attacher::AttachEngine3D
  Fuse = false
  Placement = pos=(0,0,0.8) rot=(0,0,1;0rad)
  Scale = (1.05,1.05,1)
FEATURE [Part::FeaturePython] Clone130  label="m2Nuts082"  # WARN: FeaturePython — macro-defined, semantics opaque (R4)
  AttacherType = Attacher::AttachEngine3D
  Fuse = false
  Placement = pos=(0,0,4) rot=(0,0,1;0rad)
  Scale = (1.05,1.05,5)
FEATURE [Part::FeaturePython] Clone131  label="m2Nuts083"  # WARN: FeaturePython — macro-defined, semantics opaque (R4)
  AttacherType = Attacher::AttachEngine3D
  Fuse = false
  Placement = pos=(0,0,0.8) rot=(0,0,1;0rad)
  Scale = (1.05,1.05,1)
FEATURE [Part::FeaturePython] Clone132  label="m2Nuts084"  # WARN: FeaturePython — macro-defined, semantics opaque (R4)
  AttacherType = Attacher::AttachEngine3D
  Fuse = false
  Placement = pos=(0,0,4) rot=(0,0,1;0rad)
  Scale = (1.05,1.05,5)
FEATURE [Part::FeaturePython] Clone133  label="m2Nuts085"  # WARN: FeaturePython — macro-defined, semantics opaque (R4)
  AttacherType = Attacher::AttachEngine3D
  Fuse = false
  Placement = pos=(0,0,0.8) rot=(0,0,1;0rad)
  Scale = (1.05,1.05,1)
FEATURE [Part::FeaturePython] Clone134  label="m2Nuts086"  # WARN: FeaturePython — macro-defined, semantics opaque (R4)
  AttacherType = Attacher::AttachEngine3D
  Fuse = false
  Placement = pos=(0,0,4) rot=(0,0,1;0rad)
  Scale = (1.05,1.05,5)
FEATURE [Part::FeaturePython] Clone135  label="m2Nuts087"  # WARN: FeaturePython — macro-defined, semantics opaque (R4)
  AttacherType = Attacher::AttachEngine3D
  Fuse = false
  Placement = pos=(0,0,0.8) rot=(0,0,1;0rad)
  Scale = (1.05,1.05,1)
FEATURE [Part::FeaturePython] Clone136  label="M3Nut058"  # WARN: FeaturePython — macro-defined, semantics opaque (R4)
  AttacherType = Attacher::AttachEngine3D
  Fuse = false
  Placement = pos=(0,0,4.5) rot=(0,0,1;0rad)
  Scale = (1.1,1.1,5)
FEATURE [Part::FeaturePython] Clone137  label="M3Nut059"  # WARN: FeaturePython — macro-defined, semantics opaque (R4)
  AttacherType = Attacher::AttachEngine3D
  Fuse = false
  Placement = pos=(0,0,0.9) rot=(0,0,1;0rad)
  Scale = (1.1,1.1,1)
FEATURE [Part::FeaturePython] Clone138  label="M3Nut060"  # WARN: FeaturePython — macro-defined, semantics opaque (R4)
  AttacherType = Attacher::AttachEngine3D
  Fuse = false
  Placement = pos=(0,0,4.5) rot=(0,0,1;0rad)
  Scale = (1.1,1.1,5)
FEATURE [Part::FeaturePython] Clone139  label="M3Nut061"  # WARN: FeaturePython — macro-defined, semantics opaque (R4)
  AttacherType = Attacher::AttachEngine3D
  Fuse = false
  Placement = pos=(0,0,0.9) rot=(0,0,1;0rad)
  Scale = (1.1,1.1,1)
FEATURE [Part::FeaturePython] Clone140  label="M3Nut062"  # WARN: FeaturePython — macro-defined, semantics opaque (R4)
  AttacherType = Attacher::AttachEngine3D
  Fuse = false
  Placement = pos=(0,0,4.5) rot=(0,0,1;0rad)
  Scale = (1.1,1.1,5)
FEATURE [Part::FeaturePython] Clone141  label="M3Nut063"  # WARN: FeaturePython — macro-defined, semantics opaque (R4)
  AttacherType = Attacher::AttachEngine3D
  Fuse = false
  Placement = pos=(0,0,0.9) rot=(0,0,1;0rad)
  Scale = (1.1,1.1,1)
FEATURE [Part::FeaturePython] Clone142  label="m2Nuts088"  # WARN: FeaturePython — macro-defined, semantics opaque (R4)
  AttacherType = Attacher::AttachEngine3D
  Fuse = false
  Placement = pos=(0,0,4) rot=(0,0,1;0rad)
  Scale = (1.05,1.05,5)
FEATURE [Part::FeaturePython] Clone143  label="m2Nuts089"  # WARN: FeaturePython — macro-defined, semantics opaque (R4)
  AttacherType = Attacher::AttachEngine3D
  Fuse = false
  Placement = pos=(0,0,0.8) rot=(0,0,1;0rad)
  Scale = (1.05,1.05,1)
FEATURE [Part::FeaturePython] Clone144  label="m2Nuts090"  # WARN: FeaturePython — macro-defined, semantics opaque (R4)
  AttacherType = Attacher::AttachEngine3D
  Fuse = false
  Placement = pos=(0,0,4) rot=(0,0,1;0rad)
  Scale = (1.05,1.05,5)
FEATURE [Part::FeaturePython] Clone145  label="m2Nuts091"  # WARN: FeaturePython — macro-defined, semantics opaque (R4)
  AttacherType = Attacher::AttachEngine3D
  Fuse = false
  Placement = pos=(0,0,0.8) rot=(0,0,1;0rad)
  Scale = (1.05,1.05,1)
FEATURE [Part::FeaturePython] Clone146  label="M3Nut064"  # WARN: FeaturePython — macro-defined, semantics opaque (R4)
  AttacherType = Attacher::AttachEngine3D
  Fuse = false
  Placement = pos=(175,-8,74) rot=(0.57735,0.57735,0.57735;2.0944rad)
  Scale = (1.09,1.09,1)
FEATURE [Part::FeaturePython] Clone147  label="M3Nut065"  # WARN: FeaturePython — macro-defined, semantics opaque (R4)
  AttacherType = Attacher::AttachEngine3D
  Fuse = false
  Placement = pos=(175,-8,74) rot=(0.57735,0.57735,0.57735;2.0944rad)
  Scale = (1.09,1.09,1)
FEATURE [Part::FeaturePython] Clone148  label="M3Nut066"  # WARN: FeaturePython — macro-defined, semantics opaque (R4)
  AttacherType = Attacher::AttachEngine3D
  Fuse = false
  Placement = pos=(175,-8,74) rot=(0.57735,0.57735,0.57735;2.0944rad)
  Scale = (1.09,1.09,1)
FEATURE [Part::FeaturePython] Clone149  label="M3Nut067"  # WARN: FeaturePython — macro-defined, semantics opaque (R4)
  AttacherType = Attacher::AttachEngine3D
  Fuse = false
  Placement = pos=(175,-8,74) rot=(0.57735,0.57735,0.57735;2.0944rad)
  Scale = (1.09,1.09,1)
FEATURE [Part::FeaturePython] Clone150  label="m2Nuts092"  # WARN: FeaturePython — macro-defined, semantics opaque (R4)
  AttacherType = Attacher::AttachEngine3D
  Fuse = false
  Placement = pos=(0,0,4) rot=(0,0,1;0rad)
  Scale = (1.05,1.05,5)
FEATURE [Part::FeaturePython] Clone151  label="m2Nuts093"  # WARN: FeaturePython — macro-defined, semantics opaque (R4)
  AttacherType = Attacher::AttachEngine3D
  Fuse = false
  Placement = pos=(0,0,0.8) rot=(0,0,1;0rad)
  Scale = (1.05,1.05,1)
FEATURE [Part::FeaturePython] Clone152  label="m2Nuts094"  # WARN: FeaturePython — macro-defined, semantics opaque (R4)
  AttacherType = Attacher::AttachEngine3D
  Fuse = false
  Placement = pos=(0,0,4) rot=(0,0,1;0rad)
  Scale = (1.05,1.05,5)
FEATURE [Part::FeaturePython] Clone153  label="m2Nuts095"  # WARN: FeaturePython — macro-defined, semantics opaque (R4)
  AttacherType = Attacher::AttachEngine3D
  Fuse = false
  Placement = pos=(0,0,0.8) rot=(0,0,1;0rad)
  Scale = (1.05,1.05,1)
FEATURE [Part::FeaturePython] Clone154  label="m2Nuts096"  # WARN: FeaturePython — macro-defined, semantics opaque (R4)
  AttacherType = Attacher::AttachEngine3D
  Fuse = false
  Placement = pos=(0,0,4) rot=(0,0,1;0rad)
  Scale = (1.05,1.05,5)
FEATURE [Part::FeaturePython] Clone155  label="m2Nuts097"  # WARN: FeaturePython — macro-defined, semantics opaque (R4)
  AttacherType = Attacher::AttachEngine3D
  Fuse = false
  Placement = pos=(0,0,0.8) rot=(0,0,1;0rad)
  Scale = (1.05,1.05,1)
FEATURE [Part::FeaturePython] Clone156  label="m2Nuts098"  # WARN: FeaturePython — macro-defined, semantics opaque (R4)
  AttacherType = Attacher::AttachEngine3D
  Fuse = false
  Placement = pos=(0,0,4) rot=(0,0,1;0rad)
  Scale = (1.05,1.05,5)
FEATURE [Part::FeaturePython] Clone157  label="m2Nuts099"  # WARN: FeaturePython — macro-defined, semantics opaque (R4)
  AttacherType = Attacher::AttachEngine3D
  Fuse = false
  Placement = pos=(0,0,0.8) rot=(0,0,1;0rad)
  Scale = (1.05,1.05,1)
FEATURE [Part::FeaturePython] Clone158  label="m2Nuts100"  # WARN: FeaturePython — macro-defined, semantics opaque (R4)
  AttacherType = Attacher::AttachEngine3D
  Fuse = false
  Placement = pos=(0,0,4) rot=(0,0,1;0rad)
  Scale = (1.05,1.05,5)
FEATURE [Part::FeaturePython] Clone159  label="m2Nuts101"  # WARN: FeaturePython — macro-defined, semantics opaque (R4)
  AttacherType = Attacher::AttachEngine3D
  Fuse = false
  Placement = pos=(0,0,0.8) rot=(0,0,1;0rad)
  Scale = (1.05,1.05,1)
FEATURE [Part::FeaturePython] Clone160  label="m2Nuts102"  # WARN: FeaturePython — macro-defined, semantics opaque (R4)
  AttacherType = Attacher::AttachEngine3D
  Fuse = false
  Placement = pos=(0,0,4) rot=(0,0,1;0rad)
  Scale = (1.05,1.05,5)
FEATURE [Part::FeaturePython] Clone161  label="m2Nuts103"  # WARN: FeaturePython — macro-defined, semantics opaque (R4)
  AttacherType = Attacher::AttachEngine3D
  Fuse = false
  Placement = pos=(0,0,0.8) rot=(0,0,1;0rad)
  Scale = (1.05,1.05,1)
FEATURE [Part::FeaturePython] Clone162  label="m2Nuts104"  # WARN: FeaturePython — macro-defined, semantics opaque (R4)
  AttacherType = Attacher::AttachEngine3D
  Fuse = false
  Placement = pos=(0,0,4) rot=(0,0,1;0rad)
  Scale = (1.05,1.05,5)
FEATURE [Part::FeaturePython] Clone163  label="m2Nuts105"  # WARN: FeaturePython — macro-defined, semantics opaque (R4)
  AttacherType = Attacher::AttachEngine3D
  Fuse = false
  Placement = pos=(0,0,0.8) rot=(0,0,1;0rad)
  Scale = (1.05,1.05,1)
FEATURE [Part::FeaturePython] Clone164  label="m2Nuts106"  # WARN: FeaturePython — macro-defined, semantics opaque (R4)
  AttacherType = Attacher::AttachEngine3D
  Fuse = false
  Placement = pos=(0,0,4) rot=(0,0,1;0rad)
  Scale = (1.05,1.05,5)
FEATURE [Part::FeaturePython] Clone165  label="m2Nuts107"  # WARN: FeaturePython — macro-defined, semantics opaque (R4)
  AttacherType = Attacher::AttachEngine3D
  Fuse = false
  Placement = pos=(0,0,0.8) rot=(0,0,1;0rad)
  Scale = (1.05,1.05,1)
FEATURE [Part::FeaturePython] Clone166  label="m2Nuts108"  # WARN: FeaturePython — macro-defined, semantics opaque (R4)
  AttacherType = Attacher::AttachEngine3D
  Fuse = false
  Placement = pos=(0,0,4) rot=(0,0,1;0rad)
  Scale = (1.05,1.05,5)
FEATURE [Part::FeaturePython] Clone167  label="m2Nuts109"  # WARN: FeaturePython — macro-defined, semantics opaque (R4)
  AttacherType = Attacher::AttachEngine3D
  Fuse = false
  Placement = pos=(0,0,0.8) rot=(0,0,1;0rad)
  Scale = (1.05,1.05,1)
FEATURE [Part::FeaturePython] Clone168  label="m2Nuts110"  # WARN: FeaturePython — macro-defined, semantics opaque (R4)
  AttacherType = Attacher::AttachEngine3D
  Fuse = false
  Placement = pos=(0,0,4) rot=(0,0,1;0rad)
  Scale = (1.05,1.05,5)
FEATURE [Part::FeaturePython] Clone169  label="m2Nuts111"  # WARN: FeaturePython — macro-defined, semantics opaque (R4)
  AttacherType = Attacher::AttachEngine3D
  Fuse = false
  Placement = pos=(0,0,0.8) rot=(0,0,1;0rad)
  Scale = (1.05,1.05,1)
FEATURE [Part::FeaturePython] Clone170  label="m2Nuts112"  # WARN: FeaturePython — macro-defined, semantics opaque (R4)
  AttacherType = Attacher::AttachEngine3D
  Fuse = false
  Placement = pos=(0,0,4) rot=(0,0,1;0rad)
  Scale = (1.05,1.05,5)
FEATURE [Part::FeaturePython] Clone171  label="m2Nuts113"  # WARN: FeaturePython — macro-defined, semantics opaque (R4)
  AttacherType = Attacher::AttachEngine3D
  Fuse = false
  Placement = pos=(0,0,0.8) rot=(0,0,1;0rad)
  Scale = (1.05,1.05,1)
FEATURE [Part::FeaturePython] Clone172  label="m2Nuts114"  # WARN: FeaturePython — macro-defined, semantics opaque (R4)
  AttacherType = Attacher::AttachEngine3D
  Fuse = false
  Placement = pos=(0,0,4) rot=(0,0,1;0rad)
  Scale = (1.05,1.05,5)
FEATURE [Part::FeaturePython] Clone173  label="m2Nuts115"  # WARN: FeaturePython — macro-defined, semantics opaque (R4)
  AttacherType = Attacher::AttachEngine3D
  Fuse = false
  Placement = pos=(0,0,0.8) rot=(0,0,1;0rad)
  Scale = (1.05,1.05,1)
FEATURE [Part::Cylinder] Cylinder072 .. Cylinder077  x6 (patterned run collapsed; names and placements below)
  Angle = 360
  AttacherType = Attacher::AttachEngine3D
  FirstAngle = 0
  Height = 8
  Radius = 2
  SecondAngle = 0
FEATURE [Part::Cylinder] Cylinder078
  Angle = 360
  AttacherType = Attacher::AttachEngine3D
  FirstAngle = 0
  Height = 9
  Radius = 2
  SecondAngle = 0
FEATURE [Part::Cylinder] Cylinder079
  Angle = 360
  AttacherType = Attacher::AttachEngine3D
  FirstAngle = 0
  Height = 9
  Radius = 2
  SecondAngle = 0
FEATURE [Part::Cylinder] Cylinder080
  Angle = 360
  AttacherType = Attacher::AttachEngine3D
  FirstAngle = 0
  Height = 9
  Radius = 2
  SecondAngle = 0
FEATURE [Part::Cylinder] Cylinder081 .. Cylinder094  x14 (patterned run collapsed; names and placements below)
  Angle = 360
  AttacherType = Attacher::AttachEngine3D
  FirstAngle = 0
  Height = 8
  Radius = 2
  SecondAngle = 0
FEATURE [Part::MultiFuse] Fusion386
  Shapes = -> [Clone143,Clone142]
FEATURE [Part::MultiFuse] Fusion387  label="m2Cuts035"
  Placement = pos=(182.13,0,-31.13) rot=(0.57735,0.57735,0.57735;4.18879rad)
  Shapes = -> [Cylinder081,Fusion386]
FEATURE [Part::MultiFuse] Fusion389
  Shapes = -> [Clone125,Clone124]
FEATURE [Part::MultiFuse] Fusion390  label="m2Cuts036"
  Placement = pos=(178.54,-14.55,62.5) rot=(1,0,0;3.14159rad)
  Shapes = -> [Cylinder072,Fusion389]
FEATURE [Part::MultiFuse] Fusion391
  Shapes = -> [Clone127,Clone126]
FEATURE [Part::MultiFuse] Fusion392  label="m2Cuts037"
  Placement = pos=(178.54,-34.85,62.5) rot=(1,0,0;3.14159rad)
  Shapes = -> [Cylinder073,Fusion391]
FEATURE [Part::MultiFuse] Fusion393
  Shapes = -> [Clone129,Clone128]
FEATURE [Part::MultiFuse] Fusion394  label="m2Cuts038"
  Placement = pos=(198.84,-14.55,62.5) rot=(1,0,0;3.14159rad)
  Shapes = -> [Cylinder074,Fusion393]
FEATURE [Part::MultiFuse] Fusion395
  Shapes = -> [Clone131,Clone130]
FEATURE [Part::MultiFuse] Fusion396  label="m2Cuts039"
  Placement = pos=(208.09,-14.55,62.5) rot=(1,0,0;3.14159rad)
  Shapes = -> [Cylinder075,Fusion395]
FEATURE [Part::MultiFuse] Fusion397
  Shapes = -> [Clone133,Clone132]
FEATURE [Part::MultiFuse] Fusion398  label="m2Cuts040"
  Placement = pos=(225.89,-14.55,62.5) rot=(1,0,0;3.14159rad)
  Shapes = -> [Cylinder076,Fusion397]
FEATURE [Part::MultiFuse] Fusion399
  Shapes = -> [Clone135,Clone134]
FEATURE [Part::MultiFuse] Fusion400  label="m2Cuts041"
  Placement = pos=(225.89,-34.85,62.5) rot=(1,0,0;3.14159rad)
  Shapes = -> [Cylinder077,Fusion399]
FEATURE [Part::MultiFuse] Fusion401  label="m2Cuts042"
  Shapes = -> [Fusion390,Fusion392,Fusion394,Fusion396,Fusion398,Fusion400]
FEATURE [Part::Cut] Cut039  label="gpsM2Cuts001"
  Base = -> Fusion401
  Tool = -> Box003
FEATURE [Part::MultiFuse] Fusion402
  Shapes = -> [Clone136,Cylinder078]
FEATURE [Part::MultiFuse] Fusion403  label="m3NutCut008"
  Placement = pos=(180.93,0,53.45) rot=(0.57735,0.57735,0.57735;4.18879rad)
  Shapes = -> [Clone137,Fusion402]
FEATURE [Part::MultiFuse] Fusion404
  Shapes = -> [Clone138,Cylinder079]
FEATURE [Part::MultiFuse] Fusion405  label="m3NutCut009"
  Placement = pos=(224.07,0,53.45) rot=(0.57735,0.57735,0.57735;4.18879rad)
  Shapes = -> [Clone139,Fusion404]
FEATURE [Part::MultiFuse] Fusion406
  Shapes = -> [Clone140,Cylinder080]
FEATURE [Part::MultiFuse] Fusion407  label="m3NutCut010"
  Placement = pos=(202.51,0,16.1) rot=(0.57735,0.57735,0.57735;4.18879rad)
  Shapes = -> [Clone141,Fusion406]
FEATURE [Part::MultiFuse] Fusion408  label="co2NutsCuts001"
  Placement = pos=(0,-6,0) rot=(0,0,1;0rad)
  Shapes = -> [Fusion407,Fusion405,Fusion403]
FEATURE [Part::MultiFuse] Fusion409
  Shapes = -> [Clone145,Clone144]
FEATURE [Part::MultiFuse] Fusion410  label="m2Cuts043"
  Placement = pos=(223.15,0,5.42) rot=(0.57735,0.57735,0.57735;4.18879rad)
  Shapes = -> [Cylinder082,Fusion409]
FEATURE [Part::MultiFuse] Fusion411  label="ipsM2NutCuts001"
  Placement = pos=(0,-6,0) rot=(0,0,1;0rad)
  Shapes = -> [Fusion410,Fusion387]
FEATURE [Part::MultiFuse] Fusion416  label="nutCutsForBase001"
  Shapes = -> [Fusion411,Fusion408,Cut039]
FEATURE [Part::MultiFuse] Fusion427
  Shapes = -> [Clone151,Clone150]
FEATURE [Part::MultiFuse] Fusion428  label="m2Cuts044"
  Placement = pos=(173.65,-6,40.16) rot=(0,-0.707107,-0.707107;3.14159rad)
  Shapes = -> [Cylinder083,Fusion427]
FEATURE [Part::MultiFuse] Fusion429
  Shapes = -> [Clone153,Clone152]
FEATURE [Part::MultiFuse] Fusion430  label="m2Cuts045"
  Placement = pos=(186.35,-6,40.16) rot=(0,0.707107,0.707107;3.14159rad)
  Shapes = -> [Cylinder084,Fusion429]
FEATURE [Part::MultiFuse] Fusion431  label="m2NutCuts009"
  Shapes = -> [Fusion428,Fusion430]
FEATURE [Part::MultiFuse] Fusion432
  Shapes = -> [Clone155,Clone154]
FEATURE [Part::MultiFuse] Fusion433  label="m2Cuts046"
  Placement = pos=(173.65,-6,40.16) rot=(0,0.707107,0.707107;3.14159rad)
  Shapes = -> [Cylinder085,Fusion432]
FEATURE [Part::MultiFuse] Fusion434
  Shapes = -> [Clone157,Clone156]
FEATURE [Part::MultiFuse] Fusion435  label="m2Cuts047"
  Placement = pos=(186.35,-6,40.16) rot=(0,0.707107,0.707107;3.14159rad)
  Shapes = -> [Cylinder086,Fusion434]
FEATURE [Part::MultiFuse] Fusion436  label="m2NutCuts010"
  Placement = pos=(0,0,-20.32) rot=(0,0,1;0rad)
  Shapes = -> [Fusion433,Fusion435]
FEATURE [Part::MultiFuse] Fusion437  label="m2NutCuts011"
  Shapes = -> [Fusion431,Fusion436]
FEATURE [Part::MultiFuse] Fusion438
  Shapes = -> [Clone159,Clone158]
FEATURE [Part::MultiFuse] Fusion439  label="m2Cuts048"
  Placement = pos=(173.65,-6,40.16) rot=(0,0.707107,0.707107;3.14159rad)
  Shapes = -> [Cylinder087,Fusion438]
FEATURE [Part::MultiFuse] Fusion440
  Shapes = -> [Clone161,Clone160]
FEATURE [Part::MultiFuse] Fusion441  label="m2Cuts049"
  Placement = pos=(186.35,-6,40.16) rot=(0,0.707107,0.707107;3.14159rad)
  Shapes = -> [Cylinder088,Fusion440]
FEATURE [Part::MultiFuse] Fusion442  label="m2NutCuts012"
  Shapes = -> [Fusion439,Fusion441]
FEATURE [Part::MultiFuse] Fusion443
  Shapes = -> [Clone163,Clone162]
FEATURE [Part::MultiFuse] Fusion444  label="m2Cuts050"
  Placement = pos=(173.65,-6,40.16) rot=(0,0.707107,0.707107;3.14159rad)
  Shapes = -> [Cylinder089,Fusion443]
FEATURE [Part::MultiFuse] Fusion445
  Shapes = -> [Clone165,Clone164]
FEATURE [Part::MultiFuse] Fusion446  label="m2Cuts051"
  Placement = pos=(186.35,-6,40.16) rot=(0,0.707107,0.707107;3.14159rad)
  Shapes = -> [Cylinder090,Fusion445]
FEATURE [Part::MultiFuse] Fusion447  label="m2NutCuts013"
  Placement = pos=(0,0,-20.32) rot=(0,0,1;0rad)
  Shapes = -> [Fusion444,Fusion446]
FEATURE [Part::MultiFuse] Fusion448  label="m2NutCuts014"
  Placement = pos=(45.25,0,0) rot=(0,0,1;0rad)
  Shapes = -> [Fusion442,Fusion447]
FEATURE [Part::MultiFuse] Fusion449
  Shapes = -> [Clone167,Clone166]
FEATURE [Part::MultiFuse] Fusion450  label="m2Cuts052"
  Placement = pos=(173.65,-6,40.16) rot=(0,0.707107,0.707107;3.14159rad)
  Shapes = -> [Cylinder091,Fusion449]
FEATURE [Part::MultiFuse] Fusion451
  Shapes = -> [Clone169,Clone168]
FEATURE [Part::MultiFuse] Fusion452  label="m2Cuts053"
  Placement = pos=(186.35,-6,40.16) rot=(0,0.707107,0.707107;3.14159rad)
  Shapes = -> [Cylinder092,Fusion451]
FEATURE [Part::MultiFuse] Fusion453  label="m2NutCuts015"
  Shapes = -> [Fusion450,Fusion452]
FEATURE [Part::MultiFuse] Fusion454
  Shapes = -> [Clone171,Clone170]
FEATURE [Part::MultiFuse] Fusion455  label="m2Cuts054"
  Placement = pos=(173.65,-6,40.16) rot=(0,0.707107,0.707107;3.14159rad)
  Shapes = -> [Cylinder093,Fusion454]
FEATURE [Part::MultiFuse] Fusion456
  Shapes = -> [Clone173,Clone172]
FEATURE [Part::MultiFuse] Fusion457  label="m2Cuts055"
  Placement = pos=(186.35,-6,40.16) rot=(0,0.707107,0.707107;3.14159rad)
  Shapes = -> [Cylinder094,Fusion456]
FEATURE [Part::MultiFuse] Fusion458  label="m2NutCuts016"
  Placement = pos=(0,0,-20.32) rot=(0,0,1;0rad)
  Shapes = -> [Fusion455,Fusion457]
FEATURE [Part::MultiFuse] Fusion459  label="m2NutCuts017"
  Placement = pos=(22.5,0,11.83) rot=(0,0,1;0rad)
  Shapes = -> [Fusion453,Fusion458]
FEATURE [Part::MultiFuse] Fusion460  label="ic2M2Mount001"
  Shapes = -> [Fusion437,Fusion448,Fusion459]
FEATURE [Sketcher::SketchObject] Sketch318
  ArcFitTolerance = 0
  FullyConstrained = true
  MakeInternals = false
  Placement = pos=(0,0,0) rot=(1,0,0;1.5708rad)
  sketch-geometry (4):
    g0: LineSegment StartX=158.5 StartY=80 StartZ=0 EndX=246.5 EndY=80 EndZ=0
    g1: LineSegment StartX=246.5 StartY=80 StartZ=0 EndX=246.5 EndY=-80 EndZ=0
    g2: LineSegment StartX=246.5 StartY=-80 StartZ=0 EndX=158.5 EndY=-80 EndZ=0
    g3: LineSegment StartX=158.5 StartY=-80 StartZ=0 EndX=158.5 EndY=80 EndZ=0
  constraints (12):
    c: Coincident(g0,g1)
    c: Coincident(g1,g2)
    c: Coincident(g2,g3)
    c: Coincident(g3,g0)
    c: Horizontal(g0)
    c: Horizontal(g2)
    c: Vertical(g1)
    c: Vertical(g3)
    c: DistanceY(g2) = -80
    c: DistanceY(g0) = 80
    c: DistanceX(g2) = 158.5
    c: DistanceX(g2,g2) = 88
FEATURE [Part::Extrusion] Extrude313  label="base031"
  Base = -> Sketch318
  Dir = (0,-1,2e-16)
  DirMode = 2
  FaceMakerClass = Part::FaceMakerBullseye
  FaceMakerMode = 3
  LengthFwd = 4
  LengthRev = 0
  Solid = true
  Symmetric = false
FEATURE [Sketcher::SketchObject] Sketch319
  ArcFitTolerance = 0
  FullyConstrained = true
  MakeInternals = false
  sketch-geometry (15):
    g0: LineSegment StartX=170 StartY=-4 StartZ=0 EndX=170 EndY=-42.5 EndZ=0
    g1: LineSegment StartX=170 StartY=-42.5 StartZ=0 EndX=183 EndY=-42.5 EndZ=0
    g2: LineSegment StartX=183 StartY=-42.5 StartZ=0 EndX=183 EndY=-18 EndZ=0
    g3: LineSegment StartX=183 StartY=-18 StartZ=0 EndX=222 EndY=-18 EndZ=0
    g4: LineSegment StartX=222 StartY=-18 StartZ=0 EndX=222 EndY=-42.5 EndZ=0
    g5: LineSegment StartX=222 StartY=-42.5 StartZ=0 EndX=235 EndY=-42.5 EndZ=0
    g6: LineSegment StartX=235 StartY=-42.5 StartZ=0 EndX=235 EndY=-4 EndZ=0
    g7: LineSegment StartX=235 StartY=-4 StartZ=0 EndX=170 EndY=-4 EndZ=0
    g8: Circle CenterX=178.54 CenterY=-14.55 CenterZ=0 NormalX=0 NormalY=0 NormalZ=1 AngleXU=0 Radius=1.125
    g9: Circle CenterX=178.54 CenterY=-34.85 CenterZ=0 NormalX=0 NormalY=0 NormalZ=1 AngleXU=0 Radius=1.125
    g10: Circle CenterX=225.89 CenterY=-34.85 CenterZ=0 NormalX=0 NormalY=0 NormalZ=1 AngleXU=0 Radius=1.125
    g11: Circle CenterX=225.89 CenterY=-14.55 CenterZ=0 NormalX=0 NormalY=0 NormalZ=1 AngleXU=0 Radius=1.125
    g12: Circle CenterX=198.84 CenterY=-14.55 CenterZ=0 NormalX=0 NormalY=0 NormalZ=1 AngleXU=0 Radius=1.125
    g13: Circle CenterX=208.09 CenterY=-14.55 CenterZ=0 NormalX=0 NormalY=0 NormalZ=1 AngleXU=0 Radius=1.125
    g14: Circle CenterX=191.24 CenterY=-14.55 CenterZ=0 NormalX=0 NormalY=0 NormalZ=1 AngleXU=0 Radius=1.125
  constraints (45):
    c: Vertical(g0)
    c: Coincident(g1,g0)
    c: Horizontal(g1)
    c: Coincident(g2,g1)
    c: Vertical(g2)
    c: Horizontal(g3)
    c: Coincident(g4,g3)
    c: Vertical(g4)
    c: Coincident(g5,g4)
    c: Coincident(g6,g5)
    c: Vertical(g6)
    c: Coincident(g7,g6)
    c: Coincident(g7,g0)
    c: Horizontal(g7)
    c: DistanceX(g0) = 170
    c: DistanceY(g0) = -4
    c: Horizontal(g5)
    c: DistanceX(g6) = 235
    c: DistanceX(g0,g2) = 13
    c: DistanceX(g3,g5) = 13
    c: Coincident(g2,g3)
    c: DistanceY(g2,g0) = 14
    c: DistanceY(g0,g0) = 38.5
    c: DistanceY(g4,g1) = 0
    c: Equal(g8,g11)
    c: Equal(g8,g10)
    c: Equal(g8,g9)
    c: Diameter(g8) = 2.25
    c: DistanceX(g9) = 178.54
    c: DistanceY(g9) = -34.85
    c: DistanceX(g8,g9) = 0
    c: DistanceY(g9,g8) = 20.3
    c: DistanceY(g8,g12) = 0
    c: DistanceX(g8,g12) = 20.3
    c: Equal(g12,g13)
    c: Diameter(g12) = 2.25
    c: Horizontal(g12,g13)
    c: Horizontal(g13,g11)
    c: Horizontal(g10,g9)
    c: Vertical(g10,g11)
    c: DistanceX(g9,g10) = 47.35
    c: DistanceX(g12,g13) = 9.25
    c: DistanceX(g8,g14) = 12.7
    c: Diameter(g14) = 2.25
    c: Horizontal(g14,g8)
FEATURE [Part::Extrusion] Extrude314  label="gpsMount001"
  Base = -> Sketch319
  Dir = (0,0,1)
  DirMode = 2
  FaceMakerClass = Part::FaceMakerBullseye
  FaceMakerMode = 3
  LengthFwd = 5
  LengthRev = 0
  Placement = pos=(0,0,60.5) rot=(0,0,1;0rad)
  Solid = true
  Symmetric = false
FEATURE [Sketcher::SketchObject] Sketch320
  ArcFitTolerance = 0
  FullyConstrained = true
  MakeInternals = false
  Placement = pos=(0,0,0) rot=(1,0,0;1.5708rad)
  sketch-geometry (6):
    g0: Circle CenterX=202.5 CenterY=16.1 CenterZ=0 NormalX=0 NormalY=0 NormalZ=1 AngleXU=0 Radius=1.625
    g1: Circle CenterX=202.5 CenterY=16.1 CenterZ=0 NormalX=0 NormalY=0 NormalZ=1 AngleXU=0 Radius=5
    g2: Circle CenterX=224.07 CenterY=53.45 CenterZ=0 NormalX=0 NormalY=0 NormalZ=1 AngleXU=0 Radius=5
    g3: Circle CenterX=180.93 CenterY=53.45 CenterZ=0 NormalX=0 NormalY=0 NormalZ=1 AngleXU=0 Radius=5
    g4: Circle CenterX=180.93 CenterY=53.45 CenterZ=0 NormalX=0 NormalY=0 NormalZ=1 AngleXU=0 Radius=1.625
    g5: Circle CenterX=224.07 CenterY=53.45 CenterZ=0 NormalX=0 NormalY=0 NormalZ=1 AngleXU=0 Radius=1.625
  constraints (15):
    c: DistanceX(g0) = 202.5
    c: DistanceY(g0) = 16.1
    c: Coincident(g0,g1)
    c: DistanceY(g3,g2) = 0
    c: Equal(g1,g2)
    c: Equal(g1,g3)
    c: Diameter(g1) = 10
    c: Equal(g0,g5)
    c: Equal(g0,g4)
    c: Diameter(g0) = 3.25
    c: DistanceY(g0,g3) = 37.35
    c: DistanceX(g3,g0) = 21.57
    c: DistanceX(g0,g2) = 21.57
    c: Coincident(g5,g2)
    c: Coincident(g4,g3)
FEATURE [Part::Extrusion] Extrude315  label="co2Mount001"
  Base = -> Sketch320
  Dir = (0,-1,2e-16)
  DirMode = 2
  FaceMakerClass = Part::FaceMakerBullseye
  FaceMakerMode = 3
  LengthFwd = 22
  LengthRev = 0
  Solid = true
  Symmetric = false
FEATURE [Sketcher::SketchObject] Sketch321
  ArcFitTolerance = 0
  FullyConstrained = true
  MakeInternals = false
  Placement = pos=(0,0,0) rot=(1,0,0;1.5708rad)
  sketch-geometry (4):
    g0: Circle CenterX=223.145 CenterY=5.42 CenterZ=0 NormalX=0 NormalY=0 NormalZ=1 AngleXU=0 Radius=1.125
    g1: Circle CenterX=182.125 CenterY=-31.13 CenterZ=0 NormalX=0 NormalY=0 NormalZ=1 AngleXU=0 Radius=1.125
    g2: Circle CenterX=182.125 CenterY=-31.13 CenterZ=0 NormalX=0 NormalY=0 NormalZ=1 AngleXU=0 Radius=5
    g3: Circle CenterX=223.145 CenterY=5.42 CenterZ=0 NormalX=0 NormalY=0 NormalZ=1 AngleXU=0 Radius=5
  constraints (10):
    c: DistanceX(g1) = 182.125
    c: DistanceY(g1) = -31.13
    c: DistanceX(g1,g0) = 41.02
    c: DistanceY(g1,g0) = 36.55
    c: Equal(g0,g1)
    c: Diameter(g0) = 2.25
    c: Equal(g3,g2)
    c: Diameter(g3) = 10
    c: Coincident(g2,g1)
    c: Coincident(g3,g0)
FEATURE [Part::Extrusion] Extrude316  label="base032"
  Base = -> Sketch321
  Dir = (0,-1,2e-16)
  DirMode = 2
  FaceMakerClass = Part::FaceMakerBullseye
  FaceMakerMode = 3
  LengthFwd = 18.75
  LengthRev = 0
  Solid = true
  Symmetric = false
FEATURE [Sketcher::SketchObject] Sketch322
  ArcFitTolerance = 0
  FullyConstrained = true
  MakeInternals = false
  Placement = pos=(0,0,0) rot=(1,0,0;1.5708rad)
  sketch-geometry (6):
    g0: LineSegment StartX=178.5 StartY=1.25 StartZ=0 EndX=215 EndY=-35.25 EndZ=0
    g1: LineSegment StartX=227 StartY=-23.25 StartZ=0 EndX=194.4 EndY=9.35 EndZ=0
    g2: LineSegment StartX=215 StartY=-35.25 StartZ=0 EndX=227 EndY=-35.25 EndZ=0
    g3: LineSegment StartX=227 StartY=-35.25 StartZ=0 EndX=227 EndY=-23.25 EndZ=0
    g4: LineSegment StartX=178.5 StartY=1.25 StartZ=0 EndX=178.5 EndY=9.35 EndZ=0
    g5: LineSegment StartX=178.5 StartY=9.35 StartZ=0 EndX=194.4 EndY=9.35 EndZ=0
  constraints (18):
    c: Angle(g0) = -0.785398
    c: Parallel(g1,g0)
    c: Coincident(g2,g0)
    c: Horizontal(g2)
    c: Coincident(g3,g2)
    c: Coincident(g3,g1)
    c: Vertical(g3)
    c: Coincident(g4,g0)
    c: Coincident(g5,g1)
    c: Horizontal(g5)
    c: Vertical(g4)
    c: Coincident(g4,g5)
    c: DistanceX(g2,g2) = 12
    c: DistanceY(g3,g3) = 12
    c: DistanceX(g2) = 227
    c: DistanceY(g2) = -35.25
    c: DistanceY(g4) = 9.35
    c: DistanceX(g0) = 178.5
FEATURE [Part::Extrusion] Extrude317  label="base033"
  Base = -> Sketch322
  Dir = (0,-1,2e-16)
  DirMode = 2
  FaceMakerClass = Part::FaceMakerBullseye
  FaceMakerMode = 3
  LengthFwd = 18.75
  LengthRev = 0
  Solid = true
  Symmetric = false
FEATURE [Part::MultiFuse] Fusion388  label="ipsMount003"
  Shapes = -> [Extrude316,Extrude317]
FEATURE [Sketcher::SketchObject] Sketch323
  ArcFitTolerance = 0
  FullyConstrained = true
  MakeInternals = false
  Placement = pos=(0,0,0) rot=(1,0,0;1.5708rad)
  sketch-geometry (12):
    g0: LineSegment StartX=215 StartY=-35.25 StartZ=0 EndX=227 EndY=-35.25 EndZ=0
    g1: LineSegment StartX=227 StartY=-35.25 StartZ=0 EndX=227 EndY=-23.25 EndZ=0
    g2: LineSegment StartX=178.5 StartY=1.25 StartZ=0 EndX=178.5 EndY=9.35 EndZ=0
    g3: LineSegment StartX=178.5 StartY=9.35 StartZ=0 EndX=194.4 EndY=9.35 EndZ=0
    g4: LineSegment StartX=178.5 StartY=1.25 StartZ=0 EndX=173 EndY=1.25 EndZ=0
    g5: LineSegment StartX=173 StartY=1.25 StartZ=0 EndX=173 EndY=11.25 EndZ=0
    g6: LineSegment StartX=173 StartY=11.25 StartZ=0 EndX=194.4 EndY=11.25 EndZ=0
    g7: LineSegment StartX=194.4 StartY=11.25 StartZ=0 EndX=194.4 EndY=9.35 EndZ=0
    g8: LineSegment StartX=215 StartY=-35.25 StartZ=0 EndX=215 EndY=-39.25 EndZ=0
    g9: LineSegment StartX=215 StartY=-39.25 StartZ=0 EndX=232 EndY=-39.25 EndZ=0
    g10: LineSegment StartX=232 StartY=-39.25 StartZ=0 EndX=232 EndY=-23.25 EndZ=0
    g11: LineSegment StartX=232 StartY=-23.25 StartZ=0 EndX=227 EndY=-23.25 EndZ=0
  constraints (36):
    c: Horizontal(g0)
    c: Coincident(g1,g0)
    c: Vertical(g1)
    c: Horizontal(g3)
    c: Vertical(g2)
    c: Coincident(g2,g3)
    c: DistanceX(g0,g0) = 12
    c: DistanceY(g1,g1) = 12
    c: DistanceX(g0) = 227
    c: DistanceY(g0) = -35.25
    c: DistanceY(g2) = 9.35
    c: DistanceX(g2) = 178.5
    c: DistanceX(g2,g3) = 15.9
    c: DistanceY(g2,g3) = 8.1
    c: Coincident(g4,g2)
    c: Horizontal(g4)
    c: Coincident(g5,g4)
    c: Vertical(g5)
    c: Coincident(g6,g5)
    c: Horizontal(g6)
    c: Coincident(g7,g6)
    c: Coincident(g7,g3)
    c: Vertical(g7)
    c: DistanceY(g5,g5) = 10
    c: DistanceX(g4,g4) = 5.5
    c: Coincident(g8,g0)
    c: Vertical(g8)
    c: Coincident(g9,g8)
    c: Horizontal(g9)
    c: Coincident(g10,g9)
    c: Coincident(g11,g10)
    c: Coincident(g11,g1)
    c: Horizontal(g11)
    c: Vertical(g10)
    c: DistanceY(g8,g8) = 4
    c: DistanceX(g11,g11) = 5
FEATURE [Part::Extrusion] Extrude318  label="ipsMount002"
  Base = -> Sketch323
  Dir = (0,-1,2e-16)
  DirMode = 2
  FaceMakerClass = Part::FaceMakerBullseye
  FaceMakerMode = 3
  LengthFwd = 22
  LengthRev = 0
  Solid = true
  Symmetric = false
FEATURE [Part::MultiFuse] Fusion415  label="base037"
  Shapes = -> [Extrude318,Fusion388,Extrude315,Extrude314,Extrude313]
FEATURE [Sketcher::SketchObject] Sketch324
  ArcFitTolerance = 0
  FullyConstrained = true
  MakeInternals = false
  Placement = pos=(0,-4,0) rot=(1,0,0;1.5708rad)
  sketch-geometry (5):
    g0: LineSegment StartX=178.5 StartY=1.25 StartZ=0 EndX=202.5 EndY=1.25 EndZ=0
    g1: LineSegment StartX=178.5 StartY=1.25 StartZ=0 EndX=215 EndY=-35.25 EndZ=0
    g2: LineSegment StartX=215 StartY=-35.25 StartZ=0 EndX=227 EndY=-35.25 EndZ=0
    g3: LineSegment StartX=227 StartY=-35.25 StartZ=0 EndX=227 EndY=-23.25 EndZ=0
    g4: LineSegment StartX=227 StartY=-23.25 StartZ=0 EndX=202.5 EndY=1.25 EndZ=0
  constraints (15):
    c: Coincident(g2,g1)
    c: Horizontal(g2)
    c: Coincident(g3,g2)
    c: Vertical(g3)
    c: Coincident(g4,g3)
    c: Coincident(g4,g0)
    c: Horizontal(g0)
    c: DistanceX(g0) = 178.5
    c: DistanceY(g0) = 1.25
    c: Coincident(g0,g1)
    c: Angle(g1) = -0.785398
    c: DistanceX(g2) = 227
    c: Angle(g4) = 2.35619
    c: DistanceY(g3) = -23.25
    c: DistanceY(g1) = -35.25
FEATURE [Part::Extrusion] Extrude319  label="ipsCut001"
  Base = -> Sketch324
  Dir = (0,-1,2e-16)
  DirMode = 2
  FaceMakerClass = Part::FaceMakerBullseye
  FaceMakerMode = 3
  LengthFwd = 11
  LengthRev = 0
  Solid = true
  Symmetric = false
FEATURE [Sketcher::SketchObject] Sketch325
  ArcFitTolerance = 0
  FullyConstrained = true
  MakeInternals = false
  Placement = pos=(229.5,0,0) rot=(0.57735,0.57735,0.57735;2.0944rad)
  sketch-geometry (5):
    g0: ArcOfCircle CenterX=-8 CenterY=74 CenterZ=0 NormalX=0 NormalY=0 NormalZ=1 AngleXU=0 Radius=6 StartAngle=1.5708 EndAngle=4.71239
    g1: LineSegment StartX=-8 StartY=68 StartZ=0 EndX=-4 EndY=68 EndZ=0
    g2: LineSegment StartX=-4 StartY=68 StartZ=0 EndX=-4 EndY=80 EndZ=0
    g3: LineSegment StartX=-4 StartY=80 StartZ=0 EndX=-8 EndY=80 EndZ=0
    g4: Circle CenterX=-8 CenterY=74 CenterZ=0 NormalX=0 NormalY=0 NormalZ=1 AngleXU=0 Radius=1.65
  constraints (15):
    c: Vertical(g0,g0)
    c: Vertical(g0,g0)
    c: DistanceY(g0) = 74
    c: DistanceX(g0) = -8
    c: Diameter(g0) = 12
    c: Coincident(g1,g0)
    c: Horizontal(g1)
    c: Coincident(g2,g1)
    c: Vertical(g2)
    c: Coincident(g3,g2)
    c: Coincident(g3,g0)
    c: Horizontal(g3)
    c: DistanceX(g1,g1) = 4
    c: Coincident(g4,g0)
    c: Diameter(g4) = 3.3
FEATURE [Part::Extrusion] Extrude320
  Base = -> Sketch325
  Dir = (1,0,0)
  DirMode = 2
  FaceMakerClass = Part::FaceMakerBullseye
  FaceMakerMode = 3
  LengthFwd = 5.5
  LengthRev = 0
  Placement = pos=(-59.5,0,0) rot=(0,0,1;0rad)
  Solid = true
  Symmetric = false
FEATURE [Part::Cut] Cut040
  Base = -> Extrude320
  Placement = pos=(0,0,-1) rot=(0,0,1;0rad)
  Tool = -> Clone146
FEATURE [Sketcher::SketchObject] Sketch326
  ArcFitTolerance = 0
  FullyConstrained = true
  MakeInternals = false
  Placement = pos=(229.5,0,0) rot=(0.57735,0.57735,0.57735;2.0944rad)
  sketch-geometry (5):
    g0: ArcOfCircle CenterX=-8 CenterY=74 CenterZ=0 NormalX=0 NormalY=0 NormalZ=1 AngleXU=0 Radius=6 StartAngle=1.5708 EndAngle=4.71239
    g1: LineSegment StartX=-8 StartY=68 StartZ=0 EndX=-4 EndY=68 EndZ=0
    g2: LineSegment StartX=-4 StartY=68 StartZ=0 EndX=-4 EndY=80 EndZ=0
    g3: LineSegment StartX=-4 StartY=80 StartZ=0 EndX=-8 EndY=80 EndZ=0
    g4: Circle CenterX=-8 CenterY=74 CenterZ=0 NormalX=0 NormalY=0 NormalZ=1 AngleXU=0 Radius=1.65
  constraints (15):
    c: Vertical(g0,g0)
    c: Vertical(g0,g0)
    c: DistanceY(g0) = 74
    c: DistanceX(g0) = -8
    c: Diameter(g0) = 12
    c: Coincident(g1,g0)
    c: Horizontal(g1)
    c: Coincident(g2,g1)
    c: Vertical(g2)
    c: Coincident(g3,g2)
    c: Coincident(g3,g0)
    c: Horizontal(g3)
    c: DistanceX(g1,g1) = 4
    c: Coincident(g4,g0)
    c: Diameter(g4) = 3.3
FEATURE [Part::Extrusion] Extrude321
  Base = -> Sketch326
  Dir = (1,0,0)
  DirMode = 2
  FaceMakerClass = Part::FaceMakerBullseye
  FaceMakerMode = 3
  LengthFwd = 5.5
  LengthRev = 0
  Placement = pos=(-59.5,0,0) rot=(0,0,1;0rad)
  Solid = true
  Symmetric = false
FEATURE [Part::Cut] Cut041
  Base = -> Extrude321
  Placement = pos=(405,0,147) rot=(0,1,0;3.14159rad)
  Tool = -> Clone147
FEATURE [Part::MultiFuse] Fusion412  label="baseSrsHolder004"
  Shapes = -> [Cut041,Cut040]
FEATURE [Sketcher::SketchObject] Sketch327
  ArcFitTolerance = 0
  FullyConstrained = true
  MakeInternals = false
  Placement = pos=(229.5,0,0) rot=(0.57735,0.57735,0.57735;2.0944rad)
  sketch-geometry (5):
    g0: ArcOfCircle CenterX=-8 CenterY=74 CenterZ=0 NormalX=0 NormalY=0 NormalZ=1 AngleXU=0 Radius=6 StartAngle=1.5708 EndAngle=4.71239
    g1: LineSegment StartX=-8 StartY=68 StartZ=0 EndX=-4 EndY=68 EndZ=0
    g2: LineSegment StartX=-4 StartY=68 StartZ=0 EndX=-4 EndY=80 EndZ=0
    g3: LineSegment StartX=-4 StartY=80 StartZ=0 EndX=-8 EndY=80 EndZ=0
    g4: Circle CenterX=-8 CenterY=74 CenterZ=0 NormalX=0 NormalY=0 NormalZ=1 AngleXU=0 Radius=1.65
  constraints (15):
    c: Vertical(g0,g0)
    c: Vertical(g0,g0)
    c: DistanceY(g0) = 74
    c: DistanceX(g0) = -8
    c: Diameter(g0) = 12
    c: Coincident(g1,g0)
    c: Horizontal(g1)
    c: Coincident(g2,g1)
    c: Vertical(g2)
    c: Coincident(g3,g2)
    c: Coincident(g3,g0)
    c: Horizontal(g3)
    c: DistanceX(g1,g1) = 4
    c: Coincident(g4,g0)
    c: Diameter(g4) = 3.3
FEATURE [Part::Extrusion] Extrude322
  Base = -> Sketch327
  Dir = (1,0,0)
  DirMode = 2
  FaceMakerClass = Part::FaceMakerBullseye
  FaceMakerMode = 3
  LengthFwd = 5.5
  LengthRev = 0
  Placement = pos=(-59.5,0,0) rot=(0,0,1;0rad)
  Solid = true
  Symmetric = false
FEATURE [Part::Cut] Cut042
  Base = -> Extrude322
  Placement = pos=(0,0,-1) rot=(0,0,1;0rad)
  Tool = -> Clone148
FEATURE [Sketcher::SketchObject] Sketch328
  ArcFitTolerance = 0
  FullyConstrained = true
  MakeInternals = false
  Placement = pos=(229.5,0,0) rot=(0.57735,0.57735,0.57735;2.0944rad)
  sketch-geometry (5):
    g0: ArcOfCircle CenterX=-8 CenterY=74 CenterZ=0 NormalX=0 NormalY=0 NormalZ=1 AngleXU=0 Radius=6 StartAngle=1.5708 EndAngle=4.71239
    g1: LineSegment StartX=-8 StartY=68 StartZ=0 EndX=-4 EndY=68 EndZ=0
    g2: LineSegment StartX=-4 StartY=68 StartZ=0 EndX=-4 EndY=80 EndZ=0
    g3: LineSegment StartX=-4 StartY=80 StartZ=0 EndX=-8 EndY=80 EndZ=0
    g4: Circle CenterX=-8 CenterY=74 CenterZ=0 NormalX=0 NormalY=0 NormalZ=1 AngleXU=0 Radius=1.65
  constraints (15):
    c: Vertical(g0,g0)
    c: Vertical(g0,g0)
    c: DistanceY(g0) = 74
    c: DistanceX(g0) = -8
    c: Diameter(g0) = 12
    c: Coincident(g1,g0)
    c: Horizontal(g1)
    c: Coincident(g2,g1)
    c: Vertical(g2)
    c: Coincident(g3,g2)
    c: Coincident(g3,g0)
    c: Horizontal(g3)
    c: DistanceX(g1,g1) = 4
    c: Coincident(g4,g0)
    c: Diameter(g4) = 3.3
FEATURE [Part::Extrusion] Extrude323
  Base = -> Sketch328
  Dir = (1,0,0)
  DirMode = 2
  FaceMakerClass = Part::FaceMakerBullseye
  FaceMakerMode = 3
  LengthFwd = 5.5
  LengthRev = 0
  Placement = pos=(-59.5,0,0) rot=(0,0,1;0rad)
  Solid = true
  Symmetric = false
FEATURE [Part::Cut] Cut043
  Base = -> Extrude323
  Placement = pos=(405,0,147) rot=(0,1,0;3.14159rad)
  Tool = -> Clone149
FEATURE [Part::MultiFuse] Fusion413  label="baseSrsHolder005"
  Placement = pos=(0,0,-90) rot=(0,0,1;0rad)
  Shapes = -> [Cut043,Cut042]
FEATURE [Part::MultiFuse] Fusion414  label="srsHoldsForTheBase003"
  Shapes = -> [Fusion412,Fusion413]
FEATURE [Sketcher::SketchObject] Sketch329
  ArcFitTolerance = 0
  FullyConstrained = true
  MakeInternals = false
  Placement = pos=(170,0,0) rot=(0.57735,0.57735,0.57735;2.0944rad)
  sketch-geometry (4):
    g0: LineSegment StartX=-14 StartY=80.15 StartZ=0 EndX=-4 EndY=80.15 EndZ=0
    g1: LineSegment StartX=-4 StartY=80.15 StartZ=0 EndX=-4 EndY=76.95 EndZ=0
    g2: LineSegment StartX=-4 StartY=76.95 StartZ=0 EndX=-14 EndY=76.95 EndZ=0
    g3: LineSegment StartX=-14 StartY=76.95 StartZ=0 EndX=-14 EndY=80.15 EndZ=0
  constraints (12):
    c: Coincident(g0,g1)
    c: Coincident(g1,g2)
    c: Coincident(g2,g3)
    c: Coincident(g3,g0)
    c: Horizontal(g0)
    c: Horizontal(g2)
    c: Vertical(g1)
    c: Vertical(g3)
    c: DistanceY(g2) = 76.95
    c: DistanceY(g3,g3) = 3.2
    c: DistanceX(g2,g2) = 10
    c: DistanceX(g2) = -14
FEATURE [Part::Extrusion] Extrude324  label="srsCut004"
  Base = -> Sketch329
  Dir = (1,0,0)
  DirMode = 2
  FaceMakerClass = Part::FaceMakerBullseye
  FaceMakerMode = 3
  LengthFwd = 65
  LengthRev = 0
  Solid = true
  Symmetric = false
FEATURE [Part::Cut] Cut044  label="srsHoldsForTheBase002"
  Base = -> Fusion414
  Tool = -> Extrude324
FEATURE [Sketcher::SketchObject] Sketch330
  ArcFitTolerance = 0
  FullyConstrained = true
  MakeInternals = false
  Placement = pos=(0,13,0) rot=(1,0,0;1.5708rad)
  sketch-geometry (6):
    g0: Circle CenterX=163 CenterY=63 CenterZ=0 NormalX=0 NormalY=0 NormalZ=1 AngleXU=0 Radius=1.625
    g1: Circle CenterX=242 CenterY=63 CenterZ=0 NormalX=0 NormalY=0 NormalZ=1 AngleXU=0 Radius=1.625
    g2: Circle CenterX=163 CenterY=-27 CenterZ=0 NormalX=0 NormalY=0 NormalZ=1 AngleXU=0 Radius=1.625
    g3: Circle CenterX=242 CenterY=-27 CenterZ=0 NormalX=0 NormalY=0 NormalZ=1 AngleXU=0 Radius=1.625
    g4: Circle CenterX=163 CenterY=-63 CenterZ=0 NormalX=0 NormalY=0 NormalZ=1 AngleXU=0 Radius=1.625
    g5: Circle CenterX=242 CenterY=-63 CenterZ=0 NormalX=0 NormalY=0 NormalZ=1 AngleXU=0 Radius=1.625
  constraints (18):
    c: Horizontal(g0,g1)
    c: DistanceX(g0) = 163
    c: DistanceY(g0) = 63
    c: DistanceX(g0,g1) = 79
    c: Horizontal(g2,g3)
    c: Equal(g2,g3)
    c: Equal(g2,g1)
    c: Equal(g2,g0)
    c: Diameter(g2) = 3.25
    c: DistanceY(g2,g0) = 90
    c: Vertical(g3,g1)
    c: Vertical(g2,g0)
    c: Vertical(g2,g4)
    c: Vertical(g5,g3)
    c: Equal(g4,g5)
    c: Diameter(g4) = 3.25
    c: DistanceY(g4,g2) = 36
    c: Horizontal(g5,g4)
FEATURE [Part::Extrusion] Extrude325  label="srsCutsForM3s004"
  Base = -> Sketch330
  Dir = (0,-1,2e-16)
  DirMode = 2
  FaceMakerClass = Part::FaceMakerBullseye
  FaceMakerMode = 3
  LengthFwd = 17
  LengthRev = 0
  Solid = true
  Symmetric = false
FEATURE [Part::MultiFuse] Fusion417  label="baseCuts002"
  Shapes = -> [Fusion416,Extrude325,Extrude319]
FEATURE [Part::Cut] Cut045  label="base026"
  Base = -> Fusion415
  Tool = -> Fusion417
FEATURE [Part::MultiFuse] Fusion418  label="base038"
  Shapes = -> [Cut044,Cut045]
FEATURE [Sketcher::SketchObject] Sketch331  label="outerSRS027"
  ArcFitTolerance = 0
  FullyConstrained = true
  MakeInternals = false
  Placement = pos=(0,0,-80) rot=(0,0,1;0rad)
  sketch-geometry (6):
    g0: LineSegment StartX=165 StartY=0 StartZ=0 EndX=165 EndY=-18 EndZ=0
    g1: LineSegment StartX=184 StartY=-37 StartZ=0 EndX=221 EndY=-37 EndZ=0
    g2: LineSegment StartX=240 StartY=0 StartZ=0 EndX=240 EndY=-18 EndZ=0
    g3: ArcOfCircle CenterX=184 CenterY=-18 CenterZ=0 NormalX=0 NormalY=0 NormalZ=1 AngleXU=0 Radius=19 StartAngle=3.14159 EndAngle=4.71239
    g4: ArcOfCircle CenterX=221 CenterY=-18 CenterZ=0 NormalX=0 NormalY=0 NormalZ=1 AngleXU=0 Radius=19 StartAngle=4.71239 EndAngle=6.28319
    g5: LineSegment StartX=165 StartY=0 StartZ=0 EndX=240 EndY=0 EndZ=0
  constraints (20):
    c: PointOnObject(g5,g-1)
    c: Vertical(g0)
    c: Horizontal(g1)
    c: Vertical(g2)
    c: DistanceY(g2,g5) = 0
    c: Coincident(g0,g3)
    c: Coincident(g1,g3)
    c: Coincident(g1,g4)
    c: Coincident(g2,g4)
    c: Angle(g3) = 1.5708
    c: Angle(g4) = 1.5708
    c: Coincident(g5,g2)
    c: DistanceX(g0) = 165
    c: Coincident(g5,g0)
    c: DistanceX(g0,g2) = 75
    c: DistanceY(g0,g0) = 18
    c: DistanceY(g2,g0) = 0
    c: DistanceY(g3,g0) = 0
    c: DistanceY(g4,g2) = 0
    c: DistanceX(g0,g3) = 19
FEATURE [Part::Extrusion] Extrude326
  Base = -> Sketch331
  Dir = (0,0,1)
  DirMode = 2
  FaceMakerClass = Part::FaceMakerBullseye
  FaceMakerMode = 3
  LengthFwd = 4
  LengthRev = 0
  Solid = true
  Symmetric = false
FEATURE [Part::Fillet] Fillet073  label="piCoverBottom003"
  Base = -> Extrude326
  EdgeLinks = -> Extrude326 [Edge3,Edge6,Edge9,Edge12,Edge15,Edge17,Edge18]
  Edges = 7 edges r=1: [Edge3,Edge6,Edge9,Edge12,Edge15,Edge17,Edge18]
FEATURE [Part::MultiFuse] Fusion419  label="base039"
  Shapes = -> [Fusion418,Fillet073]
FEATURE [Sketcher::SketchObject] Sketch332
  ArcFitTolerance = 0
  FullyConstrained = true
  MakeInternals = false
  MapMode = 2
  sketch-geometry (10):
    g0: LineSegment StartX=63 StartY=9.25 StartZ=0 EndX=74 EndY=9.25 EndZ=0
    g1: LineSegment StartX=74 StartY=9.25 StartZ=0 EndX=74 EndY=2 EndZ=0
    g2: LineSegment StartX=74 StartY=2 StartZ=0 EndX=63 EndY=2 EndZ=0
    g3: LineSegment StartX=63 StartY=2 StartZ=0 EndX=63 EndY=9.25 EndZ=0
    g4: LineSegment StartX=-1 StartY=9.25 StartZ=0 EndX=10 EndY=9.25 EndZ=0
    g5: LineSegment StartX=10 StartY=9.25 StartZ=0 EndX=10 EndY=2 EndZ=0
    g6: LineSegment StartX=10 StartY=2 StartZ=0 EndX=-1 EndY=2 EndZ=0
    g7: LineSegment StartX=-1 StartY=2 StartZ=0 EndX=-1 EndY=9.25 EndZ=0
    g8: Circle CenterX=7.47 CenterY=6.47 CenterZ=0 NormalX=0 NormalY=0 NormalZ=1 AngleXU=0 Radius=1.35
    g9: Circle CenterX=65.52 CenterY=6.47 CenterZ=0 NormalX=0 NormalY=0 NormalZ=1 AngleXU=0 Radius=1.35
  constraints (30):
    c: Coincident(g0,g1)
    c: Coincident(g1,g2)
    c: Coincident(g2,g3)
    c: Coincident(g3,g0)
    c: Horizontal(g0)
    c: Horizontal(g2)
    c: Vertical(g1)
    c: Vertical(g3)
    c: Coincident(g4,g5)
    c: Coincident(g5,g6)
    c: Coincident(g6,g7)
    c: Coincident(g7,g4)
    c: Horizontal(g4)
    c: Horizontal(g6)
    c: Vertical(g5)
    c: Vertical(g7)
    c: DistanceY(g6) = 2
    c: DistanceY(g7,g7) = 7.25
    c: DistanceY(g2,g5) = 0
    c: DistanceY(g0,g4) = 0
    c: DistanceX(g2,g2) = 11
    c: DistanceX(g8) = 7.47
    c: Radius(g8) = 1.35
    c: DistanceX(g9) = 65.52
    c: DistanceY(g8,g9) = 0
    c: Radius(g9) = 1.35
    c: DistanceY(g8) = 6.47
    c: DistanceX(g5,g2) = 53
    c: DistanceX(g2,g9) = 2.52
    c: DistanceX(g6,g6) = 11
FEATURE [Part::Extrusion] Extrude327  label="RaberryPiHold008"
  Base = -> Sketch332
  Dir = (0,0,1)
  DirMode = 2
  FaceMakerClass = Part::FaceMakerBullseye
  FaceMakerMode = 3
  LengthFwd = 2
  LengthRev = 0
  Placement = pos=(0,0,20.7) rot=(0,0,1;0rad)
  Solid = true
  Symmetric = false
FEATURE [Part::Fillet] Fillet074  label="piHoldBottomInDone008"
  Base = -> Extrude327
  EdgeLinks = -> Extrude327 [Edge1,Edge4,Edge12,Edge17,Edge19,Edge22]
  Edges = 6 edges: [Edge1 r=2,Edge4 r=1,Edge12 r=1,Edge17 r=2,Edge19 r=1,Edge22 r=1]
FEATURE [Part::Compound] Compound020  label="wearableHolds002"
  Links = -> [Fillet074]
  Placement = pos=(72,9.5,-78) rot=(1,0,0;1.5708rad)
FEATURE [Sketcher::SketchObject] Sketch333
  ArcFitTolerance = 0
  FullyConstrained = true
  MakeInternals = false
  Placement = pos=(0,0,0) rot=(1,0,0;1.5708rad)
  sketch-geometry (12):
    g0: LineSegment StartX=79.5 StartY=-51.5 StartZ=0 EndX=74 EndY=-51.5 EndZ=0
    g1: LineSegment StartX=74 StartY=-51.5 StartZ=0 EndX=74 EndY=-43.5 EndZ=0
    g2: LineSegment StartX=74 StartY=-43.5 StartZ=0 EndX=82.5 EndY=-43.5 EndZ=0
    g3: LineSegment StartX=82.5 StartY=-43.5 StartZ=0 EndX=82.5 EndY=-48.5 EndZ=0
    g4: ArcOfCircle CenterX=79.5 CenterY=-48.5 CenterZ=0 NormalX=0 NormalY=0 NormalZ=1 AngleXU=0 Radius=3 StartAngle=4.71239 EndAngle=6.28319
    g5: Circle CenterX=79.5 CenterY=-48.5 CenterZ=0 NormalX=0 NormalY=0 NormalZ=1 AngleXU=0 Radius=1.75
    g6: LineSegment StartX=142.75 StartY=-51.25 StartZ=0 EndX=137.5 EndY=-51.25 EndZ=0
    g7: LineSegment StartX=142.75 StartY=-43.5 StartZ=0 EndX=134.75 EndY=-43.5 EndZ=0
    g8: LineSegment StartX=134.75 StartY=-43.5 StartZ=0 EndX=134.75 EndY=-48.5 EndZ=0
    g9: ArcOfCircle CenterX=137.5 CenterY=-48.5 CenterZ=0 NormalX=0 NormalY=0 NormalZ=1 AngleXU=0 Radius=2.75 StartAngle=3.14159 EndAngle=4.71239
    g10: LineSegment StartX=142.75 StartY=-51.25 StartZ=0 EndX=142.75 EndY=-43.5 EndZ=0
    g11: Circle CenterX=137.5 CenterY=-48.5 CenterZ=0 NormalX=0 NormalY=0 NormalZ=1 AngleXU=0 Radius=1.75
  constraints (36):
    c: Horizontal(g0)
    c: Coincident(g1,g0)
    c: Vertical(g1)
    c: Coincident(g2,g1)
    c: Horizontal(g2)
    c: Coincident(g3,g2)
    c: Vertical(g3)
    c: Coincident(g4,g3)
    c: Angle(g4) = 1.5708
    c: Coincident(g0,g4)
    c: DistanceY(g0) = -51.5
    c: Vertical(g0,g4)
    c: DistanceX(g4) = 79.5
    c: DistanceY(g4) = -48.5
    c: DistanceX(g0) = 74
    c: Coincident(g5,g4)
    c: Diameter(g5) = 3.5
    c: Horizontal(g6)
    c: Horizontal(g7)
    c: Coincident(g8,g7)
    c: Vertical(g8)
    c: Coincident(g9,g6)
    c: Coincident(g9,g8)
    c: Horizontal(g9,g4)
    c: DistanceX(g4,g9) = 58
    c: Coincident(g10,g6)
    c: Coincident(g10,g7)
    c: Vertical(g10)
    c: Angle(g9) = 1.5708
    c: Horizontal(g9,g8)
    c: Diameter(g9) = 5.5
    c: Coincident(g11,g9)
    c: Diameter(g11) = 3.5
    c: DistanceY(g1,g1) = 8
    c: DistanceY(g2,g7) = 0
    c: DistanceX(g7,g6) = 8
FEATURE [Part::Extrusion] Extrude328  label="piZeroHolds002"
  Base = -> Sketch333
  Dir = (0,-1,2e-16)
  DirMode = 2
  FaceMakerClass = Part::FaceMakerBullseye
  FaceMakerMode = 3
  LengthFwd = 7
  LengthRev = 0
  Solid = true
  Symmetric = false
FEATURE [App::Part] Part006  label="piZeroParts001Holds001"
  Group = -> [Sketch333,Extrude328,Extrude327,Fillet074,Sketch332,Compound020]
  Origin = -> Origin029
  Placement = pos=(94,-4,0) rot=(0,0,1;0rad)
FEATURE [Part::MultiFuse] Fusion423  label="base040"
  Shapes = -> [Fusion419,Part006]
FEATURE [Sketcher::SketchObject] Sketch334
  ArcFitTolerance = 0
  FullyConstrained = true
  MakeInternals = false
  Placement = pos=(0,0,0) rot=(1,0,0;1.5708rad)
  sketch-geometry (46):
    g0: LineSegment StartX=11.75 StartY=19.5 StartZ=0 EndX=21.5 EndY=19.5 EndZ=0
    g1: LineSegment StartX=21.5 StartY=19.5 StartZ=0 EndX=23.75 EndY=22 EndZ=0
    g2: LineSegment StartX=23.75 StartY=22 StartZ=0 EndX=23.75 EndY=25 EndZ=0
    g3: LineSegment StartX=23.75 StartY=25 StartZ=0 EndX=9.5 EndY=25 EndZ=0
    g4: LineSegment StartX=9.5 StartY=25 StartZ=0 EndX=9.5 EndY=22 EndZ=0
    g5: LineSegment StartX=40 StartY=24.5 StartZ=0 EndX=40 EndY=22 EndZ=0
    g6: LineSegment StartX=40 StartY=22 StartZ=0 EndX=42.5 EndY=19.5 EndZ=0
    g7: LineSegment StartX=42.5 StartY=19.5 StartZ=0 EndX=48.7 EndY=19.5 EndZ=0
    g8: LineSegment StartX=48.7 StartY=19.5 StartZ=0 EndX=51.2 EndY=22 EndZ=0
    g9: LineSegment StartX=51.2 StartY=22 StartZ=0 EndX=51.2 EndY=24.5 EndZ=0
    g10: LineSegment StartX=51.2 StartY=24.5 StartZ=0 EndX=40 EndY=24.5 EndZ=0
    g11: LineSegment StartX=52.45 StartY=24.5 StartZ=0 EndX=52.45 EndY=22 EndZ=0
    g12: LineSegment StartX=52.45 StartY=22 StartZ=0 EndX=54.95 EndY=19.5 EndZ=0
    g13: LineSegment StartX=54.95 StartY=19.5 StartZ=0 EndX=61.15 EndY=19.5 EndZ=0
    g14: LineSegment StartX=61.15 StartY=19.5 StartZ=0 EndX=63.65 EndY=22 EndZ=0
    g15: LineSegment StartX=63.65 StartY=22 StartZ=0 EndX=63.65 EndY=24.5 EndZ=0
    g16: LineSegment StartX=63.65 StartY=24.5 StartZ=0 EndX=52.45 EndY=24.5 EndZ=0
    g17: LineSegment StartX=9.5 StartY=22 StartZ=0 EndX=11.75 EndY=19.5 EndZ=0
    g18: ArcOfCircle CenterX=12.3 CenterY=15.45 CenterZ=0 NormalX=0 NormalY=0 NormalZ=1 AngleXU=0 Radius=1 StartAngle=1.5708 EndAngle=3.14159
    g19: LineSegment StartX=11.3 StartY=15.45 StartZ=0 EndX=11.3 EndY=14.2 EndZ=0
    g20: LineSegment StartX=12.3 StartY=16.45 StartZ=0 EndX=16.8 EndY=16.45 EndZ=0
    g21: ArcOfCircle CenterX=16.8 CenterY=15.45 CenterZ=0 NormalX=0 NormalY=0 NormalZ=1 AngleXU=0 Radius=1 StartAngle=3e-16 EndAngle=1.5708
    g22: ArcOfCircle CenterX=16.8 CenterY=14.2 CenterZ=0 NormalX=0 NormalY=0 NormalZ=1 AngleXU=0 Radius=1 StartAngle=4.71239 EndAngle=6.28319
    g23: ArcOfCircle CenterX=12.3 CenterY=14.2 CenterZ=0 NormalX=0 NormalY=0 NormalZ=1 AngleXU=0 Radius=1 StartAngle=3.14159 EndAngle=4.71239
    g24: LineSegment StartX=12.3 StartY=13.2 StartZ=0 EndX=16.8 EndY=13.2 EndZ=0
    g25: LineSegment StartX=17.8 StartY=15.45 StartZ=0 EndX=17.8 EndY=14.2 EndZ=0
    g26: Circle CenterX=18.9 CenterY=16.475 CenterZ=0 NormalX=0 NormalY=0 NormalZ=1 AngleXU=0 Radius=0.5
    g27: Circle CenterX=21.09 CenterY=16.475 CenterZ=0 NormalX=0 NormalY=0 NormalZ=1 AngleXU=0 Radius=0.5
    g28: Circle CenterX=23.28 CenterY=16.475 CenterZ=0 NormalX=0 NormalY=0 NormalZ=1 AngleXU=0 Radius=0.5
    g29: Circle CenterX=25.47 CenterY=16.475 CenterZ=0 NormalX=0 NormalY=0 NormalZ=1 AngleXU=0 Radius=0.5
    g30: LineSegment StartX=44.8 StartY=16.45 StartZ=0 EndX=49.3 EndY=16.45 EndZ=0
    g31: LineSegment StartX=50.3 StartY=15.45 StartZ=0 EndX=50.3 EndY=14.2 EndZ=0
    g32: LineSegment StartX=49.3 StartY=13.2 StartZ=0 EndX=44.8 EndY=13.2 EndZ=0
    g33: LineSegment StartX=43.8 StartY=15.45 StartZ=0 EndX=43.8 EndY=14.2 EndZ=0
    g34: ArcOfCircle CenterX=44.8 CenterY=15.45 CenterZ=0 NormalX=0 NormalY=0 NormalZ=1 AngleXU=0 Radius=1 StartAngle=1.5708 EndAngle=3.14159
    g35: ArcOfCircle CenterX=49.3 CenterY=15.45 CenterZ=0 NormalX=0 NormalY=0 NormalZ=1 AngleXU=0 Radius=1 StartAngle=3e-16 EndAngle=1.5708
    g36: ArcOfCircle CenterX=49.3 CenterY=14.2 CenterZ=0 NormalX=0 NormalY=0 NormalZ=1 AngleXU=0 Radius=1 StartAngle=4.71239 EndAngle=6.28319
    g37: ArcOfCircle CenterX=44.8 CenterY=14.2 CenterZ=0 NormalX=0 NormalY=0 NormalZ=1 AngleXU=0 Radius=1 StartAngle=3.14159 EndAngle=4.71239
    g38: LineSegment StartX=52.25 StartY=15.58 StartZ=0 EndX=52.25 EndY=14.58 EndZ=0
    g39: LineSegment StartX=53.5 StartY=16.83 StartZ=0 EndX=60.5 EndY=16.83 EndZ=0
    g40: LineSegment StartX=53.5 StartY=13.33 StartZ=0 EndX=60.5 EndY=13.33 EndZ=0
    g41: LineSegment StartX=61.75 StartY=15.58 StartZ=0 EndX=61.75 EndY=14.58 EndZ=0
    g42: ArcOfCircle CenterX=53.5 CenterY=15.58 CenterZ=0 NormalX=0 NormalY=0 NormalZ=1 AngleXU=0 Radius=1.25 StartAngle=1.5708 EndAngle=3.14159
    g43: ArcOfCircle CenterX=60.5 CenterY=15.58 CenterZ=0 NormalX=0 NormalY=0 NormalZ=1 AngleXU=0 Radius=1.25 StartAngle=2e-16 EndAngle=1.5708
    g44: ArcOfCircle CenterX=60.5 CenterY=14.58 CenterZ=0 NormalX=0 NormalY=0 NormalZ=1 AngleXU=0 Radius=1.25 StartAngle=4.7124 EndAngle=6.28319
    g45: ArcOfCircle CenterX=53.5 CenterY=14.58 CenterZ=0 NormalX=0 NormalY=0 NormalZ=1 AngleXU=0 Radius=1.25 StartAngle=3.14159 EndAngle=4.71239
  constraints (150):
    c: Horizontal(g0)
    c: Coincident(g0,g1)
    c: Coincident(g1,g2)
    c: Coincident(g2,g3)
    c: Horizontal(g3)
    c: Coincident(g3,g4)
    c: Vertical(g4)
    c: Coincident(g5,g6)
    c: Coincident(g6,g7)
    c: Horizontal(g7)
    c: Coincident(g7,g8)
    c: Coincident(g8,g9)
    c: Vertical(g9)
    c: Coincident(g9,g10)
    c: Coincident(g10,g5)
    c: Coincident(g11,g12)
    c: Coincident(g12,g13)
    c: Horizontal(g13)
    c: Coincident(g13,g14)
    c: Coincident(g14,g15)
    c: Vertical(g15)
    c: Coincident(g15,g16)
    c: Coincident(g16,g11)
    c: Horizontal(g16)
    c: Coincident(g17,g4)
    c: Coincident(g0,g17)
    c: DistanceX(g3) = 9.5
    c: DistanceX(g3,g3) = 14.25
    c: Vertical(g2)
    c: DistanceY(g3) = 25
    c: DistanceY(g4) = 22
    c: DistanceY(g4,g1) = 0
    c: DistanceX(g4,g0) = 2.25
    c: DistanceX(g0,g1) = 2.25
    c: Horizontal(g10)
    c: Vertical(g5)
    c: Vertical(g11)
    c: DistanceX(g5) = 40
    c: DistanceX(g5,g9) = 11.2
    c: DistanceY(g11,g9) = 0
    c: DistanceY(g5,g5) = 2.5
    c: DistanceY(g8,g5) = 0
    c: DistanceY(g11,g8) = 0
    c: DistanceY(g14,g11) = 0
    c: DistanceY(g6,g5) = 2.5
    c: DistanceX(g5,g6) = 2.5
    c: DistanceX(g7,g8) = 2.5
    c: DistanceX(g9,g11) = 1.25
    c: DistanceY(g12,g7) = 0
    c: DistanceX(g11,g12) = 2.5
    c: DistanceX(g13,g14) = 2.5
    c: DistanceX(g11,g15) = 11.2
    c: DistanceY(g0,g4) = 2.5
    c: DistanceY(g5) = 24.5
    c: Coincident(g19,g18)
    c: Vertical(g19)
    c: Horizontal(g20)
    c: Coincident(g21,g20)
    c: Coincident(g23,g19)
    c: Coincident(g24,g23)
    c: Coincident(g24,g22)
    c: Horizontal(g24)
    c: Coincident(g25,g21)
    c: Coincident(g25,g22)
    c: Vertical(g25)
    c: Coincident(g18,g20)
    c: Radius(g18) = 1
    c: Angle(g18) = 1.5708
    c: Angle(g21) = 1.5708
    c: Angle(g22) = 1.5708
    c: Angle(g23) = 1.5708
    c: DistanceX(g23) = 12.3
    c: DistanceY(g23) = 13.2
    c: DistanceX(g19) = 11.3
    c: DistanceY(g23,g19) = 0
    c: DistanceY(g18,g18) = 0
    c: DistanceX(g21,g20) = 0
    c: Radius(g21) = 1
    c: Radius(g22) = 1
    c: DistanceX(g22,g22) = 0
    c: DistanceX(g18,g20) = 4.5
    c: DistanceX(g26) = 18.9
    c: Radius(g26) = 0.5
    c: DistanceY(g26) = 16.475
    c: DistanceX(g26,g27) = 2.19
    c: DistanceY(g26,g27) = 0
    c: DistanceY(g28,g27) = 0
    c: DistanceY(g29,g28) = 0
    c: DistanceX(g27,g28) = 2.19
    c: Radius(g27) = 0.5
    c: Radius(g28) = 0.5
    c: Radius(g29) = 0.5
    c: DistanceX(g28,g29) = 2.19
    c: DistanceY(g23,g18) = 1.25
    c: Horizontal(g30)
    c: Vertical(g31)
    c: Vertical(g33)
    c: Coincident(g33,g34)
    c: Coincident(g33,g37)
    c: Coincident(g32,g37)
    c: Coincident(g32,g36)
    c: Coincident(g31,g36)
    c: Coincident(g31,g35)
    c: Coincident(g30,g35)
    c: Coincident(g30,g34)
    c: Angle(g34) = 1.5708
    c: Angle(g35) = 1.5708
    c: Angle(g37) = 1.5708
    c: Angle(g36) = 1.5708
    c: DistanceY(g18,g34) = 0
    c: DistanceY(g34,g33) = 0
    c: Radius(g34) = 1
    c: DistanceY(g33,g37) = 0
    c: Radius(g37) = 1
    c: Radius(g36) = 1
    c: Radius(g35) = 1
    c: DistanceY(g33,g23) = 0
    c: DistanceY(g31,g36) = 0
    c: Horizontal(g32)
    c: DistanceX(g35,g30) = 0
    c: DistanceX(g32,g32) = 4.5
    c: Vertical(g38)
    c: Horizontal(g39)
    c: Horizontal(g40)
    c: Vertical(g41)
    c: Coincident(g42,g38)
    c: Coincident(g42,g39)
    c: Coincident(g43,g39)
    c: Coincident(g45,g38)
    c: Coincident(g45,g40)
    c: Coincident(g40,g44)
    c: Coincident(g41,g44)
    c: Coincident(g41,g43)
    c: DistanceX(g42) = 53.5
    c: DistanceY(g42) = 15.58
    c: DistanceX(g42,g45) = 0
    c: DistanceY(g45,g42) = 1
    c: Radius(g42) = 1.25
    c: Radius(g44) = 1.25
    c: Radius(g43) = 1.25
    c: DistanceX(g45,g40) = 0
    c: DistanceX(g42,g39) = 0
    c: DistanceY(g42,g43) = 0
    c: DistanceY(g44,g45) = 0
    c: DistanceY(g45,g38) = 0
    c: DistanceX(g42,g43) = 7
    c: DistanceX(g18,g34) = 32.5
    c: DistanceY(g41,g44) = 0
    c: DistanceY(g43,g41) = 0
    c: Angle(g42) = 1.5708
FEATURE [Part::Extrusion] Extrude329  label="lightBottomCutDone013"
  Base = -> Sketch334
  Dir = (0,-1,2e-16)
  DirMode = 2
  FaceMakerClass = Part::FaceMakerBullseye
  FaceMakerMode = 3
  LengthFwd = 5
  LengthRev = 0
  Placement = pos=(0,2,0) rot=(0,0,1;0rad)
  Solid = true
  Symmetric = false
FEATURE [Sketcher::SketchObject] Sketch335
  ArcFitTolerance = 0
  FullyConstrained = true
  MakeInternals = false
  Placement = pos=(0,0,0) rot=(1,0,0;1.5708rad)
  sketch-geometry (8):
    g0: ArcOfCircle CenterX=11.8 CenterY=15.45 CenterZ=0 NormalX=0 NormalY=0 NormalZ=1 AngleXU=0 Radius=1.25 StartAngle=1.5708 EndAngle=3.14159
    g1: ArcOfCircle CenterX=17.3 CenterY=15.45 CenterZ=0 NormalX=0 NormalY=0 NormalZ=1 AngleXU=0 Radius=1.25 StartAngle=-9e-16 EndAngle=1.5708
    g2: ArcOfCircle CenterX=16.8 CenterY=14.2 CenterZ=0 NormalX=0 NormalY=0 NormalZ=1 AngleXU=0 Radius=1.75 StartAngle=4.71239 EndAngle=6.28319
    g3: ArcOfCircle CenterX=12.3 CenterY=14.2 CenterZ=0 NormalX=0 NormalY=0 NormalZ=1 AngleXU=0 Radius=1.75 StartAngle=3.14159 EndAngle=4.71239
    g4: LineSegment StartX=11.8 StartY=16.7 StartZ=0 EndX=17.3 EndY=16.7 EndZ=0
    g5: LineSegment StartX=18.55 StartY=15.45 StartZ=0 EndX=18.55 EndY=14.2 EndZ=0
    g6: LineSegment StartX=16.8 StartY=12.45 StartZ=0 EndX=12.3 EndY=12.45 EndZ=0
    g7: LineSegment StartX=10.55 StartY=14.2 StartZ=0 EndX=10.55 EndY=15.45 EndZ=0
  constraints (28):
    c: Coincident(g4,g0)
    c: Coincident(g4,g1)
    c: Horizontal(g4)
    c: Coincident(g5,g1)
    c: Coincident(g5,g2)
    c: Coincident(g6,g2)
    c: Coincident(g6,g3)
    c: Horizontal(g6)
    c: Coincident(g7,g3)
    c: Coincident(g7,g0)
    c: Vertical(g7)
    c: Radius(g0) = 1.25
    c: DistanceY(g0,g0) = 0
    c: Angle(g3) = 1.5708
    c: DistanceY(g3,g3) = 0
    c: DistanceY(g3,g0) = 1.25
    c: DistanceY(g3) = 14.2
    c: Radius(g3) = 1.75
    c: Radius(g2) = 1.75
    c: Radius(g1) = 1.25
    c: DistanceX(g6,g6) = 4.5
    c: DistanceX(g3) = 12.3
    c: DistanceY(g1,g1) = 0
    c: DistanceX(g2,g2) = 0
    c: Angle(g1) = 1.5708
    c: Angle(g2) = 1.5708
    c: Vertical(g5)
    c: DistanceX(g0,g0) = 0
FEATURE [Part::Extrusion] Extrude331  label="buttonCuts027"
  Base = -> Sketch335
  Dir = (0,-1,2e-16)
  DirMode = 2
  FaceMakerClass = Part::FaceMakerBullseye
  FaceMakerMode = 3
  LengthFwd = 0.6
  LengthRev = 0
  Placement = pos=(32.5,2,0) rot=(0,0,1;0rad)
  Solid = true
  Symmetric = false
FEATURE [Sketcher::SketchObject] Sketch336
  ArcFitTolerance = 0
  FullyConstrained = true
  MakeInternals = false
  Placement = pos=(0,0,0) rot=(1,0,0;1.5708rad)
  sketch-geometry (8):
    g0: ArcOfCircle CenterX=11.8 CenterY=15.45 CenterZ=0 NormalX=0 NormalY=0 NormalZ=1 AngleXU=0 Radius=1.25 StartAngle=1.5708 EndAngle=3.14159
    g1: ArcOfCircle CenterX=17.3 CenterY=15.45 CenterZ=0 NormalX=0 NormalY=0 NormalZ=1 AngleXU=0 Radius=1.25 StartAngle=-9e-16 EndAngle=1.5708
    g2: ArcOfCircle CenterX=16.8 CenterY=14.2 CenterZ=0 NormalX=0 NormalY=0 NormalZ=1 AngleXU=0 Radius=1.75 StartAngle=4.71239 EndAngle=6.28319
    g3: ArcOfCircle CenterX=12.3 CenterY=14.2 CenterZ=0 NormalX=0 NormalY=0 NormalZ=1 AngleXU=0 Radius=1.75 StartAngle=3.14159 EndAngle=4.71239
    g4: LineSegment StartX=11.8 StartY=16.7 StartZ=0 EndX=17.3 EndY=16.7 EndZ=0
    g5: LineSegment StartX=18.55 StartY=15.45 StartZ=0 EndX=18.55 EndY=14.2 EndZ=0
    g6: LineSegment StartX=16.8 StartY=12.45 StartZ=0 EndX=12.3 EndY=12.45 EndZ=0
    g7: LineSegment StartX=10.55 StartY=14.2 StartZ=0 EndX=10.55 EndY=15.45 EndZ=0
  constraints (28):
    c: Coincident(g4,g0)
    c: Coincident(g4,g1)
    c: Horizontal(g4)
    c: Coincident(g5,g1)
    c: Coincident(g5,g2)
    c: Coincident(g6,g2)
    c: Coincident(g6,g3)
    c: Horizontal(g6)
    c: Coincident(g7,g3)
    c: Coincident(g7,g0)
    c: Vertical(g7)
    c: Radius(g0) = 1.25
    c: DistanceY(g0,g0) = 0
    c: Angle(g3) = 1.5708
    c: DistanceY(g3,g3) = 0
    c: DistanceY(g3,g0) = 1.25
    c: DistanceY(g3) = 14.2
    c: Radius(g3) = 1.75
    c: Radius(g2) = 1.75
    c: Radius(g1) = 1.25
    c: DistanceX(g6,g6) = 4.5
    c: DistanceX(g3) = 12.3
    c: DistanceY(g1,g1) = 0
    c: DistanceX(g2,g2) = 0
    c: Angle(g1) = 1.5708
    c: Angle(g2) = 1.5708
    c: Vertical(g5)
    c: DistanceX(g0,g0) = 0
FEATURE [Part::Extrusion] Extrude330  label="buttonCuts026"
  Base = -> Sketch336
  Dir = (0,-1,2e-16)
  DirMode = 2
  FaceMakerClass = Part::FaceMakerBullseye
  FaceMakerMode = 3
  LengthFwd = 0.6
  LengthRev = 0
  Placement = pos=(0,2,0) rot=(0,0,1;0rad)
  Solid = true
  Symmetric = false
FEATURE [Part::MultiFuse] Fusion420  label="bottomButtonCuts015"
  Shapes = -> [Extrude331,Extrude330]
FEATURE [Part::MultiFuse] Fusion421  label="bottomCuts012"
  Shapes = -> [Fusion420,Extrude329]
FEATURE [Part::Compound] Compound021  label="wearableCuts006"
  Links = -> [Fusion421]
  Placement = pos=(72,9.5,-78) rot=(1,0,0;1.5708rad)
FEATURE [Sketcher::SketchObject] Sketch337
  ArcFitTolerance = 0
  FullyConstrained = true
  MakeInternals = false
  Placement = pos=(0,0,-77.25) rot=(0,0,1;0rad)
  sketch-geometry (6):
    g0: ArcOfCircle CenterX=125.5 CenterY=-4.58 CenterZ=0 NormalX=0 NormalY=0 NormalZ=1 AngleXU=0 Radius=2.4 StartAngle=1.5708 EndAngle=3.14159
    g1: ArcOfCircle CenterX=132.5 CenterY=-4.58 CenterZ=0 NormalX=0 NormalY=0 NormalZ=1 AngleXU=0 Radius=2.4 StartAngle=0 EndAngle=1.5708
    g2: LineSegment StartX=125.5 StartY=-2.18 StartZ=0 EndX=132.5 EndY=-2.18 EndZ=0
    g3: LineSegment StartX=134.9 StartY=-4.58 StartZ=0 EndX=134.9 EndY=-8.75 EndZ=0
    g4: LineSegment StartX=134.9 StartY=-8.75 StartZ=0 EndX=123.1 EndY=-8.75 EndZ=0
    g5: LineSegment StartX=123.1 StartY=-8.75 StartZ=0 EndX=123.1 EndY=-4.58 EndZ=0
  constraints (20):
    c: Vertical(g1,g1)
    c: Horizontal(g1,g0)
    c: Horizontal(g0,g0)
    c: DistanceX(g1) = 132.5
    c: Vertical(g1,g3)
    c: Horizontal(g1,g0)
    c: Coincident(g2,g0)
    c: Coincident(g2,g1)
    c: Coincident(g3,g1)
    c: Coincident(g5,g0)
    c: DistanceY(g0) = -4.58
    c: Horizontal(g4)
    c: DistanceY(g4) = -8.75
    c: Vertical(g5)
    c: DistanceX(g5) = 123.1
    c: Horizontal(g0,g1)
    c: Coincident(g4,g5)
    c: Diameter(g1) = 4.8
    c: Angle(g0) = 1.5708
    c: Coincident(g3,g4)
FEATURE [Part::Extrusion] Extrude332  label="usbCCut003"
  Base = -> Sketch337
  Dir = (0,0,1)
  DirMode = 2
  FaceMakerClass = Part::FaceMakerBullseye
  FaceMakerMode = 3
  LengthFwd = 10
  LengthRev = 0
  Reversed = true
  Solid = true
  Symmetric = false
FEATURE [Sketcher::SketchObject] Sketch338
  ArcFitTolerance = 0
  FullyConstrained = true
  MakeInternals = false
  Placement = pos=(0,0,-78) rot=(0,0,1;0rad)
  sketch-geometry (8):
    g0: ArcOfCircle CenterX=81 CenterY=-12 CenterZ=0 NormalX=0 NormalY=0 NormalZ=1 AngleXU=0 Radius=3.25 StartAngle=1.5708 EndAngle=3.14159
    g1: ArcOfCircle CenterX=81 CenterY=-14 CenterZ=0 NormalX=0 NormalY=0 NormalZ=1 AngleXU=0 Radius=3.25 StartAngle=3.14159 EndAngle=4.71239
    g2: ArcOfCircle CenterX=135 CenterY=-14 CenterZ=0 NormalX=0 NormalY=0 NormalZ=1 AngleXU=0 Radius=3.25 StartAngle=4.71239 EndAngle=6.28319
    g3: ArcOfCircle CenterX=135 CenterY=-12 CenterZ=0 NormalX=0 NormalY=0 NormalZ=1 AngleXU=0 Radius=3.25 StartAngle=0 EndAngle=1.5708
    g4: LineSegment StartX=81 StartY=-17.25 StartZ=0 EndX=135 EndY=-17.25 EndZ=0
    g5: LineSegment StartX=138.25 StartY=-14 StartZ=0 EndX=138.25 EndY=-12 EndZ=0
    g6: LineSegment StartX=135 StartY=-8.75 StartZ=0 EndX=81 EndY=-8.75 EndZ=0
    g7: LineSegment StartX=77.75 StartY=-12 StartZ=0 EndX=77.75 EndY=-14 EndZ=0
  constraints (30):
    c: Horizontal(g3,g0)
    c: Vertical(g1,g0)
    c: Vertical(g3,g2)
    c: Vertical(g2,g2)
    c: Vertical(g2,g3)
    c: Vertical(g1,g1)
    c: Vertical(g0,g0)
    c: Horizontal(g0,g0)
    c: Horizontal(g3,g3)
    c: Horizontal(g1,g1)
    c: DistanceY(g3) = -8.75
    c: Vertical(g0,g1)
    c: Horizontal(g3,g0)
    c: Vertical(g2,g3)
    c: Horizontal(g2,g2)
    c: Horizontal(g2,g1)
    c: DistanceX(g2) = 135
    c: DistanceY(g2) = -14
    c: DistanceY(g2,g3) = 2
    c: DistanceX(g0,g3) = 54
    c: Coincident(g4,g1)
    c: Coincident(g4,g2)
    c: Coincident(g5,g2)
    c: Coincident(g5,g3)
    c: Coincident(g6,g3)
    c: Coincident(g6,g0)
    c: Horizontal(g6)
    c: Tangent(g6,g0)
    c: Coincident(g7,g0)
    c: Coincident(g7,g1)
FEATURE [Part::Extrusion] Extrude333  label="microUSBCut003"
  Base = -> Sketch338
  Dir = (0,0,1)
  DirMode = 2
  FaceMakerClass = Part::FaceMakerBullseye
  FaceMakerMode = 3
  LengthFwd = 10
  LengthRev = 0
  Reversed = true
  Solid = true
  Symmetric = false
FEATURE [Part::MultiFuse] Fusion422  label="wireCuts003"
  Shapes = -> [Extrude332,Extrude333]
FEATURE [App::Part] Part007  label="piZeroParts003"
  Group = -> [Extrude329,Extrude330,Extrude331,Fusion420,Fusion421,Sketch334,Sketch335,Sketch336,Compound021,Sketch337,Extrude332,Sketch338,Extrude333,Fusion422]
  Origin = -> Origin030
  Placement = pos=(94,-4,0) rot=(0,0,1;0rad)
FEATURE [Part::FeaturePython] Connect001  # WARN: FeaturePython — macro-defined, semantics opaque (R4)
  Objects = -> [Part007]
  Tolerance = 0
FEATURE [Part::Cut] Cut046  label="base027"
  Base = -> Fusion423
  Tool = -> Connect001
FEATURE [Sketcher::SketchObject] Sketch339
  ArcFitTolerance = 0
  FullyConstrained = true
  MakeInternals = false
  Placement = pos=(0,0,0) rot=(1,0,0;1.5708rad)
  sketch-geometry (46):
    g0: LineSegment StartX=11.75 StartY=19.5 StartZ=0 EndX=21.5 EndY=19.5 EndZ=0
    g1: LineSegment StartX=21.5 StartY=19.5 StartZ=0 EndX=23.75 EndY=22 EndZ=0
    g2: LineSegment StartX=23.75 StartY=22 StartZ=0 EndX=23.75 EndY=25 EndZ=0
    g3: LineSegment StartX=23.75 StartY=25 StartZ=0 EndX=9.5 EndY=25 EndZ=0
    g4: LineSegment StartX=9.5 StartY=25 StartZ=0 EndX=9.5 EndY=22 EndZ=0
    g5: LineSegment StartX=40 StartY=24.5 StartZ=0 EndX=40 EndY=22 EndZ=0
    g6: LineSegment StartX=40 StartY=22 StartZ=0 EndX=42.5 EndY=19.5 EndZ=0
    g7: LineSegment StartX=42.5 StartY=19.5 StartZ=0 EndX=48.7 EndY=19.5 EndZ=0
    g8: LineSegment StartX=48.7 StartY=19.5 StartZ=0 EndX=51.2 EndY=22 EndZ=0
    g9: LineSegment StartX=51.2 StartY=22 StartZ=0 EndX=51.2 EndY=24.5 EndZ=0
    g10: LineSegment StartX=51.2 StartY=24.5 StartZ=0 EndX=40 EndY=24.5 EndZ=0
    g11: LineSegment StartX=52.45 StartY=24.5 StartZ=0 EndX=52.45 EndY=22 EndZ=0
    g12: LineSegment StartX=52.45 StartY=22 StartZ=0 EndX=54.95 EndY=19.5 EndZ=0
    g13: LineSegment StartX=54.95 StartY=19.5 StartZ=0 EndX=61.15 EndY=19.5 EndZ=0
    g14: LineSegment StartX=61.15 StartY=19.5 StartZ=0 EndX=63.65 EndY=22 EndZ=0
    g15: LineSegment StartX=63.65 StartY=22 StartZ=0 EndX=63.65 EndY=24.5 EndZ=0
    g16: LineSegment StartX=63.65 StartY=24.5 StartZ=0 EndX=52.45 EndY=24.5 EndZ=0
    g17: LineSegment StartX=9.5 StartY=22 StartZ=0 EndX=11.75 EndY=19.5 EndZ=0
    g18: ArcOfCircle CenterX=12.3 CenterY=15.45 CenterZ=0 NormalX=0 NormalY=0 NormalZ=1 AngleXU=0 Radius=1 StartAngle=1.5708 EndAngle=3.14159
    g19: LineSegment StartX=11.3 StartY=15.45 StartZ=0 EndX=11.3 EndY=14.2 EndZ=0
    g20: LineSegment StartX=12.3 StartY=16.45 StartZ=0 EndX=16.8 EndY=16.45 EndZ=0
    g21: ArcOfCircle CenterX=16.8 CenterY=15.45 CenterZ=0 NormalX=0 NormalY=0 NormalZ=1 AngleXU=0 Radius=1 StartAngle=3e-16 EndAngle=1.5708
    g22: ArcOfCircle CenterX=16.8 CenterY=14.2 CenterZ=0 NormalX=0 NormalY=0 NormalZ=1 AngleXU=0 Radius=1 StartAngle=4.71239 EndAngle=6.28319
    g23: ArcOfCircle CenterX=12.3 CenterY=14.2 CenterZ=0 NormalX=0 NormalY=0 NormalZ=1 AngleXU=0 Radius=1 StartAngle=3.14159 EndAngle=4.71239
    g24: LineSegment StartX=12.3 StartY=13.2 StartZ=0 EndX=16.8 EndY=13.2 EndZ=0
    g25: LineSegment StartX=17.8 StartY=15.45 StartZ=0 EndX=17.8 EndY=14.2 EndZ=0
    g26: Circle CenterX=18.9 CenterY=16.475 CenterZ=0 NormalX=0 NormalY=0 NormalZ=1 AngleXU=0 Radius=0.5
    g27: Circle CenterX=21.09 CenterY=16.475 CenterZ=0 NormalX=0 NormalY=0 NormalZ=1 AngleXU=0 Radius=0.5
    g28: Circle CenterX=23.28 CenterY=16.475 CenterZ=0 NormalX=0 NormalY=0 NormalZ=1 AngleXU=0 Radius=0.5
    g29: Circle CenterX=25.47 CenterY=16.475 CenterZ=0 NormalX=0 NormalY=0 NormalZ=1 AngleXU=0 Radius=0.5
    g30: LineSegment StartX=44.8 StartY=16.45 StartZ=0 EndX=49.3 EndY=16.45 EndZ=0
    g31: LineSegment StartX=50.3 StartY=15.45 StartZ=0 EndX=50.3 EndY=14.2 EndZ=0
    g32: LineSegment StartX=49.3 StartY=13.2 StartZ=0 EndX=44.8 EndY=13.2 EndZ=0
    g33: LineSegment StartX=43.8 StartY=15.45 StartZ=0 EndX=43.8 EndY=14.2 EndZ=0
    g34: ArcOfCircle CenterX=44.8 CenterY=15.45 CenterZ=0 NormalX=0 NormalY=0 NormalZ=1 AngleXU=0 Radius=1 StartAngle=1.5708 EndAngle=3.14159
    g35: ArcOfCircle CenterX=49.3 CenterY=15.45 CenterZ=0 NormalX=0 NormalY=0 NormalZ=1 AngleXU=0 Radius=1 StartAngle=3e-16 EndAngle=1.5708
    g36: ArcOfCircle CenterX=49.3 CenterY=14.2 CenterZ=0 NormalX=0 NormalY=0 NormalZ=1 AngleXU=0 Radius=1 StartAngle=4.71239 EndAngle=6.28319
    g37: ArcOfCircle CenterX=44.8 CenterY=14.2 CenterZ=0 NormalX=0 NormalY=0 NormalZ=1 AngleXU=0 Radius=1 StartAngle=3.14159 EndAngle=4.71239
    g38: LineSegment StartX=52.25 StartY=15.58 StartZ=0 EndX=52.25 EndY=14.58 EndZ=0
    g39: LineSegment StartX=53.5 StartY=16.83 StartZ=0 EndX=60.5 EndY=16.83 EndZ=0
    g40: LineSegment StartX=53.5 StartY=13.33 StartZ=0 EndX=60.5 EndY=13.33 EndZ=0
    g41: LineSegment StartX=61.75 StartY=15.58 StartZ=0 EndX=61.75 EndY=14.58 EndZ=0
    g42: ArcOfCircle CenterX=53.5 CenterY=15.58 CenterZ=0 NormalX=0 NormalY=0 NormalZ=1 AngleXU=0 Radius=1.25 StartAngle=1.5708 EndAngle=3.14159
    g43: ArcOfCircle CenterX=60.5 CenterY=15.58 CenterZ=0 NormalX=0 NormalY=0 NormalZ=1 AngleXU=0 Radius=1.25 StartAngle=2e-16 EndAngle=1.5708
    g44: ArcOfCircle CenterX=60.5 CenterY=14.58 CenterZ=0 NormalX=0 NormalY=0 NormalZ=1 AngleXU=0 Radius=1.25 StartAngle=4.7124 EndAngle=6.28319
    g45: ArcOfCircle CenterX=53.5 CenterY=14.58 CenterZ=0 NormalX=0 NormalY=0 NormalZ=1 AngleXU=0 Radius=1.25 StartAngle=3.14159 EndAngle=4.71239
  constraints (150):
    c: Horizontal(g0)
    c: Coincident(g0,g1)
    c: Coincident(g1,g2)
    c: Coincident(g2,g3)
    c: Horizontal(g3)
    c: Coincident(g3,g4)
    c: Vertical(g4)
    c: Coincident(g5,g6)
    c: Coincident(g6,g7)
    c: Horizontal(g7)
    c: Coincident(g7,g8)
    c: Coincident(g8,g9)
    c: Vertical(g9)
    c: Coincident(g9,g10)
    c: Coincident(g10,g5)
    c: Coincident(g11,g12)
    c: Coincident(g12,g13)
    c: Horizontal(g13)
    c: Coincident(g13,g14)
    c: Coincident(g14,g15)
    c: Vertical(g15)
    c: Coincident(g15,g16)
    c: Coincident(g16,g11)
    c: Horizontal(g16)
    c: Coincident(g17,g4)
    c: Coincident(g0,g17)
    c: DistanceX(g3) = 9.5
    c: DistanceX(g3,g3) = 14.25
    c: Vertical(g2)
    c: DistanceY(g3) = 25
    c: DistanceY(g4) = 22
    c: DistanceY(g4,g1) = 0
    c: DistanceX(g4,g0) = 2.25
    c: DistanceX(g0,g1) = 2.25
    c: Horizontal(g10)
    c: Vertical(g5)
    c: Vertical(g11)
    c: DistanceX(g5) = 40
    c: DistanceX(g5,g9) = 11.2
    c: DistanceY(g11,g9) = 0
    c: DistanceY(g5,g5) = 2.5
    c: DistanceY(g8,g5) = 0
    c: DistanceY(g11,g8) = 0
    c: DistanceY(g14,g11) = 0
    c: DistanceY(g6,g5) = 2.5
    c: DistanceX(g5,g6) = 2.5
    c: DistanceX(g7,g8) = 2.5
    c: DistanceX(g9,g11) = 1.25
    c: DistanceY(g12,g7) = 0
    c: DistanceX(g11,g12) = 2.5
    c: DistanceX(g13,g14) = 2.5
    c: DistanceX(g11,g15) = 11.2
    c: DistanceY(g0,g4) = 2.5
    c: DistanceY(g5) = 24.5
    c: Coincident(g19,g18)
    c: Vertical(g19)
    c: Horizontal(g20)
    c: Coincident(g21,g20)
    c: Coincident(g23,g19)
    c: Coincident(g24,g23)
    c: Coincident(g24,g22)
    c: Horizontal(g24)
    c: Coincident(g25,g21)
    c: Coincident(g25,g22)
    c: Vertical(g25)
    c: Coincident(g18,g20)
    c: Radius(g18) = 1
    c: Angle(g18) = 1.5708
    c: Angle(g21) = 1.5708
    c: Angle(g22) = 1.5708
    c: Angle(g23) = 1.5708
    c: DistanceX(g23) = 12.3
    c: DistanceY(g23) = 13.2
    c: DistanceX(g19) = 11.3
    c: DistanceY(g23,g19) = 0
    c: DistanceY(g18,g18) = 0
    c: DistanceX(g21,g20) = 0
    c: Radius(g21) = 1
    c: Radius(g22) = 1
    c: DistanceX(g22,g22) = 0
    c: DistanceX(g18,g20) = 4.5
    c: DistanceX(g26) = 18.9
    c: Radius(g26) = 0.5
    c: DistanceY(g26) = 16.475
    c: DistanceX(g26,g27) = 2.19
    c: DistanceY(g26,g27) = 0
    c: DistanceY(g28,g27) = 0
    c: DistanceY(g29,g28) = 0
    c: DistanceX(g27,g28) = 2.19
    c: Radius(g27) = 0.5
    c: Radius(g28) = 0.5
    c: Radius(g29) = 0.5
    c: DistanceX(g28,g29) = 2.19
    c: DistanceY(g23,g18) = 1.25
    c: Horizontal(g30)
    c: Vertical(g31)
    c: Vertical(g33)
    c: Coincident(g33,g34)
    c: Coincident(g33,g37)
    c: Coincident(g32,g37)
    c: Coincident(g32,g36)
    c: Coincident(g31,g36)
    c: Coincident(g31,g35)
    c: Coincident(g30,g35)
    c: Coincident(g30,g34)
    c: Angle(g34) = 1.5708
    c: Angle(g35) = 1.5708
    c: Angle(g37) = 1.5708
    c: Angle(g36) = 1.5708
    c: DistanceY(g18,g34) = 0
    c: DistanceY(g34,g33) = 0
    c: Radius(g34) = 1
    c: DistanceY(g33,g37) = 0
    c: Radius(g37) = 1
    c: Radius(g36) = 1
    c: Radius(g35) = 1
    c: DistanceY(g33,g23) = 0
    c: DistanceY(g31,g36) = 0
    c: Horizontal(g32)
    c: DistanceX(g35,g30) = 0
    c: DistanceX(g32,g32) = 4.5
    c: Vertical(g38)
    c: Horizontal(g39)
    c: Horizontal(g40)
    c: Vertical(g41)
    c: Coincident(g42,g38)
    c: Coincident(g42,g39)
    c: Coincident(g43,g39)
    c: Coincident(g45,g38)
    c: Coincident(g45,g40)
    c: Coincident(g40,g44)
    c: Coincident(g41,g44)
    c: Coincident(g41,g43)
    c: DistanceX(g42) = 53.5
    c: DistanceY(g42) = 15.58
    c: DistanceX(g42,g45) = 0
    c: DistanceY(g45,g42) = 1
    c: Radius(g42) = 1.25
    c: Radius(g44) = 1.25
    c: Radius(g43) = 1.25
    c: DistanceX(g45,g40) = 0
    c: DistanceX(g42,g39) = 0
    c: DistanceY(g42,g43) = 0
    c: DistanceY(g44,g45) = 0
    c: DistanceY(g45,g38) = 0
    c: DistanceX(g42,g43) = 7
    c: DistanceX(g18,g34) = 32.5
    c: DistanceY(g41,g44) = 0
    c: DistanceY(g43,g41) = 0
    c: Angle(g42) = 1.5708
FEATURE [Part::Extrusion] Extrude334  label="lightBottomCutDone014"
  Base = -> Sketch339
  Dir = (0,-1,2e-16)
  DirMode = 2
  FaceMakerClass = Part::FaceMakerBullseye
  FaceMakerMode = 3
  LengthFwd = 5
  LengthRev = 0
  Placement = pos=(0,2,0) rot=(0,0,1;0rad)
  Solid = true
  Symmetric = false
FEATURE [Sketcher::SketchObject] Sketch340
  ArcFitTolerance = 0
  FullyConstrained = true
  MakeInternals = false
  Placement = pos=(0,0,0) rot=(1,0,0;1.5708rad)
  sketch-geometry (8):
    g0: ArcOfCircle CenterX=11.8 CenterY=15.45 CenterZ=0 NormalX=0 NormalY=0 NormalZ=1 AngleXU=0 Radius=1.25 StartAngle=1.5708 EndAngle=3.14159
    g1: ArcOfCircle CenterX=17.3 CenterY=15.45 CenterZ=0 NormalX=0 NormalY=0 NormalZ=1 AngleXU=0 Radius=1.25 StartAngle=-9e-16 EndAngle=1.5708
    g2: ArcOfCircle CenterX=16.8 CenterY=14.2 CenterZ=0 NormalX=0 NormalY=0 NormalZ=1 AngleXU=0 Radius=1.75 StartAngle=4.71239 EndAngle=6.28319
    g3: ArcOfCircle CenterX=12.3 CenterY=14.2 CenterZ=0 NormalX=0 NormalY=0 NormalZ=1 AngleXU=0 Radius=1.75 StartAngle=3.14159 EndAngle=4.71239
    g4: LineSegment StartX=11.8 StartY=16.7 StartZ=0 EndX=17.3 EndY=16.7 EndZ=0
    g5: LineSegment StartX=18.55 StartY=15.45 StartZ=0 EndX=18.55 EndY=14.2 EndZ=0
    g6: LineSegment StartX=16.8 StartY=12.45 StartZ=0 EndX=12.3 EndY=12.45 EndZ=0
    g7: LineSegment StartX=10.55 StartY=14.2 StartZ=0 EndX=10.55 EndY=15.45 EndZ=0
  constraints (28):
    c: Coincident(g4,g0)
    c: Coincident(g4,g1)
    c: Horizontal(g4)
    c: Coincident(g5,g1)
    c: Coincident(g5,g2)
    c: Coincident(g6,g2)
    c: Coincident(g6,g3)
    c: Horizontal(g6)
    c: Coincident(g7,g3)
    c: Coincident(g7,g0)
    c: Vertical(g7)
    c: Radius(g0) = 1.25
    c: DistanceY(g0,g0) = 0
    c: Angle(g3) = 1.5708
    c: DistanceY(g3,g3) = 0
    c: DistanceY(g3,g0) = 1.25
    c: DistanceY(g3) = 14.2
    c: Radius(g3) = 1.75
    c: Radius(g2) = 1.75
    c: Radius(g1) = 1.25
    c: DistanceX(g6,g6) = 4.5
    c: DistanceX(g3) = 12.3
    c: DistanceY(g1,g1) = 0
    c: DistanceX(g2,g2) = 0
    c: Angle(g1) = 1.5708
    c: Angle(g2) = 1.5708
    c: Vertical(g5)
    c: DistanceX(g0,g0) = 0
FEATURE [Part::Extrusion] Extrude336  label="buttonCuts029"
  Base = -> Sketch340
  Dir = (0,-1,2e-16)
  DirMode = 2
  FaceMakerClass = Part::FaceMakerBullseye
  FaceMakerMode = 3
  LengthFwd = 0.6
  LengthRev = 0
  Placement = pos=(32.5,2,0) rot=(0,0,1;0rad)
  Solid = true
  Symmetric = false
FEATURE [Sketcher::SketchObject] Sketch341
  ArcFitTolerance = 0
  FullyConstrained = true
  MakeInternals = false
  Placement = pos=(0,0,0) rot=(1,0,0;1.5708rad)
  sketch-geometry (8):
    g0: ArcOfCircle CenterX=11.8 CenterY=15.45 CenterZ=0 NormalX=0 NormalY=0 NormalZ=1 AngleXU=0 Radius=1.25 StartAngle=1.5708 EndAngle=3.14159
    g1: ArcOfCircle CenterX=17.3 CenterY=15.45 CenterZ=0 NormalX=0 NormalY=0 NormalZ=1 AngleXU=0 Radius=1.25 StartAngle=-9e-16 EndAngle=1.5708
    g2: ArcOfCircle CenterX=16.8 CenterY=14.2 CenterZ=0 NormalX=0 NormalY=0 NormalZ=1 AngleXU=0 Radius=1.75 StartAngle=4.71239 EndAngle=6.28319
    g3: ArcOfCircle CenterX=12.3 CenterY=14.2 CenterZ=0 NormalX=0 NormalY=0 NormalZ=1 AngleXU=0 Radius=1.75 StartAngle=3.14159 EndAngle=4.71239
    g4: LineSegment StartX=11.8 StartY=16.7 StartZ=0 EndX=17.3 EndY=16.7 EndZ=0
    g5: LineSegment StartX=18.55 StartY=15.45 StartZ=0 EndX=18.55 EndY=14.2 EndZ=0
    g6: LineSegment StartX=16.8 StartY=12.45 StartZ=0 EndX=12.3 EndY=12.45 EndZ=0
    g7: LineSegment StartX=10.55 StartY=14.2 StartZ=0 EndX=10.55 EndY=15.45 EndZ=0
  constraints (28):
    c: Coincident(g4,g0)
    c: Coincident(g4,g1)
    c: Horizontal(g4)
    c: Coincident(g5,g1)
    c: Coincident(g5,g2)
    c: Coincident(g6,g2)
    c: Coincident(g6,g3)
    c: Horizontal(g6)
    c: Coincident(g7,g3)
    c: Coincident(g7,g0)
    c: Vertical(g7)
    c: Radius(g0) = 1.25
    c: DistanceY(g0,g0) = 0
    c: Angle(g3) = 1.5708
    c: DistanceY(g3,g3) = 0
    c: DistanceY(g3,g0) = 1.25
    c: DistanceY(g3) = 14.2
    c: Radius(g3) = 1.75
    c: Radius(g2) = 1.75
    c: Radius(g1) = 1.25
    c: DistanceX(g6,g6) = 4.5
    c: DistanceX(g3) = 12.3
    c: DistanceY(g1,g1) = 0
    c: DistanceX(g2,g2) = 0
    c: Angle(g1) = 1.5708
    c: Angle(g2) = 1.5708
    c: Vertical(g5)
    c: DistanceX(g0,g0) = 0
FEATURE [Part::Extrusion] Extrude335  label="buttonCuts028"
  Base = -> Sketch341
  Dir = (0,-1,2e-16)
  DirMode = 2
  FaceMakerClass = Part::FaceMakerBullseye
  FaceMakerMode = 3
  LengthFwd = 0.6
  LengthRev = 0
  Placement = pos=(0,2,0) rot=(0,0,1;0rad)
  Solid = true
  Symmetric = false
FEATURE [Part::MultiFuse] Fusion424  label="bottomButtonCuts016"
  Shapes = -> [Extrude336,Extrude335]
FEATURE [Part::MultiFuse] Fusion425  label="baseCuts003"
  Placement = pos=(166,5.5,-78) rot=(1,0,0;1.5708rad)
  Shapes = -> [Extrude334,Fusion424]
FEATURE [Part::Cut] Cut047  label="base028"
  Base = -> Cut046
  Tool = -> Fusion425
FEATURE [Sketcher::SketchObject] Sketch342
  ArcFitTolerance = 0
  FullyConstrained = true
  MakeInternals = false
  Placement = pos=(0,-4,0) rot=(1,0,0;1.5708rad)
  sketch-geometry (8):
    g0: LineSegment StartX=165 StartY=-68.75 StartZ=0 EndX=169 EndY=-68.75 EndZ=0
    g1: LineSegment StartX=169 StartY=-68.75 StartZ=0 EndX=169 EndY=-76 EndZ=0
    g2: LineSegment StartX=169 StartY=-76 StartZ=0 EndX=165 EndY=-76 EndZ=0
    g3: LineSegment StartX=165 StartY=-76 StartZ=0 EndX=165 EndY=-68.75 EndZ=0
    g4: LineSegment StartX=236 StartY=-68.75 StartZ=0 EndX=240 EndY=-68.75 EndZ=0
    g5: LineSegment StartX=240 StartY=-68.75 StartZ=0 EndX=240 EndY=-76 EndZ=0
    g6: LineSegment StartX=240 StartY=-76 StartZ=0 EndX=236 EndY=-76 EndZ=0
    g7: LineSegment StartX=236 StartY=-76 StartZ=0 EndX=236 EndY=-68.75 EndZ=0
  constraints (24):
    c: Coincident(g0,g1)
    c: Coincident(g1,g2)
    c: Coincident(g2,g3)
    c: Coincident(g3,g0)
    c: Horizontal(g0)
    c: Horizontal(g2)
    c: Vertical(g1)
    c: Vertical(g3)
    c: DistanceX(g2) = 165
    c: DistanceY(g2) = -76
    c: DistanceY(g1,g1) = 7.25
    c: DistanceX(g2,g1) = 4
    c: Coincident(g4,g5)
    c: Coincident(g5,g6)
    c: Coincident(g6,g7)
    c: Coincident(g7,g4)
    c: Horizontal(g4)
    c: Horizontal(g6)
    c: Vertical(g5)
    c: Vertical(g7)
    c: DistanceX(g5) = 240
    c: DistanceX(g4,g4) = 4
    c: Horizontal(g4,g0)
    c: Horizontal(g6,g1)
FEATURE [Part::Extrusion] Extrude337
  Base = -> Sketch342
  Dir = (0,-1,2e-16)
  DirMode = 2
  FaceMakerClass = Part::FaceMakerBullseye
  FaceMakerMode = 3
  LengthFwd = 12.2
  LengthRev = 0
  Solid = true
  Symmetric = false
FEATURE [Part::MultiFuse] Fusion426  label="base041"
  Shapes = -> [Cut047,Extrude337]
FEATURE [Sketcher::SketchObject] Sketch343
  ArcFitTolerance = 0
  FullyConstrained = true
  MakeInternals = false
  Placement = pos=(0,0,0) rot=(1,0,0;1.5708rad)
  sketch-geometry (16):
    g0: Circle CenterX=173.65 CenterY=40.16 CenterZ=0 NormalX=0 NormalY=0 NormalZ=1 AngleXU=0 Radius=5
    g1: Circle CenterX=186.35 CenterY=40.16 CenterZ=0 NormalX=0 NormalY=0 NormalZ=1 AngleXU=0 Radius=5
    g2: Circle CenterX=173.65 CenterY=19.84 CenterZ=0 NormalX=0 NormalY=0 NormalZ=1 AngleXU=0 Radius=5
    g3: Circle CenterX=186.35 CenterY=19.84 CenterZ=0 NormalX=0 NormalY=0 NormalZ=1 AngleXU=0 Radius=5
    g4: Circle CenterX=218.9 CenterY=19.84 CenterZ=0 NormalX=0 NormalY=0 NormalZ=1 AngleXU=0 Radius=5
    g5: Circle CenterX=231.6 CenterY=19.84 CenterZ=0 NormalX=0 NormalY=0 NormalZ=1 AngleXU=0 Radius=5
    g6: Circle CenterX=231.6 CenterY=40.16 CenterZ=0 NormalX=0 NormalY=0 NormalZ=1 AngleXU=0 Radius=5
    g7: Circle CenterX=218.9 CenterY=40.16 CenterZ=0 NormalX=0 NormalY=0 NormalZ=1 AngleXU=0 Radius=5
    g8: Circle CenterX=173.65 CenterY=19.84 CenterZ=0 NormalX=0 NormalY=0 NormalZ=1 AngleXU=0 Radius=1.125
    g9: Circle CenterX=186.35 CenterY=19.84 CenterZ=0 NormalX=0 NormalY=0 NormalZ=1 AngleXU=0 Radius=1.125
    g10: Circle CenterX=186.35 CenterY=40.16 CenterZ=0 NormalX=0 NormalY=0 NormalZ=1 AngleXU=0 Radius=1.125
    g11: Circle CenterX=173.65 CenterY=40.16 CenterZ=0 NormalX=0 NormalY=0 NormalZ=1 AngleXU=0 Radius=1.125
    g12: Circle CenterX=218.9 CenterY=40.16 CenterZ=0 NormalX=0 NormalY=0 NormalZ=1 AngleXU=0 Radius=1.125
    g13: Circle CenterX=231.6 CenterY=40.16 CenterZ=0 NormalX=0 NormalY=0 NormalZ=1 AngleXU=0 Radius=1.125
    g14: Circle CenterX=218.9 CenterY=19.84 CenterZ=0 NormalX=0 NormalY=0 NormalZ=1 AngleXU=0 Radius=1.125
    g15: Circle CenterX=231.6 CenterY=19.84 CenterZ=0 NormalX=0 NormalY=0 NormalZ=1 AngleXU=0 Radius=1.125
  constraints (34):
    c: DistanceY(g1,g0) = 0
    c: DistanceX(g0) = 173.65
    c: DistanceY(g0) = 40.16
    c: DistanceY(g2,g0) = 20.32
    c: Horizontal(g2,g3)
    c: Vertical(g3,g1)
    c: Horizontal(g1,g7)
    c: Horizontal(g7,g6)
    c: Horizontal(g4,g3)
    c: Horizontal(g3,g5)
    c: Equal(g0, g1-g7) x7
    c: Diameter(g0) = 10
    c: DistanceX(g1,g7) = 32.55
    c: DistanceX(g0,g1) = 12.7
    c: Vertical(g2,g0)
    c: DistanceX(g7,g6) = 12.7
    c: Vertical(g4,g7)
    c: Vertical(g5,g6)
    c: Coincident(g8,g2)
    c: Coincident(g9,g3)
    c: Coincident(g10,g1)
    c: Coincident(g11,g0)
    c: Coincident(g12,g7)
    c: Coincident(g13,g6)
    c: Coincident(g14,g4)
    c: Coincident(g15,g5)
    c: Equal(g8,g9)
    c: Equal(g8,g11)
    c: Equal(g8,g10)
    c: Equal(g8,g12)
    c: Equal(g8,g14)
    c: Equal(g8,g15)
    c: Equal(g8,g13)
    c: Diameter(g8) = 2.25
FEATURE [Part::Extrusion] Extrude338  label="i2cMounts001"
  Base = -> Sketch343
  Dir = (0,-1,2e-16)
  DirMode = 2
  FaceMakerClass = Part::FaceMakerBullseye
  FaceMakerMode = 3
  LengthFwd = 10
  LengthRev = 0
  Solid = true
  Symmetric = false
FEATURE [Part::MultiFuse] Fusion461  label="base042"
  Shapes = -> [Extrude338,Fusion426]
FEATURE [Part::Cut] Cut048  label="base029"
  Base = -> Fusion461
  Tool = -> Fusion460
FEATURE [Part::Fillet] Fillet075  label="base034"
  Base = -> Cut048
  EdgeLinks = -> Cut048 [Edge753,Edge812]
  Edges = 2 edges r=10: [Edge753,Edge812]
FEATURE [Sketcher::SketchObject] Sketch344
  ArcFitTolerance = 0
  FullyConstrained = true
  MakeInternals = false
  Placement = pos=(0,0,0) rot=(1,0,0;1.5708rad)
  sketch-geometry (4):
    g0: ArcOfCircle CenterX=233.5 CenterY=-58 CenterZ=0 NormalX=0 NormalY=0 NormalZ=1 AngleXU=0 Radius=4 StartAngle=1e-16 EndAngle=3.14159
    g1: ArcOfCircle CenterX=233.5 CenterY=-62 CenterZ=0 NormalX=0 NormalY=0 NormalZ=1 AngleXU=0 Radius=4 StartAngle=3.14159 EndAngle=6.28319
    g2: LineSegment StartX=229.5 StartY=-58 StartZ=0 EndX=229.5 EndY=-62 EndZ=0
    g3: LineSegment StartX=237.5 StartY=-62 StartZ=0 EndX=237.5 EndY=-58 EndZ=0
  constraints (10):
    c: Tangent(g0,g2) = -1.5708
    c: Tangent(g2,g1) = -1.5708
    c: Tangent(g1,g3) = -1.5708
    c: Tangent(g3,g0) = -1.5708
    c: Equal(g0,g1)
    c: Vertical(g2)
    c: DistanceX(g1) = 237.5
    c: DistanceX(g1,g1) = 8
    c: DistanceY(g1,g0) = 4
    c: DistanceY(g1) = -62
FEATURE [Part::Extrusion] Extrude339  label="baseWireCut001"
  Base = -> Sketch344
  Dir = (0,-1,2e-16)
  DirMode = 2
  FaceMakerClass = Part::FaceMakerBullseye
  FaceMakerMode = 3
  LengthFwd = 4
  LengthRev = 0
  Solid = true
  Symmetric = false
FEATURE [Part::Feature] Part__Feature362  label="Printed Circuit Board"
  shape: bbox 25.4 x 17.78 x 1.6 mm, 53 faces (baked)
FEATURE [Part::Feature] Part__Feature363  label="ICM-20948-9axis-IMU v2"
  Placement = pos=(-0.10588,0.00770028,1.6) rot=(0,0,-1;1.5708rad)
  shape: bbox 3 x 3 x 1.05 mm, 395 faces, 26 solids (baked)
FEATURE [Part::Feature] Part__Feature364  label="SOT23-5 v002"
  Placement = pos=(-5.22064,-0.331862,1.57965) rot=(0,0,-1;1.5708rad)
  shape: bbox 3.004 x 2.839 x 1.189 mm, 69 faces, 6 solids (baked)
FEATURE [Part::Feature] Part__Feature365  label="COMPOUND001"
  shape: bbox 1.158 x 2.103 x 0.7727 mm, 35 faces, 0 solids (baked)
FEATURE [Part::Feature] Part__Feature366  label="COMPOUND002"
  shape: bbox 1.985 x 1.82 x 0.6253 mm, 42 faces, 6 solids (baked)
FEATURE [App::Part] SOT23_6_v3  label="SOT23-6 v3"
  Group = -> [Part__Feature365,Part__Feature366]
  Origin = -> Origin031
  Placement = pos=(2.41278,-3.39005,1.22426) rot=(0,0,1;3.14159rad)
FEATURE [Part::Feature] Part__Feature367  label="COMPOUND003"
  shape: bbox 1.158 x 2.103 x 0.7727 mm, 35 faces, 0 solids (baked)
FEATURE [Part::Feature] Part__Feature368  label="COMPOUND004"
  shape: bbox 1.985 x 1.82 x 0.6253 mm, 42 faces, 6 solids (baked)
FEATURE [App::Part] SOT23_6_v004  label="SOT23-6 v004"
  Group = -> [Part__Feature367,Part__Feature368]
  Origin = -> Origin032
  Placement = pos=(1.87935,3.54648,1.22426) rot=(0,0,1;0rad)
FEATURE [Part::Feature] Part__Feature369  label="LED 0603 single color v1"
  Placement = pos=(-9.1591,3.69227,1.60762) rot=(0,0,1;1.5708rad)
  shape: bbox 1.961 x 0.7932 x 0.7145 mm, 63 faces, 5 solids (baked)
FEATURE [Part::Feature] Part__Feature370  label="Cathode"
  shape: bbox 1.4 x 0.65 x 0.7 mm, 14 faces (baked)
FEATURE [Part::Feature] Part__Feature371  label="Anode"
  shape: bbox 1.4 x 0.65 x 0.7 mm, 14 faces (baked)
FEATURE [Part::Feature] Part__Feature372  label="Cathode Bar"
  shape: bbox 0.3 x 1.3 x 0.01 mm, 6 faces (baked)
FEATURE [Part::Feature] Part__Feature373  label="Body"
  shape: bbox 1.95 x 1.5 x 1.05 mm, 38 faces (baked)
FEATURE [App::Part] SOD_323  label="SOD-323"
  Group = -> [Part__Feature370,Part__Feature371,Part__Feature372,Part__Feature373]
  Origin = -> Origin033
FEATURE [App::Part] SOD_323_v1  label="SOD-323 v1"
  Group = -> [SOD_323]
  Origin = -> Origin034
  Placement = pos=(7.02114,3.54357,1.6) rot=(0,0,1;1.5708rad)
FEATURE [Part::Feature] Part__Feature374  label="CAPC-0603-T0.9-BN v1"
  Placement = pos=(-1.65403,3.12991,1.6) rot=(0,0,1;0rad)
  shape: bbox 1.7 x 0.9 x 0.9 mm, 42 faces (baked)
FEATURE [Part::Feature] Part__Feature375  label="CAPC-0603-T0.9-BN v010"
  Placement = pos=(-2.94143,-0.250998,1.6) rot=(0,0,1;1.5708rad)
  shape: bbox 0.9 x 1.7 x 0.9 mm, 42 faces (baked)
FEATURE [Part::Feature] Part__Feature376  label="CAPC-0805-T0.95-BN v1"
  Placement = pos=(-4.93215,2.96802,1.6) rot=(0,0,1;0rad)
  shape: bbox 2.1 x 1.35 x 0.95 mm, 42 faces (baked)
FEATURE [Part::Feature] Part__Feature377  label="CAPC-0805-T0.95-BN v015"
  Placement = pos=(-6.10128,-3.2862,1.6) rot=(0,0,1;0rad)
  shape: bbox 2.1 x 1.35 x 0.95 mm, 42 faces (baked)
FEATURE [Part::Feature] Part__Feature378  label="RESC-0603 v1"
  Placement = pos=(-7.25133,3.55479,1.6) rot=(0,0,-1;1.5708rad)
  shape: bbox 0.9 x 1.7 x 0.55 mm, 52 faces, 3 solids (baked)
FEATURE [Part::Feature] Part__Feature379  label="RESC-0603 v009"
  Placement = pos=(-2.6456,-3.67699,1.6) rot=(0,0,1;0rad)
  shape: bbox 1.7 x 0.9 x 0.55 mm, 52 faces, 3 solids (baked)
FEATURE [Part::Feature] Part__Feature380  label="YC164_RESPACK v1"
  Placement = pos=(3.93663,0.00430864,1.6) rot=(0,0,-1;1.5708rad)
  shape: bbox 1.6 x 3.2 x 0.61 mm, 172 faces (baked)
FEATURE [Part::Feature] Part__Feature381  label="YC164_RESPACK v008"
  Placement = pos=(3.66041,4.82408,1.6) rot=(0,0,-1;1.5708rad)
  shape: bbox 1.6 x 3.2 x 0.61 mm, 172 faces (baked)
FEATURE [Part::Feature] Part__Feature382  label="qwicc v011"
  Placement = pos=(-8.62344,0.00769078,1.295) rot=(0.57735,-0.57735,-0.57735;2.0944rad)
  shape: bbox 4.95 x 6 x 2.96 mm, 229 faces, 7 solids (baked)
FEATURE [Part::Feature] Part__Feature383  label="qwicc v012"
  Placement = pos=(8.56116,0.0089391,1.295) rot=(0.57735,0.57735,0.57735;2.0944rad)
  shape: bbox 4.95 x 6 x 2.96 mm, 229 faces, 7 solids (baked)
FEATURE [App::Part] Adafruit_ICM20948_STEMMA_QT_v4  label="Adafruit ICM20948 STEMMA QT v4"
  Group = -> [Part__Feature362,Part__Feature363,Part__Feature364,SOT23_6_v3,SOT23_6_v004,Part__Feature369,SOD_323_v1,Part__Feature374,Part__Feature375,Part__Feature376,Part__Feature377,Part__Feature378,Part__Feature379,Part__Feature380,Part__Feature381,Part__Feature382,Part__Feature383]
  Origin = -> Origin035
  Placement = pos=(184.9,-24.7,66) rot=(0,0,1;4.71239rad)
FEATURE [Part::Feature] Part__Feature384  label="CL-SA_s_C004"
  Placement = pos=(-0.8,0,-1e-15) rot=(0,0,1;0rad)
  shape: bbox 8.3 x 3.1 x 2.4 mm, 31 faces (baked)
FEATURE [Part::Feature] Part__Feature385  label="CL-SA_c_C004"
  Placement = pos=(0,-4.5,-1e-15) rot=(0,0,1;0rad)
  shape: bbox 10 x 10 x 2.54 mm, 56 faces (baked)
FEATURE [App::Part] CL_SA_12C_024  label="switch001"
  Group = -> [Part__Feature384,Part__Feature385]
  Origin = -> Origin010
  Placement = pos=(202.5,-45,-80) rot=(-1,0,0;1.5708rad)
FEATURE [Sketcher::SketchObject] Sketch345
  ArcFitTolerance = 1e-06
  FullyConstrained = true
  MakeInternals = false
  Placement = pos=(0,0,-76) rot=(0,0,1;0rad)
  sketch-geometry (4):
    g0: LineSegment StartX=197.3 StartY=-43.5 StartZ=0 EndX=197.3 EndY=-46.5 EndZ=0
    g1: LineSegment StartX=197.3 StartY=-46.5 StartZ=0 EndX=207.7 EndY=-46.5 EndZ=0
    g2: LineSegment StartX=207.7 StartY=-46.5 StartZ=0 EndX=207.7 EndY=-43.5 EndZ=0
    g3: LineSegment StartX=207.7 StartY=-43.5 StartZ=0 EndX=197.3 EndY=-43.5 EndZ=0
  constraints (12):
    c: Coincident(g0,g1)
    c: Coincident(g1,g2)
    c: Coincident(g2,g3)
    c: Coincident(g3,g0)
    c: Vertical(g0)
    c: Vertical(g2)
    c: Horizontal(g1)
    c: Horizontal(g3)
    c: DistanceY(g0,g0) = 3
    c: DistanceX(g0) = 197.3
    c: DistanceX(g3,g3) = 10.4
    c: DistanceY(g0) = -43.5
FEATURE [Part::Extrusion] Extrude340  label="switchCut001"
  Base = -> Sketch345
  Dir = (0,0,1)
  DirMode = 2
  FaceMakerClass = Part::FaceMakerBullseye
  FaceMakerMode = 3
  LengthFwd = 4
  LengthRev = 0
  Reversed = true
  Solid = true
  Symmetric = false
FEATURE [Part::Cut] Cut049  label="piHolder002"
  Base = -> Cut034
  Tool = -> Extrude340
FEATURE [Part::Fillet] Fillet077  label="piCover006"
  Base = -> Cut049
  EdgeLinks = -> Cut049 [Edge108,Edge109,Edge110,Edge111,Edge176,Edge177,Edge178,Edge179,Edge180,Edge181,Edge182,Edge183]
  Edges = 12 edges r=0.5: [Edge108,Edge109,Edge110,Edge111,Edge176,Edge177,Edge178,Edge179,Edge180,Edge181,Edge182,Edge183]
FEATURE [Sketcher::SketchObject] Sketch346  label="wireProtector"
  ArcFitTolerance = 1e-06
  FullyConstrained = true
  MakeInternals = false
  Placement = pos=(0,0,-76) rot=(0,0,1;0rad)
  sketch-geometry (8):
    g0: LineSegment StartX=200.9 StartY=-23.75 StartZ=0 EndX=200.9 EndY=0 EndZ=0
    g1: LineSegment StartX=200.9 StartY=0 StartZ=0 EndX=203.4 EndY=0 EndZ=0
    g2: LineSegment StartX=203.4 StartY=0 StartZ=0 EndX=203.4 EndY=-21.25 EndZ=0
    g3: LineSegment StartX=234.75 StartY=-23.75 StartZ=0 EndX=234.75 EndY=0 EndZ=0
    g4: LineSegment StartX=234.75 StartY=0 StartZ=0 EndX=232.25 EndY=0 EndZ=0
    g5: LineSegment StartX=232.25 StartY=0 StartZ=0 EndX=232.25 EndY=-21.25 EndZ=0
    g6: LineSegment StartX=200.9 StartY=-23.75 StartZ=0 EndX=234.75 EndY=-23.75 EndZ=0
    g7: LineSegment StartX=232.25 StartY=-21.25 StartZ=0 EndX=203.4 EndY=-21.25 EndZ=0
  constraints (24):
    c: Vertical(g0)
    c: Coincident(g2,g1)
    c: Vertical(g2)
    c: Vertical(g3)
    c: Coincident(g4,g3)
    c: Horizontal(g4)
    c: Coincident(g5,g4)
    c: Vertical(g5)
    c: Horizontal(g1)
    c: Coincident(g0,g1)
    c: DistanceY(g0) = 0
    c: Horizontal(g4,g1)
    c: DistanceX(g0,g1) = 2.5
    c: DistanceY(g2,g0) = -2.5
    c: DistanceY(g2,g2) = 21.25
    c: Horizontal(g5,g2)
    c: Horizontal(g3,g0)
    c: DistanceX(g5,g3) = 2.5
    c: Coincident(g6,g0)
    c: Coincident(g6,g3)
    c: Coincident(g7,g5)
    c: Coincident(g7,g2)
    c: DistanceX(g2) = 203.4
    c: DistanceX(g5) = 232.25
FEATURE [Part::Extrusion] Extrude341
  Base = -> Sketch346
  Dir = (0,0,1)
  DirMode = 2
  FaceMakerClass = Part::FaceMakerBullseye
  FaceMakerMode = 3
  LengthFwd = 12
  LengthRev = 0
  Reversed = true
  Solid = true
  Symmetric = false
FEATURE [Part::Fillet] Fillet078  label="wireCover"
  Base = -> Extrude341
  EdgeLinks = -> Extrude341 [Edge1,Edge2,Edge11,Edge14]
  Edges = 4 edges r=3.25: [Edge1,Edge2,Edge11,Edge14]
FEATURE [Part::Fillet] Fillet079
  Base = -> Fillet075
  EdgeLinks = -> Fillet075 [Edge80,Edge81,Edge82,Edge84,Edge89,Edge90,Edge124,Edge126,Edge133,Edge134,Edge143,Edge144,Edge145]
  Edges = 13 edges r=1: [Edge80,Edge81,Edge82,Edge84,Edge89,Edge90,Edge124,Edge126,Edge133,Edge134,Edge143,Edge144,Edge145]
FEATURE [Part::Fillet] Fillet080  label="sensorBase"
  Base = -> Fillet079
  EdgeLinks = -> Fillet079 [Edge13,Edge81,Edge82,Edge359,Edge361,Edge363,Edge404,Edge406,Edge408,Edge744,Edge748]
  Edges = 11 edges r=1: [Edge13,Edge81,Edge82,Edge359,Edge361,Edge363,Edge404,Edge406,Edge408,Edge744,Edge748]
FEATURE [Part::Cut] Cut050
  Base = -> Fillet080
  Tool = -> Extrude339
FEATURE [Part::Fillet] Fillet081  label="sensorBase001"
  Base = -> Cut050
  EdgeLinks = -> Cut050 [Edge1,Edge3,Edge4,Edge6,Edge20,Edge22,Edge63,Edge65,Edge67,Edge68,Edge69,Edge70,Edge276,Edge278,Edge280,Edge281]
  Edges = 16 edges r=1: [Edge1,Edge3,Edge4,Edge6,Edge20,Edge22,Edge63,Edge65,Edge67,Edge68,Edge69,Edge70,Edge276,Edge278,Edge280,Edge281]
FEATURE [Part::Fillet] Fillet082
  Base = -> Fillet078
  EdgeLinks = -> Fillet078 [Edge4,Edge17,Edge19,Edge20,Edge21,Edge22,Edge23,Edge24,Edge25,Edge26,Edge27,Edge28]
  Edges = 12 edges r=1: [Edge4,Edge17,Edge19,Edge20,Edge21,Edge22,Edge23,Edge24,Edge25,Edge26,Edge27,Edge28]
FEATURE [Part::Fillet] Fillet083  label="sensorBase002"
  Base = -> Fillet081
  EdgeLinks = -> Fillet081 [Edge471,Edge478]
  Edges = 2 edges r=1: [Edge471,Edge478]
FEATURE [Part::MultiFuse] Fusion462  label="sensorBase003"
  Shapes = -> [Fillet083,Fillet082]
FEATURE [Part::Fillet] Fillet084  label="sensorBase004"
  Base = -> Fusion462
  EdgeLinks = -> Fusion462 [Edge171,Edge351]
  Edges = 2 edges r=1: [Edge171,Edge351]
FEATURE [Part::FeaturePython] Tube  # WARN: FeaturePython — macro-defined, semantics opaque (R4)
  AttacherType = Attacher::AttachEngine3D
  Height = 10
  InnerRadius = 3.25
  OuterRadius = 6
  Placement = pos=(220,-44.5,-86) rot=(0,0,1;0rad)
FEATURE [Part::Cylinder] Cylinder095
  Angle = 360
  AttacherType = Attacher::AttachEngine3D
  FirstAngle = 0
  Height = 10
  Placement = pos=(220,-44.5,-86) rot=(0,0,1;0rad)
  Radius = 3.25
  SecondAngle = 0
FEATURE [Part::FeaturePython] Tube001  # WARN: FeaturePython — macro-defined, semantics opaque (R4)
  AttacherType = Attacher::AttachEngine3D
  Height = 10
  InnerRadius = 3.25
  OuterRadius = 6
  Placement = pos=(220,-44.5,-86) rot=(0,0,1;0rad)
FEATURE [Part::MultiFuse] Fusion463
  Refine = true
  Shapes = -> [Tube,Cylinder095]
FEATURE [Part::Cut] Cut051
  Base = -> Fillet077
  Refine = true
  Tool = -> Fusion463
FEATURE [Part::Cylinder] Cylinder096
  Angle = 360
  AttacherType = Attacher::AttachEngine3D
  FirstAngle = 0
  Height = 10
  Placement = pos=(220,-44.5,-86) rot=(0,0,1;0rad)
  Radius = 3.25
  SecondAngle = 0
FEATURE [Part::Cylinder] Cylinder097
  Angle = 360
  AttacherType = Attacher::AttachEngine3D
  FirstAngle = 0
  Height = 10
  Placement = pos=(220,-44.5,-86) rot=(0,0,1;0rad)
  Radius = 3
  SecondAngle = 0
FEATURE [Sketcher::SketchObject] Sketch347  label="outerSRS028"
  ArcFitTolerance = 0
  FullyConstrained = true
  MakeInternals = false
  Placement = pos=(0,0,-80) rot=(0,0,1;0rad)
  sketch-geometry (6):
    g0: LineSegment StartX=158.5 StartY=0 StartZ=0 EndX=158.5 EndY=-32 EndZ=0
    g1: LineSegment StartX=180.5 StartY=-54 StartZ=0 EndX=224.5 EndY=-54 EndZ=0
    g2: LineSegment StartX=246.5 StartY=0 StartZ=0 EndX=246.5 EndY=-32 EndZ=0
    g3: ArcOfCircle CenterX=180.5 CenterY=-32 CenterZ=0 NormalX=0 NormalY=0 NormalZ=1 AngleXU=0 Radius=22 StartAngle=3.14159 EndAngle=4.71239
    g4: ArcOfCircle CenterX=224.5 CenterY=-32 CenterZ=0 NormalX=0 NormalY=0 NormalZ=1 AngleXU=0 Radius=22 StartAngle=4.71239 EndAngle=6.28319
    g5: LineSegment StartX=158.5 StartY=0 StartZ=0 EndX=246.5 EndY=0 EndZ=0
  constraints (20):
    c: PointOnObject(g5,g-1)
    c: Vertical(g0)
    c: Horizontal(g1)
    c: Vertical(g2)
    c: DistanceY(g2,g5) = 0
    c: Coincident(g0,g3)
    c: Coincident(g1,g3)
    c: Coincident(g1,g4)
    c: Coincident(g2,g4)
    c: Angle(g3) = 1.5708
    c: Angle(g4) = 1.5708
    c: Coincident(g5,g2)
    c: DistanceX(g0) = 158.5
    c: Coincident(g5,g0)
    c: DistanceX(g0,g2) = 88
    c: DistanceY(g0,g0) = 32
    c: DistanceY(g2,g0) = 0
    c: DistanceY(g3,g0) = 0
    c: DistanceY(g4,g2) = 0
    c: DistanceX(g0,g3) = 22
FEATURE [Part::Extrusion] Extrude342
  Base = -> Sketch347
  Dir = (0,0,1)
  DirMode = 2
  FaceMakerClass = Part::FaceMakerBullseye
  FaceMakerMode = 3
  LengthFwd = 4
  LengthRev = 0
  Solid = true
  Symmetric = false
FEATURE [Part::Fillet] Fillet085  label="piCoverBottom004"
  Base = -> Extrude342
  EdgeLinks = -> Extrude342 [Edge3,Edge4,Edge6,Edge7,Edge9,Edge10,Edge12,Edge13,Edge15,Edge16,Edge17,Edge18]
  Edges = 12 edges r=1: [Edge3,Edge4,Edge6,Edge7,Edge9,Edge10,Edge12,Edge13,Edge15,Edge16,Edge17,Edge18]
FEATURE [Sketcher::SketchObject] Sketch348  label="innerSRS018"
  ArcFitTolerance = 0
  FullyConstrained = true
  MakeInternals = false
  Placement = pos=(0,0,-65) rot=(0,0,1;0rad)
  sketch-geometry (12):
    g0: ArcOfCircle CenterX=180.5 CenterY=-32 CenterZ=0 NormalX=0 NormalY=0 NormalZ=1 AngleXU=0 Radius=10 StartAngle=3.14159 EndAngle=4.71239
    g1: ArcOfCircle CenterX=224.5 CenterY=-32 CenterZ=0 NormalX=0 NormalY=0 NormalZ=1 AngleXU=0 Radius=10 StartAngle=4.71239 EndAngle=6.28319
    g2: LineSegment StartX=170.5 StartY=-32 StartZ=0 EndX=170.5 EndY=0 EndZ=0
    g3: LineSegment StartX=234.5 StartY=0 StartZ=0 EndX=234.5 EndY=-32 EndZ=0
    g4: LineSegment StartX=180.5 StartY=-42 StartZ=0 EndX=224.5 EndY=-42 EndZ=0
    g5: LineSegment StartX=167.5 StartY=0 StartZ=0 EndX=167.5 EndY=-32 EndZ=0
    g6: LineSegment StartX=180.5 StartY=-45 StartZ=0 EndX=224.5 EndY=-45 EndZ=0
    g7: LineSegment StartX=237.5 StartY=0 StartZ=0 EndX=237.5 EndY=-32 EndZ=0
    g8: ArcOfCircle CenterX=180.5 CenterY=-32 CenterZ=0 NormalX=0 NormalY=0 NormalZ=1 AngleXU=0 Radius=13 StartAngle=3.14159 EndAngle=4.71239
    g9: ArcOfCircle CenterX=224.5 CenterY=-32 CenterZ=0 NormalX=0 NormalY=0 NormalZ=1 AngleXU=0 Radius=13 StartAngle=4.71239 EndAngle=6.28319
    g10: LineSegment StartX=167.5 StartY=0 StartZ=0 EndX=170.5 EndY=0 EndZ=0
    g11: LineSegment StartX=234.5 StartY=0 StartZ=0 EndX=237.5 EndY=0 EndZ=0
  constraints (40):
    c: Angle(g1) = 1.5708
    c: DistanceY(g1,g1) = 0
    c: DistanceY(g1,g0) = 0
    c: Angle(g0) = 1.5708
    c: DistanceX(g0,g0) = 10
    c: DistanceY(g0,g0) = 0
    c: DistanceX(g1,g1) = 10
    c: Coincident(g2,g0)
    c: Vertical(g2)
    c: PointOnObject(g3,g-1)
    c: Coincident(g3,g1)
    c: Vertical(g3)
    c: DistanceY(g2,g2) = 32
    c: Coincident(g4,g1)
    c: PointOnObject(g5,g-1)
    c: Vertical(g5)
    c: Horizontal(g6)
    c: Vertical(g7)
    c: DistanceX(g5,g2) = 3
    c: DistanceX(g3,g7) = 3
    c: DistanceY(g5,g0) = 0
    c: DistanceY(g7,g1) = 0
    c: DistanceY(g7,g3) = 0
    c: DistanceX(g2,g3) = 64
    c: DistanceX(g0,g6) = 0
    c: DistanceX(g6,g1) = 0
    c: DistanceY(g2) = 0
    c: Coincident(g5,g8)
    c: Coincident(g6,g8)
    c: DistanceY(g6,g0) = 3
    c: Coincident(g6,g9)
    c: Coincident(g7,g9)
    c: Angle(g8) = 1.5708
    c: Angle(g9) = 1.5708
    c: Coincident(g10,g5)
    c: Coincident(g10,g2)
    c: Coincident(g11,g3)
    c: Coincident(g11,g7)
    c: Coincident(g0,g4)
    c: DistanceX(g2) = 170.5
FEATURE [Sketcher::SketchObject] Sketch349  label="outerSRS029"
  ArcFitTolerance = 0
  FullyConstrained = true
  MakeInternals = false
  Placement = pos=(0,0,-80) rot=(0,0,1;0rad)
  sketch-geometry (12):
    g0: ArcOfCircle CenterX=180.5 CenterY=-32 CenterZ=0 NormalX=0 NormalY=0 NormalZ=1 AngleXU=0 Radius=20 StartAngle=3.14159 EndAngle=4.71239
    g1: ArcOfCircle CenterX=224.5 CenterY=-32 CenterZ=0 NormalX=0 NormalY=0 NormalZ=1 AngleXU=0 Radius=20 StartAngle=4.71239 EndAngle=6.28319
    g2: LineSegment StartX=160.5 StartY=-32 StartZ=0 EndX=160.5 EndY=0 EndZ=0
    g3: LineSegment StartX=244.5 StartY=0 StartZ=0 EndX=244.5 EndY=-32 EndZ=0
    g4: LineSegment StartX=180.5 StartY=-52 StartZ=0 EndX=224.5 EndY=-52 EndZ=0
    g5: LineSegment StartX=157.5 StartY=0 StartZ=0 EndX=157.5 EndY=-32 EndZ=0
    g6: LineSegment StartX=180.5 StartY=-55 StartZ=0 EndX=224.5 EndY=-55 EndZ=0
    g7: LineSegment StartX=247.5 StartY=0 StartZ=0 EndX=247.5 EndY=-32 EndZ=0
    g8: ArcOfCircle CenterX=180.5 CenterY=-32 CenterZ=0 NormalX=0 NormalY=0 NormalZ=1 AngleXU=0 Radius=23 StartAngle=3.14159 EndAngle=4.71239
    g9: ArcOfCircle CenterX=224.5 CenterY=-32 CenterZ=0 NormalX=0 NormalY=0 NormalZ=1 AngleXU=0 Radius=23 StartAngle=4.71239 EndAngle=6.28319
    g10: LineSegment StartX=157.5 StartY=0 StartZ=0 EndX=160.5 EndY=0 EndZ=0
    g11: LineSegment StartX=244.5 StartY=0 StartZ=0 EndX=247.5 EndY=0 EndZ=0
  constraints (40):
    c: Angle(g1) = 1.5708
    c: DistanceY(g1,g0) = 0
    c: Angle(g0) = 1.5708
    c: DistanceY(g0,g0) = 0
    c: Coincident(g2,g0)
    c: Vertical(g2)
    c: PointOnObject(g3,g-1)
    c: Coincident(g3,g1)
    c: Vertical(g3)
    c: DistanceY(g2,g2) = 32
    c: Coincident(g4,g1)
    c: PointOnObject(g5,g-1)
    c: Vertical(g5)
    c: Horizontal(g6)
    c: Vertical(g7)
    c: DistanceX(g5,g2) = 3
    c: DistanceX(g3,g7) = 3
    c: DistanceY(g5,g0) = 0
    c: DistanceY(g7,g1) = 0
    c: DistanceY(g7,g3) = 0
    c: DistanceX(g2) = 160.5
    c: DistanceX(g2,g3) = 84
    c: DistanceX(g0,g6) = 0
    c: DistanceX(g6,g1) = 0
    c: DistanceY(g2) = 0
    c: Coincident(g5,g8)
    c: Coincident(g6,g8)
    c: DistanceY(g6,g0) = 3
    c: Coincident(g6,g9)
    c: Coincident(g7,g9)
    c: Angle(g8) = 1.5708
    c: Angle(g9) = 1.5708
    c: Coincident(g10,g5)
    c: Coincident(g10,g2)
    c: Coincident(g11,g3)
    c: Coincident(g11,g7)
    c: DistanceY(g0,g0) = 20
    c: Coincident(g0,g4)
    c: DistanceY(g1,g0) = 0
    c: DistanceY(g1,g1) = 0
FEATURE [Part::Loft] Loft017  label="srs024"
  Closed = false
  MaxDegree = 5
  Ruled = false
  Sections = -> [Sketch348,Sketch349]
  Solid = true
FEATURE [Part::Fillet] Fillet086  label="piCover010"
  Base = -> Loft017
  EdgeLinks = -> Loft017 [Edge1,Edge3,Edge5,Edge7,Edge8,Edge10,Edge11,Edge13,Edge14,Edge16,Edge17,Edge19,Edge20,Edge22,Edge23,Edge25,Edge26,Edge28,Edge29,Edge31,Edge32,Edge34,Edge35,Edge36]
  Edges = 24 edges r=1: [Edge1,Edge3,Edge5,Edge7,Edge8,Edge10,Edge11,Edge13,Edge14,Edge16,Edge17,Edge19,Edge20,Edge22,Edge23,Edge25,Edge26,Edge28,Edge29,Edge31,Edge32,Edge34,Edge35,Edge36]
  Placement = pos=(0,0,29) rot=(0,0,1;0rad)
FEATURE [Sketcher::SketchObject] Sketch350  label="outerSRS030"
  ArcFitTolerance = 0
  FullyConstrained = true
  MakeInternals = false
  Placement = pos=(0,0,-80) rot=(0,0,1;0rad)
  sketch-geometry (12):
    g0: ArcOfCircle CenterX=180.5 CenterY=-32 CenterZ=0 NormalX=0 NormalY=0 NormalZ=1 AngleXU=0 Radius=19 StartAngle=3.14159 EndAngle=4.71239
    g1: ArcOfCircle CenterX=224.5 CenterY=-32 CenterZ=0 NormalX=0 NormalY=0 NormalZ=1 AngleXU=0 Radius=19 StartAngle=4.71239 EndAngle=6.28319
    g2: LineSegment StartX=161.5 StartY=-32 StartZ=0 EndX=161.5 EndY=0 EndZ=0
    g3: LineSegment StartX=243.5 StartY=0 StartZ=0 EndX=243.5 EndY=-32 EndZ=0
    g4: LineSegment StartX=180.5 StartY=-51 StartZ=0 EndX=224.5 EndY=-51 EndZ=0
    g5: LineSegment StartX=158.5 StartY=0 StartZ=0 EndX=158.5 EndY=-32 EndZ=0
    g6: LineSegment StartX=180.5 StartY=-54 StartZ=0 EndX=224.5 EndY=-54 EndZ=0
    g7: LineSegment StartX=246.5 StartY=0 StartZ=0 EndX=246.5 EndY=-32 EndZ=0
    g8: ArcOfCircle CenterX=180.5 CenterY=-32 CenterZ=0 NormalX=0 NormalY=0 NormalZ=1 AngleXU=0 Radius=22 StartAngle=3.14159 EndAngle=4.71239
    g9: ArcOfCircle CenterX=224.5 CenterY=-32 CenterZ=0 NormalX=0 NormalY=0 NormalZ=1 AngleXU=0 Radius=22 StartAngle=4.71239 EndAngle=6.28319
    g10: LineSegment StartX=158.5 StartY=0 StartZ=0 EndX=161.5 EndY=0 EndZ=0
    g11: LineSegment StartX=243.5 StartY=0 StartZ=0 EndX=246.5 EndY=0 EndZ=0
  constraints (40):
    c: Angle(g1) = 1.5708
    c: DistanceY(g1,g0) = 0
    c: Angle(g0) = 1.5708
    c: DistanceY(g0,g0) = 0
    c: Coincident(g2,g0)
    c: Vertical(g2)
    c: PointOnObject(g3,g-1)
    c: Coincident(g3,g1)
    c: Vertical(g3)
    c: DistanceY(g2,g2) = 32
    c: Coincident(g4,g1)
    c: PointOnObject(g5,g-1)
    c: Vertical(g5)
    c: Horizontal(g6)
    c: Vertical(g7)
    c: DistanceX(g5,g2) = 3
    c: DistanceX(g3,g7) = 3
    c: DistanceY(g5,g0) = 0
    c: DistanceY(g7,g1) = 0
    c: DistanceY(g7,g3) = 0
    c: DistanceX(g2) = 161.5
    c: DistanceX(g2,g3) = 82
    c: DistanceX(g0,g6) = 0
    c: DistanceX(g6,g1) = 0
    c: DistanceY(g2) = 0
    c: Coincident(g5,g8)
    c: Coincident(g6,g8)
    c: DistanceY(g6,g0) = 3
    c: Coincident(g6,g9)
    c: Coincident(g7,g9)
    c: Angle(g8) = 1.5708
    c: Angle(g9) = 1.5708
    c: Coincident(g10,g5)
    c: Coincident(g10,g2)
    c: Coincident(g11,g3)
    c: Coincident(g11,g7)
    c: DistanceY(g0,g0) = 19
    c: Coincident(g0,g4)
    c: DistanceY(g1,g0) = 0
    c: DistanceY(g1,g1) = 0
FEATURE [Part::Extrusion] Extrude343  label="piCover009"
  Base = -> Sketch350
  Dir = (0,0,1)
  DirMode = 2
  FaceMakerClass = Part::FaceMakerBullseye
  FaceMakerMode = 3
  LengthFwd = 30.5
  LengthRev = 0
  Solid = true
  Symmetric = false
FEATURE [Part::Fillet] Fillet087
  Base = -> Extrude343
  EdgeLinks = -> Extrude343 [Edge24,Edge25,Edge27,Edge28,Edge30,Edge31,Edge33,Edge34,Edge35,Edge36]
  Edges = 10 edges r=1: [Edge24,Edge25,Edge27,Edge28,Edge30,Edge31,Edge33,Edge34,Edge35,Edge36]
FEATURE [Part::MultiFuse] Fusion464  label="piCover012"
  Shapes = -> [Fillet087,Fillet086,Fillet085]
FEATURE [Sketcher::SketchObject] Sketch351
  ArcFitTolerance = 0
  FullyConstrained = true
  MakeInternals = false
  Placement = pos=(0,0,0) rot=(1,0,0;1.5708rad)
  sketch-geometry (4):
    g0: LineSegment StartX=70 StartY=80 StartZ=0 EndX=247.5 EndY=80 EndZ=0
    g1: LineSegment StartX=247.5 StartY=80 StartZ=0 EndX=247.5 EndY=-80 EndZ=0
    g2: LineSegment StartX=247.5 StartY=-80 StartZ=0 EndX=70 EndY=-80 EndZ=0
    g3: LineSegment StartX=70 StartY=-80 StartZ=0 EndX=70 EndY=80 EndZ=0
  constraints (12):
    c: Coincident(g0,g1)
    c: Coincident(g1,g2)
    c: Coincident(g2,g3)
    c: Coincident(g3,g0)
    c: Horizontal(g0)
    c: Horizontal(g2)
    c: Vertical(g1)
    c: Vertical(g3)
    c: DistanceY(g2) = -80
    c: DistanceY(g0) = 80
    c: DistanceX(g2) = 70
    c: DistanceX(g2,g2) = 177.5
FEATURE [Part::Extrusion] Extrude344  label="srsCuts007"
  Base = -> Sketch351
  Dir = (0,-1,2e-16)
  DirMode = 2
  FaceMakerClass = Part::FaceMakerBullseye
  FaceMakerMode = 3
  LengthFwd = 4.1
  LengthRev = 0
  Solid = true
  Symmetric = false
FEATURE [Part::Cut] Cut052  label="piCover007"
  Base = -> Fusion464
  Tool = -> Extrude344
FEATURE [Sketcher::SketchObject] Sketch352  label="outerSRS031"
  ArcFitTolerance = 0
  FullyConstrained = true
  MakeInternals = false
  Placement = pos=(0,0,-80) rot=(0,0,1;0rad)
  sketch-geometry (6):
    g0: LineSegment StartX=163.5 StartY=0 StartZ=0 EndX=163.5 EndY=-18 EndZ=0
    g1: LineSegment StartX=184 StartY=-38.5 StartZ=0 EndX=221 EndY=-38.5 EndZ=0
    g2: LineSegment StartX=241.5 StartY=0 StartZ=0 EndX=241.5 EndY=-18 EndZ=0
    g3: ArcOfCircle CenterX=184 CenterY=-18 CenterZ=0 NormalX=0 NormalY=0 NormalZ=1 AngleXU=0 Radius=20.5 StartAngle=3.14159 EndAngle=4.71239
    g4: ArcOfCircle CenterX=221 CenterY=-18 CenterZ=0 NormalX=0 NormalY=0 NormalZ=1 AngleXU=0 Radius=20.5 StartAngle=4.71239 EndAngle=6.28319
    g5: LineSegment StartX=163.5 StartY=0 StartZ=0 EndX=241.5 EndY=0 EndZ=0
  constraints (20):
    c: PointOnObject(g5,g-1)
    c: Vertical(g0)
    c: Horizontal(g1)
    c: Vertical(g2)
    c: DistanceY(g2,g5) = 0
    c: Coincident(g0,g3)
    c: Coincident(g1,g3)
    c: Coincident(g1,g4)
    c: Coincident(g2,g4)
    c: Angle(g3) = 1.5708
    c: Angle(g4) = 1.5708
    c: Coincident(g5,g2)
    c: DistanceX(g0) = 163.5
    c: Coincident(g5,g0)
    c: DistanceX(g0,g2) = 78
    c: DistanceY(g0,g0) = 18
    c: DistanceY(g2,g0) = 0
    c: DistanceY(g3,g0) = 0
    c: DistanceY(g4,g2) = 0
    c: DistanceX(g0,g3) = 20.5
FEATURE [Part::Extrusion] Extrude345
  Base = -> Sketch352
  Dir = (0,0,1)
  DirMode = 2
  FaceMakerClass = Part::FaceMakerBullseye
  FaceMakerMode = 3
  LengthFwd = 4
  LengthRev = 0
  Solid = true
  Symmetric = false
FEATURE [Part::Fillet] Fillet088  label="piCoverBottom005"
  Base = -> Extrude345
  EdgeLinks = -> Extrude345 [Edge3,Edge6,Edge9,Edge12,Edge15]
  Edges = 5 edges r=1: [Edge3,Edge6,Edge9,Edge12,Edge15]
FEATURE [Part::Cut] Cut053  label="piCover008"
  Base = -> Cut052
  Tool = -> Fillet088
FEATURE [Sketcher::SketchObject] Sketch353
  ArcFitTolerance = 0
  FullyConstrained = true
  MakeInternals = false
  Placement = pos=(0,0,-77) rot=(0,0,1;0rad)
  sketch-geometry (8):
    g0: LineSegment StartX=158.5 StartY=-25 StartZ=0 EndX=168.5 EndY=-25 EndZ=0
    g1: LineSegment StartX=158.5 StartY=-25 StartZ=0 EndX=158.5 EndY=-32 EndZ=0
    g2: LineSegment StartX=168.5 StartY=-25 StartZ=0 EndX=168.5 EndY=-50.215 EndZ=0
    g3: ArcOfCircle CenterX=181 CenterY=-31.5 CenterZ=0 NormalX=0 NormalY=0 NormalZ=1 AngleXU=0 Radius=22.5056 StartAngle=3.16381 EndAngle=4.12352
    g4: LineSegment StartX=246.5 StartY=-25 StartZ=0 EndX=236.5 EndY=-25 EndZ=0
    g5: LineSegment StartX=236.5 StartY=-25 StartZ=0 EndX=236.5 EndY=-50.215 EndZ=0
    g6: LineSegment StartX=246.5 StartY=-25 StartZ=0 EndX=246.5 EndY=-31.5 EndZ=0
    g7: ArcOfCircle CenterX=223.988 CenterY=-31.5 CenterZ=0 NormalX=0 NormalY=0 NormalZ=1 AngleXU=0 Radius=22.5125 StartAngle=5.30172 EndAngle=6.28319
  constraints (26):
    c: Horizontal(g0)
    c: Coincident(g1,g0)
    c: Vertical(g1)
    c: Coincident(g2,g0)
    c: Vertical(g2)
    c: DistanceX(g0) = 158.5
    c: DistanceX(g0,g0) = 10
    c: Coincident(g3,g2)
    c: Coincident(g3,g1)
    c: DistanceY(g1,g1) = 7
    c: DistanceY(g0) = -25
    c: DistanceY(g3,g0) = 6.5
    c: DistanceX(g1,g3) = 22.5
    c: Horizontal(g4)
    c: Coincident(g5,g4)
    c: Vertical(g5)
    c: DistanceX(g4) = 246.5
    c: DistanceX(g4,g4) = 10
    c: DistanceY(g2,g5) = 0
    c: Horizontal(g4,g0)
    c: Coincident(g6,g4)
    c: Vertical(g6)
    c: DistanceY(g6,g3) = 0
    c: Coincident(g7,g6)
    c: Coincident(g7,g5)
    c: DistanceY(g7,g3) = 0
FEATURE [Part::Extrusion] Extrude346
  Base = -> Sketch353
  Dir = (0,0,1)
  DirMode = 2
  FaceMakerClass = Part::FaceMakerBullseye
  FaceMakerMode = 3
  LengthFwd = 27.5
  LengthRev = 0
  Solid = true
  Symmetric = false
FEATURE [Part::MultiFuse] Fusion465  label="piCover013"
  Shapes = -> [Extrude346,Cut053]
FEATURE [Sketcher::SketchObject] Sketch354
  ArcFitTolerance = 0
  FullyConstrained = true
  MakeInternals = false
  Placement = pos=(0,13,0) rot=(1,0,0;1.5708rad)
  sketch-geometry (6):
    g0: Circle CenterX=163 CenterY=63 CenterZ=0 NormalX=0 NormalY=0 NormalZ=1 AngleXU=0 Radius=1.625
    g1: Circle CenterX=242 CenterY=63 CenterZ=0 NormalX=0 NormalY=0 NormalZ=1 AngleXU=0 Radius=1.625
    g2: Circle CenterX=163 CenterY=-27 CenterZ=0 NormalX=0 NormalY=0 NormalZ=1 AngleXU=0 Radius=1.625
    g3: Circle CenterX=242 CenterY=-27 CenterZ=0 NormalX=0 NormalY=0 NormalZ=1 AngleXU=0 Radius=1.625
    g4: Circle CenterX=163 CenterY=-63 CenterZ=0 NormalX=0 NormalY=0 NormalZ=1 AngleXU=0 Radius=1.625
    g5: Circle CenterX=242 CenterY=-63 CenterZ=0 NormalX=0 NormalY=0 NormalZ=1 AngleXU=0 Radius=1.625
  constraints (18):
    c: Horizontal(g0,g1)
    c: DistanceX(g0) = 163
    c: DistanceY(g0) = 63
    c: DistanceX(g0,g1) = 79
    c: Horizontal(g2,g3)
    c: Equal(g2,g3)
    c: Equal(g2,g1)
    c: Equal(g2,g0)
    c: Diameter(g2) = 3.25
    c: DistanceY(g2,g0) = 90
    c: Vertical(g3,g1)
    c: Vertical(g2,g0)
    c: Vertical(g2,g4)
    c: Vertical(g5,g3)
    c: Equal(g4,g5)
    c: Diameter(g4) = 3.25
    c: DistanceY(g4,g2) = 36
    c: Horizontal(g5,g4)
FEATURE [Part::Extrusion] Extrude347  label="srsCutsForM3s005"
  Base = -> Sketch354
  Dir = (0,-1,2e-16)
  DirMode = 2
  FaceMakerClass = Part::FaceMakerBullseye
  FaceMakerMode = 3
  LengthFwd = 50
  LengthRev = 0
  Placement = pos=(0,-17,0) rot=(0,0,1;0rad)
  Solid = true
  Symmetric = false
FEATURE [Part::Cut] Cut054  label="piHolder003"
  Base = -> Fusion465
  Tool = -> Extrude347
FEATURE [Sketcher::SketchObject] Sketch355
  ArcFitTolerance = 0
  FullyConstrained = true
  MakeInternals = false
  Placement = pos=(0,13,0) rot=(1,0,0;1.5708rad)
  sketch-geometry (6):
    g0: Circle CenterX=163 CenterY=63 CenterZ=0 NormalX=0 NormalY=0 NormalZ=1 AngleXU=0 Radius=1.625
    g1: Circle CenterX=242 CenterY=63 CenterZ=0 NormalX=0 NormalY=0 NormalZ=1 AngleXU=0 Radius=1.625
    g2: Circle CenterX=163 CenterY=-27 CenterZ=0 NormalX=0 NormalY=0 NormalZ=1 AngleXU=0 Radius=1.625
    g3: Circle CenterX=242 CenterY=-27 CenterZ=0 NormalX=0 NormalY=0 NormalZ=1 AngleXU=0 Radius=1.625
    g4: Circle CenterX=163 CenterY=-63 CenterZ=0 NormalX=0 NormalY=0 NormalZ=1 AngleXU=0 Radius=3
    g5: Circle CenterX=242 CenterY=-63 CenterZ=0 NormalX=0 NormalY=0 NormalZ=1 AngleXU=0 Radius=3
  constraints (18):
    c: Horizontal(g0,g1)
    c: DistanceX(g0) = 163
    c: DistanceY(g0) = 63
    c: DistanceX(g0,g1) = 79
    c: Horizontal(g2,g3)
    c: Equal(g2,g3)
    c: Equal(g2,g1)
    c: Equal(g2,g0)
    c: Diameter(g2) = 3.25
    c: DistanceY(g2,g0) = 90
    c: Vertical(g3,g1)
    c: Vertical(g2,g0)
    c: Vertical(g2,g4)
    c: Vertical(g5,g3)
    c: Equal(g4,g5)
    c: Diameter(g4) = 6
    c: DistanceY(g4,g2) = 36
    c: Horizontal(g5,g4)
FEATURE [Part::Extrusion] Extrude348  label="srsCutsForM3s006"
  Base = -> Sketch355
  Dir = (0,-1,2e-16)
  DirMode = 2
  FaceMakerClass = Part::FaceMakerBullseye
  FaceMakerMode = 3
  LengthFwd = 50
  LengthRev = 0
  Placement = pos=(0,-53,0) rot=(0,0,1;0rad)
  Solid = true
  Symmetric = false
FEATURE [Part::Cut] Cut055  label="piHolder004"
  Base = -> Cut054
  Tool = -> Extrude348
FEATURE [Sketcher::SketchObject] Sketch356
  ArcFitTolerance = 1e-06
  FullyConstrained = true
  MakeInternals = false
  Placement = pos=(0,0,-76) rot=(0,0,1;0rad)
  sketch-geometry (4):
    g0: LineSegment StartX=197.3 StartY=-43.5 StartZ=0 EndX=197.3 EndY=-46.5 EndZ=0
    g1: LineSegment StartX=197.3 StartY=-46.5 StartZ=0 EndX=207.7 EndY=-46.5 EndZ=0
    g2: LineSegment StartX=207.7 StartY=-46.5 StartZ=0 EndX=207.7 EndY=-43.5 EndZ=0
    g3: LineSegment StartX=207.7 StartY=-43.5 StartZ=0 EndX=197.3 EndY=-43.5 EndZ=0
  constraints (12):
    c: Coincident(g0,g1)
    c: Coincident(g1,g2)
    c: Coincident(g2,g3)
    c: Coincident(g3,g0)
    c: Vertical(g0)
    c: Vertical(g2)
    c: Horizontal(g1)
    c: Horizontal(g3)
    c: DistanceY(g0,g0) = 3
    c: DistanceX(g0) = 197.3
    c: DistanceX(g3,g3) = 10.4
    c: DistanceY(g0) = -43.5
FEATURE [Part::Extrusion] Extrude349  label="switchCut002"
  Base = -> Sketch356
  Dir = (0,0,1)
  DirMode = 2
  FaceMakerClass = Part::FaceMakerBullseye
  FaceMakerMode = 3
  LengthFwd = 4
  LengthRev = 0
  Reversed = true
  Solid = true
  Symmetric = false
FEATURE [Part::Cut] Cut056  label="piHolder005"
  Base = -> Cut055
  Tool = -> Extrude349
FEATURE [Part::Fillet] Fillet089  label="piCover011"
  Base = -> Cut056
  EdgeLinks = -> Cut056 [Edge108,Edge109,Edge110,Edge111,Edge176,Edge177,Edge178,Edge179,Edge180,Edge181,Edge182,Edge183]
  Edges = 12 edges r=0.5: [Edge108,Edge109,Edge110,Edge111,Edge176,Edge177,Edge178,Edge179,Edge180,Edge181,Edge182,Edge183]
FEATURE [Part::FeaturePython] Tube002  # WARN: FeaturePython — macro-defined, semantics opaque (R4)
  AttacherType = Attacher::AttachEngine3D
  Height = 10
  InnerRadius = 3
  OuterRadius = 6
  Placement = pos=(220,-44.5,-86) rot=(0,0,1;0rad)
FEATURE [Part::MultiFuse] Fusion466
  Refine = true
  Shapes = -> [Tube002,Cylinder097]
FEATURE [Part::Cut] Cut057  label="piCover014"
  Base = -> Fillet089
  Refine = true
  Tool = -> Fusion466
FEATURE [Part::FeaturePython] Tube003  # WARN: FeaturePython — macro-defined, semantics opaque (R4)
  AttacherType = Attacher::AttachEngine3D
  Height = 10
  InnerRadius = 2.5
  OuterRadius = 6
  Placement = pos=(220,-44.5,-86) rot=(0,0,1;0rad)
FEATURE [Part::Cylinder] Cylinder098
  Angle = 360
  AttacherType = Attacher::AttachEngine3D
  FirstAngle = 0
  Height = 5
  Placement = pos=(227,-44.5,-83) rot=(0,1,0;4.71239rad)
  Radius = 1.5
  SecondAngle = 0
FEATURE [Part::Cut] Cut058  label="tube"
  Base = -> Tube003
  Refine = true
  Tool = -> Cylinder098
FEATURE [Part::MultiFuse] Fusion467  label="picover_temp"
  Refine = true
  Shapes = -> [Cut057,Cut058]
FEATURE [Part::Fillet] Fillet090  label="piCover_fillet"
  Base = -> Fusion467
  EdgeLinks = -> Fusion467 [Edge29,Edge116,Edge219,Edge273]
  Edges = 4 edges: [Edge29 r=0.5,Edge116 r=1,Edge219 r=1,Edge273 r=0.5]
FEATURE [App::Part] Part008
  Group = -> [Cut058,Sketch349,Sketch347,Sketch348,Sketch351,Sketch352,Sketch355,Sketch350,Sketch353,Sketch354,Sketch356,Tube003,Cylinder097,Tube002,Fusion465,Fusion466,Loft017,Cut054,Cut052,Cut053,Cut057,Fillet086,Cut055,Cut056,Fillet085,Fillet087,Fillet088,Fillet089,Fusion464,Extrude343,Extrude342,Extrude344,Extrude346,Extrude348,Extrude349,Extrude345,Extrude347,Cylinder098,Fusion467,Fillet090]
  Origin = -> Origin036
FEATURE [Part::Cylinder] Cylinder099
  Angle = 360
  AttacherType = Attacher::AttachEngine3D
  FirstAngle = 0
  Height = 10
  Placement = pos=(221,-25,60) rot=(0,0,1;0rad)
  Radius = 8.5
  SecondAngle = 0
FEATURE [Sketcher::SketchObject] Sketch357
  ArcFitTolerance = 0
  FullyConstrained = true
  MakeInternals = false
  Placement = pos=(0,0,0) rot=(1,0,0;1.5708rad)
  sketch-geometry (4):
    g0: ArcOfCircle CenterX=233.5 CenterY=-58 CenterZ=0 NormalX=0 NormalY=0 NormalZ=1 AngleXU=0 Radius=4 StartAngle=1e-16 EndAngle=3.14159
    g1: ArcOfCircle CenterX=233.5 CenterY=-62 CenterZ=0 NormalX=0 NormalY=0 NormalZ=1 AngleXU=0 Radius=4 StartAngle=3.14159 EndAngle=6.28319
    g2: LineSegment StartX=229.5 StartY=-58 StartZ=0 EndX=229.5 EndY=-62 EndZ=0
    g3: LineSegment StartX=237.5 StartY=-62 StartZ=0 EndX=237.5 EndY=-58 EndZ=0
  constraints (10):
    c: Tangent(g0,g2) = -1.5708
    c: Tangent(g2,g1) = -1.5708
    c: Tangent(g1,g3) = -1.5708
    c: Tangent(g3,g0) = -1.5708
    c: Equal(g0,g1)
    c: Vertical(g2)
    c: DistanceX(g1) = 237.5
    c: DistanceX(g1,g1) = 8
    c: DistanceY(g1,g0) = 4
    c: DistanceY(g1) = -62
FEATURE [Part::Extrusion] Extrude350  label="baseWireCut002"
  Base = -> Sketch357
  Dir = (0,-1,2e-16)
  DirMode = 2
  FaceMakerClass = Part::FaceMakerBullseye
  FaceMakerMode = 3
  LengthFwd = 4
  LengthRev = 0
  Solid = true
  Symmetric = false
FEATURE [Part::Box] Box004  label="Cube002"
  AttacherType = Attacher::AttachEngine3D
  Height = 10
  Length = 38.5
  Placement = pos=(170,-4,50.5) rot=(0,0,-1;1.5708rad)
  Width = 65
FEATURE [Part::FeaturePython] Clone174  label="m2Nuts116"  # WARN: FeaturePython — macro-defined, semantics opaque (R4)
  AttacherType = Attacher::AttachEngine3D
  Fuse = false
  Placement = pos=(0,0,4) rot=(0,0,1;0rad)
  Scale = (1.05,1.05,5)
FEATURE [Part::FeaturePython] Clone175  label="m2Nuts117"  # WARN: FeaturePython — macro-defined, semantics opaque (R4)
  AttacherType = Attacher::AttachEngine3D
  Fuse = false
  Placement = pos=(0,0,0.8) rot=(0,0,1;0rad)
  Scale = (1.05,1.05,1)
FEATURE [Part::FeaturePython] Clone176  label="m2Nuts118"  # WARN: FeaturePython — macro-defined, semantics opaque (R4)
  AttacherType = Attacher::AttachEngine3D
  Fuse = false
  Placement = pos=(0,0,4) rot=(0,0,1;0rad)
  Scale = (1.05,1.05,5)
FEATURE [Part::FeaturePython] Clone177  label="m2Nuts119"  # WARN: FeaturePython — macro-defined, semantics opaque (R4)
  AttacherType = Attacher::AttachEngine3D
  Fuse = false
  Placement = pos=(0,0,0.8) rot=(0,0,1;0rad)
  Scale = (1.05,1.05,1)
FEATURE [Part::FeaturePython] Clone178  label="m2Nuts120"  # WARN: FeaturePython — macro-defined, semantics opaque (R4)
  AttacherType = Attacher::AttachEngine3D
  Fuse = false
  Placement = pos=(0,0,4) rot=(0,0,1;0rad)
  Scale = (1.05,1.05,5)
FEATURE [Part::FeaturePython] Clone179  label="m2Nuts121"  # WARN: FeaturePython — macro-defined, semantics opaque (R4)
  AttacherType = Attacher::AttachEngine3D
  Fuse = false
  Placement = pos=(0,0,0.8) rot=(0,0,1;0rad)
  Scale = (1.05,1.05,1)
FEATURE [Part::FeaturePython] Clone180  label="m2Nuts122"  # WARN: FeaturePython — macro-defined, semantics opaque (R4)
  AttacherType = Attacher::AttachEngine3D
  Fuse = false
  Placement = pos=(0,0,4) rot=(0,0,1;0rad)
  Scale = (1.05,1.05,5)
FEATURE [Part::FeaturePython] Clone181  label="m2Nuts123"  # WARN: FeaturePython — macro-defined, semantics opaque (R4)
  AttacherType = Attacher::AttachEngine3D
  Fuse = false
  Placement = pos=(0,0,0.8) rot=(0,0,1;0rad)
  Scale = (1.05,1.05,1)
FEATURE [Part::FeaturePython] Clone182  label="m2Nuts124"  # WARN: FeaturePython — macro-defined, semantics opaque (R4)
  AttacherType = Attacher::AttachEngine3D
  Fuse = false
  Placement = pos=(0,0,4) rot=(0,0,1;0rad)
  Scale = (1.05,1.05,5)
FEATURE [Part::FeaturePython] Clone183  label="m2Nuts125"  # WARN: FeaturePython — macro-defined, semantics opaque (R4)
  AttacherType = Attacher::AttachEngine3D
  Fuse = false
  Placement = pos=(0,0,0.8) rot=(0,0,1;0rad)
  Scale = (1.05,1.05,1)
FEATURE [Part::FeaturePython] Clone184  label="m2Nuts126"  # WARN: FeaturePython — macro-defined, semantics opaque (R4)
  AttacherType = Attacher::AttachEngine3D
  Fuse = false
  Placement = pos=(0,0,4) rot=(0,0,1;0rad)
  Scale = (1.05,1.05,5)
FEATURE [Part::FeaturePython] Clone185  label="m2Nuts127"  # WARN: FeaturePython — macro-defined, semantics opaque (R4)
  AttacherType = Attacher::AttachEngine3D
  Fuse = false
  Placement = pos=(0,0,0.8) rot=(0,0,1;0rad)
  Scale = (1.05,1.05,1)
FEATURE [Part::FeaturePython] Clone186  label="M3Nut068"  # WARN: FeaturePython — macro-defined, semantics opaque (R4)
  AttacherType = Attacher::AttachEngine3D
  Fuse = false
  Placement = pos=(0,0,4.5) rot=(0,0,1;0rad)
  Scale = (1.1,1.1,5)
FEATURE [Part::FeaturePython] Clone187  label="M3Nut069"  # WARN: FeaturePython — macro-defined, semantics opaque (R4)
  AttacherType = Attacher::AttachEngine3D
  Fuse = false
  Placement = pos=(0,0,0.9) rot=(0,0,1;0rad)
  Scale = (1.1,1.1,1)
FEATURE [Part::FeaturePython] Clone188  label="M3Nut070"  # WARN: FeaturePython — macro-defined, semantics opaque (R4)
  AttacherType = Attacher::AttachEngine3D
  Fuse = false
  Placement = pos=(0,0,4.5) rot=(0,0,1;0rad)
  Scale = (1.1,1.1,5)
FEATURE [Part::FeaturePython] Clone189  label="M3Nut071"  # WARN: FeaturePython — macro-defined, semantics opaque (R4)
  AttacherType = Attacher::AttachEngine3D
  Fuse = false
  Placement = pos=(0,0,0.9) rot=(0,0,1;0rad)
  Scale = (1.1,1.1,1)
FEATURE [Part::FeaturePython] Clone190  label="M3Nut072"  # WARN: FeaturePython — macro-defined, semantics opaque (R4)
  AttacherType = Attacher::AttachEngine3D
  Fuse = false
  Placement = pos=(0,0,4.5) rot=(0,0,1;0rad)
  Scale = (1.1,1.1,5)
FEATURE [Part::FeaturePython] Clone191  label="M3Nut073"  # WARN: FeaturePython — macro-defined, semantics opaque (R4)
  AttacherType = Attacher::AttachEngine3D
  Fuse = false
  Placement = pos=(0,0,0.9) rot=(0,0,1;0rad)
  Scale = (1.1,1.1,1)
FEATURE [Part::FeaturePython] Clone192  label="m2Nuts128"  # WARN: FeaturePython — macro-defined, semantics opaque (R4)
  AttacherType = Attacher::AttachEngine3D
  Fuse = false
  Placement = pos=(0,0,4) rot=(0,0,1;0rad)
  Scale = (1.05,1.05,5)
FEATURE [Part::FeaturePython] Clone193  label="m2Nuts129"  # WARN: FeaturePython — macro-defined, semantics opaque (R4)
  AttacherType = Attacher::AttachEngine3D
  Fuse = false
  Placement = pos=(0,0,0.8) rot=(0,0,1;0rad)
  Scale = (1.05,1.05,1)
FEATURE [Part::FeaturePython] Clone194  label="m2Nuts130"  # WARN: FeaturePython — macro-defined, semantics opaque (R4)
  AttacherType = Attacher::AttachEngine3D
  Fuse = false
  Placement = pos=(0,0,4) rot=(0,0,1;0rad)
  Scale = (1.05,1.05,5)
FEATURE [Part::FeaturePython] Clone195  label="m2Nuts131"  # WARN: FeaturePython — macro-defined, semantics opaque (R4)
  AttacherType = Attacher::AttachEngine3D
  Fuse = false
  Placement = pos=(0,0,0.8) rot=(0,0,1;0rad)
  Scale = (1.05,1.05,1)
FEATURE [Part::FeaturePython] Clone196  label="M3Nut074"  # WARN: FeaturePython — macro-defined, semantics opaque (R4)
  AttacherType = Attacher::AttachEngine3D
  Fuse = false
  Placement = pos=(175,-8,74) rot=(0.57735,0.57735,0.57735;2.0944rad)
  Scale = (1.09,1.09,1)
FEATURE [Part::FeaturePython] Clone197  label="M3Nut075"  # WARN: FeaturePython — macro-defined, semantics opaque (R4)
  AttacherType = Attacher::AttachEngine3D
  Fuse = false
  Placement = pos=(175,-8,74) rot=(0.57735,0.57735,0.57735;2.0944rad)
  Scale = (1.09,1.09,1)
FEATURE [Part::FeaturePython] Clone198  label="M3Nut076"  # WARN: FeaturePython — macro-defined, semantics opaque (R4)
  AttacherType = Attacher::AttachEngine3D
  Fuse = false
  Placement = pos=(175,-8,74) rot=(0.57735,0.57735,0.57735;2.0944rad)
  Scale = (1.09,1.09,1)
FEATURE [Part::FeaturePython] Clone199  label="M3Nut077"  # WARN: FeaturePython — macro-defined, semantics opaque (R4)
  AttacherType = Attacher::AttachEngine3D
  Fuse = false
  Placement = pos=(175,-8,74) rot=(0.57735,0.57735,0.57735;2.0944rad)
  Scale = (1.09,1.09,1)
FEATURE [Part::FeaturePython] Clone200  label="m2Nuts132"  # WARN: FeaturePython — macro-defined, semantics opaque (R4)
  AttacherType = Attacher::AttachEngine3D
  Fuse = false
  Placement = pos=(0,0,4) rot=(0,0,1;0rad)
  Scale = (1.05,1.05,5)
FEATURE [Part::FeaturePython] Clone201  label="m2Nuts133"  # WARN: FeaturePython — macro-defined, semantics opaque (R4)
  AttacherType = Attacher::AttachEngine3D
  Fuse = false
  Placement = pos=(0,0,0.8) rot=(0,0,1;0rad)
  Scale = (1.05,1.05,1)
FEATURE [Part::FeaturePython] Clone202  label="m2Nuts134"  # WARN: FeaturePython — macro-defined, semantics opaque (R4)
  AttacherType = Attacher::AttachEngine3D
  Fuse = false
  Placement = pos=(0,0,4) rot=(0,0,1;0rad)
  Scale = (1.05,1.05,5)
FEATURE [Part::FeaturePython] Clone203  label="m2Nuts135"  # WARN: FeaturePython — macro-defined, semantics opaque (R4)
  AttacherType = Attacher::AttachEngine3D
  Fuse = false
  Placement = pos=(0,0,0.8) rot=(0,0,1;0rad)
  Scale = (1.05,1.05,1)
FEATURE [Part::FeaturePython] Clone204  label="m2Nuts136"  # WARN: FeaturePython — macro-defined, semantics opaque (R4)
  AttacherType = Attacher::AttachEngine3D
  Fuse = false
  Placement = pos=(0,0,4) rot=(0,0,1;0rad)
  Scale = (1.05,1.05,5)
FEATURE [Part::FeaturePython] Clone205  label="m2Nuts137"  # WARN: FeaturePython — macro-defined, semantics opaque (R4)
  AttacherType = Attacher::AttachEngine3D
  Fuse = false
  Placement = pos=(0,0,0.8) rot=(0,0,1;0rad)
  Scale = (1.05,1.05,1)
FEATURE [Part::FeaturePython] Clone206  label="m2Nuts138"  # WARN: FeaturePython — macro-defined, semantics opaque (R4)
  AttacherType = Attacher::AttachEngine3D
  Fuse = false
  Placement = pos=(0,0,4) rot=(0,0,1;0rad)
  Scale = (1.05,1.05,5)
FEATURE [Part::FeaturePython] Clone207  label="m2Nuts139"  # WARN: FeaturePython — macro-defined, semantics opaque (R4)
  AttacherType = Attacher::AttachEngine3D
  Fuse = false
  Placement = pos=(0,0,0.8) rot=(0,0,1;0rad)
  Scale = (1.05,1.05,1)
FEATURE [Part::FeaturePython] Clone208  label="m2Nuts140"  # WARN: FeaturePython — macro-defined, semantics opaque (R4)
  AttacherType = Attacher::AttachEngine3D
  Fuse = false
  Placement = pos=(0,0,4) rot=(0,0,1;0rad)
  Scale = (1.05,1.05,5)
FEATURE [Part::FeaturePython] Clone209  label="m2Nuts141"  # WARN: FeaturePython — macro-defined, semantics opaque (R4)
  AttacherType = Attacher::AttachEngine3D
  Fuse = false
  Placement = pos=(0,0,0.8) rot=(0,0,1;0rad)
  Scale = (1.05,1.05,1)
FEATURE [Part::FeaturePython] Clone210  label="m2Nuts142"  # WARN: FeaturePython — macro-defined, semantics opaque (R4)
  AttacherType = Attacher::AttachEngine3D
  Fuse = false
  Placement = pos=(0,0,4) rot=(0,0,1;0rad)
  Scale = (1.05,1.05,5)
FEATURE [Part::FeaturePython] Clone211  label="m2Nuts143"  # WARN: FeaturePython — macro-defined, semantics opaque (R4)
  AttacherType = Attacher::AttachEngine3D
  Fuse = false
  Placement = pos=(0,0,0.8) rot=(0,0,1;0rad)
  Scale = (1.05,1.05,1)
FEATURE [Part::FeaturePython] Clone212  label="m2Nuts144"  # WARN: FeaturePython — macro-defined, semantics opaque (R4)
  AttacherType = Attacher::AttachEngine3D
  Fuse = false
  Placement = pos=(0,0,4) rot=(0,0,1;0rad)
  Scale = (1.05,1.05,5)
FEATURE [Part::FeaturePython] Clone213  label="m2Nuts145"  # WARN: FeaturePython — macro-defined, semantics opaque (R4)
  AttacherType = Attacher::AttachEngine3D
  Fuse = false
  Placement = pos=(0,0,0.8) rot=(0,0,1;0rad)
  Scale = (1.05,1.05,1)
FEATURE [Part::FeaturePython] Clone214  label="m2Nuts146"  # WARN: FeaturePython — macro-defined, semantics opaque (R4)
  AttacherType = Attacher::AttachEngine3D
  Fuse = false
  Placement = pos=(0,0,4) rot=(0,0,1;0rad)
  Scale = (1.05,1.05,5)
FEATURE [Part::FeaturePython] Clone215  label="m2Nuts147"  # WARN: FeaturePython — macro-defined, semantics opaque (R4)
  AttacherType = Attacher::AttachEngine3D
  Fuse = false
  Placement = pos=(0,0,0.8) rot=(0,0,1;0rad)
  Scale = (1.05,1.05,1)
FEATURE [Part::FeaturePython] Clone216  label="m2Nuts148"  # WARN: FeaturePython — macro-defined, semantics opaque (R4)
  AttacherType = Attacher::AttachEngine3D
  Fuse = false
  Placement = pos=(0,0,4) rot=(0,0,1;0rad)
  Scale = (1.05,1.05,5)
FEATURE [Part::FeaturePython] Clone217  label="m2Nuts149"  # WARN: FeaturePython — macro-defined, semantics opaque (R4)
  AttacherType = Attacher::AttachEngine3D
  Fuse = false
  Placement = pos=(0,0,0.8) rot=(0,0,1;0rad)
  Scale = (1.05,1.05,1)
FEATURE [Part::FeaturePython] Clone218  label="m2Nuts150"  # WARN: FeaturePython — macro-defined, semantics opaque (R4)
  AttacherType = Attacher::AttachEngine3D
  Fuse = false
  Placement = pos=(0,0,4) rot=(0,0,1;0rad)
  Scale = (1.05,1.05,5)
FEATURE [Part::FeaturePython] Clone219  label="m2Nuts151"  # WARN: FeaturePython — macro-defined, semantics opaque (R4)
  AttacherType = Attacher::AttachEngine3D
  Fuse = false
  Placement = pos=(0,0,0.8) rot=(0,0,1;0rad)
  Scale = (1.05,1.05,1)
FEATURE [Part::FeaturePython] Clone220  label="m2Nuts152"  # WARN: FeaturePython — macro-defined, semantics opaque (R4)
  AttacherType = Attacher::AttachEngine3D
  Fuse = false
  Placement = pos=(0,0,4) rot=(0,0,1;0rad)
  Scale = (1.05,1.05,5)
FEATURE [Part::FeaturePython] Clone221  label="m2Nuts153"  # WARN: FeaturePython — macro-defined, semantics opaque (R4)
  AttacherType = Attacher::AttachEngine3D
  Fuse = false
  Placement = pos=(0,0,0.8) rot=(0,0,1;0rad)
  Scale = (1.05,1.05,1)
FEATURE [Part::FeaturePython] Clone222  label="m2Nuts154"  # WARN: FeaturePython — macro-defined, semantics opaque (R4)
  AttacherType = Attacher::AttachEngine3D
  Fuse = false
  Placement = pos=(0,0,4) rot=(0,0,1;0rad)
  Scale = (1.05,1.05,5)
FEATURE [Part::FeaturePython] Clone223  label="m2Nuts155"  # WARN: FeaturePython — macro-defined, semantics opaque (R4)
  AttacherType = Attacher::AttachEngine3D
  Fuse = false
  Placement = pos=(0,0,0.8) rot=(0,0,1;0rad)
  Scale = (1.05,1.05,1)
FEATURE [Part::Cylinder] Cylinder100
  Angle = 360
  AttacherType = Attacher::AttachEngine3D
  FirstAngle = 0
  Height = 10
  Placement = pos=(221,-25,60) rot=(0,0,1;0rad)
  Radius = 8.5
  SecondAngle = 0
FEATURE [Part::Cylinder] Cylinder101 .. Cylinder106  x6 (patterned run collapsed; names and placements below)
  Angle = 360
  AttacherType = Attacher::AttachEngine3D
  FirstAngle = 0
  Height = 8
  Radius = 2
  SecondAngle = 0
FEATURE [Part::Cylinder] Cylinder107
  Angle = 360
  AttacherType = Attacher::AttachEngine3D
  FirstAngle = 0
  Height = 9
  Radius = 2
  SecondAngle = 0
FEATURE [Part::Cylinder] Cylinder108
  Angle = 360
  AttacherType = Attacher::AttachEngine3D
  FirstAngle = 0
  Height = 9
  Radius = 2
  SecondAngle = 0
FEATURE [Part::Cylinder] Cylinder109
  Angle = 360
  AttacherType = Attacher::AttachEngine3D
  FirstAngle = 0
  Height = 9
  Radius = 2
  SecondAngle = 0
FEATURE [Part::Cylinder] Cylinder110 .. Cylinder123  x14 (patterned run collapsed; names and placements below)
  Angle = 360
  AttacherType = Attacher::AttachEngine3D
  FirstAngle = 0
  Height = 8
  Radius = 2
  SecondAngle = 0
FEATURE [Part::MultiFuse] Fusion469
  Shapes = -> [Clone193,Clone192]
FEATURE [Part::MultiFuse] Fusion470  label="m2Cuts056"
  Placement = pos=(182.13,0,-31.13) rot=(0.57735,0.57735,0.57735;4.18879rad)
  Shapes = -> [Cylinder110,Fusion469]
FEATURE [Part::MultiFuse] Fusion472
  Shapes = -> [Clone175,Clone174]
FEATURE [Part::MultiFuse] Fusion473  label="m2Cuts057"
  Placement = pos=(178.54,-14.55,62.5) rot=(1,0,0;3.14159rad)
  Shapes = -> [Cylinder101,Fusion472]
FEATURE [Part::MultiFuse] Fusion474
  Shapes = -> [Clone177,Clone176]
FEATURE [Part::MultiFuse] Fusion475  label="m2Cuts058"
  Placement = pos=(178.54,-34.85,62.5) rot=(1,0,0;3.14159rad)
  Shapes = -> [Cylinder102,Fusion474]
FEATURE [Part::MultiFuse] Fusion476
  Shapes = -> [Clone179,Clone178]
FEATURE [Part::MultiFuse] Fusion477  label="m2Cuts059"
  Placement = pos=(198.84,-14.55,62.5) rot=(1,0,0;3.14159rad)
  Shapes = -> [Cylinder103,Fusion476]
FEATURE [Part::MultiFuse] Fusion478
  Shapes = -> [Clone181,Clone180]
FEATURE [Part::MultiFuse] Fusion479  label="m2Cuts060"
  Placement = pos=(208.09,-14.55,62.5) rot=(1,0,0;3.14159rad)
  Shapes = -> [Cylinder104,Fusion478]
FEATURE [Part::MultiFuse] Fusion480
  Shapes = -> [Clone183,Clone182]
FEATURE [Part::MultiFuse] Fusion481  label="m2Cuts061"
  Placement = pos=(225.89,-14.55,62.5) rot=(1,0,0;3.14159rad)
  Shapes = -> [Cylinder105,Fusion480]
FEATURE [Part::MultiFuse] Fusion482
  Shapes = -> [Clone185,Clone184]
FEATURE [Part::MultiFuse] Fusion483  label="m2Cuts062"
  Placement = pos=(225.89,-34.85,62.5) rot=(1,0,0;3.14159rad)
  Shapes = -> [Cylinder106,Fusion482]
FEATURE [Part::MultiFuse] Fusion484  label="m2Cuts063"
  Shapes = -> [Fusion473,Fusion475,Fusion477,Fusion479,Fusion481,Fusion483]
FEATURE [Part::Cut] Cut060  label="gpsM2Cuts002"
  Base = -> Fusion484
  Tool = -> Box004
FEATURE [Part::MultiFuse] Fusion485
  Shapes = -> [Clone186,Cylinder107]
FEATURE [Part::MultiFuse] Fusion486  label="m3NutCut011"
  Placement = pos=(180.93,0,53.45) rot=(0.57735,0.57735,0.57735;4.18879rad)
  Shapes = -> [Clone187,Fusion485]
FEATURE [Part::MultiFuse] Fusion487
  Shapes = -> [Clone188,Cylinder108]
FEATURE [Part::MultiFuse] Fusion488  label="m3NutCut012"
  Placement = pos=(224.07,0,53.45) rot=(0.57735,0.57735,0.57735;4.18879rad)
  Shapes = -> [Clone189,Fusion487]
FEATURE [Part::MultiFuse] Fusion489
  Shapes = -> [Clone190,Cylinder109]
FEATURE [Part::MultiFuse] Fusion490  label="m3NutCut013"
  Placement = pos=(202.51,0,16.1) rot=(0.57735,0.57735,0.57735;4.18879rad)
  Shapes = -> [Clone191,Fusion489]
FEATURE [Part::MultiFuse] Fusion491  label="co2NutsCuts002"
  Placement = pos=(0,-6,0) rot=(0,0,1;0rad)
  Shapes = -> [Fusion490,Fusion488,Fusion486]
FEATURE [Part::MultiFuse] Fusion492
  Shapes = -> [Clone195,Clone194]
FEATURE [Part::MultiFuse] Fusion493  label="m2Cuts064"
  Placement = pos=(223.15,0,5.42) rot=(0.57735,0.57735,0.57735;4.18879rad)
  Shapes = -> [Cylinder111,Fusion492]
FEATURE [Part::MultiFuse] Fusion494  label="ipsM2NutCuts002"
  Placement = pos=(0,-6,0) rot=(0,0,1;0rad)
  Shapes = -> [Fusion493,Fusion470]
FEATURE [Part::MultiFuse] Fusion499  label="nutCutsForBase002"
  Shapes = -> [Fusion494,Fusion491,Cut060]
FEATURE [Part::MultiFuse] Fusion510
  Shapes = -> [Clone201,Clone200]
FEATURE [Part::MultiFuse] Fusion511  label="m2Cuts065"
  Placement = pos=(173.65,-6,40.16) rot=(0,-0.707107,-0.707107;3.14159rad)
  Shapes = -> [Cylinder112,Fusion510]
FEATURE [Part::MultiFuse] Fusion512
  Shapes = -> [Clone203,Clone202]
FEATURE [Part::MultiFuse] Fusion513  label="m2Cuts066"
  Placement = pos=(186.35,-6,40.16) rot=(0,0.707107,0.707107;3.14159rad)
  Shapes = -> [Cylinder113,Fusion512]
FEATURE [Part::MultiFuse] Fusion514  label="m2NutCuts018"
  Shapes = -> [Fusion511,Fusion513]
FEATURE [Part::MultiFuse] Fusion515
  Shapes = -> [Clone205,Clone204]
FEATURE [Part::MultiFuse] Fusion516  label="m2Cuts067"
  Placement = pos=(173.65,-6,40.16) rot=(0,0.707107,0.707107;3.14159rad)
  Shapes = -> [Cylinder114,Fusion515]
FEATURE [Part::MultiFuse] Fusion517
  Shapes = -> [Clone207,Clone206]
FEATURE [Part::MultiFuse] Fusion518  label="m2Cuts068"
  Placement = pos=(186.35,-6,40.16) rot=(0,0.707107,0.707107;3.14159rad)
  Shapes = -> [Cylinder115,Fusion517]
FEATURE [Part::MultiFuse] Fusion519  label="m2NutCuts019"
  Placement = pos=(0,0,-20.32) rot=(0,0,1;0rad)
  Shapes = -> [Fusion516,Fusion518]
FEATURE [Part::MultiFuse] Fusion520  label="m2NutCuts020"
  Shapes = -> [Fusion514,Fusion519]
FEATURE [Part::MultiFuse] Fusion521
  Shapes = -> [Clone209,Clone208]
FEATURE [Part::MultiFuse] Fusion522  label="m2Cuts069"
  Placement = pos=(173.65,-6,40.16) rot=(0,0.707107,0.707107;3.14159rad)
  Shapes = -> [Cylinder116,Fusion521]
FEATURE [Part::MultiFuse] Fusion523
  Shapes = -> [Clone211,Clone210]
FEATURE [Part::MultiFuse] Fusion524  label="m2Cuts070"
  Placement = pos=(186.35,-6,40.16) rot=(0,0.707107,0.707107;3.14159rad)
  Shapes = -> [Cylinder117,Fusion523]
FEATURE [Part::MultiFuse] Fusion525  label="m2NutCuts021"
  Shapes = -> [Fusion522,Fusion524]
FEATURE [Part::MultiFuse] Fusion526
  Shapes = -> [Clone213,Clone212]
FEATURE [Part::MultiFuse] Fusion527  label="m2Cuts071"
  Placement = pos=(173.65,-6,40.16) rot=(0,0.707107,0.707107;3.14159rad)
  Shapes = -> [Cylinder118,Fusion526]
FEATURE [Part::MultiFuse] Fusion528
  Shapes = -> [Clone215,Clone214]
FEATURE [Part::MultiFuse] Fusion529  label="m2Cuts072"
  Placement = pos=(186.35,-6,40.16) rot=(0,0.707107,0.707107;3.14159rad)
  Shapes = -> [Cylinder119,Fusion528]
FEATURE [Part::MultiFuse] Fusion530  label="m2NutCuts022"
  Placement = pos=(0,0,-20.32) rot=(0,0,1;0rad)
  Shapes = -> [Fusion527,Fusion529]
FEATURE [Part::MultiFuse] Fusion531  label="m2NutCuts023"
  Placement = pos=(45.25,0,0) rot=(0,0,1;0rad)
  Shapes = -> [Fusion525,Fusion530]
FEATURE [Part::MultiFuse] Fusion532
  Shapes = -> [Clone217,Clone216]
FEATURE [Part::MultiFuse] Fusion533  label="m2Cuts073"
  Placement = pos=(173.65,-6,40.16) rot=(0,0.707107,0.707107;3.14159rad)
  Shapes = -> [Cylinder120,Fusion532]
FEATURE [Part::MultiFuse] Fusion534
  Shapes = -> [Clone219,Clone218]
FEATURE [Part::MultiFuse] Fusion535  label="m2Cuts074"
  Placement = pos=(186.35,-6,40.16) rot=(0,0.707107,0.707107;3.14159rad)
  Shapes = -> [Cylinder121,Fusion534]
FEATURE [Part::MultiFuse] Fusion536  label="m2NutCuts024"
  Shapes = -> [Fusion533,Fusion535]
FEATURE [Part::MultiFuse] Fusion537
  Shapes = -> [Clone221,Clone220]
FEATURE [Part::MultiFuse] Fusion538  label="m2Cuts075"
  Placement = pos=(173.65,-6,40.16) rot=(0,0.707107,0.707107;3.14159rad)
  Shapes = -> [Cylinder122,Fusion537]
FEATURE [Part::MultiFuse] Fusion539
  Shapes = -> [Clone223,Clone222]
FEATURE [Part::MultiFuse] Fusion540  label="m2Cuts076"
  Placement = pos=(186.35,-6,40.16) rot=(0,0.707107,0.707107;3.14159rad)
  Shapes = -> [Cylinder123,Fusion539]
FEATURE [Part::MultiFuse] Fusion541  label="m2NutCuts025"
  Placement = pos=(0,0,-20.32) rot=(0,0,1;0rad)
  Shapes = -> [Fusion538,Fusion540]
FEATURE [Part::MultiFuse] Fusion542  label="m2NutCuts026"
  Placement = pos=(22.5,0,11.83) rot=(0,0,1;0rad)
  Shapes = -> [Fusion536,Fusion541]
FEATURE [Part::MultiFuse] Fusion543  label="ic2M2Mount002"
  Shapes = -> [Fusion520,Fusion531,Fusion542]
FEATURE [Sketcher::SketchObject] Sketch358
  ArcFitTolerance = 0
  FullyConstrained = true
  MakeInternals = false
  Placement = pos=(0,0,0) rot=(1,0,0;1.5708rad)
  sketch-geometry (4):
    g0: LineSegment StartX=158.5 StartY=80 StartZ=0 EndX=246.5 EndY=80 EndZ=0
    g1: LineSegment StartX=246.5 StartY=80 StartZ=0 EndX=246.5 EndY=-80 EndZ=0
    g2: LineSegment StartX=246.5 StartY=-80 StartZ=0 EndX=158.5 EndY=-80 EndZ=0
    g3: LineSegment StartX=158.5 StartY=-80 StartZ=0 EndX=158.5 EndY=80 EndZ=0
  constraints (12):
    c: Coincident(g0,g1)
    c: Coincident(g1,g2)
    c: Coincident(g2,g3)
    c: Coincident(g3,g0)
    c: Horizontal(g0)
    c: Horizontal(g2)
    c: Vertical(g1)
    c: Vertical(g3)
    c: DistanceY(g2) = -80
    c: DistanceY(g0) = 80
    c: DistanceX(g2) = 158.5
    c: DistanceX(g2,g2) = 88
FEATURE [Part::Extrusion] Extrude351  label="base047"
  Base = -> Sketch358
  Dir = (0,-1,2e-16)
  DirMode = 2
  FaceMakerClass = Part::FaceMakerBullseye
  FaceMakerMode = 3
  LengthFwd = 4
  LengthRev = 0
  Solid = true
  Symmetric = false
FEATURE [Sketcher::SketchObject] Sketch359
  ArcFitTolerance = 0
  FullyConstrained = true
  MakeInternals = false
  sketch-geometry (15):
    g0: LineSegment StartX=170 StartY=-4 StartZ=0 EndX=170 EndY=-42.5 EndZ=0
    g1: LineSegment StartX=170 StartY=-42.5 StartZ=0 EndX=183 EndY=-42.5 EndZ=0
    g2: LineSegment StartX=183 StartY=-42.5 StartZ=0 EndX=183 EndY=-18 EndZ=0
    g3: LineSegment StartX=183 StartY=-18 StartZ=0 EndX=222 EndY=-18 EndZ=0
    g4: LineSegment StartX=222 StartY=-18 StartZ=0 EndX=222 EndY=-42.5 EndZ=0
    g5: LineSegment StartX=222 StartY=-42.5 StartZ=0 EndX=235 EndY=-42.5 EndZ=0
    g6: LineSegment StartX=235 StartY=-42.5 StartZ=0 EndX=235 EndY=-4 EndZ=0
    g7: LineSegment StartX=235 StartY=-4 StartZ=0 EndX=170 EndY=-4 EndZ=0
    g8: Circle CenterX=178.54 CenterY=-14.55 CenterZ=0 NormalX=0 NormalY=0 NormalZ=1 AngleXU=0 Radius=1.125
    g9: Circle CenterX=178.54 CenterY=-34.85 CenterZ=0 NormalX=0 NormalY=0 NormalZ=1 AngleXU=0 Radius=1.125
    g10: Circle CenterX=225.89 CenterY=-34.85 CenterZ=0 NormalX=0 NormalY=0 NormalZ=1 AngleXU=0 Radius=1.125
    g11: Circle CenterX=225.89 CenterY=-14.55 CenterZ=0 NormalX=0 NormalY=0 NormalZ=1 AngleXU=0 Radius=1.125
    g12: Circle CenterX=198.84 CenterY=-14.55 CenterZ=0 NormalX=0 NormalY=0 NormalZ=1 AngleXU=0 Radius=1.125
    g13: Circle CenterX=208.09 CenterY=-14.55 CenterZ=0 NormalX=0 NormalY=0 NormalZ=1 AngleXU=0 Radius=1.125
    g14: Circle CenterX=191.24 CenterY=-14.55 CenterZ=0 NormalX=0 NormalY=0 NormalZ=1 AngleXU=0 Radius=1.125
  constraints (45):
    c: Vertical(g0)
    c: Coincident(g1,g0)
    c: Horizontal(g1)
    c: Coincident(g2,g1)
    c: Vertical(g2)
    c: Horizontal(g3)
    c: Coincident(g4,g3)
    c: Vertical(g4)
    c: Coincident(g5,g4)
    c: Coincident(g6,g5)
    c: Vertical(g6)
    c: Coincident(g7,g6)
    c: Coincident(g7,g0)
    c: Horizontal(g7)
    c: DistanceX(g0) = 170
    c: DistanceY(g0) = -4
    c: Horizontal(g5)
    c: DistanceX(g6) = 235
    c: DistanceX(g0,g2) = 13
    c: DistanceX(g3,g5) = 13
    c: Coincident(g2,g3)
    c: DistanceY(g2,g0) = 14
    c: DistanceY(g0,g0) = 38.5
    c: DistanceY(g4,g1) = 0
    c: Equal(g8,g11)
    c: Equal(g8,g10)
    c: Equal(g8,g9)
    c: Diameter(g8) = 2.25
    c: DistanceX(g9) = 178.54
    c: DistanceY(g9) = -34.85
    c: DistanceX(g8,g9) = 0
    c: DistanceY(g9,g8) = 20.3
    c: DistanceY(g8,g12) = 0
    c: DistanceX(g8,g12) = 20.3
    c: Equal(g12,g13)
    c: Diameter(g12) = 2.25
    c: Horizontal(g12,g13)
    c: Horizontal(g13,g11)
    c: Horizontal(g10,g9)
    c: Vertical(g10,g11)
    c: DistanceX(g9,g10) = 47.35
    c: DistanceX(g12,g13) = 9.25
    c: DistanceX(g8,g14) = 12.7
    c: Diameter(g14) = 2.25
    c: Horizontal(g14,g8)
FEATURE [Part::Extrusion] Extrude352  label="gpsMount002"
  Base = -> Sketch359
  Dir = (0,0,1)
  DirMode = 2
  FaceMakerClass = Part::FaceMakerBullseye
  FaceMakerMode = 3
  LengthFwd = 5
  LengthRev = 0
  Placement = pos=(0,0,60.5) rot=(0,0,1;0rad)
  Solid = true
  Symmetric = false
FEATURE [Sketcher::SketchObject] Sketch360
  ArcFitTolerance = 0
  FullyConstrained = true
  MakeInternals = false
  Placement = pos=(0,0,0) rot=(1,0,0;1.5708rad)
  sketch-geometry (6):
    g0: Circle CenterX=202.5 CenterY=16.1 CenterZ=0 NormalX=0 NormalY=0 NormalZ=1 AngleXU=0 Radius=1.625
    g1: Circle CenterX=202.5 CenterY=16.1 CenterZ=0 NormalX=0 NormalY=0 NormalZ=1 AngleXU=0 Radius=5
    g2: Circle CenterX=224.07 CenterY=53.45 CenterZ=0 NormalX=0 NormalY=0 NormalZ=1 AngleXU=0 Radius=5
    g3: Circle CenterX=180.93 CenterY=53.45 CenterZ=0 NormalX=0 NormalY=0 NormalZ=1 AngleXU=0 Radius=5
    g4: Circle CenterX=180.93 CenterY=53.45 CenterZ=0 NormalX=0 NormalY=0 NormalZ=1 AngleXU=0 Radius=1.625
    g5: Circle CenterX=224.07 CenterY=53.45 CenterZ=0 NormalX=0 NormalY=0 NormalZ=1 AngleXU=0 Radius=1.625
  constraints (15):
    c: DistanceX(g0) = 202.5
    c: DistanceY(g0) = 16.1
    c: Coincident(g0,g1)
    c: DistanceY(g3,g2) = 0
    c: Equal(g1,g2)
    c: Equal(g1,g3)
    c: Diameter(g1) = 10
    c: Equal(g0,g5)
    c: Equal(g0,g4)
    c: Diameter(g0) = 3.25
    c: DistanceY(g0,g3) = 37.35
    c: DistanceX(g3,g0) = 21.57
    c: DistanceX(g0,g2) = 21.57
    c: Coincident(g5,g2)
    c: Coincident(g4,g3)
FEATURE [Part::Extrusion] Extrude353  label="co2Mount002"
  Base = -> Sketch360
  Dir = (0,-1,2e-16)
  DirMode = 2
  FaceMakerClass = Part::FaceMakerBullseye
  FaceMakerMode = 3
  LengthFwd = 22
  LengthRev = 0
  Solid = true
  Symmetric = false
FEATURE [Sketcher::SketchObject] Sketch361
  ArcFitTolerance = 0
  FullyConstrained = true
  MakeInternals = false
  Placement = pos=(0,0,0) rot=(1,0,0;1.5708rad)
  sketch-geometry (4):
    g0: Circle CenterX=223.145 CenterY=5.42 CenterZ=0 NormalX=0 NormalY=0 NormalZ=1 AngleXU=0 Radius=1.125
    g1: Circle CenterX=182.125 CenterY=-31.13 CenterZ=0 NormalX=0 NormalY=0 NormalZ=1 AngleXU=0 Radius=1.125
    g2: Circle CenterX=182.125 CenterY=-31.13 CenterZ=0 NormalX=0 NormalY=0 NormalZ=1 AngleXU=0 Radius=5
    g3: Circle CenterX=223.145 CenterY=5.42 CenterZ=0 NormalX=0 NormalY=0 NormalZ=1 AngleXU=0 Radius=5
  constraints (10):
    c: DistanceX(g1) = 182.125
    c: DistanceY(g1) = -31.13
    c: DistanceX(g1,g0) = 41.02
    c: DistanceY(g1,g0) = 36.55
    c: Equal(g0,g1)
    c: Diameter(g0) = 2.25
    c: Equal(g3,g2)
    c: Diameter(g3) = 10
    c: Coincident(g2,g1)
    c: Coincident(g3,g0)
FEATURE [Part::Extrusion] Extrude354  label="base048"
  Base = -> Sketch361
  Dir = (0,-1,2e-16)
  DirMode = 2
  FaceMakerClass = Part::FaceMakerBullseye
  FaceMakerMode = 3
  LengthFwd = 18.75
  LengthRev = 0
  Solid = true
  Symmetric = false
FEATURE [Sketcher::SketchObject] Sketch362
  ArcFitTolerance = 0
  FullyConstrained = true
  MakeInternals = false
  Placement = pos=(0,0,0) rot=(1,0,0;1.5708rad)
  sketch-geometry (6):
    g0: LineSegment StartX=178.5 StartY=1.25 StartZ=0 EndX=215 EndY=-35.25 EndZ=0
    g1: LineSegment StartX=227 StartY=-23.25 StartZ=0 EndX=194.4 EndY=9.35 EndZ=0
    g2: LineSegment StartX=215 StartY=-35.25 StartZ=0 EndX=227 EndY=-35.25 EndZ=0
    g3: LineSegment StartX=227 StartY=-35.25 StartZ=0 EndX=227 EndY=-23.25 EndZ=0
    g4: LineSegment StartX=178.5 StartY=1.25 StartZ=0 EndX=178.5 EndY=9.35 EndZ=0
    g5: LineSegment StartX=178.5 StartY=9.35 StartZ=0 EndX=194.4 EndY=9.35 EndZ=0
  constraints (18):
    c: Angle(g0) = -0.785398
    c: Parallel(g1,g0)
    c: Coincident(g2,g0)
    c: Horizontal(g2)
    c: Coincident(g3,g2)
    c: Coincident(g3,g1)
    c: Vertical(g3)
    c: Coincident(g4,g0)
    c: Coincident(g5,g1)
    c: Horizontal(g5)
    c: Vertical(g4)
    c: Coincident(g4,g5)
    c: DistanceX(g2,g2) = 12
    c: DistanceY(g3,g3) = 12
    c: DistanceX(g2) = 227
    c: DistanceY(g2) = -35.25
    c: DistanceY(g4) = 9.35
    c: DistanceX(g0) = 178.5
FEATURE [Part::Extrusion] Extrude355  label="base049"
  Base = -> Sketch362
  Dir = (0,-1,2e-16)
  DirMode = 2
  FaceMakerClass = Part::FaceMakerBullseye
  FaceMakerMode = 3
  LengthFwd = 18.75
  LengthRev = 0
  Solid = true
  Symmetric = false
FEATURE [Part::MultiFuse] Fusion471  label="ipsMount005"
  Shapes = -> [Extrude354,Extrude355]
FEATURE [Sketcher::SketchObject] Sketch363
  ArcFitTolerance = 0
  FullyConstrained = true
  MakeInternals = false
  Placement = pos=(0,0,0) rot=(1,0,0;1.5708rad)
  sketch-geometry (12):
    g0: LineSegment StartX=215 StartY=-35.25 StartZ=0 EndX=227 EndY=-35.25 EndZ=0
    g1: LineSegment StartX=227 StartY=-35.25 StartZ=0 EndX=227 EndY=-23.25 EndZ=0
    g2: LineSegment StartX=178.5 StartY=1.25 StartZ=0 EndX=178.5 EndY=9.35 EndZ=0
    g3: LineSegment StartX=178.5 StartY=9.35 StartZ=0 EndX=194.4 EndY=9.35 EndZ=0
    g4: LineSegment StartX=178.5 StartY=1.25 StartZ=0 EndX=173 EndY=1.25 EndZ=0
    g5: LineSegment StartX=173 StartY=1.25 StartZ=0 EndX=173 EndY=11.25 EndZ=0
    g6: LineSegment StartX=173 StartY=11.25 StartZ=0 EndX=194.4 EndY=11.25 EndZ=0
    g7: LineSegment StartX=194.4 StartY=11.25 StartZ=0 EndX=194.4 EndY=9.35 EndZ=0
    g8: LineSegment StartX=215 StartY=-35.25 StartZ=0 EndX=215 EndY=-39.25 EndZ=0
    g9: LineSegment StartX=215 StartY=-39.25 StartZ=0 EndX=232 EndY=-39.25 EndZ=0
    g10: LineSegment StartX=232 StartY=-39.25 StartZ=0 EndX=232 EndY=-23.25 EndZ=0
    g11: LineSegment StartX=232 StartY=-23.25 StartZ=0 EndX=227 EndY=-23.25 EndZ=0
  constraints (36):
    c: Horizontal(g0)
    c: Coincident(g1,g0)
    c: Vertical(g1)
    c: Horizontal(g3)
    c: Vertical(g2)
    c: Coincident(g2,g3)
    c: DistanceX(g0,g0) = 12
    c: DistanceY(g1,g1) = 12
    c: DistanceX(g0) = 227
    c: DistanceY(g0) = -35.25
    c: DistanceY(g2) = 9.35
    c: DistanceX(g2) = 178.5
    c: DistanceX(g2,g3) = 15.9
    c: DistanceY(g2,g3) = 8.1
    c: Coincident(g4,g2)
    c: Horizontal(g4)
    c: Coincident(g5,g4)
    c: Vertical(g5)
    c: Coincident(g6,g5)
    c: Horizontal(g6)
    c: Coincident(g7,g6)
    c: Coincident(g7,g3)
    c: Vertical(g7)
    c: DistanceY(g5,g5) = 10
    c: DistanceX(g4,g4) = 5.5
    c: Coincident(g8,g0)
    c: Vertical(g8)
    c: Coincident(g9,g8)
    c: Horizontal(g9)
    c: Coincident(g10,g9)
    c: Coincident(g11,g10)
    c: Coincident(g11,g1)
    c: Horizontal(g11)
    c: Vertical(g10)
    c: DistanceY(g8,g8) = 4
    c: DistanceX(g11,g11) = 5
FEATURE [Part::Extrusion] Extrude356  label="ipsMount004"
  Base = -> Sketch363
  Dir = (0,-1,2e-16)
  DirMode = 2
  FaceMakerClass = Part::FaceMakerBullseye
  FaceMakerMode = 3
  LengthFwd = 22
  LengthRev = 0
  Solid = true
  Symmetric = false
FEATURE [Part::MultiFuse] Fusion498  label="base050"
  Shapes = -> [Extrude356,Fusion471,Extrude353,Extrude352,Extrude351]
FEATURE [Sketcher::SketchObject] Sketch364
  ArcFitTolerance = 0
  FullyConstrained = true
  MakeInternals = false
  Placement = pos=(0,-4,0) rot=(1,0,0;1.5708rad)
  sketch-geometry (5):
    g0: LineSegment StartX=178.5 StartY=1.25 StartZ=0 EndX=202.5 EndY=1.25 EndZ=0
    g1: LineSegment StartX=178.5 StartY=1.25 StartZ=0 EndX=215 EndY=-35.25 EndZ=0
    g2: LineSegment StartX=215 StartY=-35.25 StartZ=0 EndX=227 EndY=-35.25 EndZ=0
    g3: LineSegment StartX=227 StartY=-35.25 StartZ=0 EndX=227 EndY=-23.25 EndZ=0
    g4: LineSegment StartX=227 StartY=-23.25 StartZ=0 EndX=202.5 EndY=1.25 EndZ=0
  constraints (15):
    c: Coincident(g2,g1)
    c: Horizontal(g2)
    c: Coincident(g3,g2)
    c: Vertical(g3)
    c: Coincident(g4,g3)
    c: Coincident(g4,g0)
    c: Horizontal(g0)
    c: DistanceX(g0) = 178.5
    c: DistanceY(g0) = 1.25
    c: Coincident(g0,g1)
    c: Angle(g1) = -0.785398
    c: DistanceX(g2) = 227
    c: Angle(g4) = 2.35619
    c: DistanceY(g3) = -23.25
    c: DistanceY(g1) = -35.25
FEATURE [Part::Extrusion] Extrude357  label="ipsCut002"
  Base = -> Sketch364
  Dir = (0,-1,2e-16)
  DirMode = 2
  FaceMakerClass = Part::FaceMakerBullseye
  FaceMakerMode = 3
  LengthFwd = 11
  LengthRev = 0
  Solid = true
  Symmetric = false
FEATURE [Sketcher::SketchObject] Sketch365
  ArcFitTolerance = 0
  FullyConstrained = true
  MakeInternals = false
  Placement = pos=(229.5,0,0) rot=(0.57735,0.57735,0.57735;2.0944rad)
  sketch-geometry (5):
    g0: ArcOfCircle CenterX=-8 CenterY=74 CenterZ=0 NormalX=0 NormalY=0 NormalZ=1 AngleXU=0 Radius=6 StartAngle=1.5708 EndAngle=4.71239
    g1: LineSegment StartX=-8 StartY=68 StartZ=0 EndX=-4 EndY=68 EndZ=0
    g2: LineSegment StartX=-4 StartY=68 StartZ=0 EndX=-4 EndY=80 EndZ=0
    g3: LineSegment StartX=-4 StartY=80 StartZ=0 EndX=-8 EndY=80 EndZ=0
    g4: Circle CenterX=-8 CenterY=74 CenterZ=0 NormalX=0 NormalY=0 NormalZ=1 AngleXU=0 Radius=1.65
  constraints (15):
    c: Vertical(g0,g0)
    c: Vertical(g0,g0)
    c: DistanceY(g0) = 74
    c: DistanceX(g0) = -8
    c: Diameter(g0) = 12
    c: Coincident(g1,g0)
    c: Horizontal(g1)
    c: Coincident(g2,g1)
    c: Vertical(g2)
    c: Coincident(g3,g2)
    c: Coincident(g3,g0)
    c: Horizontal(g3)
    c: DistanceX(g1,g1) = 4
    c: Coincident(g4,g0)
    c: Diameter(g4) = 3.3
FEATURE [Part::Extrusion] Extrude358
  Base = -> Sketch365
  Dir = (1,0,0)
  DirMode = 2
  FaceMakerClass = Part::FaceMakerBullseye
  FaceMakerMode = 3
  LengthFwd = 5.5
  LengthRev = 0
  Placement = pos=(-59.5,0,0) rot=(0,0,1;0rad)
  Solid = true
  Symmetric = false
FEATURE [Part::Cut] Cut061
  Base = -> Extrude358
  Placement = pos=(0,0,-1) rot=(0,0,1;0rad)
  Tool = -> Clone196
FEATURE [Sketcher::SketchObject] Sketch366
  ArcFitTolerance = 0
  FullyConstrained = true
  MakeInternals = false
  Placement = pos=(229.5,0,0) rot=(0.57735,0.57735,0.57735;2.0944rad)
  sketch-geometry (5):
    g0: ArcOfCircle CenterX=-8 CenterY=74 CenterZ=0 NormalX=0 NormalY=0 NormalZ=1 AngleXU=0 Radius=6 StartAngle=1.5708 EndAngle=4.71239
    g1: LineSegment StartX=-8 StartY=68 StartZ=0 EndX=-4 EndY=68 EndZ=0
    g2: LineSegment StartX=-4 StartY=68 StartZ=0 EndX=-4 EndY=80 EndZ=0
    g3: LineSegment StartX=-4 StartY=80 StartZ=0 EndX=-8 EndY=80 EndZ=0
    g4: Circle CenterX=-8 CenterY=74 CenterZ=0 NormalX=0 NormalY=0 NormalZ=1 AngleXU=0 Radius=1.65
  constraints (15):
    c: Vertical(g0,g0)
    c: Vertical(g0,g0)
    c: DistanceY(g0) = 74
    c: DistanceX(g0) = -8
    c: Diameter(g0) = 12
    c: Coincident(g1,g0)
    c: Horizontal(g1)
    c: Coincident(g2,g1)
    c: Vertical(g2)
    c: Coincident(g3,g2)
    c: Coincident(g3,g0)
    c: Horizontal(g3)
    c: DistanceX(g1,g1) = 4
    c: Coincident(g4,g0)
    c: Diameter(g4) = 3.3
FEATURE [Part::Extrusion] Extrude359
  Base = -> Sketch366
  Dir = (1,0,0)
  DirMode = 2
  FaceMakerClass = Part::FaceMakerBullseye
  FaceMakerMode = 3
  LengthFwd = 5.5
  LengthRev = 0
  Placement = pos=(-59.5,0,0) rot=(0,0,1;0rad)
  Solid = true
  Symmetric = false
FEATURE [Part::Cut] Cut062
  Base = -> Extrude359
  Placement = pos=(405,0,147) rot=(0,1,0;3.14159rad)
  Tool = -> Clone197
FEATURE [Part::MultiFuse] Fusion495  label="baseSrsHolder006"
  Shapes = -> [Cut062,Cut061]
FEATURE [Sketcher::SketchObject] Sketch367
  ArcFitTolerance = 0
  FullyConstrained = true
  MakeInternals = false
  Placement = pos=(229.5,0,0) rot=(0.57735,0.57735,0.57735;2.0944rad)
  sketch-geometry (5):
    g0: ArcOfCircle CenterX=-8 CenterY=74 CenterZ=0 NormalX=0 NormalY=0 NormalZ=1 AngleXU=0 Radius=6 StartAngle=1.5708 EndAngle=4.71239
    g1: LineSegment StartX=-8 StartY=68 StartZ=0 EndX=-4 EndY=68 EndZ=0
    g2: LineSegment StartX=-4 StartY=68 StartZ=0 EndX=-4 EndY=80 EndZ=0
    g3: LineSegment StartX=-4 StartY=80 StartZ=0 EndX=-8 EndY=80 EndZ=0
    g4: Circle CenterX=-8 CenterY=74 CenterZ=0 NormalX=0 NormalY=0 NormalZ=1 AngleXU=0 Radius=1.65
  constraints (15):
    c: Vertical(g0,g0)
    c: Vertical(g0,g0)
    c: DistanceY(g0) = 74
    c: DistanceX(g0) = -8
    c: Diameter(g0) = 12
    c: Coincident(g1,g0)
    c: Horizontal(g1)
    c: Coincident(g2,g1)
    c: Vertical(g2)
    c: Coincident(g3,g2)
    c: Coincident(g3,g0)
    c: Horizontal(g3)
    c: DistanceX(g1,g1) = 4
    c: Coincident(g4,g0)
    c: Diameter(g4) = 3.3
FEATURE [Part::Extrusion] Extrude360
  Base = -> Sketch367
  Dir = (1,0,0)
  DirMode = 2
  FaceMakerClass = Part::FaceMakerBullseye
  FaceMakerMode = 3
  LengthFwd = 5.5
  LengthRev = 0
  Placement = pos=(-59.5,0,0) rot=(0,0,1;0rad)
  Solid = true
  Symmetric = false
FEATURE [Part::Cut] Cut063
  Base = -> Extrude360
  Placement = pos=(0,0,-1) rot=(0,0,1;0rad)
  Tool = -> Clone198
FEATURE [Sketcher::SketchObject] Sketch368
  ArcFitTolerance = 0
  FullyConstrained = true
  MakeInternals = false
  Placement = pos=(229.5,0,0) rot=(0.57735,0.57735,0.57735;2.0944rad)
  sketch-geometry (5):
    g0: ArcOfCircle CenterX=-8 CenterY=74 CenterZ=0 NormalX=0 NormalY=0 NormalZ=1 AngleXU=0 Radius=6 StartAngle=1.5708 EndAngle=4.71239
    g1: LineSegment StartX=-8 StartY=68 StartZ=0 EndX=-4 EndY=68 EndZ=0
    g2: LineSegment StartX=-4 StartY=68 StartZ=0 EndX=-4 EndY=80 EndZ=0
    g3: LineSegment StartX=-4 StartY=80 StartZ=0 EndX=-8 EndY=80 EndZ=0
    g4: Circle CenterX=-8 CenterY=74 CenterZ=0 NormalX=0 NormalY=0 NormalZ=1 AngleXU=0 Radius=1.65
  constraints (15):
    c: Vertical(g0,g0)
    c: Vertical(g0,g0)
    c: DistanceY(g0) = 74
    c: DistanceX(g0) = -8
    c: Diameter(g0) = 12
    c: Coincident(g1,g0)
    c: Horizontal(g1)
    c: Coincident(g2,g1)
    c: Vertical(g2)
    c: Coincident(g3,g2)
    c: Coincident(g3,g0)
    c: Horizontal(g3)
    c: DistanceX(g1,g1) = 4
    c: Coincident(g4,g0)
    c: Diameter(g4) = 3.3
FEATURE [Part::Extrusion] Extrude361
  Base = -> Sketch368
  Dir = (1,0,0)
  DirMode = 2
  FaceMakerClass = Part::FaceMakerBullseye
  FaceMakerMode = 3
  LengthFwd = 5.5
  LengthRev = 0
  Placement = pos=(-59.5,0,0) rot=(0,0,1;0rad)
  Solid = true
  Symmetric = false
FEATURE [Part::Cut] Cut064
  Base = -> Extrude361
  Placement = pos=(405,0,147) rot=(0,1,0;3.14159rad)
  Tool = -> Clone199
FEATURE [Part::MultiFuse] Fusion496  label="baseSrsHolder007"
  Placement = pos=(0,0,-90) rot=(0,0,1;0rad)
  Shapes = -> [Cut064,Cut063]
FEATURE [Part::MultiFuse] Fusion497  label="srsHoldsForTheBase005"
  Shapes = -> [Fusion495,Fusion496]
FEATURE [Sketcher::SketchObject] Sketch369
  ArcFitTolerance = 0
  FullyConstrained = true
  MakeInternals = false
  Placement = pos=(170,0,0) rot=(0.57735,0.57735,0.57735;2.0944rad)
  sketch-geometry (4):
    g0: LineSegment StartX=-14 StartY=80.15 StartZ=0 EndX=-4 EndY=80.15 EndZ=0
    g1: LineSegment StartX=-4 StartY=80.15 StartZ=0 EndX=-4 EndY=76.95 EndZ=0
    g2: LineSegment StartX=-4 StartY=76.95 StartZ=0 EndX=-14 EndY=76.95 EndZ=0
    g3: LineSegment StartX=-14 StartY=76.95 StartZ=0 EndX=-14 EndY=80.15 EndZ=0
  constraints (12):
    c: Coincident(g0,g1)
    c: Coincident(g1,g2)
    c: Coincident(g2,g3)
    c: Coincident(g3,g0)
    c: Horizontal(g0)
    c: Horizontal(g2)
    c: Vertical(g1)
    c: Vertical(g3)
    c: DistanceY(g2) = 76.95
    c: DistanceY(g3,g3) = 3.2
    c: DistanceX(g2,g2) = 10
    c: DistanceX(g2) = -14
FEATURE [Part::Extrusion] Extrude362  label="srsCut005"
  Base = -> Sketch369
  Dir = (1,0,0)
  DirMode = 2
  FaceMakerClass = Part::FaceMakerBullseye
  FaceMakerMode = 3
  LengthFwd = 65
  LengthRev = 0
  Solid = true
  Symmetric = false
FEATURE [Part::Cut] Cut065  label="srsHoldsForTheBase004"
  Base = -> Fusion497
  Tool = -> Extrude362
FEATURE [Sketcher::SketchObject] Sketch370
  ArcFitTolerance = 0
  FullyConstrained = true
  MakeInternals = false
  Placement = pos=(0,13,0) rot=(1,0,0;1.5708rad)
  sketch-geometry (6):
    g0: Circle CenterX=163 CenterY=63 CenterZ=0 NormalX=0 NormalY=0 NormalZ=1 AngleXU=0 Radius=1.625
    g1: Circle CenterX=242 CenterY=63 CenterZ=0 NormalX=0 NormalY=0 NormalZ=1 AngleXU=0 Radius=1.625
    g2: Circle CenterX=163 CenterY=-27 CenterZ=0 NormalX=0 NormalY=0 NormalZ=1 AngleXU=0 Radius=1.625
    g3: Circle CenterX=242 CenterY=-27 CenterZ=0 NormalX=0 NormalY=0 NormalZ=1 AngleXU=0 Radius=1.625
    g4: Circle CenterX=163 CenterY=-63 CenterZ=0 NormalX=0 NormalY=0 NormalZ=1 AngleXU=0 Radius=1.625
    g5: Circle CenterX=242 CenterY=-63 CenterZ=0 NormalX=0 NormalY=0 NormalZ=1 AngleXU=0 Radius=1.625
  constraints (18):
    c: Horizontal(g0,g1)
    c: DistanceX(g0) = 163
    c: DistanceY(g0) = 63
    c: DistanceX(g0,g1) = 79
    c: Horizontal(g2,g3)
    c: Equal(g2,g3)
    c: Equal(g2,g1)
    c: Equal(g2,g0)
    c: Diameter(g2) = 3.25
    c: DistanceY(g2,g0) = 90
    c: Vertical(g3,g1)
    c: Vertical(g2,g0)
    c: Vertical(g2,g4)
    c: Vertical(g5,g3)
    c: Equal(g4,g5)
    c: Diameter(g4) = 3.25
    c: DistanceY(g4,g2) = 36
    c: Horizontal(g5,g4)
FEATURE [Part::Extrusion] Extrude363  label="srsCutsForM3s007"
  Base = -> Sketch370
  Dir = (0,-1,2e-16)
  DirMode = 2
  FaceMakerClass = Part::FaceMakerBullseye
  FaceMakerMode = 3
  LengthFwd = 17
  LengthRev = 0
  Solid = true
  Symmetric = false
FEATURE [Part::MultiFuse] Fusion500  label="baseCuts004"
  Shapes = -> [Fusion499,Extrude363,Extrude357]
FEATURE [Part::Cut] Cut066  label="base043"
  Base = -> Fusion498
  Tool = -> Fusion500
FEATURE [Part::MultiFuse] Fusion501  label="base051"
  Shapes = -> [Cut065,Cut066]
FEATURE [Sketcher::SketchObject] Sketch371  label="outerSRS032"
  ArcFitTolerance = 0
  FullyConstrained = true
  MakeInternals = false
  Placement = pos=(0,0,-80) rot=(0,0,1;0rad)
  sketch-geometry (6):
    g0: LineSegment StartX=165 StartY=0 StartZ=0 EndX=165 EndY=-18 EndZ=0
    g1: LineSegment StartX=184 StartY=-37 StartZ=0 EndX=221 EndY=-37 EndZ=0
    g2: LineSegment StartX=240 StartY=0 StartZ=0 EndX=240 EndY=-18 EndZ=0
    g3: ArcOfCircle CenterX=184 CenterY=-18 CenterZ=0 NormalX=0 NormalY=0 NormalZ=1 AngleXU=0 Radius=19 StartAngle=3.14159 EndAngle=4.71239
    g4: ArcOfCircle CenterX=221 CenterY=-18 CenterZ=0 NormalX=0 NormalY=0 NormalZ=1 AngleXU=0 Radius=19 StartAngle=4.71239 EndAngle=6.28319
    g5: LineSegment StartX=165 StartY=0 StartZ=0 EndX=240 EndY=0 EndZ=0
  constraints (20):
    c: PointOnObject(g5,g-1)
    c: Vertical(g0)
    c: Horizontal(g1)
    c: Vertical(g2)
    c: DistanceY(g2,g5) = 0
    c: Coincident(g0,g3)
    c: Coincident(g1,g3)
    c: Coincident(g1,g4)
    c: Coincident(g2,g4)
    c: Angle(g3) = 1.5708
    c: Angle(g4) = 1.5708
    c: Coincident(g5,g2)
    c: DistanceX(g0) = 165
    c: Coincident(g5,g0)
    c: DistanceX(g0,g2) = 75
    c: DistanceY(g0,g0) = 18
    c: DistanceY(g2,g0) = 0
    c: DistanceY(g3,g0) = 0
    c: DistanceY(g4,g2) = 0
    c: DistanceX(g0,g3) = 19
FEATURE [Part::Extrusion] Extrude364
  Base = -> Sketch371
  Dir = (0,0,1)
  DirMode = 2
  FaceMakerClass = Part::FaceMakerBullseye
  FaceMakerMode = 3
  LengthFwd = 4
  LengthRev = 0
  Solid = true
  Symmetric = false
FEATURE [Part::Fillet] Fillet092  label="piCoverBottom006"
  Base = -> Extrude364
  EdgeLinks = -> Extrude364 [Edge3,Edge6,Edge9,Edge12,Edge15,Edge17,Edge18]
  Edges = 7 edges r=1: [Edge3,Edge6,Edge9,Edge12,Edge15,Edge17,Edge18]
FEATURE [Part::MultiFuse] Fusion502  label="base052"
  Shapes = -> [Fusion501,Fillet092]
FEATURE [Sketcher::SketchObject] Sketch372
  ArcFitTolerance = 0
  FullyConstrained = true
  MakeInternals = false
  MapMode = 2
  sketch-geometry (10):
    g0: LineSegment StartX=63 StartY=9.25 StartZ=0 EndX=74 EndY=9.25 EndZ=0
    g1: LineSegment StartX=74 StartY=9.25 StartZ=0 EndX=74 EndY=2 EndZ=0
    g2: LineSegment StartX=74 StartY=2 StartZ=0 EndX=63 EndY=2 EndZ=0
    g3: LineSegment StartX=63 StartY=2 StartZ=0 EndX=63 EndY=9.25 EndZ=0
    g4: LineSegment StartX=-1 StartY=9.25 StartZ=0 EndX=10 EndY=9.25 EndZ=0
    g5: LineSegment StartX=10 StartY=9.25 StartZ=0 EndX=10 EndY=2 EndZ=0
    g6: LineSegment StartX=10 StartY=2 StartZ=0 EndX=-1 EndY=2 EndZ=0
    g7: LineSegment StartX=-1 StartY=2 StartZ=0 EndX=-1 EndY=9.25 EndZ=0
    g8: Circle CenterX=7.47 CenterY=6.47 CenterZ=0 NormalX=0 NormalY=0 NormalZ=1 AngleXU=0 Radius=1.35
    g9: Circle CenterX=65.52 CenterY=6.47 CenterZ=0 NormalX=0 NormalY=0 NormalZ=1 AngleXU=0 Radius=1.35
  constraints (30):
    c: Coincident(g0,g1)
    c: Coincident(g1,g2)
    c: Coincident(g2,g3)
    c: Coincident(g3,g0)
    c: Horizontal(g0)
    c: Horizontal(g2)
    c: Vertical(g1)
    c: Vertical(g3)
    c: Coincident(g4,g5)
    c: Coincident(g5,g6)
    c: Coincident(g6,g7)
    c: Coincident(g7,g4)
    c: Horizontal(g4)
    c: Horizontal(g6)
    c: Vertical(g5)
    c: Vertical(g7)
    c: DistanceY(g6) = 2
    c: DistanceY(g7,g7) = 7.25
    c: DistanceY(g2,g5) = 0
    c: DistanceY(g0,g4) = 0
    c: DistanceX(g2,g2) = 11
    c: DistanceX(g8) = 7.47
    c: Radius(g8) = 1.35
    c: DistanceX(g9) = 65.52
    c: DistanceY(g8,g9) = 0
    c: Radius(g9) = 1.35
    c: DistanceY(g8) = 6.47
    c: DistanceX(g5,g2) = 53
    c: DistanceX(g2,g9) = 2.52
    c: DistanceX(g6,g6) = 11
FEATURE [Part::Extrusion] Extrude365  label="RaberryPiHold009"
  Base = -> Sketch372
  Dir = (0,0,1)
  DirMode = 2
  FaceMakerClass = Part::FaceMakerBullseye
  FaceMakerMode = 3
  LengthFwd = 2
  LengthRev = 0
  Placement = pos=(0,0,20.7) rot=(0,0,1;0rad)
  Solid = true
  Symmetric = false
FEATURE [Part::Fillet] Fillet093  label="piHoldBottomInDone009"
  Base = -> Extrude365
  EdgeLinks = -> Extrude365 [Edge1,Edge4,Edge12,Edge17,Edge19,Edge22]
  Edges = 6 edges: [Edge1 r=2,Edge4 r=1,Edge12 r=1,Edge17 r=2,Edge19 r=1,Edge22 r=1]
FEATURE [Part::Compound] Compound023  label="wearableHolds003"
  Links = -> [Fillet093]
  Placement = pos=(72,9.5,-78) rot=(1,0,0;1.5708rad)
FEATURE [Sketcher::SketchObject] Sketch373
  ArcFitTolerance = 0
  FullyConstrained = true
  MakeInternals = false
  Placement = pos=(0,0,0) rot=(1,0,0;1.5708rad)
  sketch-geometry (12):
    g0: LineSegment StartX=79.5 StartY=-51.5 StartZ=0 EndX=74 EndY=-51.5 EndZ=0
    g1: LineSegment StartX=74 StartY=-51.5 StartZ=0 EndX=74 EndY=-43.5 EndZ=0
    g2: LineSegment StartX=74 StartY=-43.5 StartZ=0 EndX=82.5 EndY=-43.5 EndZ=0
    g3: LineSegment StartX=82.5 StartY=-43.5 StartZ=0 EndX=82.5 EndY=-48.5 EndZ=0
    g4: ArcOfCircle CenterX=79.5 CenterY=-48.5 CenterZ=0 NormalX=0 NormalY=0 NormalZ=1 AngleXU=0 Radius=3 StartAngle=4.71239 EndAngle=6.28319
    g5: Circle CenterX=79.5 CenterY=-48.5 CenterZ=0 NormalX=0 NormalY=0 NormalZ=1 AngleXU=0 Radius=1.75
    g6: LineSegment StartX=142.75 StartY=-51.25 StartZ=0 EndX=137.5 EndY=-51.25 EndZ=0
    g7: LineSegment StartX=142.75 StartY=-43.5 StartZ=0 EndX=134.75 EndY=-43.5 EndZ=0
    g8: LineSegment StartX=134.75 StartY=-43.5 StartZ=0 EndX=134.75 EndY=-48.5 EndZ=0
    g9: ArcOfCircle CenterX=137.5 CenterY=-48.5 CenterZ=0 NormalX=0 NormalY=0 NormalZ=1 AngleXU=0 Radius=2.75 StartAngle=3.14159 EndAngle=4.71239
    g10: LineSegment StartX=142.75 StartY=-51.25 StartZ=0 EndX=142.75 EndY=-43.5 EndZ=0
    g11: Circle CenterX=137.5 CenterY=-48.5 CenterZ=0 NormalX=0 NormalY=0 NormalZ=1 AngleXU=0 Radius=1.75
  constraints (36):
    c: Horizontal(g0)
    c: Coincident(g1,g0)
    c: Vertical(g1)
    c: Coincident(g2,g1)
    c: Horizontal(g2)
    c: Coincident(g3,g2)
    c: Vertical(g3)
    c: Coincident(g4,g3)
    c: Angle(g4) = 1.5708
    c: Coincident(g0,g4)
    c: DistanceY(g0) = -51.5
    c: Vertical(g0,g4)
    c: DistanceX(g4) = 79.5
    c: DistanceY(g4) = -48.5
    c: DistanceX(g0) = 74
    c: Coincident(g5,g4)
    c: Diameter(g5) = 3.5
    c: Horizontal(g6)
    c: Horizontal(g7)
    c: Coincident(g8,g7)
    c: Vertical(g8)
    c: Coincident(g9,g6)
    c: Coincident(g9,g8)
    c: Horizontal(g9,g4)
    c: DistanceX(g4,g9) = 58
    c: Coincident(g10,g6)
    c: Coincident(g10,g7)
    c: Vertical(g10)
    c: Angle(g9) = 1.5708
    c: Horizontal(g9,g8)
    c: Diameter(g9) = 5.5
    c: Coincident(g11,g9)
    c: Diameter(g11) = 3.5
    c: DistanceY(g1,g1) = 8
    c: DistanceY(g2,g7) = 0
    c: DistanceX(g7,g6) = 8
FEATURE [Part::Extrusion] Extrude366  label="piZeroHolds003"
  Base = -> Sketch373
  Dir = (0,-1,2e-16)
  DirMode = 2
  FaceMakerClass = Part::FaceMakerBullseye
  FaceMakerMode = 3
  LengthFwd = 7
  LengthRev = 0
  Solid = true
  Symmetric = false
FEATURE [App::Part] Part009  label="piZeroParts001Holds002"
  Group = -> [Sketch373,Extrude366,Extrude365,Fillet093,Sketch372,Compound023]
  Origin = -> Origin037
  Placement = pos=(94,-4,0) rot=(0,0,1;0rad)
FEATURE [Part::MultiFuse] Fusion506  label="base053"
  Shapes = -> [Fusion502,Part009]
FEATURE [Sketcher::SketchObject] Sketch374
  ArcFitTolerance = 0
  FullyConstrained = true
  MakeInternals = false
  Placement = pos=(0,0,0) rot=(1,0,0;1.5708rad)
  sketch-geometry (46):
    g0: LineSegment StartX=11.75 StartY=19.5 StartZ=0 EndX=21.5 EndY=19.5 EndZ=0
    g1: LineSegment StartX=21.5 StartY=19.5 StartZ=0 EndX=23.75 EndY=22 EndZ=0
    g2: LineSegment StartX=23.75 StartY=22 StartZ=0 EndX=23.75 EndY=25 EndZ=0
    g3: LineSegment StartX=23.75 StartY=25 StartZ=0 EndX=9.5 EndY=25 EndZ=0
    g4: LineSegment StartX=9.5 StartY=25 StartZ=0 EndX=9.5 EndY=22 EndZ=0
    g5: LineSegment StartX=40 StartY=24.5 StartZ=0 EndX=40 EndY=22 EndZ=0
    g6: LineSegment StartX=40 StartY=22 StartZ=0 EndX=42.5 EndY=19.5 EndZ=0
    g7: LineSegment StartX=42.5 StartY=19.5 StartZ=0 EndX=48.7 EndY=19.5 EndZ=0
    g8: LineSegment StartX=48.7 StartY=19.5 StartZ=0 EndX=51.2 EndY=22 EndZ=0
    g9: LineSegment StartX=51.2 StartY=22 StartZ=0 EndX=51.2 EndY=24.5 EndZ=0
    g10: LineSegment StartX=51.2 StartY=24.5 StartZ=0 EndX=40 EndY=24.5 EndZ=0
    g11: LineSegment StartX=52.45 StartY=24.5 StartZ=0 EndX=52.45 EndY=22 EndZ=0
    g12: LineSegment StartX=52.45 StartY=22 StartZ=0 EndX=54.95 EndY=19.5 EndZ=0
    g13: LineSegment StartX=54.95 StartY=19.5 StartZ=0 EndX=61.15 EndY=19.5 EndZ=0
    g14: LineSegment StartX=61.15 StartY=19.5 StartZ=0 EndX=63.65 EndY=22 EndZ=0
    g15: LineSegment StartX=63.65 StartY=22 StartZ=0 EndX=63.65 EndY=24.5 EndZ=0
    g16: LineSegment StartX=63.65 StartY=24.5 StartZ=0 EndX=52.45 EndY=24.5 EndZ=0
    g17: LineSegment StartX=9.5 StartY=22 StartZ=0 EndX=11.75 EndY=19.5 EndZ=0
    g18: ArcOfCircle CenterX=12.3 CenterY=15.45 CenterZ=0 NormalX=0 NormalY=0 NormalZ=1 AngleXU=0 Radius=1 StartAngle=1.5708 EndAngle=3.14159
    g19: LineSegment StartX=11.3 StartY=15.45 StartZ=0 EndX=11.3 EndY=14.2 EndZ=0
    g20: LineSegment StartX=12.3 StartY=16.45 StartZ=0 EndX=16.8 EndY=16.45 EndZ=0
    g21: ArcOfCircle CenterX=16.8 CenterY=15.45 CenterZ=0 NormalX=0 NormalY=0 NormalZ=1 AngleXU=0 Radius=1 StartAngle=3e-16 EndAngle=1.5708
    g22: ArcOfCircle CenterX=16.8 CenterY=14.2 CenterZ=0 NormalX=0 NormalY=0 NormalZ=1 AngleXU=0 Radius=1 StartAngle=4.71239 EndAngle=6.28319
    g23: ArcOfCircle CenterX=12.3 CenterY=14.2 CenterZ=0 NormalX=0 NormalY=0 NormalZ=1 AngleXU=0 Radius=1 StartAngle=3.14159 EndAngle=4.71239
    g24: LineSegment StartX=12.3 StartY=13.2 StartZ=0 EndX=16.8 EndY=13.2 EndZ=0
    g25: LineSegment StartX=17.8 StartY=15.45 StartZ=0 EndX=17.8 EndY=14.2 EndZ=0
    g26: Circle CenterX=18.9 CenterY=16.475 CenterZ=0 NormalX=0 NormalY=0 NormalZ=1 AngleXU=0 Radius=0.5
    g27: Circle CenterX=21.09 CenterY=16.475 CenterZ=0 NormalX=0 NormalY=0 NormalZ=1 AngleXU=0 Radius=0.5
    g28: Circle CenterX=23.28 CenterY=16.475 CenterZ=0 NormalX=0 NormalY=0 NormalZ=1 AngleXU=0 Radius=0.5
    g29: Circle CenterX=25.47 CenterY=16.475 CenterZ=0 NormalX=0 NormalY=0 NormalZ=1 AngleXU=0 Radius=0.5
    g30: LineSegment StartX=44.8 StartY=16.45 StartZ=0 EndX=49.3 EndY=16.45 EndZ=0
    g31: LineSegment StartX=50.3 StartY=15.45 StartZ=0 EndX=50.3 EndY=14.2 EndZ=0
    g32: LineSegment StartX=49.3 StartY=13.2 StartZ=0 EndX=44.8 EndY=13.2 EndZ=0
    g33: LineSegment StartX=43.8 StartY=15.45 StartZ=0 EndX=43.8 EndY=14.2 EndZ=0
    g34: ArcOfCircle CenterX=44.8 CenterY=15.45 CenterZ=0 NormalX=0 NormalY=0 NormalZ=1 AngleXU=0 Radius=1 StartAngle=1.5708 EndAngle=3.14159
    g35: ArcOfCircle CenterX=49.3 CenterY=15.45 CenterZ=0 NormalX=0 NormalY=0 NormalZ=1 AngleXU=0 Radius=1 StartAngle=3e-16 EndAngle=1.5708
    g36: ArcOfCircle CenterX=49.3 CenterY=14.2 CenterZ=0 NormalX=0 NormalY=0 NormalZ=1 AngleXU=0 Radius=1 StartAngle=4.71239 EndAngle=6.28319
    g37: ArcOfCircle CenterX=44.8 CenterY=14.2 CenterZ=0 NormalX=0 NormalY=0 NormalZ=1 AngleXU=0 Radius=1 StartAngle=3.14159 EndAngle=4.71239
    g38: LineSegment StartX=52.25 StartY=15.58 StartZ=0 EndX=52.25 EndY=14.58 EndZ=0
    g39: LineSegment StartX=53.5 StartY=16.83 StartZ=0 EndX=60.5 EndY=16.83 EndZ=0
    g40: LineSegment StartX=53.5 StartY=13.33 StartZ=0 EndX=60.5 EndY=13.33 EndZ=0
    g41: LineSegment StartX=61.75 StartY=15.58 StartZ=0 EndX=61.75 EndY=14.58 EndZ=0
    g42: ArcOfCircle CenterX=53.5 CenterY=15.58 CenterZ=0 NormalX=0 NormalY=0 NormalZ=1 AngleXU=0 Radius=1.25 StartAngle=1.5708 EndAngle=3.14159
    g43: ArcOfCircle CenterX=60.5 CenterY=15.58 CenterZ=0 NormalX=0 NormalY=0 NormalZ=1 AngleXU=0 Radius=1.25 StartAngle=2e-16 EndAngle=1.5708
    g44: ArcOfCircle CenterX=60.5 CenterY=14.58 CenterZ=0 NormalX=0 NormalY=0 NormalZ=1 AngleXU=0 Radius=1.25 StartAngle=4.7124 EndAngle=6.28319
    g45: ArcOfCircle CenterX=53.5 CenterY=14.58 CenterZ=0 NormalX=0 NormalY=0 NormalZ=1 AngleXU=0 Radius=1.25 StartAngle=3.14159 EndAngle=4.71239
  constraints (150):
    c: Horizontal(g0)
    c: Coincident(g0,g1)
    c: Coincident(g1,g2)
    c: Coincident(g2,g3)
    c: Horizontal(g3)
    c: Coincident(g3,g4)
    c: Vertical(g4)
    c: Coincident(g5,g6)
    c: Coincident(g6,g7)
    c: Horizontal(g7)
    c: Coincident(g7,g8)
    c: Coincident(g8,g9)
    c: Vertical(g9)
    c: Coincident(g9,g10)
    c: Coincident(g10,g5)
    c: Coincident(g11,g12)
    c: Coincident(g12,g13)
    c: Horizontal(g13)
    c: Coincident(g13,g14)
    c: Coincident(g14,g15)
    c: Vertical(g15)
    c: Coincident(g15,g16)
    c: Coincident(g16,g11)
    c: Horizontal(g16)
    c: Coincident(g17,g4)
    c: Coincident(g0,g17)
    c: DistanceX(g3) = 9.5
    c: DistanceX(g3,g3) = 14.25
    c: Vertical(g2)
    c: DistanceY(g3) = 25
    c: DistanceY(g4) = 22
    c: DistanceY(g4,g1) = 0
    c: DistanceX(g4,g0) = 2.25
    c: DistanceX(g0,g1) = 2.25
    c: Horizontal(g10)
    c: Vertical(g5)
    c: Vertical(g11)
    c: DistanceX(g5) = 40
    c: DistanceX(g5,g9) = 11.2
    c: DistanceY(g11,g9) = 0
    c: DistanceY(g5,g5) = 2.5
    c: DistanceY(g8,g5) = 0
    c: DistanceY(g11,g8) = 0
    c: DistanceY(g14,g11) = 0
    c: DistanceY(g6,g5) = 2.5
    c: DistanceX(g5,g6) = 2.5
    c: DistanceX(g7,g8) = 2.5
    c: DistanceX(g9,g11) = 1.25
    c: DistanceY(g12,g7) = 0
    c: DistanceX(g11,g12) = 2.5
    c: DistanceX(g13,g14) = 2.5
    c: DistanceX(g11,g15) = 11.2
    c: DistanceY(g0,g4) = 2.5
    c: DistanceY(g5) = 24.5
    c: Coincident(g19,g18)
    c: Vertical(g19)
    c: Horizontal(g20)
    c: Coincident(g21,g20)
    c: Coincident(g23,g19)
    c: Coincident(g24,g23)
    c: Coincident(g24,g22)
    c: Horizontal(g24)
    c: Coincident(g25,g21)
    c: Coincident(g25,g22)
    c: Vertical(g25)
    c: Coincident(g18,g20)
    c: Radius(g18) = 1
    c: Angle(g18) = 1.5708
    c: Angle(g21) = 1.5708
    c: Angle(g22) = 1.5708
    c: Angle(g23) = 1.5708
    c: DistanceX(g23) = 12.3
    c: DistanceY(g23) = 13.2
    c: DistanceX(g19) = 11.3
    c: DistanceY(g23,g19) = 0
    c: DistanceY(g18,g18) = 0
    c: DistanceX(g21,g20) = 0
    c: Radius(g21) = 1
    c: Radius(g22) = 1
    c: DistanceX(g22,g22) = 0
    c: DistanceX(g18,g20) = 4.5
    c: DistanceX(g26) = 18.9
    c: Radius(g26) = 0.5
    c: DistanceY(g26) = 16.475
    c: DistanceX(g26,g27) = 2.19
    c: DistanceY(g26,g27) = 0
    c: DistanceY(g28,g27) = 0
    c: DistanceY(g29,g28) = 0
    c: DistanceX(g27,g28) = 2.19
    c: Radius(g27) = 0.5
    c: Radius(g28) = 0.5
    c: Radius(g29) = 0.5
    c: DistanceX(g28,g29) = 2.19
    c: DistanceY(g23,g18) = 1.25
    c: Horizontal(g30)
    c: Vertical(g31)
    c: Vertical(g33)
    c: Coincident(g33,g34)
    c: Coincident(g33,g37)
    c: Coincident(g32,g37)
    c: Coincident(g32,g36)
    c: Coincident(g31,g36)
    c: Coincident(g31,g35)
    c: Coincident(g30,g35)
    c: Coincident(g30,g34)
    c: Angle(g34) = 1.5708
    c: Angle(g35) = 1.5708
    c: Angle(g37) = 1.5708
    c: Angle(g36) = 1.5708
    c: DistanceY(g18,g34) = 0
    c: DistanceY(g34,g33) = 0
    c: Radius(g34) = 1
    c: DistanceY(g33,g37) = 0
    c: Radius(g37) = 1
    c: Radius(g36) = 1
    c: Radius(g35) = 1
    c: DistanceY(g33,g23) = 0
    c: DistanceY(g31,g36) = 0
    c: Horizontal(g32)
    c: DistanceX(g35,g30) = 0
    c: DistanceX(g32,g32) = 4.5
    c: Vertical(g38)
    c: Horizontal(g39)
    c: Horizontal(g40)
    c: Vertical(g41)
    c: Coincident(g42,g38)
    c: Coincident(g42,g39)
    c: Coincident(g43,g39)
    c: Coincident(g45,g38)
    c: Coincident(g45,g40)
    c: Coincident(g40,g44)
    c: Coincident(g41,g44)
    c: Coincident(g41,g43)
    c: DistanceX(g42) = 53.5
    c: DistanceY(g42) = 15.58
    c: DistanceX(g42,g45) = 0
    c: DistanceY(g45,g42) = 1
    c: Radius(g42) = 1.25
    c: Radius(g44) = 1.25
    c: Radius(g43) = 1.25
    c: DistanceX(g45,g40) = 0
    c: DistanceX(g42,g39) = 0
    c: DistanceY(g42,g43) = 0
    c: DistanceY(g44,g45) = 0
    c: DistanceY(g45,g38) = 0
    c: DistanceX(g42,g43) = 7
    c: DistanceX(g18,g34) = 32.5
    c: DistanceY(g41,g44) = 0
    c: DistanceY(g43,g41) = 0
    c: Angle(g42) = 1.5708
FEATURE [Part::Extrusion] Extrude367  label="lightBottomCutDone015"
  Base = -> Sketch374
  Dir = (0,-1,2e-16)
  DirMode = 2
  FaceMakerClass = Part::FaceMakerBullseye
  FaceMakerMode = 3
  LengthFwd = 5
  LengthRev = 0
  Placement = pos=(0,2,0) rot=(0,0,1;0rad)
  Solid = true
  Symmetric = false
FEATURE [Sketcher::SketchObject] Sketch375
  ArcFitTolerance = 0
  FullyConstrained = true
  MakeInternals = false
  Placement = pos=(0,0,0) rot=(1,0,0;1.5708rad)
  sketch-geometry (8):
    g0: ArcOfCircle CenterX=11.8 CenterY=15.45 CenterZ=0 NormalX=0 NormalY=0 NormalZ=1 AngleXU=0 Radius=1.25 StartAngle=1.5708 EndAngle=3.14159
    g1: ArcOfCircle CenterX=17.3 CenterY=15.45 CenterZ=0 NormalX=0 NormalY=0 NormalZ=1 AngleXU=0 Radius=1.25 StartAngle=-9e-16 EndAngle=1.5708
    g2: ArcOfCircle CenterX=16.8 CenterY=14.2 CenterZ=0 NormalX=0 NormalY=0 NormalZ=1 AngleXU=0 Radius=1.75 StartAngle=4.71239 EndAngle=6.28319
    g3: ArcOfCircle CenterX=12.3 CenterY=14.2 CenterZ=0 NormalX=0 NormalY=0 NormalZ=1 AngleXU=0 Radius=1.75 StartAngle=3.14159 EndAngle=4.71239
    g4: LineSegment StartX=11.8 StartY=16.7 StartZ=0 EndX=17.3 EndY=16.7 EndZ=0
    g5: LineSegment StartX=18.55 StartY=15.45 StartZ=0 EndX=18.55 EndY=14.2 EndZ=0
    g6: LineSegment StartX=16.8 StartY=12.45 StartZ=0 EndX=12.3 EndY=12.45 EndZ=0
    g7: LineSegment StartX=10.55 StartY=14.2 StartZ=0 EndX=10.55 EndY=15.45 EndZ=0
  constraints (28):
    c: Coincident(g4,g0)
    c: Coincident(g4,g1)
    c: Horizontal(g4)
    c: Coincident(g5,g1)
    c: Coincident(g5,g2)
    c: Coincident(g6,g2)
    c: Coincident(g6,g3)
    c: Horizontal(g6)
    c: Coincident(g7,g3)
    c: Coincident(g7,g0)
    c: Vertical(g7)
    c: Radius(g0) = 1.25
    c: DistanceY(g0,g0) = 0
    c: Angle(g3) = 1.5708
    c: DistanceY(g3,g3) = 0
    c: DistanceY(g3,g0) = 1.25
    c: DistanceY(g3) = 14.2
    c: Radius(g3) = 1.75
    c: Radius(g2) = 1.75
    c: Radius(g1) = 1.25
    c: DistanceX(g6,g6) = 4.5
    c: DistanceX(g3) = 12.3
    c: DistanceY(g1,g1) = 0
    c: DistanceX(g2,g2) = 0
    c: Angle(g1) = 1.5708
    c: Angle(g2) = 1.5708
    c: Vertical(g5)
    c: DistanceX(g0,g0) = 0
FEATURE [Part::Extrusion] Extrude369  label="buttonCuts031"
  Base = -> Sketch375
  Dir = (0,-1,2e-16)
  DirMode = 2
  FaceMakerClass = Part::FaceMakerBullseye
  FaceMakerMode = 3
  LengthFwd = 0.6
  LengthRev = 0
  Placement = pos=(32.5,2,0) rot=(0,0,1;0rad)
  Solid = true
  Symmetric = false
FEATURE [Sketcher::SketchObject] Sketch376
  ArcFitTolerance = 0
  FullyConstrained = true
  MakeInternals = false
  Placement = pos=(0,0,0) rot=(1,0,0;1.5708rad)
  sketch-geometry (8):
    g0: ArcOfCircle CenterX=11.8 CenterY=15.45 CenterZ=0 NormalX=0 NormalY=0 NormalZ=1 AngleXU=0 Radius=1.25 StartAngle=1.5708 EndAngle=3.14159
    g1: ArcOfCircle CenterX=17.3 CenterY=15.45 CenterZ=0 NormalX=0 NormalY=0 NormalZ=1 AngleXU=0 Radius=1.25 StartAngle=-9e-16 EndAngle=1.5708
    g2: ArcOfCircle CenterX=16.8 CenterY=14.2 CenterZ=0 NormalX=0 NormalY=0 NormalZ=1 AngleXU=0 Radius=1.75 StartAngle=4.71239 EndAngle=6.28319
    g3: ArcOfCircle CenterX=12.3 CenterY=14.2 CenterZ=0 NormalX=0 NormalY=0 NormalZ=1 AngleXU=0 Radius=1.75 StartAngle=3.14159 EndAngle=4.71239
    g4: LineSegment StartX=11.8 StartY=16.7 StartZ=0 EndX=17.3 EndY=16.7 EndZ=0
    g5: LineSegment StartX=18.55 StartY=15.45 StartZ=0 EndX=18.55 EndY=14.2 EndZ=0
    g6: LineSegment StartX=16.8 StartY=12.45 StartZ=0 EndX=12.3 EndY=12.45 EndZ=0
    g7: LineSegment StartX=10.55 StartY=14.2 StartZ=0 EndX=10.55 EndY=15.45 EndZ=0
  constraints (28):
    c: Coincident(g4,g0)
    c: Coincident(g4,g1)
    c: Horizontal(g4)
    c: Coincident(g5,g1)
    c: Coincident(g5,g2)
    c: Coincident(g6,g2)
    c: Coincident(g6,g3)
    c: Horizontal(g6)
    c: Coincident(g7,g3)
    c: Coincident(g7,g0)
    c: Vertical(g7)
    c: Radius(g0) = 1.25
    c: DistanceY(g0,g0) = 0
    c: Angle(g3) = 1.5708
    c: DistanceY(g3,g3) = 0
    c: DistanceY(g3,g0) = 1.25
    c: DistanceY(g3) = 14.2
    c: Radius(g3) = 1.75
    c: Radius(g2) = 1.75
    c: Radius(g1) = 1.25
    c: DistanceX(g6,g6) = 4.5
    c: DistanceX(g3) = 12.3
    c: DistanceY(g1,g1) = 0
    c: DistanceX(g2,g2) = 0
    c: Angle(g1) = 1.5708
    c: Angle(g2) = 1.5708
    c: Vertical(g5)
    c: DistanceX(g0,g0) = 0
FEATURE [Part::Extrusion] Extrude368  label="buttonCuts030"
  Base = -> Sketch376
  Dir = (0,-1,2e-16)
  DirMode = 2
  FaceMakerClass = Part::FaceMakerBullseye
  FaceMakerMode = 3
  LengthFwd = 0.6
  LengthRev = 0
  Placement = pos=(0,2,0) rot=(0,0,1;0rad)
  Solid = true
  Symmetric = false
FEATURE [Part::MultiFuse] Fusion503  label="bottomButtonCuts017"
  Shapes = -> [Extrude369,Extrude368]
FEATURE [Part::MultiFuse] Fusion504  label="bottomCuts013"
  Shapes = -> [Fusion503,Extrude367]
FEATURE [Part::Compound] Compound024  label="wearableCuts007"
  Links = -> [Fusion504]
  Placement = pos=(72,9.5,-78) rot=(1,0,0;1.5708rad)
FEATURE [Sketcher::SketchObject] Sketch377
  ArcFitTolerance = 0
  FullyConstrained = true
  MakeInternals = false
  Placement = pos=(0,0,-77.25) rot=(0,0,1;0rad)
  sketch-geometry (6):
    g0: ArcOfCircle CenterX=125.5 CenterY=-4.58 CenterZ=0 NormalX=0 NormalY=0 NormalZ=1 AngleXU=0 Radius=2.4 StartAngle=1.5708 EndAngle=3.14159
    g1: ArcOfCircle CenterX=132.5 CenterY=-4.58 CenterZ=0 NormalX=0 NormalY=0 NormalZ=1 AngleXU=0 Radius=2.4 StartAngle=0 EndAngle=1.5708
    g2: LineSegment StartX=125.5 StartY=-2.18 StartZ=0 EndX=132.5 EndY=-2.18 EndZ=0
    g3: LineSegment StartX=134.9 StartY=-4.58 StartZ=0 EndX=134.9 EndY=-8.75 EndZ=0
    g4: LineSegment StartX=134.9 StartY=-8.75 StartZ=0 EndX=123.1 EndY=-8.75 EndZ=0
    g5: LineSegment StartX=123.1 StartY=-8.75 StartZ=0 EndX=123.1 EndY=-4.58 EndZ=0
  constraints (20):
    c: Vertical(g1,g1)
    c: Horizontal(g1,g0)
    c: Horizontal(g0,g0)
    c: DistanceX(g1) = 132.5
    c: Vertical(g1,g3)
    c: Horizontal(g1,g0)
    c: Coincident(g2,g0)
    c: Coincident(g2,g1)
    c: Coincident(g3,g1)
    c: Coincident(g5,g0)
    c: DistanceY(g0) = -4.58
    c: Horizontal(g4)
    c: DistanceY(g4) = -8.75
    c: Vertical(g5)
    c: DistanceX(g5) = 123.1
    c: Horizontal(g0,g1)
    c: Coincident(g4,g5)
    c: Diameter(g1) = 4.8
    c: Angle(g0) = 1.5708
    c: Coincident(g3,g4)
FEATURE [Part::Extrusion] Extrude370  label="usbCCut004"
  Base = -> Sketch377
  Dir = (0,0,1)
  DirMode = 2
  FaceMakerClass = Part::FaceMakerBullseye
  FaceMakerMode = 3
  LengthFwd = 10
  LengthRev = 0
  Reversed = true
  Solid = true
  Symmetric = false
FEATURE [Sketcher::SketchObject] Sketch378
  ArcFitTolerance = 0
  FullyConstrained = true
  MakeInternals = false
  Placement = pos=(0,0,-78) rot=(0,0,1;0rad)
  sketch-geometry (8):
    g0: ArcOfCircle CenterX=81 CenterY=-12 CenterZ=0 NormalX=0 NormalY=0 NormalZ=1 AngleXU=0 Radius=3.25 StartAngle=1.5708 EndAngle=3.14159
    g1: ArcOfCircle CenterX=81 CenterY=-14 CenterZ=0 NormalX=0 NormalY=0 NormalZ=1 AngleXU=0 Radius=3.25 StartAngle=3.14159 EndAngle=4.71239
    g2: ArcOfCircle CenterX=135 CenterY=-14 CenterZ=0 NormalX=0 NormalY=0 NormalZ=1 AngleXU=0 Radius=3.25 StartAngle=4.71239 EndAngle=6.28319
    g3: ArcOfCircle CenterX=135 CenterY=-12 CenterZ=0 NormalX=0 NormalY=0 NormalZ=1 AngleXU=0 Radius=3.25 StartAngle=0 EndAngle=1.5708
    g4: LineSegment StartX=81 StartY=-17.25 StartZ=0 EndX=135 EndY=-17.25 EndZ=0
    g5: LineSegment StartX=138.25 StartY=-14 StartZ=0 EndX=138.25 EndY=-12 EndZ=0
    g6: LineSegment StartX=135 StartY=-8.75 StartZ=0 EndX=81 EndY=-8.75 EndZ=0
    g7: LineSegment StartX=77.75 StartY=-12 StartZ=0 EndX=77.75 EndY=-14 EndZ=0
  constraints (30):
    c: Horizontal(g3,g0)
    c: Vertical(g1,g0)
    c: Vertical(g3,g2)
    c: Vertical(g2,g2)
    c: Vertical(g2,g3)
    c: Vertical(g1,g1)
    c: Vertical(g0,g0)
    c: Horizontal(g0,g0)
    c: Horizontal(g3,g3)
    c: Horizontal(g1,g1)
    c: DistanceY(g3) = -8.75
    c: Vertical(g0,g1)
    c: Horizontal(g3,g0)
    c: Vertical(g2,g3)
    c: Horizontal(g2,g2)
    c: Horizontal(g2,g1)
    c: DistanceX(g2) = 135
    c: DistanceY(g2) = -14
    c: DistanceY(g2,g3) = 2
    c: DistanceX(g0,g3) = 54
    c: Coincident(g4,g1)
    c: Coincident(g4,g2)
    c: Coincident(g5,g2)
    c: Coincident(g5,g3)
    c: Coincident(g6,g3)
    c: Coincident(g6,g0)
    c: Horizontal(g6)
    c: Tangent(g6,g0)
    c: Coincident(g7,g0)
    c: Coincident(g7,g1)
FEATURE [Part::Extrusion] Extrude371  label="microUSBCut004"
  Base = -> Sketch378
  Dir = (0,0,1)
  DirMode = 2
  FaceMakerClass = Part::FaceMakerBullseye
  FaceMakerMode = 3
  LengthFwd = 10
  LengthRev = 0
  Reversed = true
  Solid = true
  Symmetric = false
FEATURE [Part::MultiFuse] Fusion505  label="wireCuts004"
  Shapes = -> [Extrude370,Extrude371]
FEATURE [App::Part] Part010  label="piZeroParts004"
  Group = -> [Extrude367,Extrude368,Extrude369,Fusion503,Fusion504,Sketch374,Sketch375,Sketch376,Compound024,Sketch377,Extrude370,Sketch378,Extrude371,Fusion505]
  Origin = -> Origin038
  Placement = pos=(94,-4,0) rot=(0,0,1;0rad)
FEATURE [Part::FeaturePython] Connect002  # WARN: FeaturePython — macro-defined, semantics opaque (R4)
  Objects = -> [Part010]
  Tolerance = 0
FEATURE [Part::Cut] Cut067  label="base044"
  Base = -> Fusion506
  Tool = -> Connect002
FEATURE [Sketcher::SketchObject] Sketch379
  ArcFitTolerance = 0
  FullyConstrained = true
  MakeInternals = false
  Placement = pos=(0,0,0) rot=(1,0,0;1.5708rad)
  sketch-geometry (46):
    g0: LineSegment StartX=11.75 StartY=19.5 StartZ=0 EndX=21.5 EndY=19.5 EndZ=0
    g1: LineSegment StartX=21.5 StartY=19.5 StartZ=0 EndX=23.75 EndY=22 EndZ=0
    g2: LineSegment StartX=23.75 StartY=22 StartZ=0 EndX=23.75 EndY=25 EndZ=0
    g3: LineSegment StartX=23.75 StartY=25 StartZ=0 EndX=9.5 EndY=25 EndZ=0
    g4: LineSegment StartX=9.5 StartY=25 StartZ=0 EndX=9.5 EndY=22 EndZ=0
    g5: LineSegment StartX=40 StartY=24.5 StartZ=0 EndX=40 EndY=22 EndZ=0
    g6: LineSegment StartX=40 StartY=22 StartZ=0 EndX=42.5 EndY=19.5 EndZ=0
    g7: LineSegment StartX=42.5 StartY=19.5 StartZ=0 EndX=48.7 EndY=19.5 EndZ=0
    g8: LineSegment StartX=48.7 StartY=19.5 StartZ=0 EndX=51.2 EndY=22 EndZ=0
    g9: LineSegment StartX=51.2 StartY=22 StartZ=0 EndX=51.2 EndY=24.5 EndZ=0
    g10: LineSegment StartX=51.2 StartY=24.5 StartZ=0 EndX=40 EndY=24.5 EndZ=0
    g11: LineSegment StartX=52.45 StartY=24.5 StartZ=0 EndX=52.45 EndY=22 EndZ=0
    g12: LineSegment StartX=52.45 StartY=22 StartZ=0 EndX=54.95 EndY=19.5 EndZ=0
    g13: LineSegment StartX=54.95 StartY=19.5 StartZ=0 EndX=61.15 EndY=19.5 EndZ=0
    g14: LineSegment StartX=61.15 StartY=19.5 StartZ=0 EndX=63.65 EndY=22 EndZ=0
    g15: LineSegment StartX=63.65 StartY=22 StartZ=0 EndX=63.65 EndY=24.5 EndZ=0
    g16: LineSegment StartX=63.65 StartY=24.5 StartZ=0 EndX=52.45 EndY=24.5 EndZ=0
    g17: LineSegment StartX=9.5 StartY=22 StartZ=0 EndX=11.75 EndY=19.5 EndZ=0
    g18: ArcOfCircle CenterX=12.3 CenterY=15.45 CenterZ=0 NormalX=0 NormalY=0 NormalZ=1 AngleXU=0 Radius=1 StartAngle=1.5708 EndAngle=3.14159
    g19: LineSegment StartX=11.3 StartY=15.45 StartZ=0 EndX=11.3 EndY=14.2 EndZ=0
    g20: LineSegment StartX=12.3 StartY=16.45 StartZ=0 EndX=16.8 EndY=16.45 EndZ=0
    g21: ArcOfCircle CenterX=16.8 CenterY=15.45 CenterZ=0 NormalX=0 NormalY=0 NormalZ=1 AngleXU=0 Radius=1 StartAngle=3e-16 EndAngle=1.5708
    g22: ArcOfCircle CenterX=16.8 CenterY=14.2 CenterZ=0 NormalX=0 NormalY=0 NormalZ=1 AngleXU=0 Radius=1 StartAngle=4.71239 EndAngle=6.28319
    g23: ArcOfCircle CenterX=12.3 CenterY=14.2 CenterZ=0 NormalX=0 NormalY=0 NormalZ=1 AngleXU=0 Radius=1 StartAngle=3.14159 EndAngle=4.71239
    g24: LineSegment StartX=12.3 StartY=13.2 StartZ=0 EndX=16.8 EndY=13.2 EndZ=0
    g25: LineSegment StartX=17.8 StartY=15.45 StartZ=0 EndX=17.8 EndY=14.2 EndZ=0
    g26: Circle CenterX=18.9 CenterY=16.475 CenterZ=0 NormalX=0 NormalY=0 NormalZ=1 AngleXU=0 Radius=0.5
    g27: Circle CenterX=21.09 CenterY=16.475 CenterZ=0 NormalX=0 NormalY=0 NormalZ=1 AngleXU=0 Radius=0.5
    g28: Circle CenterX=23.28 CenterY=16.475 CenterZ=0 NormalX=0 NormalY=0 NormalZ=1 AngleXU=0 Radius=0.5
    g29: Circle CenterX=25.47 CenterY=16.475 CenterZ=0 NormalX=0 NormalY=0 NormalZ=1 AngleXU=0 Radius=0.5
    g30: LineSegment StartX=44.8 StartY=16.45 StartZ=0 EndX=49.3 EndY=16.45 EndZ=0
    g31: LineSegment StartX=50.3 StartY=15.45 StartZ=0 EndX=50.3 EndY=14.2 EndZ=0
    g32: LineSegment StartX=49.3 StartY=13.2 StartZ=0 EndX=44.8 EndY=13.2 EndZ=0
    g33: LineSegment StartX=43.8 StartY=15.45 StartZ=0 EndX=43.8 EndY=14.2 EndZ=0
    g34: ArcOfCircle CenterX=44.8 CenterY=15.45 CenterZ=0 NormalX=0 NormalY=0 NormalZ=1 AngleXU=0 Radius=1 StartAngle=1.5708 EndAngle=3.14159
    g35: ArcOfCircle CenterX=49.3 CenterY=15.45 CenterZ=0 NormalX=0 NormalY=0 NormalZ=1 AngleXU=0 Radius=1 StartAngle=3e-16 EndAngle=1.5708
    g36: ArcOfCircle CenterX=49.3 CenterY=14.2 CenterZ=0 NormalX=0 NormalY=0 NormalZ=1 AngleXU=0 Radius=1 StartAngle=4.71239 EndAngle=6.28319
    g37: ArcOfCircle CenterX=44.8 CenterY=14.2 CenterZ=0 NormalX=0 NormalY=0 NormalZ=1 AngleXU=0 Radius=1 StartAngle=3.14159 EndAngle=4.71239
    g38: LineSegment StartX=52.25 StartY=15.58 StartZ=0 EndX=52.25 EndY=14.58 EndZ=0
    g39: LineSegment StartX=53.5 StartY=16.83 StartZ=0 EndX=60.5 EndY=16.83 EndZ=0
    g40: LineSegment StartX=53.5 StartY=13.33 StartZ=0 EndX=60.5 EndY=13.33 EndZ=0
    g41: LineSegment StartX=61.75 StartY=15.58 StartZ=0 EndX=61.75 EndY=14.58 EndZ=0
    g42: ArcOfCircle CenterX=53.5 CenterY=15.58 CenterZ=0 NormalX=0 NormalY=0 NormalZ=1 AngleXU=0 Radius=1.25 StartAngle=1.5708 EndAngle=3.14159
    g43: ArcOfCircle CenterX=60.5 CenterY=15.58 CenterZ=0 NormalX=0 NormalY=0 NormalZ=1 AngleXU=0 Radius=1.25 StartAngle=2e-16 EndAngle=1.5708
    g44: ArcOfCircle CenterX=60.5 CenterY=14.58 CenterZ=0 NormalX=0 NormalY=0 NormalZ=1 AngleXU=0 Radius=1.25 StartAngle=4.7124 EndAngle=6.28319
    g45: ArcOfCircle CenterX=53.5 CenterY=14.58 CenterZ=0 NormalX=0 NormalY=0 NormalZ=1 AngleXU=0 Radius=1.25 StartAngle=3.14159 EndAngle=4.71239
  constraints (150):
    c: Horizontal(g0)
    c: Coincident(g0,g1)
    c: Coincident(g1,g2)
    c: Coincident(g2,g3)
    c: Horizontal(g3)
    c: Coincident(g3,g4)
    c: Vertical(g4)
    c: Coincident(g5,g6)
    c: Coincident(g6,g7)
    c: Horizontal(g7)
    c: Coincident(g7,g8)
    c: Coincident(g8,g9)
    c: Vertical(g9)
    c: Coincident(g9,g10)
    c: Coincident(g10,g5)
    c: Coincident(g11,g12)
    c: Coincident(g12,g13)
    c: Horizontal(g13)
    c: Coincident(g13,g14)
    c: Coincident(g14,g15)
    c: Vertical(g15)
    c: Coincident(g15,g16)
    c: Coincident(g16,g11)
    c: Horizontal(g16)
    c: Coincident(g17,g4)
    c: Coincident(g0,g17)
    c: DistanceX(g3) = 9.5
    c: DistanceX(g3,g3) = 14.25
    c: Vertical(g2)
    c: DistanceY(g3) = 25
    c: DistanceY(g4) = 22
    c: DistanceY(g4,g1) = 0
    c: DistanceX(g4,g0) = 2.25
    c: DistanceX(g0,g1) = 2.25
    c: Horizontal(g10)
    c: Vertical(g5)
    c: Vertical(g11)
    c: DistanceX(g5) = 40
    c: DistanceX(g5,g9) = 11.2
    c: DistanceY(g11,g9) = 0
    c: DistanceY(g5,g5) = 2.5
    c: DistanceY(g8,g5) = 0
    c: DistanceY(g11,g8) = 0
    c: DistanceY(g14,g11) = 0
    c: DistanceY(g6,g5) = 2.5
    c: DistanceX(g5,g6) = 2.5
    c: DistanceX(g7,g8) = 2.5
    c: DistanceX(g9,g11) = 1.25
    c: DistanceY(g12,g7) = 0
    c: DistanceX(g11,g12) = 2.5
    c: DistanceX(g13,g14) = 2.5
    c: DistanceX(g11,g15) = 11.2
    c: DistanceY(g0,g4) = 2.5
    c: DistanceY(g5) = 24.5
    c: Coincident(g19,g18)
    c: Vertical(g19)
    c: Horizontal(g20)
    c: Coincident(g21,g20)
    c: Coincident(g23,g19)
    c: Coincident(g24,g23)
    c: Coincident(g24,g22)
    c: Horizontal(g24)
    c: Coincident(g25,g21)
    c: Coincident(g25,g22)
    c: Vertical(g25)
    c: Coincident(g18,g20)
    c: Radius(g18) = 1
    c: Angle(g18) = 1.5708
    c: Angle(g21) = 1.5708
    c: Angle(g22) = 1.5708
    c: Angle(g23) = 1.5708
    c: DistanceX(g23) = 12.3
    c: DistanceY(g23) = 13.2
    c: DistanceX(g19) = 11.3
    c: DistanceY(g23,g19) = 0
    c: DistanceY(g18,g18) = 0
    c: DistanceX(g21,g20) = 0
    c: Radius(g21) = 1
    c: Radius(g22) = 1
    c: DistanceX(g22,g22) = 0
    c: DistanceX(g18,g20) = 4.5
    c: DistanceX(g26) = 18.9
    c: Radius(g26) = 0.5
    c: DistanceY(g26) = 16.475
    c: DistanceX(g26,g27) = 2.19
    c: DistanceY(g26,g27) = 0
    c: DistanceY(g28,g27) = 0
    c: DistanceY(g29,g28) = 0
    c: DistanceX(g27,g28) = 2.19
    c: Radius(g27) = 0.5
    c: Radius(g28) = 0.5
    c: Radius(g29) = 0.5
    c: DistanceX(g28,g29) = 2.19
    c: DistanceY(g23,g18) = 1.25
    c: Horizontal(g30)
    c: Vertical(g31)
    c: Vertical(g33)
    c: Coincident(g33,g34)
    c: Coincident(g33,g37)
    c: Coincident(g32,g37)
    c: Coincident(g32,g36)
    c: Coincident(g31,g36)
    c: Coincident(g31,g35)
    c: Coincident(g30,g35)
    c: Coincident(g30,g34)
    c: Angle(g34) = 1.5708
    c: Angle(g35) = 1.5708
    c: Angle(g37) = 1.5708
    c: Angle(g36) = 1.5708
    c: DistanceY(g18,g34) = 0
    c: DistanceY(g34,g33) = 0
    c: Radius(g34) = 1
    c: DistanceY(g33,g37) = 0
    c: Radius(g37) = 1
    c: Radius(g36) = 1
    c: Radius(g35) = 1
    c: DistanceY(g33,g23) = 0
    c: DistanceY(g31,g36) = 0
    c: Horizontal(g32)
    c: DistanceX(g35,g30) = 0
    c: DistanceX(g32,g32) = 4.5
    c: Vertical(g38)
    c: Horizontal(g39)
    c: Horizontal(g40)
    c: Vertical(g41)
    c: Coincident(g42,g38)
    c: Coincident(g42,g39)
    c: Coincident(g43,g39)
    c: Coincident(g45,g38)
    c: Coincident(g45,g40)
    c: Coincident(g40,g44)
    c: Coincident(g41,g44)
    c: Coincident(g41,g43)
    c: DistanceX(g42) = 53.5
    c: DistanceY(g42) = 15.58
    c: DistanceX(g42,g45) = 0
    c: DistanceY(g45,g42) = 1
    c: Radius(g42) = 1.25
    c: Radius(g44) = 1.25
    c: Radius(g43) = 1.25
    c: DistanceX(g45,g40) = 0
    c: DistanceX(g42,g39) = 0
    c: DistanceY(g42,g43) = 0
    c: DistanceY(g44,g45) = 0
    c: DistanceY(g45,g38) = 0
    c: DistanceX(g42,g43) = 7
    c: DistanceX(g18,g34) = 32.5
    c: DistanceY(g41,g44) = 0
    c: DistanceY(g43,g41) = 0
    c: Angle(g42) = 1.5708
FEATURE [Part::Extrusion] Extrude372  label="lightBottomCutDone016"
  Base = -> Sketch379
  Dir = (0,-1,2e-16)
  DirMode = 2
  FaceMakerClass = Part::FaceMakerBullseye
  FaceMakerMode = 3
  LengthFwd = 5
  LengthRev = 0
  Placement = pos=(0,2,0) rot=(0,0,1;0rad)
  Solid = true
  Symmetric = false
FEATURE [Sketcher::SketchObject] Sketch380
  ArcFitTolerance = 0
  FullyConstrained = true
  MakeInternals = false
  Placement = pos=(0,0,0) rot=(1,0,0;1.5708rad)
  sketch-geometry (8):
    g0: ArcOfCircle CenterX=11.8 CenterY=15.45 CenterZ=0 NormalX=0 NormalY=0 NormalZ=1 AngleXU=0 Radius=1.25 StartAngle=1.5708 EndAngle=3.14159
    g1: ArcOfCircle CenterX=17.3 CenterY=15.45 CenterZ=0 NormalX=0 NormalY=0 NormalZ=1 AngleXU=0 Radius=1.25 StartAngle=-9e-16 EndAngle=1.5708
    g2: ArcOfCircle CenterX=16.8 CenterY=14.2 CenterZ=0 NormalX=0 NormalY=0 NormalZ=1 AngleXU=0 Radius=1.75 StartAngle=4.71239 EndAngle=6.28319
    g3: ArcOfCircle CenterX=12.3 CenterY=14.2 CenterZ=0 NormalX=0 NormalY=0 NormalZ=1 AngleXU=0 Radius=1.75 StartAngle=3.14159 EndAngle=4.71239
    g4: LineSegment StartX=11.8 StartY=16.7 StartZ=0 EndX=17.3 EndY=16.7 EndZ=0
    g5: LineSegment StartX=18.55 StartY=15.45 StartZ=0 EndX=18.55 EndY=14.2 EndZ=0
    g6: LineSegment StartX=16.8 StartY=12.45 StartZ=0 EndX=12.3 EndY=12.45 EndZ=0
    g7: LineSegment StartX=10.55 StartY=14.2 StartZ=0 EndX=10.55 EndY=15.45 EndZ=0
  constraints (28):
    c: Coincident(g4,g0)
    c: Coincident(g4,g1)
    c: Horizontal(g4)
    c: Coincident(g5,g1)
    c: Coincident(g5,g2)
    c: Coincident(g6,g2)
    c: Coincident(g6,g3)
    c: Horizontal(g6)
    c: Coincident(g7,g3)
    c: Coincident(g7,g0)
    c: Vertical(g7)
    c: Radius(g0) = 1.25
    c: DistanceY(g0,g0) = 0
    c: Angle(g3) = 1.5708
    c: DistanceY(g3,g3) = 0
    c: DistanceY(g3,g0) = 1.25
    c: DistanceY(g3) = 14.2
    c: Radius(g3) = 1.75
    c: Radius(g2) = 1.75
    c: Radius(g1) = 1.25
    c: DistanceX(g6,g6) = 4.5
    c: DistanceX(g3) = 12.3
    c: DistanceY(g1,g1) = 0
    c: DistanceX(g2,g2) = 0
    c: Angle(g1) = 1.5708
    c: Angle(g2) = 1.5708
    c: Vertical(g5)
    c: DistanceX(g0,g0) = 0
FEATURE [Part::Extrusion] Extrude374  label="buttonCuts033"
  Base = -> Sketch380
  Dir = (0,-1,2e-16)
  DirMode = 2
  FaceMakerClass = Part::FaceMakerBullseye
  FaceMakerMode = 3
  LengthFwd = 0.6
  LengthRev = 0
  Placement = pos=(32.5,2,0) rot=(0,0,1;0rad)
  Solid = true
  Symmetric = false
FEATURE [Sketcher::SketchObject] Sketch381
  ArcFitTolerance = 0
  FullyConstrained = true
  MakeInternals = false
  Placement = pos=(0,0,0) rot=(1,0,0;1.5708rad)
  sketch-geometry (8):
    g0: ArcOfCircle CenterX=11.8 CenterY=15.45 CenterZ=0 NormalX=0 NormalY=0 NormalZ=1 AngleXU=0 Radius=1.25 StartAngle=1.5708 EndAngle=3.14159
    g1: ArcOfCircle CenterX=17.3 CenterY=15.45 CenterZ=0 NormalX=0 NormalY=0 NormalZ=1 AngleXU=0 Radius=1.25 StartAngle=-9e-16 EndAngle=1.5708
    g2: ArcOfCircle CenterX=16.8 CenterY=14.2 CenterZ=0 NormalX=0 NormalY=0 NormalZ=1 AngleXU=0 Radius=1.75 StartAngle=4.71239 EndAngle=6.28319
    g3: ArcOfCircle CenterX=12.3 CenterY=14.2 CenterZ=0 NormalX=0 NormalY=0 NormalZ=1 AngleXU=0 Radius=1.75 StartAngle=3.14159 EndAngle=4.71239
    g4: LineSegment StartX=11.8 StartY=16.7 StartZ=0 EndX=17.3 EndY=16.7 EndZ=0
    g5: LineSegment StartX=18.55 StartY=15.45 StartZ=0 EndX=18.55 EndY=14.2 EndZ=0
    g6: LineSegment StartX=16.8 StartY=12.45 StartZ=0 EndX=12.3 EndY=12.45 EndZ=0
    g7: LineSegment StartX=10.55 StartY=14.2 StartZ=0 EndX=10.55 EndY=15.45 EndZ=0
  constraints (28):
    c: Coincident(g4,g0)
    c: Coincident(g4,g1)
    c: Horizontal(g4)
    c: Coincident(g5,g1)
    c: Coincident(g5,g2)
    c: Coincident(g6,g2)
    c: Coincident(g6,g3)
    c: Horizontal(g6)
    c: Coincident(g7,g3)
    c: Coincident(g7,g0)
    c: Vertical(g7)
    c: Radius(g0) = 1.25
    c: DistanceY(g0,g0) = 0
    c: Angle(g3) = 1.5708
    c: DistanceY(g3,g3) = 0
    c: DistanceY(g3,g0) = 1.25
    c: DistanceY(g3) = 14.2
    c: Radius(g3) = 1.75
    c: Radius(g2) = 1.75
    c: Radius(g1) = 1.25
    c: DistanceX(g6,g6) = 4.5
    c: DistanceX(g3) = 12.3
    c: DistanceY(g1,g1) = 0
    c: DistanceX(g2,g2) = 0
    c: Angle(g1) = 1.5708
    c: Angle(g2) = 1.5708
    c: Vertical(g5)
    c: DistanceX(g0,g0) = 0
FEATURE [Part::Extrusion] Extrude373  label="buttonCuts032"
  Base = -> Sketch381
  Dir = (0,-1,2e-16)
  DirMode = 2
  FaceMakerClass = Part::FaceMakerBullseye
  FaceMakerMode = 3
  LengthFwd = 0.6
  LengthRev = 0
  Placement = pos=(0,2,0) rot=(0,0,1;0rad)
  Solid = true
  Symmetric = false
FEATURE [Part::MultiFuse] Fusion507  label="bottomButtonCuts018"
  Shapes = -> [Extrude374,Extrude373]
FEATURE [Part::MultiFuse] Fusion508  label="baseCuts005"
  Placement = pos=(166,5.5,-78) rot=(1,0,0;1.5708rad)
  Shapes = -> [Extrude372,Fusion507]
FEATURE [Part::Cut] Cut068  label="base045"
  Base = -> Cut067
  Tool = -> Fusion508
FEATURE [Sketcher::SketchObject] Sketch382
  ArcFitTolerance = 0
  FullyConstrained = true
  MakeInternals = false
  Placement = pos=(0,-4,0) rot=(1,0,0;1.5708rad)
  sketch-geometry (8):
    g0: LineSegment StartX=165 StartY=-68.75 StartZ=0 EndX=169 EndY=-68.75 EndZ=0
    g1: LineSegment StartX=169 StartY=-68.75 StartZ=0 EndX=169 EndY=-76 EndZ=0
    g2: LineSegment StartX=169 StartY=-76 StartZ=0 EndX=165 EndY=-76 EndZ=0
    g3: LineSegment StartX=165 StartY=-76 StartZ=0 EndX=165 EndY=-68.75 EndZ=0
    g4: LineSegment StartX=236 StartY=-68.75 StartZ=0 EndX=240 EndY=-68.75 EndZ=0
    g5: LineSegment StartX=240 StartY=-68.75 StartZ=0 EndX=240 EndY=-76 EndZ=0
    g6: LineSegment StartX=240 StartY=-76 StartZ=0 EndX=236 EndY=-76 EndZ=0
    g7: LineSegment StartX=236 StartY=-76 StartZ=0 EndX=236 EndY=-68.75 EndZ=0
  constraints (24):
    c: Coincident(g0,g1)
    c: Coincident(g1,g2)
    c: Coincident(g2,g3)
    c: Coincident(g3,g0)
    c: Horizontal(g0)
    c: Horizontal(g2)
    c: Vertical(g1)
    c: Vertical(g3)
    c: DistanceX(g2) = 165
    c: DistanceY(g2) = -76
    c: DistanceY(g1,g1) = 7.25
    c: DistanceX(g2,g1) = 4
    c: Coincident(g4,g5)
    c: Coincident(g5,g6)
    c: Coincident(g6,g7)
    c: Coincident(g7,g4)
    c: Horizontal(g4)
    c: Horizontal(g6)
    c: Vertical(g5)
    c: Vertical(g7)
    c: DistanceX(g5) = 240
    c: DistanceX(g4,g4) = 4
    c: Horizontal(g4,g0)
    c: Horizontal(g6,g1)
FEATURE [Part::Extrusion] Extrude375
  Base = -> Sketch382
  Dir = (0,-1,2e-16)
  DirMode = 2
  FaceMakerClass = Part::FaceMakerBullseye
  FaceMakerMode = 3
  LengthFwd = 12.2
  LengthRev = 0
  Solid = true
  Symmetric = false
FEATURE [Part::MultiFuse] Fusion509  label="base054"
  Shapes = -> [Cut068,Extrude375]
FEATURE [Sketcher::SketchObject] Sketch383
  ArcFitTolerance = 0
  FullyConstrained = true
  MakeInternals = false
  Placement = pos=(0,0,0) rot=(1,0,0;1.5708rad)
  sketch-geometry (16):
    g0: Circle CenterX=173.65 CenterY=40.16 CenterZ=0 NormalX=0 NormalY=0 NormalZ=1 AngleXU=0 Radius=5
    g1: Circle CenterX=186.35 CenterY=40.16 CenterZ=0 NormalX=0 NormalY=0 NormalZ=1 AngleXU=0 Radius=5
    g2: Circle CenterX=173.65 CenterY=19.84 CenterZ=0 NormalX=0 NormalY=0 NormalZ=1 AngleXU=0 Radius=5
    g3: Circle CenterX=186.35 CenterY=19.84 CenterZ=0 NormalX=0 NormalY=0 NormalZ=1 AngleXU=0 Radius=5
    g4: Circle CenterX=218.9 CenterY=19.84 CenterZ=0 NormalX=0 NormalY=0 NormalZ=1 AngleXU=0 Radius=5
    g5: Circle CenterX=231.6 CenterY=19.84 CenterZ=0 NormalX=0 NormalY=0 NormalZ=1 AngleXU=0 Radius=5
    g6: Circle CenterX=231.6 CenterY=40.16 CenterZ=0 NormalX=0 NormalY=0 NormalZ=1 AngleXU=0 Radius=5
    g7: Circle CenterX=218.9 CenterY=40.16 CenterZ=0 NormalX=0 NormalY=0 NormalZ=1 AngleXU=0 Radius=5
    g8: Circle CenterX=173.65 CenterY=19.84 CenterZ=0 NormalX=0 NormalY=0 NormalZ=1 AngleXU=0 Radius=1.125
    g9: Circle CenterX=186.35 CenterY=19.84 CenterZ=0 NormalX=0 NormalY=0 NormalZ=1 AngleXU=0 Radius=1.125
    g10: Circle CenterX=186.35 CenterY=40.16 CenterZ=0 NormalX=0 NormalY=0 NormalZ=1 AngleXU=0 Radius=1.125
    g11: Circle CenterX=173.65 CenterY=40.16 CenterZ=0 NormalX=0 NormalY=0 NormalZ=1 AngleXU=0 Radius=1.125
    g12: Circle CenterX=218.9 CenterY=40.16 CenterZ=0 NormalX=0 NormalY=0 NormalZ=1 AngleXU=0 Radius=1.125
    g13: Circle CenterX=231.6 CenterY=40.16 CenterZ=0 NormalX=0 NormalY=0 NormalZ=1 AngleXU=0 Radius=1.125
    g14: Circle CenterX=218.9 CenterY=19.84 CenterZ=0 NormalX=0 NormalY=0 NormalZ=1 AngleXU=0 Radius=1.125
    g15: Circle CenterX=231.6 CenterY=19.84 CenterZ=0 NormalX=0 NormalY=0 NormalZ=1 AngleXU=0 Radius=1.125
  constraints (34):
    c: DistanceY(g1,g0) = 0
    c: DistanceX(g0) = 173.65
    c: DistanceY(g0) = 40.16
    c: DistanceY(g2,g0) = 20.32
    c: Horizontal(g2,g3)
    c: Vertical(g3,g1)
    c: Horizontal(g1,g7)
    c: Horizontal(g7,g6)
    c: Horizontal(g4,g3)
    c: Horizontal(g3,g5)
    c: Equal(g0, g1-g7) x7
    c: Diameter(g0) = 10
    c: DistanceX(g1,g7) = 32.55
    c: DistanceX(g0,g1) = 12.7
    c: Vertical(g2,g0)
    c: DistanceX(g7,g6) = 12.7
    c: Vertical(g4,g7)
    c: Vertical(g5,g6)
    c: Coincident(g8,g2)
    c: Coincident(g9,g3)
    c: Coincident(g10,g1)
    c: Coincident(g11,g0)
    c: Coincident(g12,g7)
    c: Coincident(g13,g6)
    c: Coincident(g14,g4)
    c: Coincident(g15,g5)
    c: Equal(g8,g9)
    c: Equal(g8,g11)
    c: Equal(g8,g10)
    c: Equal(g8,g12)
    c: Equal(g8,g14)
    c: Equal(g8,g15)
    c: Equal(g8,g13)
    c: Diameter(g8) = 2.25
FEATURE [Part::Extrusion] Extrude376  label="i2cMounts002"
  Base = -> Sketch383
  Dir = (0,-1,2e-16)
  DirMode = 2
  FaceMakerClass = Part::FaceMakerBullseye
  FaceMakerMode = 3
  LengthFwd = 10
  LengthRev = 0
  Solid = true
  Symmetric = false
FEATURE [Part::MultiFuse] Fusion544  label="base055"
  Shapes = -> [Extrude376,Fusion509]
FEATURE [Part::Cut] Cut069  label="base046"
  Base = -> Fusion544
  Tool = -> Fusion543
FEATURE [Part::Cut] Cut059
  Base = -> Cut069
  Refine = true
  Tool = -> Cylinder100
FEATURE [Sketcher::SketchObject] Sketch384
  ArcFitTolerance = 0
  FullyConstrained = true
  MakeInternals = false
  Placement = pos=(0,0,0) rot=(1,0,0;1.5708rad)
  sketch-geometry (4):
    g0: ArcOfCircle CenterX=233.5 CenterY=-58 CenterZ=0 NormalX=0 NormalY=0 NormalZ=1 AngleXU=0 Radius=4 StartAngle=1e-16 EndAngle=3.14159
    g1: ArcOfCircle CenterX=233.5 CenterY=-62 CenterZ=0 NormalX=0 NormalY=0 NormalZ=1 AngleXU=0 Radius=4 StartAngle=3.14159 EndAngle=6.28319
    g2: LineSegment StartX=229.5 StartY=-58 StartZ=0 EndX=229.5 EndY=-62 EndZ=0
    g3: LineSegment StartX=237.5 StartY=-62 StartZ=0 EndX=237.5 EndY=-58 EndZ=0
  constraints (10):
    c: Tangent(g0,g2) = -1.5708
    c: Tangent(g2,g1) = -1.5708
    c: Tangent(g1,g3) = -1.5708
    c: Tangent(g3,g0) = -1.5708
    c: Equal(g0,g1)
    c: Vertical(g2)
    c: DistanceX(g1) = 237.5
    c: DistanceX(g1,g1) = 8
    c: DistanceY(g1,g0) = 4
    c: DistanceY(g1) = -62
FEATURE [Part::Extrusion] Extrude377  label="baseWireCut003"
  Base = -> Sketch384
  Dir = (0,-1,2e-16)
  DirMode = 2
  FaceMakerClass = Part::FaceMakerBullseye
  FaceMakerMode = 3
  LengthFwd = 4
  LengthRev = 0
  Solid = true
  Symmetric = false
FEATURE [Part::Cut] Cut070
  Base = -> Cut059
  Refine = true
  Tool = -> Extrude377
FEATURE [Sketcher::SketchObject] Sketch385  label="wireProtector001"
  ArcFitTolerance = 1e-06
  FullyConstrained = true
  MakeInternals = false
  Placement = pos=(0,0,-76) rot=(0,0,1;0rad)
  sketch-geometry (8):
    g0: LineSegment StartX=200.9 StartY=-23.75 StartZ=0 EndX=200.9 EndY=0 EndZ=0
    g1: LineSegment StartX=200.9 StartY=0 StartZ=0 EndX=203.4 EndY=0 EndZ=0
    g2: LineSegment StartX=203.4 StartY=0 StartZ=0 EndX=203.4 EndY=-21.25 EndZ=0
    g3: LineSegment StartX=234.75 StartY=-23.75 StartZ=0 EndX=234.75 EndY=0 EndZ=0
    g4: LineSegment StartX=234.75 StartY=0 StartZ=0 EndX=232.25 EndY=0 EndZ=0
    g5: LineSegment StartX=232.25 StartY=0 StartZ=0 EndX=232.25 EndY=-21.25 EndZ=0
    g6: LineSegment StartX=200.9 StartY=-23.75 StartZ=0 EndX=234.75 EndY=-23.75 EndZ=0
    g7: LineSegment StartX=232.25 StartY=-21.25 StartZ=0 EndX=203.4 EndY=-21.25 EndZ=0
  constraints (24):
    c: Vertical(g0)
    c: Coincident(g2,g1)
    c: Vertical(g2)
    c: Vertical(g3)
    c: Coincident(g4,g3)
    c: Horizontal(g4)
    c: Coincident(g5,g4)
    c: Vertical(g5)
    c: Horizontal(g1)
    c: Coincident(g0,g1)
    c: DistanceY(g0) = 0
    c: Horizontal(g4,g1)
    c: DistanceX(g0,g1) = 2.5
    c: DistanceY(g2,g0) = -2.5
    c: DistanceY(g2,g2) = 21.25
    c: Horizontal(g5,g2)
    c: Horizontal(g3,g0)
    c: DistanceX(g5,g3) = 2.5
    c: Coincident(g6,g0)
    c: Coincident(g6,g3)
    c: Coincident(g7,g5)
    c: Coincident(g7,g2)
    c: DistanceX(g2) = 203.4
    c: DistanceX(g5) = 232.25
FEATURE [Part::Extrusion] Extrude378
  Base = -> Sketch385
  Dir = (0,0,1)
  DirMode = 2
  FaceMakerClass = Part::FaceMakerBullseye
  FaceMakerMode = 3
  LengthFwd = 12
  LengthRev = 0
  Reversed = true
  Solid = true
  Symmetric = false
FEATURE [Part::Fillet] Fillet094  label="wireCover001"
  Base = -> Extrude378
  EdgeLinks = -> Extrude378 [Edge1,Edge2,Edge11,Edge14]
  Edges = 4 edges r=3.25: [Edge1,Edge2,Edge11,Edge14]
FEATURE [Part::Fillet] Fillet095
  Base = -> Fillet094
  EdgeLinks = -> Fillet094 [Edge4,Edge17,Edge19,Edge20,Edge21,Edge22,Edge23,Edge24,Edge25,Edge26,Edge27,Edge28]
  Edges = 12 edges r=1: [Edge4,Edge17,Edge19,Edge20,Edge21,Edge22,Edge23,Edge24,Edge25,Edge26,Edge27,Edge28]
FEATURE [Part::MultiFuse] Fusion468  label="BaseGuard"
  Refine = true
  Shapes = -> [Cut070,Fillet095]
FEATURE [Part::Fillet] Fillet091  label="sensorBase005"
  Base = -> Fusion468
  EdgeLinks = -> Fusion468 [Edge731,Edge732,Edge734,Edge736,Edge738,Edge742,Edge744,Edge745,Edge746,Edge753,Edge754,Edge755,Edge756,Edge757,Edge758,Edge759,Edge767,Edge768,Edge769,Edge770,Edge772,Edge773,Edge774,Edge775,Edge776,Edge777,Edge778,Edge779,Edge780,Edge781,Edge794,Edge795,Edge796,Edge798,Edge801,Edge803,Edge804,Edge805,Edge807,Edge808,+68 more]
  Edges = 108 edges: [Edge731 r=1,Edge732 r=1,Edge734 r=1,Edge736 r=1,Edge738 r=1,Edge742 r=1,Edge744 r=1,Edge745 r=1,Edge746 r=1,Edge753 r=1,Edge754 r=1,Edge755 r=1,Edge756 r=1,Edge757 r=1,Edge758 r=1,Edge759 r=1,Edge767 r=1,Edge768 r=1,Edge769 r=1,Edge770 r=1,Edge772 r=1,Edge773 r=1,Edge774 r=1,Edge775 r=1,Edge776 r=1,Edge777 r=1,Edge778 r=1,Edge779 r=1,Edge780 r=1,Edge781 r=1,Edge794 r=1,Edge795 r=1,Edge796 r=1,Edge798 r=1,Edge801 r=1,Edge803 r=1,Edge804 r=1,Edge805 r=1,Edge807 r=1,Edge808 r=1,Edge809 r=1,Edge811 r=1,Edge812 r=1,Edge813 r=1,Edge814 r=1,Edge815 r=1,Edge817 r=1,Edge818 r=1,Edge819 r=1,Edge820 r=1,+58 more]
FEATURE [Part::Compound] Compound022  label="prints"
  Links = -> [Fillet077,Fillet084,Fillet072,Cut036,Fusion385,Tube,Cylinder095,Tube001,Fusion463,Cut051,Cylinder099,Fillet091]
